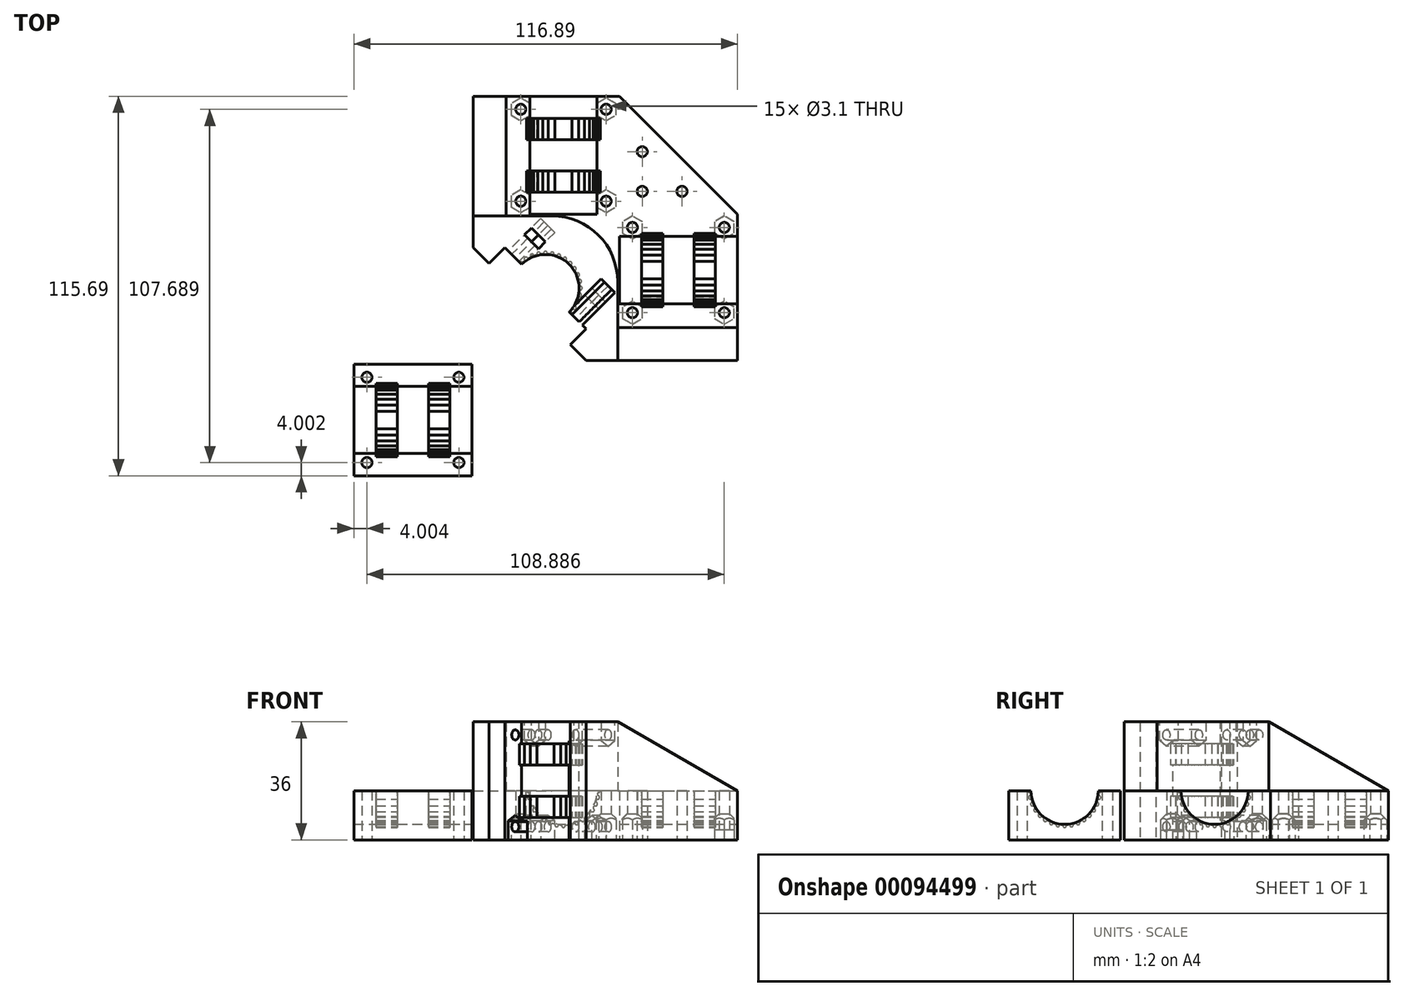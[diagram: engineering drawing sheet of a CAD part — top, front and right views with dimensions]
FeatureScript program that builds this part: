
annotation { "Feature Type Name" : "Feature", "Feature Type Description" : "" }
export const myFeature = defineFeature(function(context is Context, id is Id, definition is map)
    precondition{}
    {
        {
            var Q0;
            Q0=qCreatedBy(makeId("Top.planeOp"),FACE);
            var sketch = newSketch(context, id + "F0", { "sketchPlane" : qUnion([Q0])});
            skLineSegment(sketch, "E0.bottom", {"start": v(34, 0) * mm, "end": v(70, 0) * mm});
            skLineSegment(sketch, "E0.top", {"start": v(34, 34) * mm, "end": v(70, 34) * mm});
            skLineSegment(sketch, "E0.left", {"start": v(34, 0) * mm, "end": v(34, 34) * mm});
            skLineSegment(sketch, "E0.right", {"start": v(70, 0) * mm, "end": v(70, 34) * mm});
            skLineSegment(sketch, "E1", {"start": v(52, 34) * mm, "end": v(52, 0) * mm, "construction": true});
            skLineSegment(sketch, "E2", {"start": v(34, 17) * mm, "end": v(70, 17) * mm, "construction": true});
            skLineSegment(sketch, "E3", {"start": v(34, 34) * mm, "end": v(34, 70) * mm});
            skLineSegment(sketch, "E4", {"start": v(34, 70) * mm, "end": v(0, 70) * mm});
            skLineSegment(sketch, "E5", {"start": v(0, 70) * mm, "end": v(0, 34) * mm});
            skLineSegment(sketch, "E6", {"start": v(0, 34) * mm, "end": v(34, 34) * mm});
            skLineSegment(sketch, "E7", {"start": v(17, 70) * mm, "end": v(17, 34) * mm, "construction": true});
            skLineSegment(sketch, "E8", {"start": v(0, 52) * mm, "end": v(34, 52) * mm, "construction": true});
            skCircle(sketch, "E9", {"center": v(66, 30) * mm, "radius": 1.55 * mm});
            skPoint(sketch, "E10", {"position": v(60, 17) * mm});
            skCircle(sketch, "E11.MirrorC", {"center": v(38, 30) * mm, "radius": 1.55 * mm});
            skPoint(sketch, "E12.MirrorP", {"position": v(44, 17) * mm});
            skCircle(sketch, "E13.MirrorC", {"center": v(38, 4) * mm, "radius": 1.55 * mm});
            skCircle(sketch, "E14.MirrorC", {"center": v(66, 4) * mm, "radius": 1.55 * mm});
            skCircle(sketch, "E15", {"center": v(30, 66) * mm, "radius": 1.55 * mm});
            skPoint(sketch, "E16", {"position": v(17, 60) * mm});
            skCircle(sketch, "E17.MirrorC", {"center": v(4, 66) * mm, "radius": 1.55 * mm});
            skCircle(sketch, "E18.MirrorC", {"center": v(30, 38) * mm, "radius": 1.55 * mm});
            skPoint(sketch, "E19.MirrorP", {"position": v(17, 44) * mm});
            skCircle(sketch, "E20.MirrorC", {"center": v(4, 38) * mm, "radius": 1.55 * mm});
            skLineSegment(sketch, "E21", {"start": v(34, 70) * mm, "end": v(70, 34) * mm});
            skLineSegment(sketch, "E22", {"start": v(0, 70) * mm, "end": v(-0.5, 70) * mm});
            skLineSegment(sketch, "E23", {"start": v(-0.5, 70) * mm, "end": v(-0.5, 34) * mm});
            skLineSegment(sketch, "E24", {"start": v(33.5, -0.5) * mm, "end": v(70, -0.5) * mm});
            skLineSegment(sketch, "E25", {"start": v(70, -0.5) * mm, "end": v(70, 0) * mm});
            skLineSegment(sketch, "E26", {"start": v(-0.5, 34) * mm, "end": v(-0.5, 33.5) * mm});
            skLineSegment(sketch, "E27", {"start": v(-0.5, 33.5) * mm, "end": v(33.5, 33.5) * mm});
            skLineSegment(sketch, "E28", {"start": v(33.5, 33.5) * mm, "end": v(33.5, -0.5) * mm});
            skLineSegment(sketch, "E29", {"start": v(-0.5, 33.5) * mm, "end": v(33.5, -0.5) * mm});
            skLineSegment(sketch, "E30.0", {"start": v(41, 41) * mm, "end": v(41, 53.1) * mm, "construction": true});
            skLineSegment(sketch, "E30.1", {"start": v(41, 41) * mm, "end": v(53.1, 41) * mm, "construction": true});
            skLineSegment(sketch, "E30.2", {"start": v(41, 53.1) * mm, "end": v(53.1, 41) * mm, "construction": true});
            skLineSegment(sketch, "E31", {"start": v(70, -0.5) * mm, "end": v(70, -10.5) * mm});
            skLineSegment(sketch, "E32", {"start": v(70, -10.5) * mm, "end": v(33.5, -10.5) * mm});
            skLineSegment(sketch, "E33", {"start": v(33.5, -10.5) * mm, "end": v(-10.5, 33.5) * mm});
            skLineSegment(sketch, "E34", {"start": v(-10.5, 33.5) * mm, "end": v(-10.5, 70) * mm});
            skLineSegment(sketch, "E35", {"start": v(-10.5, 70) * mm, "end": v(-0.5, 70) * mm});
            skLineSegment(sketch, "E36", {"start": v(34, 34) * mm, "end": v(0, 0) * mm, "construction": true});
            skPoint(sketch, "E37", {"position": v(-0.87, 23.87) * mm});
            skPoint(sketch, "E38.MirrorP", {"position": v(23.87, -0.87) * mm});
            skLineSegment(sketch, "E39", {"start": v(33.5, -10.5) * mm, "end": v(23.87, -10.5) * mm});
            skLineSegment(sketch, "E40", {"start": v(23.87, -10.5) * mm, "end": v(23.87, -0.87) * mm});
            skLineSegment(sketch, "E41", {"start": v(-10.5, 33.5) * mm, "end": v(-10.5, 23.87) * mm});
            skLineSegment(sketch, "E42", {"start": v(-10.5, 23.87) * mm, "end": v(-0.87, 23.87) * mm});
            skLineSegment(sketch, "E43", {"start": v(23.87, -10.5) * mm, "end": v(19.06, -5.69) * mm});
            skLineSegment(sketch, "E44", {"start": v(19.06, -5.69) * mm, "end": v(23.87, -0.87) * mm});
            skLineSegment(sketch, "E45", {"start": v(-10.5, 23.87) * mm, "end": v(-5.69, 19.06) * mm});
            skLineSegment(sketch, "E46", {"start": v(-5.69, 19.06) * mm, "end": v(-0.87, 23.87) * mm});
            skCircle(sketch, "E47", {"center": v(41, 41) * mm, "radius": 1.55 * mm});
            skCircle(sketch, "E48", {"center": v(53.1, 41) * mm, "radius": 1.55 * mm});
            skCircle(sketch, "E49", {"center": v(41, 53.1) * mm, "radius": 1.55 * mm});
            skSolve(sketch);
        }
        {
            var Q0;
            Q0=makeQuery(id+"F0.imprint","IMPRINT",FACE,{"disambiguationData":[TD([[makeQuery(id+"F0.imprint","IMPRINT",EDGE,{"derivedFrom":sQuery(id+"F0.wireOp",EDGE,"E3")}),1.0]])]});
            var Q1;
            Q1=makeQuery(id+"F0.imprint","IMPRINT",FACE,{"disambiguationData":[TD([[makeQuery(id+"F0.imprint","IMPRINT",EDGE,{"derivedFrom":sQuery(id+"F0.wireOp",EDGE,"E0.bottom")}),1.0]])]});
            var Q2;
            Q2=makeQuery(id+"F0.imprint","IMPRINT",FACE,{"disambiguationData":[TD([[makeQuery(id+"F0.imprint","IMPRINT",EDGE,{"derivedFrom":sQuery(id+"F0.wireOp",EDGE,"E0.top")}),1.0]])]});
            var Q3;
            Q3=makeQuery(id+"F0.imprint","IMPRINT",FACE,{"disambiguationData":[TD([[makeQuery(id+"F0.imprint","IMPRINT",EDGE,{"derivedFrom":sQuery(id+"F0.wireOp",EDGE,"E0.bottom")}),-1.0]])]});
            extrude(context, id + "F1", {"entities" : qUnion([Q0, Q1, Q2, Q3]), "depth" : 15 * mm});
        }
        {
            var Q0;
            Q0=makeQuery(id+"F0.imprint","IMPRINT",FACE,{"disambiguationData":[TD([[makeQuery(id+"F0.imprint","IMPRINT",EDGE,{"derivedFrom":sQuery(id+"F0.wireOp",EDGE,"E27")}),-1.0]])]});
            var Q1;
            Q1=makeQuery(id+"F0.imprint","IMPRINT",FACE,{"disambiguationData":[TD([[makeQuery(id+"F0.imprint","IMPRINT",EDGE,{"derivedFrom":sQuery(id+"F0.wireOp",EDGE,"E23")}),-1.0]])]});
            var Q2;
            {var subQ0=sQuery(id+"F0.wireOp",EDGE,"E41");Q2=makeQuery(id+"F0.imprint","IMPRINT",FACE,{"disambiguationData":[TD([[makeQuery(id+"F0.imprint","IMPRINT",EDGE,{"derivedFrom":subQ0}),1.0]])]});}
            var Q3;
            {var subQ0=sQuery(id+"F0.wireOp",EDGE,"E39");Q3=makeQuery(id+"F0.imprint","IMPRINT",FACE,{"disambiguationData":[TD([[makeQuery(id+"F0.imprint","IMPRINT",EDGE,{"derivedFrom":subQ0}),-1.0]])]});}
            var Q4;
            Q4=makeQuery(id+"F0.imprint","IMPRINT",FACE,{"disambiguationData":[TD([[makeQuery(id+"F0.imprint","IMPRINT",EDGE,{"derivedFrom":sQuery(id+"F0.wireOp",EDGE,"E40")}),1.0]])]});
            var Q5;
            Q5=makeQuery(id+"F0.imprint","IMPRINT",FACE,{"disambiguationData":[TD([[makeQuery(id+"F0.imprint","IMPRINT",EDGE,{"derivedFrom":sQuery(id+"F0.wireOp",EDGE,"E42")}),-1.0]])]});
            extrude(context, id + "F2", {"entities" : qUnion([Q0, Q1, Q2, Q3, Q4, Q5]), "operationType" : NewBodyOperationType.ADD, "depth" : 36 * mm});
        }
        {
            var Q0;
            Q0=makeQuery(id+"F1.opExtrude","SWEPT_FACE",FACE,{"disambiguationData":[OSD([sQuery(id+"F0.wireOp",EDGE,"E0.right"),sQuery(id+"F0.wireOp",EDGE,"E25")])]});
            var sketch = newSketch(context, id + "F3", { "sketchPlane" : qUnion([Q0])});
            skLineSegment(sketch, "E50.0", {"start": v(5.55, 15) * mm, "end": v(2.45, 15) * mm});
            skLineSegment(sketch, "E51.0", {"start": v(28.45, 15) * mm, "end": v(31.55, 15) * mm});
            skLineSegment(sketch, "E52", {"start": v(5.55, 15) * mm, "end": v(28.45, 15) * mm});
            skPoint(sketch, "E53", {"position": v(17, 15) * mm});
            skArc(sketch, "E54", {"start": v(6.75, 15) * mm, "mid": v(17, 4.75) * mm, "end": v(27.25, 15) * mm});
            skSolve(sketch);
        }
        {
            var Q0;
            Q0 = qSketchRegion(id + "F3", true);
            var Q1;
            Q1=makeQuery(id+"F2.opExtrude","SWEPT_FACE",FACE,{"disambiguationData":[OSD([sQuery(id+"F0.wireOp",EDGE,"E28")])]});
            extrude(context, id + "F4", {"entities" : qUnion([Q0]), "operationType" : NewBodyOperationType.REMOVE, "oppositeDirection" : true, "endBoundEntityFace" : qUnion([Q1]), "depth" : 36 * mm});
        }
        {
            var Q0;
            Q0=makeQuery(id+"F1.opExtrude","SWEPT_FACE",FACE,{"disambiguationData":[OSD([sQuery(id+"F0.wireOp",EDGE,"E4"),sQuery(id+"F0.wireOp",EDGE,"E22")])]});
            var sketch = newSketch(context, id + "F5", { "sketchPlane" : qUnion([Q0])});
            skLineSegment(sketch, "E55", {"start": v(-28.45, 15) * mm, "end": v(-5.55, 15) * mm});
            skPoint(sketch, "E56.0.start.orphan", {"position": v(-31.55, 15) * mm});
            skPoint(sketch, "E57.0.start.orphan", {"position": v(-2.45, 15) * mm});
            skPoint(sketch, "E58", {"position": v(-17, 15) * mm});
            skArc(sketch, "E59", {"start": v(-27.25, 15) * mm, "mid": v(-17, 4.75) * mm, "end": v(-6.75, 15) * mm});
            skSolve(sketch);
        }
        {
            var Q0;
            Q0 = qSketchRegion(id + "F5", true);
            var Q1;
            Q1=makeQuery(id+"F2.opExtrude","SWEPT_FACE",FACE,{"disambiguationData":[OSD([sQuery(id+"F0.wireOp",EDGE,"E27")])]});
            extrude(context, id + "F6", {"entities" : qUnion([Q0]), "operationType" : NewBodyOperationType.REMOVE, "oppositeDirection" : true, "endBoundEntityFace" : qUnion([Q1]), "depth" : 36 * mm});
        }
        {
            var Q0;
            Q0=makeQuery(id+"F2.opExtrude","CAP_FACE",FACE,{"disambiguationData":[OSD([sQuery(id+"F0.wireOp",EDGE,"E23"),sQuery(id+"F0.wireOp",EDGE,"E24"),sQuery(id+"F0.wireOp",EDGE,"E26"),sQuery(id+"F0.wireOp",EDGE,"E27"),sQuery(id+"F0.wireOp",EDGE,"E28"),sQuery(id+"F0.wireOp",EDGE,"E31"),sQuery(id+"F0.wireOp",EDGE,"E32"),sQuery(id+"F0.wireOp",EDGE,"E33"),sQuery(id+"F0.wireOp",EDGE,"E34"),sQuery(id+"F0.wireOp",EDGE,"E35")])],"isStart":false});
            var sketch = newSketch(context, id + "F7", { "sketchPlane" : qUnion([Q0])});
            skLineSegment(sketch, "E60.0", {"start": v(-0.87, 23.87) * mm, "end": v(23.87, -0.87) * mm});
            skArc(sketch, "E61", {"start": v(18.75, 4.25) * mm, "mid": v(18.75, 18.75) * mm, "end": v(4.25, 18.75) * mm});
            skSolve(sketch);
        }
        {
            var Q0;
            Q0 = qSketchRegion(id + "F7", true);
            var Q1;
            Q1=makeQuery(id+"F2.opExtrude","CAP_FACE",FACE,{"disambiguationData":[OSD([sQuery(id+"F0.wireOp",EDGE,"E27"),sQuery(id+"F0.wireOp",EDGE,"E28"),sQuery(id+"F0.wireOp",EDGE,"E29")])],"isStart":true});
            extrude(context, id + "F8", {"entities" : qUnion([Q0]), "operationType" : NewBodyOperationType.REMOVE, "endBound" : BoundingType.UP_TO_SURFACE, "oppositeDirection" : true, "endBoundEntityFace" : qUnion([Q1]), "depth" : 25 * mm});
        }
        {
            var Q0;
            {var subQ0=sQuery(id+"F0.wireOp",EDGE,"E44");var subQ8=sQuery(id+"F0.wireOp",EDGE,"E33");Q0=makeQuery(id+"F8.boolean.opBoolean","SPLIT",FACE,{"disambiguationData":[TD([makeQuery(id+"F2.opExtrude","SWEPT_FACE",FACE,{"disambiguationData":[OSD([subQ0])]})])],"derivedFrom":makeQuery(id+"F2.opExtrude","SWEPT_FACE",FACE,{"disambiguationData":[OSD([subQ8])]})});}
            cPlane(context, id + "F9", {"entities" : qUnion([Q0]), "cplaneType" : CPlaneType.OFFSET, "offset" : 7 * mm, "oppositeDirection" : true, "width" : 150 * mm, "height" : 150 * mm});
        }
        {
            var Q0;
            Q0=qCreatedBy(id+"F9.planeOp",FACE);
            var sketch = newSketch(context, id + "F10", { "sketchPlane" : qUnion([Q0])});
            skPoint(sketch, "E62.0", {"position": v(-24.04, 36) * mm});
            skPoint(sketch, "E63.0", {"position": v(24.04, 36) * mm});
            skPoint(sketch, "E64.0", {"position": v(24.04, 0) * mm});
            skPoint(sketch, "E65.0", {"position": v(-24.04, 0) * mm});
            skLineSegment(sketch, "E66", {"start": v(-24.04, 0) * mm, "end": v(-24.04, 36) * mm, "construction": true});
            skLineSegment(sketch, "E67", {"start": v(-24.04, 36) * mm, "end": v(24.04, 36) * mm, "construction": true});
            skLineSegment(sketch, "E68", {"start": v(24.04, 36) * mm, "end": v(24.04, 0) * mm, "construction": true});
            skLineSegment(sketch, "E69", {"start": v(24.04, 0) * mm, "end": v(-24.04, 0) * mm, "construction": true});
            skLineSegment(sketch, "E70", {"start": v(0, 0) * mm, "end": v(0, 36) * mm, "construction": true});
            skLineSegment(sketch, "E71", {"start": v(-24.04, 18) * mm, "end": v(24.04, 18) * mm, "construction": true});
            skCircle(sketch, "E72", {"center": v(-13, 32) * mm, "radius": 1.55 * mm});
            skCircle(sketch, "E73.cCircle", {"center": v(-13, 32) * mm, "radius": 3 * mm, "construction": true});
            skLineSegment(sketch, "E73.0", {"start": v(-10, 33.73) * mm, "end": v(-10, 30.27) * mm});
            skLineSegment(sketch, "E73.1", {"start": v(-10, 30.27) * mm, "end": v(-13, 28.54) * mm});
            skLineSegment(sketch, "E73.2", {"start": v(-13, 28.54) * mm, "end": v(-16, 30.27) * mm});
            skLineSegment(sketch, "E73.3", {"start": v(-16, 30.27) * mm, "end": v(-16, 33.73) * mm});
            skLineSegment(sketch, "E73.4", {"start": v(-16, 33.73) * mm, "end": v(-13, 35.46) * mm, "construction": true});
            skLineSegment(sketch, "E73.5", {"start": v(-13, 35.46) * mm, "end": v(-10, 33.73) * mm, "construction": true});
            skPoint(sketch, "E73.0.midPoint", {"position": v(-10, 32) * mm});
            skLineSegment(sketch, "E74", {"start": v(-16, 33.73) * mm, "end": v(-16, 36) * mm});
            skLineSegment(sketch, "E75", {"start": v(-16, 36) * mm, "end": v(-10, 36) * mm});
            skLineSegment(sketch, "E76", {"start": v(-10, 36) * mm, "end": v(-10, 33.73) * mm});
            skCircle(sketch, "E77.MirrorC", {"center": v(-13, 4) * mm, "radius": 1.55 * mm});
            skLineSegment(sketch, "E78.MirrorCS", {"start": v(-16, 2.27) * mm, "end": v(-16, 0) * mm});
            skLineSegment(sketch, "E79.MirrorCS", {"start": v(-16, 5.73) * mm, "end": v(-16, 2.27) * mm});
            skLineSegment(sketch, "E80.MirrorCS", {"start": v(-13, 7.46) * mm, "end": v(-16, 5.73) * mm});
            skLineSegment(sketch, "E81.MirrorCS", {"start": v(-10, 5.73) * mm, "end": v(-13, 7.46) * mm});
            skLineSegment(sketch, "E82.MirrorCS", {"start": v(-10, 2.27) * mm, "end": v(-10, 5.73) * mm});
            skLineSegment(sketch, "E83.MirrorCS", {"start": v(-10, 0) * mm, "end": v(-10, 2.27) * mm});
            skLineSegment(sketch, "E84.MirrorCS", {"start": v(10, 36) * mm, "end": v(10, 33.73) * mm});
            skLineSegment(sketch, "E85.MirrorCS", {"start": v(10, 33.73) * mm, "end": v(10, 30.27) * mm});
            skLineSegment(sketch, "E86.MirrorCS", {"start": v(10, 30.27) * mm, "end": v(13, 28.54) * mm});
            skLineSegment(sketch, "E87.MirrorCS", {"start": v(13, 28.54) * mm, "end": v(16, 30.27) * mm});
            skLineSegment(sketch, "E88.MirrorCS", {"start": v(16, 30.27) * mm, "end": v(16, 33.73) * mm});
            skLineSegment(sketch, "E89.MirrorCS", {"start": v(16, 33.73) * mm, "end": v(16, 36) * mm});
            skCircle(sketch, "E90.MirrorC", {"center": v(13, 32) * mm, "radius": 1.55 * mm});
            skLineSegment(sketch, "E91.MirrorCS", {"start": v(16, 2.27) * mm, "end": v(16, 0) * mm});
            skLineSegment(sketch, "E92.MirrorCS", {"start": v(16, 5.73) * mm, "end": v(16, 2.27) * mm});
            skLineSegment(sketch, "E93.MirrorCS", {"start": v(13, 7.46) * mm, "end": v(16, 5.73) * mm});
            skLineSegment(sketch, "E94.MirrorCS", {"start": v(10, 5.73) * mm, "end": v(13, 7.46) * mm});
            skLineSegment(sketch, "E95.MirrorCS", {"start": v(10, 2.27) * mm, "end": v(10, 5.73) * mm});
            skLineSegment(sketch, "E96.MirrorCS", {"start": v(10, 0) * mm, "end": v(10, 2.27) * mm});
            skCircle(sketch, "E97.MirrorC", {"center": v(13, 4) * mm, "radius": 1.55 * mm});
            skLineSegment(sketch, "E98", {"start": v(-16, 0) * mm, "end": v(-10, 0) * mm});
            skLineSegment(sketch, "E99", {"start": v(10, 0) * mm, "end": v(16, 0) * mm});
            skLineSegment(sketch, "E100", {"start": v(16, 36) * mm, "end": v(10, 36) * mm});
            skLineSegment(sketch, "E101", {"start": v(-13, 32) * mm, "end": v(-13, 36) * mm, "construction": true});
            skLineSegment(sketch, "E102.0", {"start": v(-10.25, 0) * mm, "end": v(-10.25, 36) * mm, "construction": true});
            skLineSegment(sketch, "E103.0", {"start": v(10.25, 0) * mm, "end": v(10.25, 36) * mm, "construction": true});
            skPoint(sketch, "E104", {"position": v(0, 18) * mm});
            skPoint(sketch, "E105", {"position": v(0, 26) * mm});
            skPoint(sketch, "E106.MirrorP", {"position": v(0, 10) * mm});
            skSolve(sketch);
        }
        {
            var Q0;
            Q0=makeQuery(id+"F10.imprint","IMPRINT",FACE,{"disambiguationData":[TD([[makeQuery(id+"F10.imprint","IMPRINT",EDGE,{"derivedFrom":sQuery(id+"F10.wireOp",EDGE,"E72")}),1.0]])]});
            var Q1;
            Q1=makeQuery(id+"F10.imprint","IMPRINT",FACE,{"disambiguationData":[TD([[makeQuery(id+"F10.imprint","IMPRINT",EDGE,{"derivedFrom":sQuery(id+"F10.wireOp",EDGE,"E77.MirrorC")}),-1.0]])]});
            var Q2;
            Q2=makeQuery(id+"F10.imprint","IMPRINT",FACE,{"disambiguationData":[TD([[makeQuery(id+"F10.imprint","IMPRINT",EDGE,{"derivedFrom":sQuery(id+"F10.wireOp",EDGE,"E97.MirrorC")}),1.0]])]});
            var Q3;
            Q3=makeQuery(id+"F10.imprint","IMPRINT",FACE,{"disambiguationData":[TD([[makeQuery(id+"F10.imprint","IMPRINT",EDGE,{"derivedFrom":sQuery(id+"F10.wireOp",EDGE,"E90.MirrorC")}),-1.0]])]});
            extrude(context, id + "F11", {"entities" : qUnion([Q0, Q1, Q2, Q3]), "operationType" : NewBodyOperationType.REMOVE, "oppositeDirection" : true, "depth" : 7 * mm, "hasSecondDirection" : true, "secondDirectionOppositeDirection" : false, "secondDirectionDepth" : 25 * mm});
        }
        {
            var Q0;
            Q0=makeQuery(id+"F10.imprint","IMPRINT",FACE,{"disambiguationData":[TD([[makeQuery(id+"F10.imprint","IMPRINT",EDGE,{"derivedFrom":sQuery(id+"F10.wireOp",EDGE,"E72")}),-1.0]])]});
            var Q1;
            Q1=makeQuery(id+"F10.imprint","IMPRINT",FACE,{"disambiguationData":[TD([[makeQuery(id+"F10.imprint","IMPRINT",EDGE,{"derivedFrom":sQuery(id+"F10.wireOp",EDGE,"E77.MirrorC")}),1.0]])]});
            var Q2;
            Q2=makeQuery(id+"F10.imprint","IMPRINT",FACE,{"disambiguationData":[TD([[makeQuery(id+"F10.imprint","IMPRINT",EDGE,{"derivedFrom":sQuery(id+"F10.wireOp",EDGE,"E91.MirrorCS")}),-1.0]])]});
            var Q3;
            Q3=makeQuery(id+"F10.imprint","IMPRINT",FACE,{"disambiguationData":[TD([[makeQuery(id+"F10.imprint","IMPRINT",EDGE,{"derivedFrom":sQuery(id+"F10.wireOp",EDGE,"E84.MirrorCS")}),1.0]])]});
            extrude(context, id + "F12", {"entities" : qUnion([Q0, Q1, Q2, Q3]), "operationType" : NewBodyOperationType.REMOVE, "oppositeDirection" : true, "depth" : 3 * mm});
        }
        {
            var Q0;
            Q0=makeQuery(id+"F2.opExtrude","SWEPT_FACE",FACE,{"disambiguationData":[OSD([sQuery(id+"F0.wireOp",EDGE,"E24")])]});
            var sketch = newSketch(context, id + "F13", { "sketchPlane" : qUnion([Q0])});
            skLineSegment(sketch, "E107", {"start": v(-33.5, 36) * mm, "end": v(-70, 15) * mm});
            skLineSegment(sketch, "E108.0", {"start": v(-33.5, 36) * mm, "end": v(-70, 36) * mm});
            skLineSegment(sketch, "E109.0", {"start": v(-70, 36) * mm, "end": v(-70, 15) * mm});
            skSolve(sketch);
        }
        {
            var Q0;
            Q0 = qSketchRegion(id + "F13", true);
            var Q1;
            Q1=makeQuery(id+"F2.opExtrude","SWEPT_FACE",FACE,{"disambiguationData":[OSD([sQuery(id+"F0.wireOp",EDGE,"E32"),sQuery(id+"F0.wireOp",EDGE,"E39")])]});
            extrude(context, id + "F14", {"entities" : qUnion([Q0]), "operationType" : NewBodyOperationType.REMOVE, "endBound" : BoundingType.UP_TO_SURFACE, "oppositeDirection" : true, "endBoundEntityFace" : qUnion([Q1]), "depth" : 25 * mm});
        }
        {
            var Q0;
            Q0=makeQuery(id+"F2.opExtrude","SWEPT_FACE",FACE,{"disambiguationData":[OSD([sQuery(id+"F0.wireOp",EDGE,"E23"),sQuery(id+"F0.wireOp",EDGE,"E26")])]});
            var sketch = newSketch(context, id + "F15", { "sketchPlane" : qUnion([Q0])});
            skLineSegment(sketch, "E110.0", {"start": v(70, 36) * mm, "end": v(33.5, 36) * mm});
            skLineSegment(sketch, "E111.0", {"start": v(70, 36) * mm, "end": v(70, 15) * mm});
            skLineSegment(sketch, "E112", {"start": v(33.5, 36) * mm, "end": v(70, 15) * mm});
            skSolve(sketch);
        }
        {
            var Q0;
            Q0 = qSketchRegion(id + "F15", true);
            var Q1;
            Q1=makeQuery(id+"F2.opExtrude","SWEPT_FACE",FACE,{"disambiguationData":[OSD([sQuery(id+"F0.wireOp",EDGE,"E34"),sQuery(id+"F0.wireOp",EDGE,"E41")])]});
            extrude(context, id + "F16", {"entities" : qUnion([Q0]), "operationType" : NewBodyOperationType.REMOVE, "endBound" : BoundingType.UP_TO_SURFACE, "oppositeDirection" : true, "endBoundEntityFace" : qUnion([Q1]), "depth" : 25 * mm});
        }
        {
            var Q0;
            Q0=makeQuery(id+"F2.opExtrude","SWEPT_EDGE",EDGE,{"disambiguationData":[OSD([sQuery(id+"F0.wireOp",EDGE,"E27"),sQuery(id+"F0.wireOp",EDGE,"E28")])]});
            fillet(context, id + "F17", {"entities" : qUnion([Q0]), "radius" : 20 * mm, "tangentPropagation" : true, "allowEdgeOverflow" : false});
        }
        {
            var Q0;
            {var subQ0=sQuery(id+"F0.wireOp",EDGE,"E28");var subQ1=sQuery(id+"F0.wireOp",EDGE,"E27");var subQ2=sQuery(id+"F0.wireOp",EDGE,"E26");var subQ3=sQuery(id+"F0.wireOp",EDGE,"E24");var subQ4=sQuery(id+"F0.wireOp",EDGE,"E23");Q0=makeQuery(id+"F2.boolean.opBoolean","MERGE",FACE,{"derivedFrom":[makeQuery(id+"F1.opExtrude","CAP_FACE",FACE,{"disambiguationData":[OSD([sQuery(id+"F0.wireOp",EDGE,"E0.right"),sQuery(id+"F0.wireOp",EDGE,"E4"),sQuery(id+"F0.wireOp",EDGE,"E9"),sQuery(id+"F0.wireOp",EDGE,"E11.MirrorC"),sQuery(id+"F0.wireOp",EDGE,"E13.MirrorC"),sQuery(id+"F0.wireOp",EDGE,"E14.MirrorC"),sQuery(id+"F0.wireOp",EDGE,"E15"),sQuery(id+"F0.wireOp",EDGE,"E17.MirrorC"),sQuery(id+"F0.wireOp",EDGE,"E18.MirrorC"),sQuery(id+"F0.wireOp",EDGE,"E20.MirrorC"),sQuery(id+"F0.wireOp",EDGE,"E21"),sQuery(id+"F0.wireOp",EDGE,"E22"),subQ4,subQ3,sQuery(id+"F0.wireOp",EDGE,"E25"),subQ2,subQ1,subQ0,sQuery(id+"F0.wireOp",EDGE,"E30.0"),sQuery(id+"F0.wireOp",EDGE,"E30.1"),sQuery(id+"F0.wireOp",EDGE,"E30.2")])],"isStart":true}),makeQuery(id+"F2.opExtrude","CAP_FACE",FACE,{"disambiguationData":[OSD([subQ4,subQ3,subQ2,subQ1,subQ0,sQuery(id+"F0.wireOp",EDGE,"E31"),sQuery(id+"F0.wireOp",EDGE,"E32"),sQuery(id+"F0.wireOp",EDGE,"E33"),sQuery(id+"F0.wireOp",EDGE,"E34"),sQuery(id+"F0.wireOp",EDGE,"E35"),sQuery(id+"F0.wireOp",EDGE,"E39"),sQuery(id+"F0.wireOp",EDGE,"E41"),sQuery(id+"F0.wireOp",EDGE,"E43"),sQuery(id+"F0.wireOp",EDGE,"E44"),sQuery(id+"F0.wireOp",EDGE,"E45"),sQuery(id+"F0.wireOp",EDGE,"E46")])],"isStart":true})]});}
            var sketch = newSketch(context, id + "F18", { "sketchPlane" : qUnion([Q0])});
            skCircle(sketch, "E113.0", {"center": v(66, -4) * mm, "radius": 1.55 * mm});
            skCircle(sketch, "E114.0", {"center": v(66, -30) * mm, "radius": 1.55 * mm, "construction": true});
            skCircle(sketch, "E115.0", {"center": v(38, -4) * mm, "radius": 1.55 * mm, "construction": true});
            skCircle(sketch, "E116.0", {"center": v(38, -30) * mm, "radius": 1.55 * mm, "construction": true});
            skCircle(sketch, "E117.0", {"center": v(30, -38) * mm, "radius": 1.55 * mm, "construction": true});
            skCircle(sketch, "E118.0", {"center": v(30, -66) * mm, "radius": 1.55 * mm, "construction": true});
            skCircle(sketch, "E119.0", {"center": v(4, -66) * mm, "radius": 1.55 * mm, "construction": true});
            skCircle(sketch, "E120.0", {"center": v(4, -38) * mm, "radius": 1.55 * mm, "construction": true});
            skCircle(sketch, "E121.cCircle", {"center": v(66, -4) * mm, "radius": 3 * mm, "construction": true});
            skLineSegment(sketch, "E121.0", {"start": v(66, -7.46) * mm, "end": v(63, -5.73) * mm});
            skLineSegment(sketch, "E121.1", {"start": v(63, -5.73) * mm, "end": v(63, -2.27) * mm});
            skLineSegment(sketch, "E121.2", {"start": v(63, -2.27) * mm, "end": v(66, -0.54) * mm});
            skLineSegment(sketch, "E121.3", {"start": v(66, -0.54) * mm, "end": v(69, -2.27) * mm});
            skLineSegment(sketch, "E121.4", {"start": v(69, -2.27) * mm, "end": v(69, -5.73) * mm});
            skLineSegment(sketch, "E121.5", {"start": v(69, -5.73) * mm, "end": v(66, -7.46) * mm});
            skPoint(sketch, "E121.0.midPoint", {"position": v(64.5, -6.6) * mm});
            skCircle(sketch, "E122.cCircle", {"center": v(66, -30) * mm, "radius": 3 * mm, "construction": true});
            skLineSegment(sketch, "E122.0", {"start": v(63, -31.73) * mm, "end": v(63, -28.27) * mm});
            skLineSegment(sketch, "E122.1", {"start": v(63, -28.27) * mm, "end": v(66, -26.54) * mm});
            skLineSegment(sketch, "E122.2", {"start": v(66, -26.54) * mm, "end": v(69, -28.27) * mm});
            skLineSegment(sketch, "E122.3", {"start": v(69, -28.27) * mm, "end": v(69, -31.73) * mm});
            skLineSegment(sketch, "E122.4", {"start": v(69, -31.73) * mm, "end": v(66, -33.46) * mm});
            skLineSegment(sketch, "E122.5", {"start": v(66, -33.46) * mm, "end": v(63, -31.73) * mm});
            skPoint(sketch, "E122.0.midPoint", {"position": v(63, -30) * mm});
            skCircle(sketch, "E123.cCircle", {"center": v(38, -4) * mm, "radius": 3 * mm, "construction": true});
            skLineSegment(sketch, "E123.0", {"start": v(35, -5.73) * mm, "end": v(35, -2.27) * mm});
            skLineSegment(sketch, "E123.1", {"start": v(35, -2.27) * mm, "end": v(38, -0.54) * mm});
            skLineSegment(sketch, "E123.2", {"start": v(38, -0.54) * mm, "end": v(41, -2.27) * mm});
            skLineSegment(sketch, "E123.3", {"start": v(41, -2.27) * mm, "end": v(41, -5.73) * mm});
            skLineSegment(sketch, "E123.4", {"start": v(41, -5.73) * mm, "end": v(38, -7.46) * mm});
            skLineSegment(sketch, "E123.5", {"start": v(38, -7.46) * mm, "end": v(35, -5.73) * mm});
            skPoint(sketch, "E123.0.midPoint", {"position": v(35, -4) * mm});
            skCircle(sketch, "E124.cCircle", {"center": v(38, -30) * mm, "radius": 3 * mm, "construction": true});
            skLineSegment(sketch, "E124.0", {"start": v(35, -31.73) * mm, "end": v(35, -28.27) * mm});
            skLineSegment(sketch, "E124.1", {"start": v(35, -28.27) * mm, "end": v(38, -26.54) * mm});
            skLineSegment(sketch, "E124.2", {"start": v(38, -26.54) * mm, "end": v(41, -28.27) * mm});
            skLineSegment(sketch, "E124.3", {"start": v(41, -28.27) * mm, "end": v(41, -31.73) * mm});
            skLineSegment(sketch, "E124.4", {"start": v(41, -31.73) * mm, "end": v(38, -33.46) * mm});
            skLineSegment(sketch, "E124.5", {"start": v(38, -33.46) * mm, "end": v(35, -31.73) * mm});
            skPoint(sketch, "E124.0.midPoint", {"position": v(35, -30) * mm});
            skCircle(sketch, "E125.cCircle", {"center": v(30, -38) * mm, "radius": 3 * mm, "construction": true});
            skLineSegment(sketch, "E125.0", {"start": v(27, -39.73) * mm, "end": v(27, -36.27) * mm});
            skLineSegment(sketch, "E125.1", {"start": v(27, -36.27) * mm, "end": v(30, -34.54) * mm});
            skLineSegment(sketch, "E125.2", {"start": v(30, -34.54) * mm, "end": v(33, -36.27) * mm});
            skLineSegment(sketch, "E125.3", {"start": v(33, -36.27) * mm, "end": v(33, -39.73) * mm});
            skLineSegment(sketch, "E125.4", {"start": v(33, -39.73) * mm, "end": v(30, -41.46) * mm});
            skLineSegment(sketch, "E125.5", {"start": v(30, -41.46) * mm, "end": v(27, -39.73) * mm});
            skPoint(sketch, "E125.0.midPoint", {"position": v(27, -38) * mm});
            skCircle(sketch, "E126.cCircle", {"center": v(4, -38) * mm, "radius": 3 * mm, "construction": true});
            skLineSegment(sketch, "E126.0", {"start": v(1, -39.73) * mm, "end": v(1, -36.27) * mm});
            skLineSegment(sketch, "E126.1", {"start": v(1, -36.27) * mm, "end": v(4, -34.54) * mm});
            skLineSegment(sketch, "E126.2", {"start": v(4, -34.54) * mm, "end": v(7, -36.27) * mm});
            skLineSegment(sketch, "E126.3", {"start": v(7, -36.27) * mm, "end": v(7, -39.73) * mm});
            skLineSegment(sketch, "E126.4", {"start": v(7, -39.73) * mm, "end": v(4, -41.46) * mm});
            skLineSegment(sketch, "E126.5", {"start": v(4, -41.46) * mm, "end": v(1, -39.73) * mm});
            skPoint(sketch, "E126.0.midPoint", {"position": v(1, -38) * mm});
            skCircle(sketch, "E127.cCircle", {"center": v(4, -66) * mm, "radius": 3 * mm, "construction": true});
            skLineSegment(sketch, "E127.0", {"start": v(1, -67.73) * mm, "end": v(1, -64.27) * mm});
            skLineSegment(sketch, "E127.1", {"start": v(1, -64.27) * mm, "end": v(4, -62.54) * mm});
            skLineSegment(sketch, "E127.2", {"start": v(4, -62.54) * mm, "end": v(7, -64.27) * mm});
            skLineSegment(sketch, "E127.3", {"start": v(7, -64.27) * mm, "end": v(7, -67.73) * mm});
            skLineSegment(sketch, "E127.4", {"start": v(7, -67.73) * mm, "end": v(4, -69.46) * mm});
            skLineSegment(sketch, "E127.5", {"start": v(4, -69.46) * mm, "end": v(1, -67.73) * mm});
            skPoint(sketch, "E127.0.midPoint", {"position": v(1, -66) * mm});
            skCircle(sketch, "E128.cCircle", {"center": v(30, -66) * mm, "radius": 3 * mm, "construction": true});
            skLineSegment(sketch, "E128.0", {"start": v(27, -67.73) * mm, "end": v(27, -64.27) * mm});
            skLineSegment(sketch, "E128.1", {"start": v(27, -64.27) * mm, "end": v(30, -62.54) * mm});
            skLineSegment(sketch, "E128.2", {"start": v(30, -62.54) * mm, "end": v(33, -64.27) * mm});
            skLineSegment(sketch, "E128.3", {"start": v(33, -64.27) * mm, "end": v(33, -67.73) * mm});
            skLineSegment(sketch, "E128.4", {"start": v(33, -67.73) * mm, "end": v(30, -69.46) * mm});
            skLineSegment(sketch, "E128.5", {"start": v(30, -69.46) * mm, "end": v(27, -67.73) * mm});
            skPoint(sketch, "E128.0.midPoint", {"position": v(27, -66) * mm});
            skSolve(sketch);
        }
        {
            var Q0;
            Q0 = qSketchRegion(id + "F18", true);
            extrude(context, id + "F19", {"entities" : qUnion([Q0]), "operationType" : NewBodyOperationType.REMOVE, "oppositeDirection" : true, "depth" : 3 * mm});
        }
        {
            var Q0;
            Q0=makeQuery(id+"F19.boolean.opBoolean","COPY",EDGE,{"derivedFrom":makeQuery(id+"F19.opExtrude","CAP_EDGE",EDGE,{"disambiguationData":[OSD([sQuery(id+"F18.wireOp",EDGE,"E113.0")])],"isStart":false})});
            var Q1;
            Q1=makeQuery(id+"F19.boolean.opBoolean","INTERSECT",EDGE,{"derivedFrom":[makeQuery(id+"F1.opExtrude","SWEPT_FACE",FACE,{"disambiguationData":[OSD([sQuery(id+"F0.wireOp",EDGE,"E9")])]}),makeQuery(id+"F19.opExtrude","CAP_FACE",FACE,{"disambiguationData":[OSD([sQuery(id+"F18.wireOp",EDGE,"E122.0"),sQuery(id+"F18.wireOp",EDGE,"E122.1"),sQuery(id+"F18.wireOp",EDGE,"E122.2"),sQuery(id+"F18.wireOp",EDGE,"E122.3"),sQuery(id+"F18.wireOp",EDGE,"E122.4"),sQuery(id+"F18.wireOp",EDGE,"E122.5")])],"isStart":false})]});
            var Q2;
            Q2=makeQuery(id+"F19.boolean.opBoolean","INTERSECT",EDGE,{"derivedFrom":[makeQuery(id+"F1.opExtrude","SWEPT_FACE",FACE,{"disambiguationData":[OSD([sQuery(id+"F0.wireOp",EDGE,"E13.MirrorC")])]}),makeQuery(id+"F19.opExtrude","CAP_FACE",FACE,{"disambiguationData":[OSD([sQuery(id+"F18.wireOp",EDGE,"E123.0"),sQuery(id+"F18.wireOp",EDGE,"E123.1"),sQuery(id+"F18.wireOp",EDGE,"E123.2"),sQuery(id+"F18.wireOp",EDGE,"E123.3"),sQuery(id+"F18.wireOp",EDGE,"E123.4"),sQuery(id+"F18.wireOp",EDGE,"E123.5")])],"isStart":false})]});
            var Q3;
            Q3=makeQuery(id+"F19.boolean.opBoolean","INTERSECT",EDGE,{"derivedFrom":[makeQuery(id+"F1.opExtrude","SWEPT_FACE",FACE,{"disambiguationData":[OSD([sQuery(id+"F0.wireOp",EDGE,"E11.MirrorC")])]}),makeQuery(id+"F19.opExtrude","CAP_FACE",FACE,{"disambiguationData":[OSD([sQuery(id+"F18.wireOp",EDGE,"E124.0"),sQuery(id+"F18.wireOp",EDGE,"E124.1"),sQuery(id+"F18.wireOp",EDGE,"E124.2"),sQuery(id+"F18.wireOp",EDGE,"E124.3"),sQuery(id+"F18.wireOp",EDGE,"E124.4"),sQuery(id+"F18.wireOp",EDGE,"E124.5")])],"isStart":false})]});
            var Q4;
            Q4=makeQuery(id+"F19.boolean.opBoolean","INTERSECT",EDGE,{"derivedFrom":[makeQuery(id+"F1.opExtrude","SWEPT_FACE",FACE,{"disambiguationData":[OSD([sQuery(id+"F0.wireOp",EDGE,"E18.MirrorC")])]}),makeQuery(id+"F19.opExtrude","CAP_FACE",FACE,{"disambiguationData":[OSD([sQuery(id+"F18.wireOp",EDGE,"E125.0"),sQuery(id+"F18.wireOp",EDGE,"E125.1"),sQuery(id+"F18.wireOp",EDGE,"E125.2"),sQuery(id+"F18.wireOp",EDGE,"E125.3"),sQuery(id+"F18.wireOp",EDGE,"E125.4"),sQuery(id+"F18.wireOp",EDGE,"E125.5")])],"isStart":false})]});
            var Q5;
            Q5=makeQuery(id+"F19.boolean.opBoolean","INTERSECT",EDGE,{"derivedFrom":[makeQuery(id+"F1.opExtrude","SWEPT_FACE",FACE,{"disambiguationData":[OSD([sQuery(id+"F0.wireOp",EDGE,"E15")])]}),makeQuery(id+"F19.opExtrude","CAP_FACE",FACE,{"disambiguationData":[OSD([sQuery(id+"F18.wireOp",EDGE,"E128.0"),sQuery(id+"F18.wireOp",EDGE,"E128.1"),sQuery(id+"F18.wireOp",EDGE,"E128.2"),sQuery(id+"F18.wireOp",EDGE,"E128.3"),sQuery(id+"F18.wireOp",EDGE,"E128.4"),sQuery(id+"F18.wireOp",EDGE,"E128.5")])],"isStart":false})]});
            var Q6;
            Q6=makeQuery(id+"F19.boolean.opBoolean","INTERSECT",EDGE,{"derivedFrom":[makeQuery(id+"F1.opExtrude","SWEPT_FACE",FACE,{"disambiguationData":[OSD([sQuery(id+"F0.wireOp",EDGE,"E17.MirrorC")])]}),makeQuery(id+"F19.opExtrude","CAP_FACE",FACE,{"disambiguationData":[OSD([sQuery(id+"F18.wireOp",EDGE,"E127.0"),sQuery(id+"F18.wireOp",EDGE,"E127.1"),sQuery(id+"F18.wireOp",EDGE,"E127.2"),sQuery(id+"F18.wireOp",EDGE,"E127.3"),sQuery(id+"F18.wireOp",EDGE,"E127.4"),sQuery(id+"F18.wireOp",EDGE,"E127.5")])],"isStart":false})]});
            var Q7;
            Q7=makeQuery(id+"F19.boolean.opBoolean","INTERSECT",EDGE,{"derivedFrom":[makeQuery(id+"F1.opExtrude","SWEPT_FACE",FACE,{"disambiguationData":[OSD([sQuery(id+"F0.wireOp",EDGE,"E20.MirrorC")])]}),makeQuery(id+"F19.opExtrude","CAP_FACE",FACE,{"disambiguationData":[OSD([sQuery(id+"F18.wireOp",EDGE,"E126.0"),sQuery(id+"F18.wireOp",EDGE,"E126.1"),sQuery(id+"F18.wireOp",EDGE,"E126.2"),sQuery(id+"F18.wireOp",EDGE,"E126.3"),sQuery(id+"F18.wireOp",EDGE,"E126.4"),sQuery(id+"F18.wireOp",EDGE,"E126.5")])],"isStart":false})]});
            chamfer(context, id + "F20", {"entities" : qUnion([Q0, Q1, Q2, Q3, Q4, Q5, Q6, Q7]), "width" : 5 * mm, "tangentPropagation" : true});
        }
        {
            var Q0;
            Q0=qCreatedBy(makeId("Right.planeOp"),FACE);
            var Q1;
            Q1=sQuery(id+"F0.wireOp",VERTEX,"E10");
            cPlane(context, id + "F21", {"entities" : qUnion([Q0, Q1]), "cplaneType" : CPlaneType.PLANE_POINT, "offset" : 150 * mm, "width" : 150 * mm, "height" : 150 * mm});
        }
        {
            var Q0;
            Q0=qCreatedBy(id+"F21.planeOp",FACE);
            var sketch = newSketch(context, id + "F22", { "sketchPlane" : qUnion([Q0])});
            skLineSegment(sketch, "E129", {"start": v(17, 12.16) * mm, "end": v(17, 9.53) * mm, "construction": true});
            skArc(sketch, "E130", {"start": v(17, 26.2) * mm, "mid": v(17.3, 26.12) * mm, "end": v(17.5, 25.9) * mm});
            skArc(sketch, "E131", {"start": v(17.5, 25.9) * mm, "mid": v(17.56, 25.74) * mm, "end": v(17.6, 25.58) * mm});
            skArc(sketch, "E132", {"start": v(17.6, 25.58) * mm, "mid": v(17.64, 25.5) * mm, "end": v(17.73, 25.45) * mm});
            skPoint(sketch, "E133", {"position": v(17, 24.82) * mm});
            skPoint(sketch, "E134", {"position": v(17, 25.45) * mm});
            skPoint(sketch, "E135", {"position": v(17, 25.2) * mm});
            skArc(sketch, "E136", {"start": v(17, 25.2) * mm, "mid": v(17.5, 25.19) * mm, "end": v(18, 25.15) * mm, "construction": true});
            skLineSegment(sketch, "E137", {"start": v(17.96, 24.78) * mm, "end": v(18.03, 25.43) * mm});
            skArc(sketch, "E138", {"start": v(17.73, 25.45) * mm, "mid": v(17.88, 25.44) * mm, "end": v(18.03, 25.43) * mm});
            skArc(sketch, "E139", {"start": v(17, 24.82) * mm, "mid": v(17.48, 24.81) * mm, "end": v(17.96, 24.78) * mm});
            skArc(sketch, "E140.MirrorCS", {"start": v(17, 26.2) * mm, "mid": v(16.7, 26.12) * mm, "end": v(16.5, 25.9) * mm});
            skArc(sketch, "E141.MirrorCS", {"start": v(16.5, 25.9) * mm, "mid": v(16.44, 25.74) * mm, "end": v(16.4, 25.58) * mm});
            skArc(sketch, "E142.MirrorCS", {"start": v(16.4, 25.58) * mm, "mid": v(16.36, 25.5) * mm, "end": v(16.27, 25.45) * mm});
            skArc(sketch, "E143.MirrorCS", {"start": v(16.27, 25.45) * mm, "mid": v(16.12, 25.44) * mm, "end": v(15.97, 25.43) * mm});
            skLineSegment(sketch, "E144.MirrorCS", {"start": v(16.04, 24.78) * mm, "end": v(15.97, 25.43) * mm});
            skArc(sketch, "E145.MirrorCS", {"start": v(17, 24.82) * mm, "mid": v(16.52, 24.81) * mm, "end": v(16.04, 24.78) * mm});
            skArc(sketch, "E146.1.0", {"start": v(14.39, 25.59) * mm, "mid": v(14.36, 25.43) * mm, "end": v(14.36, 25.27) * mm});
            skArc(sketch, "E146.1.1", {"start": v(14.81, 25.99) * mm, "mid": v(14.54, 25.85) * mm, "end": v(14.39, 25.59) * mm});
            skArc(sketch, "E146.1.2", {"start": v(15.08, 24.64) * mm, "mid": v(15.56, 24.72) * mm, "end": v(16.04, 24.78) * mm});
            skPoint(sketch, "E146.1.3", {"position": v(14.96, 25.25) * mm});
            skArc(sketch, "E146.1.4", {"start": v(15.36, 25.78) * mm, "mid": v(15.45, 25.64) * mm, "end": v(15.52, 25.5) * mm});
            skLineSegment(sketch, "E146.1.5", {"start": v(14.15, 24.4) * mm, "end": v(13.96, 25.03) * mm});
            skArc(sketch, "E146.1.6", {"start": v(15.68, 25.4) * mm, "mid": v(15.82, 25.41) * mm, "end": v(15.97, 25.43) * mm});
            skArc(sketch, "E146.1.8", {"start": v(14.81, 25.99) * mm, "mid": v(15.12, 25.96) * mm, "end": v(15.36, 25.78) * mm});
            skPoint(sketch, "E146.1.9", {"position": v(15.08, 24.64) * mm});
            skArc(sketch, "E146.1.10", {"start": v(15.01, 25) * mm, "mid": v(15.5, 25.09) * mm, "end": v(16, 25.15) * mm, "construction": true});
            skArc(sketch, "E146.1.11", {"start": v(15.08, 24.64) * mm, "mid": v(14.61, 24.53) * mm, "end": v(14.15, 24.4) * mm});
            skPoint(sketch, "E146.1.12", {"position": v(15.01, 25) * mm});
            skArc(sketch, "E146.1.13", {"start": v(14.24, 25.11) * mm, "mid": v(14.1, 25.07) * mm, "end": v(13.96, 25.03) * mm});
            skArc(sketch, "E146.1.14", {"start": v(15.52, 25.5) * mm, "mid": v(15.58, 25.42) * mm, "end": v(15.68, 25.4) * mm});
            skArc(sketch, "E146.1.15", {"start": v(14.36, 25.27) * mm, "mid": v(14.33, 25.17) * mm, "end": v(14.24, 25.11) * mm});
            skArc(sketch, "E146.2.0", {"start": v(12.37, 24.87) * mm, "mid": v(12.37, 24.71) * mm, "end": v(12.4, 24.55) * mm});
            skArc(sketch, "E146.2.1", {"start": v(12.71, 25.35) * mm, "mid": v(12.47, 25.16) * mm, "end": v(12.37, 24.87) * mm});
            skArc(sketch, "E146.2.2", {"start": v(13.24, 24.08) * mm, "mid": v(13.7, 24.25) * mm, "end": v(14.15, 24.4) * mm});
            skPoint(sketch, "E146.2.3", {"position": v(13, 24.66) * mm});
            skArc(sketch, "E146.2.4", {"start": v(13.3, 25.25) * mm, "mid": v(13.4, 25.14) * mm, "end": v(13.5, 25) * mm});
            skLineSegment(sketch, "E146.2.5", {"start": v(12.37, 23.66) * mm, "end": v(12.06, 24.24) * mm});
            skArc(sketch, "E146.2.6", {"start": v(13.67, 24.94) * mm, "mid": v(13.82, 24.98) * mm, "end": v(13.96, 25.03) * mm});
            skLineSegment(sketch, "E146.2.7", {"start": v(14.15, 24.4) * mm, "end": v(13.96, 25.03) * mm});
            skArc(sketch, "E146.2.8", {"start": v(12.71, 25.35) * mm, "mid": v(13.02, 25.39) * mm, "end": v(13.3, 25.25) * mm});
            skPoint(sketch, "E146.2.9", {"position": v(13.24, 24.08) * mm});
            skArc(sketch, "E146.2.10", {"start": v(13.1, 24.42) * mm, "mid": v(13.56, 24.6) * mm, "end": v(14.04, 24.76) * mm, "construction": true});
            skArc(sketch, "E146.2.11", {"start": v(13.24, 24.08) * mm, "mid": v(12.8, 23.88) * mm, "end": v(12.37, 23.66) * mm});
            skPoint(sketch, "E146.2.12", {"position": v(13.1, 24.42) * mm});
            skArc(sketch, "E146.2.13", {"start": v(12.33, 24.38) * mm, "mid": v(12.2, 24.31) * mm, "end": v(12.06, 24.24) * mm});
            skArc(sketch, "E146.2.14", {"start": v(13.5, 25) * mm, "mid": v(13.57, 24.94) * mm, "end": v(13.67, 24.94) * mm});
            skArc(sketch, "E146.2.15", {"start": v(12.4, 24.55) * mm, "mid": v(12.4, 24.45) * mm, "end": v(12.33, 24.38) * mm});
            skArc(sketch, "E146.3.0", {"start": v(10.53, 23.78) * mm, "mid": v(10.57, 23.62) * mm, "end": v(10.63, 23.47) * mm});
            skArc(sketch, "E146.3.1", {"start": v(10.78, 24.32) * mm, "mid": v(10.58, 24.08) * mm, "end": v(10.53, 23.78) * mm});
            skArc(sketch, "E146.3.2", {"start": v(11.54, 23.17) * mm, "mid": v(11.95, 23.43) * mm, "end": v(12.37, 23.66) * mm});
            skPoint(sketch, "E146.3.3", {"position": v(11.2, 23.7) * mm});
            skArc(sketch, "E146.3.4", {"start": v(11.36, 24.33) * mm, "mid": v(11.5, 24.24) * mm, "end": v(11.61, 24.13) * mm});
            skLineSegment(sketch, "E146.3.5", {"start": v(10.77, 22.6) * mm, "end": v(10.35, 23.1) * mm});
            skArc(sketch, "E146.3.6", {"start": v(11.8, 24.1) * mm, "mid": v(11.93, 24.17) * mm, "end": v(12.06, 24.24) * mm});
            skLineSegment(sketch, "E146.3.7", {"start": v(12.37, 23.66) * mm, "end": v(12.06, 24.24) * mm});
            skArc(sketch, "E146.3.8", {"start": v(10.78, 24.32) * mm, "mid": v(11.07, 24.4) * mm, "end": v(11.36, 24.33) * mm});
            skPoint(sketch, "E146.3.9", {"position": v(11.54, 23.17) * mm});
            skArc(sketch, "E146.3.10", {"start": v(11.33, 23.48) * mm, "mid": v(11.76, 23.75) * mm, "end": v(12.2, 24) * mm, "construction": true});
            skArc(sketch, "E146.3.11", {"start": v(11.54, 23.17) * mm, "mid": v(11.15, 22.9) * mm, "end": v(10.77, 22.6) * mm});
            skPoint(sketch, "E146.3.12", {"position": v(11.33, 23.48) * mm});
            skArc(sketch, "E146.3.13", {"start": v(10.59, 23.29) * mm, "mid": v(10.47, 23.2) * mm, "end": v(10.35, 23.1) * mm});
            skArc(sketch, "E146.3.14", {"start": v(11.61, 24.13) * mm, "mid": v(11.7, 24.08) * mm, "end": v(11.8, 24.1) * mm});
            skArc(sketch, "E146.3.15", {"start": v(10.63, 23.47) * mm, "mid": v(10.64, 23.37) * mm, "end": v(10.59, 23.29) * mm});
            skArc(sketch, "E146.4.0", {"start": v(8.95, 22.35) * mm, "mid": v(9, 22.2) * mm, "end": v(9.1, 22.07) * mm});
            skArc(sketch, "E146.4.1", {"start": v(9.08, 22.92) * mm, "mid": v(8.93, 22.65) * mm, "end": v(8.95, 22.35) * mm});
            skArc(sketch, "E146.4.2", {"start": v(10.05, 21.95) * mm, "mid": v(10.4, 22.28) * mm, "end": v(10.77, 22.6) * mm});
            skPoint(sketch, "E146.4.3", {"position": v(9.6, 22.4) * mm});
            skArc(sketch, "E146.4.4", {"start": v(9.65, 23.05) * mm, "mid": v(9.8, 23) * mm, "end": v(9.93, 22.9) * mm});
            skLineSegment(sketch, "E146.4.5", {"start": v(9.4, 21.23) * mm, "end": v(8.9, 21.65) * mm});
            skArc(sketch, "E146.4.6", {"start": v(10.12, 22.9) * mm, "mid": v(10.24, 23) * mm, "end": v(10.35, 23.1) * mm});
            skLineSegment(sketch, "E146.4.7", {"start": v(10.77, 22.6) * mm, "end": v(10.35, 23.1) * mm});
            skArc(sketch, "E146.4.8", {"start": v(9.08, 22.92) * mm, "mid": v(9.35, 23.07) * mm, "end": v(9.65, 23.05) * mm});
            skPoint(sketch, "E146.4.9", {"position": v(10.05, 21.95) * mm});
            skArc(sketch, "E146.4.10", {"start": v(9.79, 22.21) * mm, "mid": v(10.15, 22.56) * mm, "end": v(10.53, 22.88) * mm, "construction": true});
            skArc(sketch, "E146.4.11", {"start": v(10.05, 21.95) * mm, "mid": v(9.72, 21.6) * mm, "end": v(9.4, 21.23) * mm});
            skPoint(sketch, "E146.4.12", {"position": v(9.79, 22.21) * mm});
            skArc(sketch, "E146.4.13", {"start": v(9.1, 21.88) * mm, "mid": v(9, 21.76) * mm, "end": v(8.9, 21.65) * mm});
            skArc(sketch, "E146.4.14", {"start": v(9.93, 22.9) * mm, "mid": v(10.03, 22.87) * mm, "end": v(10.12, 22.9) * mm});
            skArc(sketch, "E146.4.15", {"start": v(9.1, 22.07) * mm, "mid": v(9.13, 21.97) * mm, "end": v(9.1, 21.88) * mm});
            skArc(sketch, "E146.5.0", {"start": v(7.67, 20.64) * mm, "mid": v(7.76, 20.5) * mm, "end": v(7.87, 20.39) * mm});
            skArc(sketch, "E146.5.1", {"start": v(7.68, 21.22) * mm, "mid": v(7.6, 20.93) * mm, "end": v(7.67, 20.64) * mm});
            skArc(sketch, "E146.5.2", {"start": v(8.83, 20.46) * mm, "mid": v(9.1, 20.85) * mm, "end": v(9.4, 21.23) * mm});
            skPoint(sketch, "E146.5.3", {"position": v(8.3, 20.8) * mm});
            skArc(sketch, "E146.5.4", {"start": v(8.22, 21.47) * mm, "mid": v(8.38, 21.43) * mm, "end": v(8.53, 21.37) * mm});
            skLineSegment(sketch, "E146.5.5", {"start": v(8.34, 19.63) * mm, "end": v(7.76, 19.94) * mm});
            skArc(sketch, "E146.5.6", {"start": v(8.71, 21.41) * mm, "mid": v(8.8, 21.53) * mm, "end": v(8.9, 21.65) * mm});
            skLineSegment(sketch, "E146.5.7", {"start": v(9.4, 21.23) * mm, "end": v(8.9, 21.65) * mm});
            skArc(sketch, "E146.5.8", {"start": v(7.68, 21.22) * mm, "mid": v(7.92, 21.42) * mm, "end": v(8.22, 21.47) * mm});
            skPoint(sketch, "E146.5.9", {"position": v(8.83, 20.46) * mm});
            skArc(sketch, "E146.5.10", {"start": v(8.52, 20.67) * mm, "mid": v(8.8, 21.08) * mm, "end": v(9.12, 21.47) * mm, "construction": true});
            skArc(sketch, "E146.5.11", {"start": v(8.83, 20.46) * mm, "mid": v(8.57, 20.05) * mm, "end": v(8.34, 19.63) * mm});
            skPoint(sketch, "E146.5.12", {"position": v(8.52, 20.67) * mm});
            skArc(sketch, "E146.5.13", {"start": v(7.9, 20.2) * mm, "mid": v(7.83, 20.07) * mm, "end": v(7.76, 19.94) * mm});
            skArc(sketch, "E146.5.14", {"start": v(8.53, 21.37) * mm, "mid": v(8.63, 21.36) * mm, "end": v(8.71, 21.41) * mm});
            skArc(sketch, "E146.5.15", {"start": v(7.87, 20.39) * mm, "mid": v(7.92, 20.3) * mm, "end": v(7.9, 20.2) * mm});
            skArc(sketch, "E146.6.0", {"start": v(6.75, 18.7) * mm, "mid": v(6.86, 18.6) * mm, "end": v(7, 18.5) * mm});
            skArc(sketch, "E146.6.1", {"start": v(6.65, 19.29) * mm, "mid": v(6.61, 18.98) * mm, "end": v(6.75, 18.7) * mm});
            skArc(sketch, "E146.6.2", {"start": v(7.92, 18.76) * mm, "mid": v(8.12, 19.2) * mm, "end": v(8.34, 19.63) * mm});
            skPoint(sketch, "E146.6.3", {"position": v(7.34, 19) * mm});
            skArc(sketch, "E146.6.4", {"start": v(7.13, 19.63) * mm, "mid": v(7.29, 19.63) * mm, "end": v(7.45, 19.6) * mm});
            skLineSegment(sketch, "E146.6.5", {"start": v(7.6, 17.85) * mm, "end": v(6.97, 18.04) * mm});
            skArc(sketch, "E146.6.6", {"start": v(7.62, 19.67) * mm, "mid": v(7.69, 19.8) * mm, "end": v(7.76, 19.94) * mm});
            skLineSegment(sketch, "E146.6.7", {"start": v(8.34, 19.63) * mm, "end": v(7.76, 19.94) * mm});
            skArc(sketch, "E146.6.8", {"start": v(6.65, 19.29) * mm, "mid": v(6.84, 19.53) * mm, "end": v(7.13, 19.63) * mm});
            skPoint(sketch, "E146.6.9", {"position": v(7.92, 18.76) * mm});
            skArc(sketch, "E146.6.10", {"start": v(7.58, 18.9) * mm, "mid": v(7.78, 19.36) * mm, "end": v(8, 19.8) * mm, "construction": true});
            skArc(sketch, "E146.6.11", {"start": v(7.92, 18.76) * mm, "mid": v(7.75, 18.3) * mm, "end": v(7.6, 17.85) * mm});
            skPoint(sketch, "E146.6.12", {"position": v(7.58, 18.9) * mm});
            skArc(sketch, "E146.6.13", {"start": v(7.06, 18.33) * mm, "mid": v(7.02, 18.18) * mm, "end": v(6.97, 18.04) * mm});
            skArc(sketch, "E146.6.14", {"start": v(7.45, 19.6) * mm, "mid": v(7.55, 19.6) * mm, "end": v(7.62, 19.67) * mm});
            skArc(sketch, "E146.6.15", {"start": v(7, 18.5) * mm, "mid": v(7.06, 18.43) * mm, "end": v(7.06, 18.33) * mm});
            skArc(sketch, "E146.7.0", {"start": v(6.22, 16.64) * mm, "mid": v(6.36, 16.55) * mm, "end": v(6.5, 16.48) * mm});
            skArc(sketch, "E146.7.1", {"start": v(6.01, 17.19) * mm, "mid": v(6.04, 16.88) * mm, "end": v(6.22, 16.64) * mm});
            skArc(sketch, "E146.7.2", {"start": v(7.36, 16.92) * mm, "mid": v(7.47, 17.39) * mm, "end": v(7.6, 17.85) * mm});
            skPoint(sketch, "E146.7.3", {"position": v(6.75, 17.04) * mm});
            skArc(sketch, "E146.7.4", {"start": v(6.41, 17.61) * mm, "mid": v(6.57, 17.64) * mm, "end": v(6.73, 17.64) * mm});
            skLineSegment(sketch, "E146.7.5", {"start": v(7.22, 15.96) * mm, "end": v(6.57, 16.03) * mm});
            skArc(sketch, "E146.7.6", {"start": v(6.89, 17.76) * mm, "mid": v(6.93, 17.9) * mm, "end": v(6.97, 18.04) * mm});
            skLineSegment(sketch, "E146.7.7", {"start": v(7.6, 17.85) * mm, "end": v(6.97, 18.04) * mm});
            skArc(sketch, "E146.7.8", {"start": v(6.01, 17.19) * mm, "mid": v(6.15, 17.46) * mm, "end": v(6.41, 17.61) * mm});
            skPoint(sketch, "E146.7.9", {"position": v(7.36, 16.92) * mm});
            skArc(sketch, "E146.7.10", {"start": v(7, 16.99) * mm, "mid": v(7.1, 17.48) * mm, "end": v(7.24, 17.96) * mm, "construction": true});
            skArc(sketch, "E146.7.11", {"start": v(7.36, 16.92) * mm, "mid": v(7.28, 16.44) * mm, "end": v(7.22, 15.96) * mm});
            skPoint(sketch, "E146.7.12", {"position": v(7, 16.99) * mm});
            skArc(sketch, "E146.7.13", {"start": v(6.6, 16.32) * mm, "mid": v(6.59, 16.18) * mm, "end": v(6.57, 16.03) * mm});
            skArc(sketch, "E146.7.14", {"start": v(6.73, 17.64) * mm, "mid": v(6.83, 17.67) * mm, "end": v(6.89, 17.76) * mm});
            skArc(sketch, "E146.7.15", {"start": v(6.5, 16.48) * mm, "mid": v(6.58, 16.42) * mm, "end": v(6.6, 16.32) * mm});
            skArc(sketch, "E146.8.0", {"start": v(6.1, 14.5) * mm, "mid": v(6.26, 14.44) * mm, "end": v(6.42, 14.4) * mm});
            skArc(sketch, "E146.8.1", {"start": v(5.8, 15) * mm, "mid": v(5.88, 14.7) * mm, "end": v(6.1, 14.5) * mm});
            skArc(sketch, "E146.8.2", {"start": v(7.18, 15) * mm, "mid": v(7.19, 15.48) * mm, "end": v(7.22, 15.96) * mm});
            skPoint(sketch, "E146.8.3", {"position": v(6.55, 15) * mm});
            skArc(sketch, "E146.8.4", {"start": v(6.1, 15.5) * mm, "mid": v(6.26, 15.56) * mm, "end": v(6.42, 15.6) * mm});
            skLineSegment(sketch, "E146.8.5", {"start": v(7.22, 14.04) * mm, "end": v(6.57, 13.97) * mm});
            skArc(sketch, "E146.8.6", {"start": v(6.55, 15.73) * mm, "mid": v(6.56, 15.88) * mm, "end": v(6.57, 16.03) * mm});
            skLineSegment(sketch, "E146.8.7", {"start": v(7.22, 15.96) * mm, "end": v(6.57, 16.03) * mm});
            skArc(sketch, "E146.8.8", {"start": v(5.8, 15) * mm, "mid": v(5.88, 15.3) * mm, "end": v(6.1, 15.5) * mm});
            skPoint(sketch, "E146.8.9", {"position": v(7.18, 15) * mm});
            skArc(sketch, "E146.8.10", {"start": v(6.8, 15) * mm, "mid": v(6.81, 15.5) * mm, "end": v(6.85, 16) * mm, "construction": true});
            skArc(sketch, "E146.8.11", {"start": v(7.18, 15) * mm, "mid": v(7.19, 14.52) * mm, "end": v(7.22, 14.04) * mm});
            skPoint(sketch, "E146.8.12", {"position": v(6.8, 15) * mm});
            skArc(sketch, "E146.8.13", {"start": v(6.55, 14.27) * mm, "mid": v(6.56, 14.12) * mm, "end": v(6.57, 13.97) * mm});
            skArc(sketch, "E146.8.14", {"start": v(6.42, 15.6) * mm, "mid": v(6.5, 15.64) * mm, "end": v(6.55, 15.73) * mm});
            skArc(sketch, "E146.8.15", {"start": v(6.42, 14.4) * mm, "mid": v(6.5, 14.36) * mm, "end": v(6.55, 14.27) * mm});
            skArc(sketch, "E146.9.0", {"start": v(6.41, 12.39) * mm, "mid": v(6.57, 12.36) * mm, "end": v(6.73, 12.36) * mm});
            skArc(sketch, "E146.9.1", {"start": v(6.01, 12.81) * mm, "mid": v(6.15, 12.54) * mm, "end": v(6.41, 12.39) * mm});
            skArc(sketch, "E146.9.2", {"start": v(7.36, 13.08) * mm, "mid": v(7.28, 13.56) * mm, "end": v(7.22, 14.04) * mm});
            skPoint(sketch, "E146.9.3", {"position": v(6.75, 12.96) * mm});
            skArc(sketch, "E146.9.4", {"start": v(6.22, 13.36) * mm, "mid": v(6.36, 13.45) * mm, "end": v(6.5, 13.52) * mm});
            skLineSegment(sketch, "E146.9.5", {"start": v(7.6, 12.15) * mm, "end": v(6.97, 11.96) * mm});
            skArc(sketch, "E146.9.6", {"start": v(6.6, 13.68) * mm, "mid": v(6.59, 13.82) * mm, "end": v(6.57, 13.97) * mm});
            skLineSegment(sketch, "E146.9.7", {"start": v(7.22, 14.04) * mm, "end": v(6.57, 13.97) * mm});
            skArc(sketch, "E146.9.8", {"start": v(6.01, 12.81) * mm, "mid": v(6.04, 13.12) * mm, "end": v(6.22, 13.36) * mm});
            skPoint(sketch, "E146.9.9", {"position": v(7.36, 13.08) * mm});
            skArc(sketch, "E146.9.10", {"start": v(7, 13.01) * mm, "mid": v(6.91, 13.5) * mm, "end": v(6.85, 14) * mm, "construction": true});
            skArc(sketch, "E146.9.11", {"start": v(7.36, 13.08) * mm, "mid": v(7.47, 12.61) * mm, "end": v(7.6, 12.15) * mm});
            skPoint(sketch, "E146.9.12", {"position": v(7, 13.01) * mm});
            skArc(sketch, "E146.9.13", {"start": v(6.89, 12.24) * mm, "mid": v(6.93, 12.1) * mm, "end": v(6.97, 11.96) * mm});
            skArc(sketch, "E146.9.14", {"start": v(6.5, 13.52) * mm, "mid": v(6.58, 13.58) * mm, "end": v(6.6, 13.68) * mm});
            skArc(sketch, "E146.9.15", {"start": v(6.73, 12.36) * mm, "mid": v(6.83, 12.33) * mm, "end": v(6.89, 12.24) * mm});
            skArc(sketch, "E146.10.0", {"start": v(7.13, 10.37) * mm, "mid": v(7.29, 10.37) * mm, "end": v(7.45, 10.4) * mm});
            skArc(sketch, "E146.10.1", {"start": v(6.65, 10.71) * mm, "mid": v(6.84, 10.47) * mm, "end": v(7.13, 10.37) * mm});
            skArc(sketch, "E146.10.2", {"start": v(7.92, 11.24) * mm, "mid": v(7.75, 11.7) * mm, "end": v(7.6, 12.15) * mm});
            skPoint(sketch, "E146.10.3", {"position": v(7.34, 11) * mm});
            skArc(sketch, "E146.10.4", {"start": v(6.75, 11.3) * mm, "mid": v(6.86, 11.4) * mm, "end": v(7, 11.5) * mm});
            skLineSegment(sketch, "E146.10.5", {"start": v(8.34, 10.37) * mm, "end": v(7.76, 10.06) * mm});
            skArc(sketch, "E146.10.6", {"start": v(7.06, 11.67) * mm, "mid": v(7.02, 11.82) * mm, "end": v(6.97, 11.96) * mm});
            skLineSegment(sketch, "E146.10.7", {"start": v(7.6, 12.15) * mm, "end": v(6.97, 11.96) * mm});
            skArc(sketch, "E146.10.8", {"start": v(6.65, 10.71) * mm, "mid": v(6.61, 11.02) * mm, "end": v(6.75, 11.3) * mm});
            skPoint(sketch, "E146.10.9", {"position": v(7.92, 11.24) * mm});
            skArc(sketch, "E146.10.10", {"start": v(7.58, 11.1) * mm, "mid": v(7.4, 11.56) * mm, "end": v(7.24, 12.04) * mm, "construction": true});
            skArc(sketch, "E146.10.11", {"start": v(7.92, 11.24) * mm, "mid": v(8.12, 10.8) * mm, "end": v(8.34, 10.37) * mm});
            skPoint(sketch, "E146.10.12", {"position": v(7.58, 11.1) * mm});
            skArc(sketch, "E146.10.13", {"start": v(7.62, 10.33) * mm, "mid": v(7.69, 10.2) * mm, "end": v(7.76, 10.06) * mm});
            skArc(sketch, "E146.10.14", {"start": v(7, 11.5) * mm, "mid": v(7.06, 11.57) * mm, "end": v(7.06, 11.67) * mm});
            skArc(sketch, "E146.10.15", {"start": v(7.45, 10.4) * mm, "mid": v(7.55, 10.4) * mm, "end": v(7.62, 10.33) * mm});
            skArc(sketch, "E146.11.0", {"start": v(8.22, 8.53) * mm, "mid": v(8.38, 8.57) * mm, "end": v(8.53, 8.63) * mm});
            skArc(sketch, "E146.11.1", {"start": v(7.68, 8.78) * mm, "mid": v(7.92, 8.58) * mm, "end": v(8.22, 8.53) * mm});
            skArc(sketch, "E146.11.2", {"start": v(8.83, 9.54) * mm, "mid": v(8.57, 9.95) * mm, "end": v(8.34, 10.37) * mm});
            skPoint(sketch, "E146.11.3", {"position": v(8.3, 9.2) * mm});
            skArc(sketch, "E146.11.4", {"start": v(7.67, 9.36) * mm, "mid": v(7.76, 9.5) * mm, "end": v(7.87, 9.61) * mm});
            skLineSegment(sketch, "E146.11.5", {"start": v(9.4, 8.77) * mm, "end": v(8.9, 8.35) * mm});
            skArc(sketch, "E146.11.6", {"start": v(7.9, 9.8) * mm, "mid": v(7.83, 9.93) * mm, "end": v(7.76, 10.06) * mm});
            skLineSegment(sketch, "E146.11.7", {"start": v(8.34, 10.37) * mm, "end": v(7.76, 10.06) * mm});
            skArc(sketch, "E146.11.8", {"start": v(7.68, 8.78) * mm, "mid": v(7.6, 9.07) * mm, "end": v(7.67, 9.36) * mm});
            skPoint(sketch, "E146.11.9", {"position": v(8.83, 9.54) * mm});
            skArc(sketch, "E146.11.10", {"start": v(8.52, 9.33) * mm, "mid": v(8.25, 9.76) * mm, "end": v(8, 10.2) * mm, "construction": true});
            skArc(sketch, "E146.11.11", {"start": v(8.83, 9.54) * mm, "mid": v(9.1, 9.15) * mm, "end": v(9.4, 8.77) * mm});
            skPoint(sketch, "E146.11.12", {"position": v(8.52, 9.33) * mm});
            skArc(sketch, "E146.11.13", {"start": v(8.71, 8.59) * mm, "mid": v(8.8, 8.47) * mm, "end": v(8.9, 8.35) * mm});
            skArc(sketch, "E146.11.14", {"start": v(7.87, 9.61) * mm, "mid": v(7.92, 9.7) * mm, "end": v(7.9, 9.8) * mm});
            skArc(sketch, "E146.11.15", {"start": v(8.53, 8.63) * mm, "mid": v(8.63, 8.64) * mm, "end": v(8.71, 8.59) * mm});
            skArc(sketch, "E146.12.0", {"start": v(9.65, 6.95) * mm, "mid": v(9.8, 7) * mm, "end": v(9.93, 7.1) * mm});
            skArc(sketch, "E146.12.1", {"start": v(9.08, 7.08) * mm, "mid": v(9.35, 6.93) * mm, "end": v(9.65, 6.95) * mm});
            skArc(sketch, "E146.12.2", {"start": v(10.05, 8.05) * mm, "mid": v(9.72, 8.4) * mm, "end": v(9.4, 8.77) * mm});
            skPoint(sketch, "E146.12.3", {"position": v(9.6, 7.6) * mm});
            skArc(sketch, "E146.12.4", {"start": v(8.95, 7.65) * mm, "mid": v(9, 7.8) * mm, "end": v(9.1, 7.93) * mm});
            skLineSegment(sketch, "E146.12.5", {"start": v(10.77, 7.4) * mm, "end": v(10.35, 6.9) * mm});
            skArc(sketch, "E146.12.6", {"start": v(9.1, 8.12) * mm, "mid": v(9, 8.24) * mm, "end": v(8.9, 8.35) * mm});
            skLineSegment(sketch, "E146.12.7", {"start": v(9.4, 8.77) * mm, "end": v(8.9, 8.35) * mm});
            skArc(sketch, "E146.12.8", {"start": v(9.08, 7.08) * mm, "mid": v(8.93, 7.35) * mm, "end": v(8.95, 7.65) * mm});
            skPoint(sketch, "E146.12.9", {"position": v(10.05, 8.05) * mm});
            skArc(sketch, "E146.12.10", {"start": v(9.79, 7.79) * mm, "mid": v(9.44, 8.15) * mm, "end": v(9.12, 8.53) * mm, "construction": true});
            skArc(sketch, "E146.12.11", {"start": v(10.05, 8.05) * mm, "mid": v(10.4, 7.72) * mm, "end": v(10.77, 7.4) * mm});
            skPoint(sketch, "E146.12.12", {"position": v(9.79, 7.79) * mm});
            skArc(sketch, "E146.12.13", {"start": v(10.12, 7.1) * mm, "mid": v(10.24, 7) * mm, "end": v(10.35, 6.9) * mm});
            skArc(sketch, "E146.12.14", {"start": v(9.1, 7.93) * mm, "mid": v(9.13, 8.03) * mm, "end": v(9.1, 8.12) * mm});
            skArc(sketch, "E146.12.15", {"start": v(9.93, 7.1) * mm, "mid": v(10.03, 7.13) * mm, "end": v(10.12, 7.1) * mm});
            skArc(sketch, "E146.13.0", {"start": v(11.36, 5.67) * mm, "mid": v(11.5, 5.76) * mm, "end": v(11.61, 5.87) * mm});
            skArc(sketch, "E146.13.1", {"start": v(10.78, 5.68) * mm, "mid": v(11.07, 5.6) * mm, "end": v(11.36, 5.67) * mm});
            skArc(sketch, "E146.13.2", {"start": v(11.54, 6.83) * mm, "mid": v(11.15, 7.1) * mm, "end": v(10.77, 7.4) * mm});
            skPoint(sketch, "E146.13.3", {"position": v(11.2, 6.3) * mm});
            skArc(sketch, "E146.13.4", {"start": v(10.53, 6.22) * mm, "mid": v(10.57, 6.38) * mm, "end": v(10.63, 6.53) * mm});
            skLineSegment(sketch, "E146.13.5", {"start": v(12.37, 6.34) * mm, "end": v(12.06, 5.76) * mm});
            skArc(sketch, "E146.13.6", {"start": v(10.59, 6.71) * mm, "mid": v(10.47, 6.8) * mm, "end": v(10.35, 6.9) * mm});
            skLineSegment(sketch, "E146.13.7", {"start": v(10.77, 7.4) * mm, "end": v(10.35, 6.9) * mm});
            skArc(sketch, "E146.13.8", {"start": v(10.78, 5.68) * mm, "mid": v(10.58, 5.92) * mm, "end": v(10.53, 6.22) * mm});
            skPoint(sketch, "E146.13.9", {"position": v(11.54, 6.83) * mm});
            skArc(sketch, "E146.13.10", {"start": v(11.33, 6.52) * mm, "mid": v(10.92, 6.8) * mm, "end": v(10.53, 7.12) * mm, "construction": true});
            skArc(sketch, "E146.13.11", {"start": v(11.54, 6.83) * mm, "mid": v(11.95, 6.57) * mm, "end": v(12.37, 6.34) * mm});
            skPoint(sketch, "E146.13.12", {"position": v(11.33, 6.52) * mm});
            skArc(sketch, "E146.13.13", {"start": v(11.8, 5.9) * mm, "mid": v(11.93, 5.83) * mm, "end": v(12.06, 5.76) * mm});
            skArc(sketch, "E146.13.14", {"start": v(10.63, 6.53) * mm, "mid": v(10.64, 6.63) * mm, "end": v(10.59, 6.71) * mm});
            skArc(sketch, "E146.13.15", {"start": v(11.61, 5.87) * mm, "mid": v(11.7, 5.92) * mm, "end": v(11.8, 5.9) * mm});
            skArc(sketch, "E146.14.0", {"start": v(13.3, 4.75) * mm, "mid": v(13.4, 4.86) * mm, "end": v(13.5, 5) * mm});
            skArc(sketch, "E146.14.1", {"start": v(12.71, 4.65) * mm, "mid": v(13.02, 4.61) * mm, "end": v(13.3, 4.75) * mm});
            skArc(sketch, "E146.14.2", {"start": v(13.24, 5.92) * mm, "mid": v(12.8, 6.12) * mm, "end": v(12.37, 6.34) * mm});
            skPoint(sketch, "E146.14.3", {"position": v(13, 5.34) * mm});
            skArc(sketch, "E146.14.4", {"start": v(12.37, 5.13) * mm, "mid": v(12.37, 5.29) * mm, "end": v(12.4, 5.45) * mm});
            skLineSegment(sketch, "E146.14.5", {"start": v(14.15, 5.6) * mm, "end": v(13.96, 4.97) * mm});
            skArc(sketch, "E146.14.6", {"start": v(12.33, 5.62) * mm, "mid": v(12.2, 5.69) * mm, "end": v(12.06, 5.76) * mm});
            skLineSegment(sketch, "E146.14.7", {"start": v(12.37, 6.34) * mm, "end": v(12.06, 5.76) * mm});
            skArc(sketch, "E146.14.8", {"start": v(12.71, 4.65) * mm, "mid": v(12.47, 4.84) * mm, "end": v(12.37, 5.13) * mm});
            skPoint(sketch, "E146.14.9", {"position": v(13.24, 5.92) * mm});
            skArc(sketch, "E146.14.10", {"start": v(13.1, 5.58) * mm, "mid": v(12.64, 5.78) * mm, "end": v(12.2, 6) * mm, "construction": true});
            skArc(sketch, "E146.14.11", {"start": v(13.24, 5.92) * mm, "mid": v(13.7, 5.75) * mm, "end": v(14.15, 5.6) * mm});
            skPoint(sketch, "E146.14.12", {"position": v(13.1, 5.58) * mm});
            skArc(sketch, "E146.14.13", {"start": v(13.67, 5.06) * mm, "mid": v(13.82, 5.02) * mm, "end": v(13.96, 4.97) * mm});
            skArc(sketch, "E146.14.14", {"start": v(12.4, 5.45) * mm, "mid": v(12.4, 5.55) * mm, "end": v(12.33, 5.62) * mm});
            skArc(sketch, "E146.14.15", {"start": v(13.5, 5) * mm, "mid": v(13.57, 5.06) * mm, "end": v(13.67, 5.06) * mm});
            skArc(sketch, "E146.15.0", {"start": v(15.36, 4.22) * mm, "mid": v(15.45, 4.36) * mm, "end": v(15.52, 4.5) * mm});
            skArc(sketch, "E146.15.1", {"start": v(14.81, 4.01) * mm, "mid": v(15.12, 4.04) * mm, "end": v(15.36, 4.22) * mm});
            skArc(sketch, "E146.15.2", {"start": v(15.08, 5.36) * mm, "mid": v(14.61, 5.47) * mm, "end": v(14.15, 5.6) * mm});
            skPoint(sketch, "E146.15.3", {"position": v(14.96, 4.75) * mm});
            skArc(sketch, "E146.15.4", {"start": v(14.39, 4.41) * mm, "mid": v(14.36, 4.57) * mm, "end": v(14.36, 4.73) * mm});
            skLineSegment(sketch, "E146.15.5", {"start": v(16.04, 5.22) * mm, "end": v(15.97, 4.57) * mm});
            skArc(sketch, "E146.15.6", {"start": v(14.24, 4.89) * mm, "mid": v(14.1, 4.93) * mm, "end": v(13.96, 4.97) * mm});
            skLineSegment(sketch, "E146.15.7", {"start": v(14.15, 5.6) * mm, "end": v(13.96, 4.97) * mm});
            skArc(sketch, "E146.15.8", {"start": v(14.81, 4.01) * mm, "mid": v(14.54, 4.15) * mm, "end": v(14.39, 4.41) * mm});
            skPoint(sketch, "E146.15.9", {"position": v(15.08, 5.36) * mm});
            skArc(sketch, "E146.15.10", {"start": v(15.01, 5) * mm, "mid": v(14.52, 5.1) * mm, "end": v(14.04, 5.24) * mm, "construction": true});
            skArc(sketch, "E146.15.11", {"start": v(15.08, 5.36) * mm, "mid": v(15.56, 5.28) * mm, "end": v(16.04, 5.22) * mm});
            skPoint(sketch, "E146.15.12", {"position": v(15.01, 5) * mm});
            skArc(sketch, "E146.15.13", {"start": v(15.68, 4.6) * mm, "mid": v(15.82, 4.59) * mm, "end": v(15.97, 4.57) * mm});
            skArc(sketch, "E146.15.14", {"start": v(14.36, 4.73) * mm, "mid": v(14.33, 4.83) * mm, "end": v(14.24, 4.89) * mm});
            skArc(sketch, "E146.15.15", {"start": v(15.52, 4.5) * mm, "mid": v(15.58, 4.58) * mm, "end": v(15.68, 4.6) * mm});
            skArc(sketch, "E146.16.0", {"start": v(17.5, 4.1) * mm, "mid": v(17.56, 4.26) * mm, "end": v(17.6, 4.42) * mm});
            skArc(sketch, "E146.16.1", {"start": v(17, 3.8) * mm, "mid": v(17.3, 3.88) * mm, "end": v(17.5, 4.1) * mm});
            skArc(sketch, "E146.16.2", {"start": v(17, 5.18) * mm, "mid": v(16.52, 5.19) * mm, "end": v(16.04, 5.22) * mm});
            skPoint(sketch, "E146.16.3", {"position": v(17, 4.55) * mm});
            skArc(sketch, "E146.16.4", {"start": v(16.5, 4.1) * mm, "mid": v(16.44, 4.26) * mm, "end": v(16.4, 4.42) * mm});
            skLineSegment(sketch, "E146.16.5", {"start": v(17.96, 5.22) * mm, "end": v(18.03, 4.57) * mm});
            skArc(sketch, "E146.16.6", {"start": v(16.27, 4.55) * mm, "mid": v(16.12, 4.56) * mm, "end": v(15.97, 4.57) * mm});
            skLineSegment(sketch, "E146.16.7", {"start": v(16.04, 5.22) * mm, "end": v(15.97, 4.57) * mm});
            skArc(sketch, "E146.16.8", {"start": v(17, 3.8) * mm, "mid": v(16.7, 3.88) * mm, "end": v(16.5, 4.1) * mm});
            skPoint(sketch, "E146.16.9", {"position": v(17, 5.18) * mm});
            skArc(sketch, "E146.16.10", {"start": v(17, 4.8) * mm, "mid": v(16.5, 4.81) * mm, "end": v(16, 4.85) * mm, "construction": true});
            skArc(sketch, "E146.16.11", {"start": v(17, 5.18) * mm, "mid": v(17.48, 5.19) * mm, "end": v(17.96, 5.22) * mm});
            skPoint(sketch, "E146.16.12", {"position": v(17, 4.8) * mm});
            skArc(sketch, "E146.16.13", {"start": v(17.73, 4.55) * mm, "mid": v(17.88, 4.56) * mm, "end": v(18.03, 4.57) * mm});
            skArc(sketch, "E146.16.14", {"start": v(16.4, 4.42) * mm, "mid": v(16.36, 4.5) * mm, "end": v(16.27, 4.55) * mm});
            skArc(sketch, "E146.16.15", {"start": v(17.6, 4.42) * mm, "mid": v(17.64, 4.5) * mm, "end": v(17.73, 4.55) * mm});
            skArc(sketch, "E146.17.0", {"start": v(19.61, 4.41) * mm, "mid": v(19.64, 4.57) * mm, "end": v(19.64, 4.73) * mm});
            skArc(sketch, "E146.17.1", {"start": v(19.19, 4.01) * mm, "mid": v(19.46, 4.15) * mm, "end": v(19.61, 4.41) * mm});
            skArc(sketch, "E146.17.2", {"start": v(18.92, 5.36) * mm, "mid": v(18.44, 5.28) * mm, "end": v(17.96, 5.22) * mm});
            skPoint(sketch, "E146.17.3", {"position": v(19.04, 4.75) * mm});
            skArc(sketch, "E146.17.4", {"start": v(18.64, 4.22) * mm, "mid": v(18.55, 4.36) * mm, "end": v(18.48, 4.5) * mm});
            skLineSegment(sketch, "E146.17.5", {"start": v(19.85, 5.6) * mm, "end": v(20.04, 4.97) * mm});
            skArc(sketch, "E146.17.6", {"start": v(18.32, 4.6) * mm, "mid": v(18.18, 4.59) * mm, "end": v(18.03, 4.57) * mm});
            skLineSegment(sketch, "E146.17.7", {"start": v(17.96, 5.22) * mm, "end": v(18.03, 4.57) * mm});
            skArc(sketch, "E146.17.8", {"start": v(19.19, 4.01) * mm, "mid": v(18.88, 4.04) * mm, "end": v(18.64, 4.22) * mm});
            skPoint(sketch, "E146.17.9", {"position": v(18.92, 5.36) * mm});
            skArc(sketch, "E146.17.10", {"start": v(18.99, 5) * mm, "mid": v(18.5, 4.91) * mm, "end": v(18, 4.85) * mm, "construction": true});
            skArc(sketch, "E146.17.11", {"start": v(18.92, 5.36) * mm, "mid": v(19.39, 5.47) * mm, "end": v(19.85, 5.6) * mm});
            skPoint(sketch, "E146.17.12", {"position": v(18.99, 5) * mm});
            skArc(sketch, "E146.17.13", {"start": v(19.76, 4.89) * mm, "mid": v(19.9, 4.93) * mm, "end": v(20.04, 4.97) * mm});
            skArc(sketch, "E146.17.14", {"start": v(18.48, 4.5) * mm, "mid": v(18.42, 4.58) * mm, "end": v(18.32, 4.6) * mm});
            skArc(sketch, "E146.17.15", {"start": v(19.64, 4.73) * mm, "mid": v(19.67, 4.83) * mm, "end": v(19.76, 4.89) * mm});
            skArc(sketch, "E146.18.0", {"start": v(21.63, 5.13) * mm, "mid": v(21.63, 5.29) * mm, "end": v(21.6, 5.45) * mm});
            skArc(sketch, "E146.18.1", {"start": v(21.29, 4.65) * mm, "mid": v(21.53, 4.84) * mm, "end": v(21.63, 5.13) * mm});
            skArc(sketch, "E146.18.2", {"start": v(20.76, 5.92) * mm, "mid": v(20.3, 5.75) * mm, "end": v(19.85, 5.6) * mm});
            skPoint(sketch, "E146.18.3", {"position": v(21, 5.34) * mm});
            skArc(sketch, "E146.18.4", {"start": v(20.7, 4.75) * mm, "mid": v(20.6, 4.86) * mm, "end": v(20.5, 5) * mm});
            skLineSegment(sketch, "E146.18.5", {"start": v(21.63, 6.34) * mm, "end": v(21.94, 5.76) * mm});
            skArc(sketch, "E146.18.6", {"start": v(20.33, 5.06) * mm, "mid": v(20.18, 5.02) * mm, "end": v(20.04, 4.97) * mm});
            skLineSegment(sketch, "E146.18.7", {"start": v(19.85, 5.6) * mm, "end": v(20.04, 4.97) * mm});
            skArc(sketch, "E146.18.8", {"start": v(21.29, 4.65) * mm, "mid": v(20.98, 4.61) * mm, "end": v(20.7, 4.75) * mm});
            skPoint(sketch, "E146.18.9", {"position": v(20.76, 5.92) * mm});
            skArc(sketch, "E146.18.10", {"start": v(20.9, 5.58) * mm, "mid": v(20.44, 5.4) * mm, "end": v(19.96, 5.24) * mm, "construction": true});
            skArc(sketch, "E146.18.11", {"start": v(20.76, 5.92) * mm, "mid": v(21.2, 6.12) * mm, "end": v(21.63, 6.34) * mm});
            skPoint(sketch, "E146.18.12", {"position": v(20.9, 5.58) * mm});
            skArc(sketch, "E146.18.13", {"start": v(21.67, 5.62) * mm, "mid": v(21.8, 5.69) * mm, "end": v(21.94, 5.76) * mm});
            skArc(sketch, "E146.18.14", {"start": v(20.5, 5) * mm, "mid": v(20.43, 5.06) * mm, "end": v(20.33, 5.06) * mm});
            skArc(sketch, "E146.18.15", {"start": v(21.6, 5.45) * mm, "mid": v(21.6, 5.55) * mm, "end": v(21.67, 5.62) * mm});
            skArc(sketch, "E146.19.0", {"start": v(23.47, 6.22) * mm, "mid": v(23.43, 6.38) * mm, "end": v(23.37, 6.53) * mm});
            skArc(sketch, "E146.19.1", {"start": v(23.22, 5.68) * mm, "mid": v(23.42, 5.92) * mm, "end": v(23.47, 6.22) * mm});
            skArc(sketch, "E146.19.2", {"start": v(22.46, 6.83) * mm, "mid": v(22.05, 6.57) * mm, "end": v(21.63, 6.34) * mm});
            skPoint(sketch, "E146.19.3", {"position": v(22.8, 6.3) * mm});
            skArc(sketch, "E146.19.4", {"start": v(22.64, 5.67) * mm, "mid": v(22.5, 5.76) * mm, "end": v(22.39, 5.87) * mm});
            skLineSegment(sketch, "E146.19.5", {"start": v(23.23, 7.4) * mm, "end": v(23.65, 6.9) * mm});
            skArc(sketch, "E146.19.6", {"start": v(22.2, 5.9) * mm, "mid": v(22.07, 5.83) * mm, "end": v(21.94, 5.76) * mm});
            skLineSegment(sketch, "E146.19.7", {"start": v(21.63, 6.34) * mm, "end": v(21.94, 5.76) * mm});
            skArc(sketch, "E146.19.8", {"start": v(23.22, 5.68) * mm, "mid": v(22.93, 5.6) * mm, "end": v(22.64, 5.67) * mm});
            skPoint(sketch, "E146.19.9", {"position": v(22.46, 6.83) * mm});
            skArc(sketch, "E146.19.10", {"start": v(22.67, 6.52) * mm, "mid": v(22.24, 6.25) * mm, "end": v(21.8, 6) * mm, "construction": true});
            skArc(sketch, "E146.19.11", {"start": v(22.46, 6.83) * mm, "mid": v(22.85, 7.1) * mm, "end": v(23.23, 7.4) * mm});
            skPoint(sketch, "E146.19.12", {"position": v(22.67, 6.52) * mm});
            skArc(sketch, "E146.19.13", {"start": v(23.41, 6.71) * mm, "mid": v(23.53, 6.8) * mm, "end": v(23.65, 6.9) * mm});
            skArc(sketch, "E146.19.14", {"start": v(22.39, 5.87) * mm, "mid": v(22.3, 5.92) * mm, "end": v(22.2, 5.9) * mm});
            skArc(sketch, "E146.19.15", {"start": v(23.37, 6.53) * mm, "mid": v(23.36, 6.63) * mm, "end": v(23.41, 6.71) * mm});
            skArc(sketch, "E146.20.0", {"start": v(25.05, 7.65) * mm, "mid": v(25, 7.8) * mm, "end": v(24.9, 7.93) * mm});
            skArc(sketch, "E146.20.1", {"start": v(24.92, 7.08) * mm, "mid": v(25.07, 7.35) * mm, "end": v(25.05, 7.65) * mm});
            skArc(sketch, "E146.20.2", {"start": v(23.95, 8.05) * mm, "mid": v(23.6, 7.72) * mm, "end": v(23.23, 7.4) * mm});
            skPoint(sketch, "E146.20.3", {"position": v(24.4, 7.6) * mm});
            skArc(sketch, "E146.20.4", {"start": v(24.35, 6.95) * mm, "mid": v(24.2, 7) * mm, "end": v(24.07, 7.1) * mm});
            skLineSegment(sketch, "E146.20.5", {"start": v(24.6, 8.77) * mm, "end": v(25.1, 8.35) * mm});
            skArc(sketch, "E146.20.6", {"start": v(23.88, 7.1) * mm, "mid": v(23.76, 7) * mm, "end": v(23.65, 6.9) * mm});
            skLineSegment(sketch, "E146.20.7", {"start": v(23.23, 7.4) * mm, "end": v(23.65, 6.9) * mm});
            skArc(sketch, "E146.20.8", {"start": v(24.92, 7.08) * mm, "mid": v(24.65, 6.93) * mm, "end": v(24.35, 6.95) * mm});
            skPoint(sketch, "E146.20.9", {"position": v(23.95, 8.05) * mm});
            skArc(sketch, "E146.20.10", {"start": v(24.21, 7.79) * mm, "mid": v(23.85, 7.44) * mm, "end": v(23.47, 7.12) * mm, "construction": true});
            skArc(sketch, "E146.20.11", {"start": v(23.95, 8.05) * mm, "mid": v(24.28, 8.4) * mm, "end": v(24.6, 8.77) * mm});
            skPoint(sketch, "E146.20.12", {"position": v(24.21, 7.79) * mm});
            skArc(sketch, "E146.20.13", {"start": v(24.9, 8.12) * mm, "mid": v(25, 8.24) * mm, "end": v(25.1, 8.35) * mm});
            skArc(sketch, "E146.20.14", {"start": v(24.07, 7.1) * mm, "mid": v(23.97, 7.13) * mm, "end": v(23.88, 7.1) * mm});
            skArc(sketch, "E146.20.15", {"start": v(24.9, 7.93) * mm, "mid": v(24.87, 8.03) * mm, "end": v(24.9, 8.12) * mm});
            skArc(sketch, "E146.21.0", {"start": v(26.33, 9.36) * mm, "mid": v(26.24, 9.5) * mm, "end": v(26.13, 9.61) * mm});
            skArc(sketch, "E146.21.1", {"start": v(26.32, 8.78) * mm, "mid": v(26.4, 9.07) * mm, "end": v(26.33, 9.36) * mm});
            skArc(sketch, "E146.21.2", {"start": v(25.17, 9.54) * mm, "mid": v(24.9, 9.15) * mm, "end": v(24.6, 8.77) * mm});
            skPoint(sketch, "E146.21.3", {"position": v(25.7, 9.2) * mm});
            skArc(sketch, "E146.21.4", {"start": v(25.78, 8.53) * mm, "mid": v(25.62, 8.57) * mm, "end": v(25.47, 8.63) * mm});
            skLineSegment(sketch, "E146.21.5", {"start": v(25.66, 10.37) * mm, "end": v(26.24, 10.06) * mm});
            skArc(sketch, "E146.21.6", {"start": v(25.29, 8.59) * mm, "mid": v(25.2, 8.47) * mm, "end": v(25.1, 8.35) * mm});
            skLineSegment(sketch, "E146.21.7", {"start": v(24.6, 8.77) * mm, "end": v(25.1, 8.35) * mm});
            skArc(sketch, "E146.21.8", {"start": v(26.32, 8.78) * mm, "mid": v(26.08, 8.58) * mm, "end": v(25.78, 8.53) * mm});
            skPoint(sketch, "E146.21.9", {"position": v(25.17, 9.54) * mm});
            skArc(sketch, "E146.21.10", {"start": v(25.48, 9.33) * mm, "mid": v(25.2, 8.92) * mm, "end": v(24.88, 8.53) * mm, "construction": true});
            skArc(sketch, "E146.21.11", {"start": v(25.17, 9.54) * mm, "mid": v(25.43, 9.95) * mm, "end": v(25.66, 10.37) * mm});
            skPoint(sketch, "E146.21.12", {"position": v(25.48, 9.33) * mm});
            skArc(sketch, "E146.21.13", {"start": v(26.1, 9.8) * mm, "mid": v(26.17, 9.93) * mm, "end": v(26.24, 10.06) * mm});
            skArc(sketch, "E146.21.14", {"start": v(25.47, 8.63) * mm, "mid": v(25.37, 8.64) * mm, "end": v(25.29, 8.59) * mm});
            skArc(sketch, "E146.21.15", {"start": v(26.13, 9.61) * mm, "mid": v(26.08, 9.7) * mm, "end": v(26.1, 9.8) * mm});
            skArc(sketch, "E146.22.0", {"start": v(27.25, 11.3) * mm, "mid": v(27.14, 11.4) * mm, "end": v(27, 11.5) * mm});
            skArc(sketch, "E146.22.1", {"start": v(27.35, 10.71) * mm, "mid": v(27.39, 11.02) * mm, "end": v(27.25, 11.3) * mm});
            skArc(sketch, "E146.22.2", {"start": v(26.08, 11.24) * mm, "mid": v(25.88, 10.8) * mm, "end": v(25.66, 10.37) * mm});
            skPoint(sketch, "E146.22.3", {"position": v(26.66, 11) * mm});
            skArc(sketch, "E146.22.4", {"start": v(26.87, 10.37) * mm, "mid": v(26.71, 10.37) * mm, "end": v(26.55, 10.4) * mm});
            skLineSegment(sketch, "E146.22.5", {"start": v(26.4, 12.15) * mm, "end": v(27.03, 11.96) * mm});
            skArc(sketch, "E146.22.6", {"start": v(26.38, 10.33) * mm, "mid": v(26.31, 10.2) * mm, "end": v(26.24, 10.06) * mm});
            skLineSegment(sketch, "E146.22.7", {"start": v(25.66, 10.37) * mm, "end": v(26.24, 10.06) * mm});
            skArc(sketch, "E146.22.8", {"start": v(27.35, 10.71) * mm, "mid": v(27.16, 10.47) * mm, "end": v(26.87, 10.37) * mm});
            skPoint(sketch, "E146.22.9", {"position": v(26.08, 11.24) * mm});
            skArc(sketch, "E146.22.10", {"start": v(26.42, 11.1) * mm, "mid": v(26.22, 10.64) * mm, "end": v(26, 10.2) * mm, "construction": true});
            skArc(sketch, "E146.22.11", {"start": v(26.08, 11.24) * mm, "mid": v(26.25, 11.7) * mm, "end": v(26.4, 12.15) * mm});
            skPoint(sketch, "E146.22.12", {"position": v(26.42, 11.1) * mm});
            skArc(sketch, "E146.22.13", {"start": v(26.94, 11.67) * mm, "mid": v(26.98, 11.82) * mm, "end": v(27.03, 11.96) * mm});
            skArc(sketch, "E146.22.14", {"start": v(26.55, 10.4) * mm, "mid": v(26.45, 10.4) * mm, "end": v(26.38, 10.33) * mm});
            skArc(sketch, "E146.22.15", {"start": v(27, 11.5) * mm, "mid": v(26.94, 11.57) * mm, "end": v(26.94, 11.67) * mm});
            skArc(sketch, "E146.23.0", {"start": v(27.78, 13.36) * mm, "mid": v(27.64, 13.45) * mm, "end": v(27.5, 13.52) * mm});
            skArc(sketch, "E146.23.1", {"start": v(27.99, 12.81) * mm, "mid": v(27.96, 13.12) * mm, "end": v(27.78, 13.36) * mm});
            skArc(sketch, "E146.23.2", {"start": v(26.64, 13.08) * mm, "mid": v(26.53, 12.61) * mm, "end": v(26.4, 12.15) * mm});
            skPoint(sketch, "E146.23.3", {"position": v(27.25, 12.96) * mm});
            skArc(sketch, "E146.23.4", {"start": v(27.59, 12.39) * mm, "mid": v(27.43, 12.36) * mm, "end": v(27.27, 12.36) * mm});
            skLineSegment(sketch, "E146.23.5", {"start": v(26.78, 14.04) * mm, "end": v(27.43, 13.97) * mm});
            skArc(sketch, "E146.23.6", {"start": v(27.11, 12.24) * mm, "mid": v(27.07, 12.1) * mm, "end": v(27.03, 11.96) * mm});
            skLineSegment(sketch, "E146.23.7", {"start": v(26.4, 12.15) * mm, "end": v(27.03, 11.96) * mm});
            skArc(sketch, "E146.23.8", {"start": v(27.99, 12.81) * mm, "mid": v(27.85, 12.54) * mm, "end": v(27.59, 12.39) * mm});
            skPoint(sketch, "E146.23.9", {"position": v(26.64, 13.08) * mm});
            skArc(sketch, "E146.23.10", {"start": v(27, 13.01) * mm, "mid": v(26.9, 12.52) * mm, "end": v(26.76, 12.04) * mm, "construction": true});
            skArc(sketch, "E146.23.11", {"start": v(26.64, 13.08) * mm, "mid": v(26.72, 13.56) * mm, "end": v(26.78, 14.04) * mm});
            skPoint(sketch, "E146.23.12", {"position": v(27, 13.01) * mm});
            skArc(sketch, "E146.23.13", {"start": v(27.4, 13.68) * mm, "mid": v(27.41, 13.82) * mm, "end": v(27.43, 13.97) * mm});
            skArc(sketch, "E146.23.14", {"start": v(27.27, 12.36) * mm, "mid": v(27.17, 12.33) * mm, "end": v(27.11, 12.24) * mm});
            skArc(sketch, "E146.23.15", {"start": v(27.5, 13.52) * mm, "mid": v(27.42, 13.58) * mm, "end": v(27.4, 13.68) * mm});
            skArc(sketch, "E146.24.0", {"start": v(27.9, 15.5) * mm, "mid": v(27.74, 15.56) * mm, "end": v(27.58, 15.6) * mm});
            skArc(sketch, "E146.24.1", {"start": v(28.2, 15) * mm, "mid": v(28.12, 15.3) * mm, "end": v(27.9, 15.5) * mm});
            skArc(sketch, "E146.24.2", {"start": v(26.82, 15) * mm, "mid": v(26.81, 14.52) * mm, "end": v(26.78, 14.04) * mm});
            skPoint(sketch, "E146.24.3", {"position": v(27.45, 15) * mm});
            skArc(sketch, "E146.24.4", {"start": v(27.9, 14.5) * mm, "mid": v(27.74, 14.44) * mm, "end": v(27.58, 14.4) * mm});
            skLineSegment(sketch, "E146.24.5", {"start": v(26.78, 15.96) * mm, "end": v(27.43, 16.03) * mm});
            skArc(sketch, "E146.24.6", {"start": v(27.45, 14.27) * mm, "mid": v(27.44, 14.12) * mm, "end": v(27.43, 13.97) * mm});
            skLineSegment(sketch, "E146.24.7", {"start": v(26.78, 14.04) * mm, "end": v(27.43, 13.97) * mm});
            skArc(sketch, "E146.24.8", {"start": v(28.2, 15) * mm, "mid": v(28.12, 14.7) * mm, "end": v(27.9, 14.5) * mm});
            skPoint(sketch, "E146.24.9", {"position": v(26.82, 15) * mm});
            skArc(sketch, "E146.24.10", {"start": v(27.2, 15) * mm, "mid": v(27.19, 14.5) * mm, "end": v(27.15, 14) * mm, "construction": true});
            skArc(sketch, "E146.24.11", {"start": v(26.82, 15) * mm, "mid": v(26.81, 15.48) * mm, "end": v(26.78, 15.96) * mm});
            skPoint(sketch, "E146.24.12", {"position": v(27.2, 15) * mm});
            skArc(sketch, "E146.24.13", {"start": v(27.45, 15.73) * mm, "mid": v(27.44, 15.88) * mm, "end": v(27.43, 16.03) * mm});
            skArc(sketch, "E146.24.14", {"start": v(27.58, 14.4) * mm, "mid": v(27.5, 14.36) * mm, "end": v(27.45, 14.27) * mm});
            skArc(sketch, "E146.24.15", {"start": v(27.58, 15.6) * mm, "mid": v(27.5, 15.64) * mm, "end": v(27.45, 15.73) * mm});
            skArc(sketch, "E146.25.0", {"start": v(27.59, 17.61) * mm, "mid": v(27.43, 17.64) * mm, "end": v(27.27, 17.64) * mm});
            skArc(sketch, "E146.25.1", {"start": v(27.99, 17.19) * mm, "mid": v(27.85, 17.46) * mm, "end": v(27.59, 17.61) * mm});
            skArc(sketch, "E146.25.2", {"start": v(26.64, 16.92) * mm, "mid": v(26.72, 16.44) * mm, "end": v(26.78, 15.96) * mm});
            skPoint(sketch, "E146.25.3", {"position": v(27.25, 17.04) * mm});
            skArc(sketch, "E146.25.4", {"start": v(27.78, 16.64) * mm, "mid": v(27.64, 16.55) * mm, "end": v(27.5, 16.48) * mm});
            skLineSegment(sketch, "E146.25.5", {"start": v(26.4, 17.85) * mm, "end": v(27.03, 18.04) * mm});
            skArc(sketch, "E146.25.6", {"start": v(27.4, 16.32) * mm, "mid": v(27.41, 16.18) * mm, "end": v(27.43, 16.03) * mm});
            skLineSegment(sketch, "E146.25.7", {"start": v(26.78, 15.96) * mm, "end": v(27.43, 16.03) * mm});
            skArc(sketch, "E146.25.8", {"start": v(27.99, 17.19) * mm, "mid": v(27.96, 16.88) * mm, "end": v(27.78, 16.64) * mm});
            skPoint(sketch, "E146.25.9", {"position": v(26.64, 16.92) * mm});
            skArc(sketch, "E146.25.10", {"start": v(27, 16.99) * mm, "mid": v(27.09, 16.5) * mm, "end": v(27.15, 16) * mm, "construction": true});
            skArc(sketch, "E146.25.11", {"start": v(26.64, 16.92) * mm, "mid": v(26.53, 17.39) * mm, "end": v(26.4, 17.85) * mm});
            skPoint(sketch, "E146.25.12", {"position": v(27, 16.99) * mm});
            skArc(sketch, "E146.25.13", {"start": v(27.11, 17.76) * mm, "mid": v(27.07, 17.9) * mm, "end": v(27.03, 18.04) * mm});
            skArc(sketch, "E146.25.14", {"start": v(27.5, 16.48) * mm, "mid": v(27.42, 16.42) * mm, "end": v(27.4, 16.32) * mm});
            skArc(sketch, "E146.25.15", {"start": v(27.27, 17.64) * mm, "mid": v(27.17, 17.67) * mm, "end": v(27.11, 17.76) * mm});
            skArc(sketch, "E146.26.0", {"start": v(26.87, 19.63) * mm, "mid": v(26.71, 19.63) * mm, "end": v(26.55, 19.6) * mm});
            skArc(sketch, "E146.26.1", {"start": v(27.35, 19.29) * mm, "mid": v(27.16, 19.53) * mm, "end": v(26.87, 19.63) * mm});
            skArc(sketch, "E146.26.2", {"start": v(26.08, 18.76) * mm, "mid": v(26.25, 18.3) * mm, "end": v(26.4, 17.85) * mm});
            skPoint(sketch, "E146.26.3", {"position": v(26.66, 19) * mm});
            skArc(sketch, "E146.26.4", {"start": v(27.25, 18.7) * mm, "mid": v(27.14, 18.6) * mm, "end": v(27, 18.5) * mm});
            skLineSegment(sketch, "E146.26.5", {"start": v(25.66, 19.63) * mm, "end": v(26.24, 19.94) * mm});
            skArc(sketch, "E146.26.6", {"start": v(26.94, 18.33) * mm, "mid": v(26.98, 18.18) * mm, "end": v(27.03, 18.04) * mm});
            skLineSegment(sketch, "E146.26.7", {"start": v(26.4, 17.85) * mm, "end": v(27.03, 18.04) * mm});
            skArc(sketch, "E146.26.8", {"start": v(27.35, 19.29) * mm, "mid": v(27.39, 18.98) * mm, "end": v(27.25, 18.7) * mm});
            skPoint(sketch, "E146.26.9", {"position": v(26.08, 18.76) * mm});
            skArc(sketch, "E146.26.10", {"start": v(26.42, 18.9) * mm, "mid": v(26.6, 18.44) * mm, "end": v(26.76, 17.96) * mm, "construction": true});
            skArc(sketch, "E146.26.11", {"start": v(26.08, 18.76) * mm, "mid": v(25.88, 19.2) * mm, "end": v(25.66, 19.63) * mm});
            skPoint(sketch, "E146.26.12", {"position": v(26.42, 18.9) * mm});
            skArc(sketch, "E146.26.13", {"start": v(26.38, 19.67) * mm, "mid": v(26.31, 19.8) * mm, "end": v(26.24, 19.94) * mm});
            skArc(sketch, "E146.26.14", {"start": v(27, 18.5) * mm, "mid": v(26.94, 18.43) * mm, "end": v(26.94, 18.33) * mm});
            skArc(sketch, "E146.26.15", {"start": v(26.55, 19.6) * mm, "mid": v(26.45, 19.6) * mm, "end": v(26.38, 19.67) * mm});
            skArc(sketch, "E146.27.0", {"start": v(25.78, 21.47) * mm, "mid": v(25.62, 21.43) * mm, "end": v(25.47, 21.37) * mm});
            skArc(sketch, "E146.27.1", {"start": v(26.32, 21.22) * mm, "mid": v(26.08, 21.42) * mm, "end": v(25.78, 21.47) * mm});
            skArc(sketch, "E146.27.2", {"start": v(25.17, 20.46) * mm, "mid": v(25.43, 20.05) * mm, "end": v(25.66, 19.63) * mm});
            skPoint(sketch, "E146.27.3", {"position": v(25.7, 20.8) * mm});
            skArc(sketch, "E146.27.4", {"start": v(26.33, 20.64) * mm, "mid": v(26.24, 20.5) * mm, "end": v(26.13, 20.39) * mm});
            skLineSegment(sketch, "E146.27.5", {"start": v(24.6, 21.23) * mm, "end": v(25.1, 21.65) * mm});
            skArc(sketch, "E146.27.6", {"start": v(26.1, 20.2) * mm, "mid": v(26.17, 20.07) * mm, "end": v(26.24, 19.94) * mm});
            skLineSegment(sketch, "E146.27.7", {"start": v(25.66, 19.63) * mm, "end": v(26.24, 19.94) * mm});
            skArc(sketch, "E146.27.8", {"start": v(26.32, 21.22) * mm, "mid": v(26.4, 20.93) * mm, "end": v(26.33, 20.64) * mm});
            skPoint(sketch, "E146.27.9", {"position": v(25.17, 20.46) * mm});
            skArc(sketch, "E146.27.10", {"start": v(25.48, 20.67) * mm, "mid": v(25.75, 20.24) * mm, "end": v(26, 19.8) * mm, "construction": true});
            skArc(sketch, "E146.27.11", {"start": v(25.17, 20.46) * mm, "mid": v(24.9, 20.85) * mm, "end": v(24.6, 21.23) * mm});
            skPoint(sketch, "E146.27.12", {"position": v(25.48, 20.67) * mm});
            skArc(sketch, "E146.27.13", {"start": v(25.29, 21.41) * mm, "mid": v(25.2, 21.53) * mm, "end": v(25.1, 21.65) * mm});
            skArc(sketch, "E146.27.14", {"start": v(26.13, 20.39) * mm, "mid": v(26.08, 20.3) * mm, "end": v(26.1, 20.2) * mm});
            skArc(sketch, "E146.27.15", {"start": v(25.47, 21.37) * mm, "mid": v(25.37, 21.36) * mm, "end": v(25.29, 21.41) * mm});
            skArc(sketch, "E146.28.0", {"start": v(24.35, 23.05) * mm, "mid": v(24.2, 23) * mm, "end": v(24.07, 22.9) * mm});
            skArc(sketch, "E146.28.1", {"start": v(24.92, 22.92) * mm, "mid": v(24.65, 23.07) * mm, "end": v(24.35, 23.05) * mm});
            skArc(sketch, "E146.28.2", {"start": v(23.95, 21.95) * mm, "mid": v(24.28, 21.6) * mm, "end": v(24.6, 21.23) * mm});
            skPoint(sketch, "E146.28.3", {"position": v(24.4, 22.4) * mm});
            skArc(sketch, "E146.28.4", {"start": v(25.05, 22.35) * mm, "mid": v(25, 22.2) * mm, "end": v(24.9, 22.07) * mm});
            skLineSegment(sketch, "E146.28.5", {"start": v(23.23, 22.6) * mm, "end": v(23.65, 23.1) * mm});
            skArc(sketch, "E146.28.6", {"start": v(24.9, 21.88) * mm, "mid": v(25, 21.76) * mm, "end": v(25.1, 21.65) * mm});
            skLineSegment(sketch, "E146.28.7", {"start": v(24.6, 21.23) * mm, "end": v(25.1, 21.65) * mm});
            skArc(sketch, "E146.28.8", {"start": v(24.92, 22.92) * mm, "mid": v(25.07, 22.65) * mm, "end": v(25.05, 22.35) * mm});
            skPoint(sketch, "E146.28.9", {"position": v(23.95, 21.95) * mm});
            skArc(sketch, "E146.28.10", {"start": v(24.21, 22.21) * mm, "mid": v(24.56, 21.85) * mm, "end": v(24.88, 21.47) * mm, "construction": true});
            skArc(sketch, "E146.28.11", {"start": v(23.95, 21.95) * mm, "mid": v(23.6, 22.28) * mm, "end": v(23.23, 22.6) * mm});
            skPoint(sketch, "E146.28.12", {"position": v(24.21, 22.21) * mm});
            skArc(sketch, "E146.28.13", {"start": v(23.88, 22.9) * mm, "mid": v(23.76, 23) * mm, "end": v(23.65, 23.1) * mm});
            skArc(sketch, "E146.28.14", {"start": v(24.9, 22.07) * mm, "mid": v(24.87, 21.97) * mm, "end": v(24.9, 21.88) * mm});
            skArc(sketch, "E146.28.15", {"start": v(24.07, 22.9) * mm, "mid": v(23.97, 22.87) * mm, "end": v(23.88, 22.9) * mm});
            skArc(sketch, "E146.29.0", {"start": v(22.64, 24.33) * mm, "mid": v(22.5, 24.24) * mm, "end": v(22.39, 24.13) * mm});
            skArc(sketch, "E146.29.1", {"start": v(23.22, 24.32) * mm, "mid": v(22.93, 24.4) * mm, "end": v(22.64, 24.33) * mm});
            skArc(sketch, "E146.29.2", {"start": v(22.46, 23.17) * mm, "mid": v(22.85, 22.9) * mm, "end": v(23.23, 22.6) * mm});
            skPoint(sketch, "E146.29.3", {"position": v(22.8, 23.7) * mm});
            skArc(sketch, "E146.29.4", {"start": v(23.47, 23.78) * mm, "mid": v(23.43, 23.62) * mm, "end": v(23.37, 23.47) * mm});
            skLineSegment(sketch, "E146.29.5", {"start": v(21.63, 23.66) * mm, "end": v(21.94, 24.24) * mm});
            skArc(sketch, "E146.29.6", {"start": v(23.41, 23.29) * mm, "mid": v(23.53, 23.2) * mm, "end": v(23.65, 23.1) * mm});
            skLineSegment(sketch, "E146.29.7", {"start": v(23.23, 22.6) * mm, "end": v(23.65, 23.1) * mm});
            skArc(sketch, "E146.29.8", {"start": v(23.22, 24.32) * mm, "mid": v(23.42, 24.08) * mm, "end": v(23.47, 23.78) * mm});
            skPoint(sketch, "E146.29.9", {"position": v(22.46, 23.17) * mm});
            skArc(sketch, "E146.29.10", {"start": v(22.67, 23.48) * mm, "mid": v(23.08, 23.2) * mm, "end": v(23.47, 22.88) * mm, "construction": true});
            skArc(sketch, "E146.29.11", {"start": v(22.46, 23.17) * mm, "mid": v(22.05, 23.43) * mm, "end": v(21.63, 23.66) * mm});
            skPoint(sketch, "E146.29.12", {"position": v(22.67, 23.48) * mm});
            skArc(sketch, "E146.29.13", {"start": v(22.2, 24.1) * mm, "mid": v(22.07, 24.17) * mm, "end": v(21.94, 24.24) * mm});
            skArc(sketch, "E146.29.14", {"start": v(23.37, 23.47) * mm, "mid": v(23.36, 23.37) * mm, "end": v(23.41, 23.29) * mm});
            skArc(sketch, "E146.29.15", {"start": v(22.39, 24.13) * mm, "mid": v(22.3, 24.08) * mm, "end": v(22.2, 24.1) * mm});
            skArc(sketch, "E146.30.0", {"start": v(20.7, 25.25) * mm, "mid": v(20.6, 25.14) * mm, "end": v(20.5, 25) * mm});
            skArc(sketch, "E146.30.1", {"start": v(21.29, 25.35) * mm, "mid": v(20.98, 25.39) * mm, "end": v(20.7, 25.25) * mm});
            skArc(sketch, "E146.30.2", {"start": v(20.76, 24.08) * mm, "mid": v(21.2, 23.88) * mm, "end": v(21.63, 23.66) * mm});
            skPoint(sketch, "E146.30.3", {"position": v(21, 24.66) * mm});
            skArc(sketch, "E146.30.4", {"start": v(21.63, 24.87) * mm, "mid": v(21.63, 24.71) * mm, "end": v(21.6, 24.55) * mm});
            skLineSegment(sketch, "E146.30.5", {"start": v(19.85, 24.4) * mm, "end": v(20.04, 25.03) * mm});
            skArc(sketch, "E146.30.6", {"start": v(21.67, 24.38) * mm, "mid": v(21.8, 24.31) * mm, "end": v(21.94, 24.24) * mm});
            skLineSegment(sketch, "E146.30.7", {"start": v(21.63, 23.66) * mm, "end": v(21.94, 24.24) * mm});
            skArc(sketch, "E146.30.8", {"start": v(21.29, 25.35) * mm, "mid": v(21.53, 25.16) * mm, "end": v(21.63, 24.87) * mm});
            skPoint(sketch, "E146.30.9", {"position": v(20.76, 24.08) * mm});
            skArc(sketch, "E146.30.10", {"start": v(20.9, 24.42) * mm, "mid": v(21.36, 24.22) * mm, "end": v(21.8, 24) * mm, "construction": true});
            skArc(sketch, "E146.30.11", {"start": v(20.76, 24.08) * mm, "mid": v(20.3, 24.25) * mm, "end": v(19.85, 24.4) * mm});
            skPoint(sketch, "E146.30.12", {"position": v(20.9, 24.42) * mm});
            skArc(sketch, "E146.30.13", {"start": v(20.33, 24.94) * mm, "mid": v(20.18, 24.98) * mm, "end": v(20.04, 25.03) * mm});
            skArc(sketch, "E146.30.14", {"start": v(21.6, 24.55) * mm, "mid": v(21.6, 24.45) * mm, "end": v(21.67, 24.38) * mm});
            skArc(sketch, "E146.30.15", {"start": v(20.5, 25) * mm, "mid": v(20.43, 24.94) * mm, "end": v(20.33, 24.94) * mm});
            skArc(sketch, "E146.31.0", {"start": v(18.64, 25.78) * mm, "mid": v(18.55, 25.64) * mm, "end": v(18.48, 25.5) * mm});
            skArc(sketch, "E146.31.1", {"start": v(19.19, 25.99) * mm, "mid": v(18.88, 25.96) * mm, "end": v(18.64, 25.78) * mm});
            skArc(sketch, "E146.31.2", {"start": v(18.92, 24.64) * mm, "mid": v(19.39, 24.53) * mm, "end": v(19.85, 24.4) * mm});
            skPoint(sketch, "E146.31.3", {"position": v(19.04, 25.25) * mm});
            skArc(sketch, "E146.31.4", {"start": v(19.61, 25.59) * mm, "mid": v(19.64, 25.43) * mm, "end": v(19.64, 25.27) * mm});
            skArc(sketch, "E146.31.6", {"start": v(19.76, 25.11) * mm, "mid": v(19.9, 25.07) * mm, "end": v(20.04, 25.03) * mm});
            skLineSegment(sketch, "E146.31.7", {"start": v(19.85, 24.4) * mm, "end": v(20.04, 25.03) * mm});
            skArc(sketch, "E146.31.8", {"start": v(19.19, 25.99) * mm, "mid": v(19.46, 25.85) * mm, "end": v(19.61, 25.59) * mm});
            skPoint(sketch, "E146.31.9", {"position": v(18.92, 24.64) * mm});
            skArc(sketch, "E146.31.10", {"start": v(18.99, 25) * mm, "mid": v(19.48, 24.9) * mm, "end": v(19.96, 24.76) * mm, "construction": true});
            skArc(sketch, "E146.31.11", {"start": v(18.92, 24.64) * mm, "mid": v(18.44, 24.72) * mm, "end": v(17.96, 24.78) * mm});
            skPoint(sketch, "E146.31.12", {"position": v(18.99, 25) * mm});
            skArc(sketch, "E146.31.13", {"start": v(18.32, 25.4) * mm, "mid": v(18.18, 25.41) * mm, "end": v(18.03, 25.43) * mm});
            skArc(sketch, "E146.31.14", {"start": v(19.64, 25.27) * mm, "mid": v(19.67, 25.17) * mm, "end": v(19.76, 25.11) * mm});
            skArc(sketch, "E146.31.15", {"start": v(18.48, 25.5) * mm, "mid": v(18.42, 25.42) * mm, "end": v(18.32, 25.4) * mm});
            skLineSegment(sketch, "E147.0", {"start": v(6.75, 15) * mm, "end": v(27.25, 15) * mm, "construction": true});
            skSolve(sketch);
        }
        {
            var Q0;
            Q0 = qSketchRegion(id + "F22", true);
            extrude(context, id + "F23", {"entities" : qUnion([Q0]), "operationType" : NewBodyOperationType.REMOVE, "endBound" : BoundingType.SYMMETRIC, "oppositeDirection" : true, "depth" : 6.5 * mm});
        }
        {
            var Q0;
            Q0=makeQuery(id+"F2.boolean.opBoolean","MERGE",FACE,{"derivedFrom":[makeQuery(id+"F1.opExtrude","SWEPT_FACE",FACE,{"disambiguationData":[OSD([sQuery(id+"F0.wireOp",EDGE,"E0.right"),sQuery(id+"F0.wireOp",EDGE,"E25")])]}),makeQuery(id+"F2.opExtrude","SWEPT_FACE",FACE,{"disambiguationData":[OSD([sQuery(id+"F0.wireOp",EDGE,"E31")])]})]});
            var Q1;
            Q1=sQuery(id+"F0.wireOp",VERTEX,"E12.MirrorP");
            cPlane(context, id + "F24", {"entities" : qUnion([Q0, Q1]), "cplaneType" : CPlaneType.PLANE_POINT, "offset" : 150 * mm, "width" : 150 * mm, "height" : 150 * mm});
        }
        {
            var Q0;
            Q0=qCreatedBy(id+"F24.planeOp",FACE);
            var sketch = newSketch(context, id + "F25", { "sketchPlane" : qUnion([Q0])});
            skLineSegment(sketch, "E148", {"start": v(17, 12.16) * mm, "end": v(17, 9.53) * mm, "construction": true});
            skArc(sketch, "E149", {"start": v(17, 26.2) * mm, "mid": v(17.3, 26.12) * mm, "end": v(17.5, 25.9) * mm});
            skArc(sketch, "E150", {"start": v(17.5, 25.9) * mm, "mid": v(17.56, 25.74) * mm, "end": v(17.6, 25.58) * mm});
            skArc(sketch, "E151", {"start": v(17.6, 25.58) * mm, "mid": v(17.64, 25.5) * mm, "end": v(17.73, 25.45) * mm});
            skPoint(sketch, "E152", {"position": v(17, 24.82) * mm});
            skPoint(sketch, "E153", {"position": v(17, 25.45) * mm});
            skPoint(sketch, "E154", {"position": v(17, 25.2) * mm});
            skArc(sketch, "E155", {"start": v(17, 25.2) * mm, "mid": v(17.5, 25.19) * mm, "end": v(18, 25.15) * mm, "construction": true});
            skLineSegment(sketch, "E156", {"start": v(17.96, 24.78) * mm, "end": v(18.03, 25.43) * mm});
            skArc(sketch, "E157", {"start": v(17.73, 25.45) * mm, "mid": v(17.88, 25.44) * mm, "end": v(18.03, 25.43) * mm});
            skArc(sketch, "E158", {"start": v(17, 24.82) * mm, "mid": v(17.48, 24.81) * mm, "end": v(17.96, 24.78) * mm});
            skArc(sketch, "E159.MirrorCS", {"start": v(17, 26.2) * mm, "mid": v(16.7, 26.12) * mm, "end": v(16.5, 25.9) * mm});
            skArc(sketch, "E160.MirrorCS", {"start": v(16.5, 25.9) * mm, "mid": v(16.44, 25.74) * mm, "end": v(16.4, 25.58) * mm});
            skArc(sketch, "E161.MirrorCS", {"start": v(16.4, 25.58) * mm, "mid": v(16.36, 25.5) * mm, "end": v(16.27, 25.45) * mm});
            skArc(sketch, "E162.MirrorCS", {"start": v(16.27, 25.45) * mm, "mid": v(16.12, 25.44) * mm, "end": v(15.97, 25.43) * mm});
            skLineSegment(sketch, "E163.MirrorCS", {"start": v(16.04, 24.78) * mm, "end": v(15.97, 25.43) * mm});
            skArc(sketch, "E164.MirrorCS", {"start": v(17, 24.82) * mm, "mid": v(16.52, 24.81) * mm, "end": v(16.04, 24.78) * mm});
            skArc(sketch, "E165.1.0", {"start": v(14.39, 25.59) * mm, "mid": v(14.36, 25.43) * mm, "end": v(14.36, 25.27) * mm});
            skArc(sketch, "E165.1.1", {"start": v(14.81, 25.99) * mm, "mid": v(14.54, 25.85) * mm, "end": v(14.39, 25.59) * mm});
            skArc(sketch, "E165.1.2", {"start": v(15.08, 24.64) * mm, "mid": v(15.56, 24.72) * mm, "end": v(16.04, 24.78) * mm});
            skPoint(sketch, "E165.1.3", {"position": v(14.96, 25.25) * mm});
            skArc(sketch, "E165.1.4", {"start": v(15.36, 25.78) * mm, "mid": v(15.45, 25.64) * mm, "end": v(15.52, 25.5) * mm});
            skLineSegment(sketch, "E165.1.5", {"start": v(14.15, 24.4) * mm, "end": v(13.96, 25.03) * mm});
            skArc(sketch, "E165.1.6", {"start": v(15.68, 25.4) * mm, "mid": v(15.82, 25.41) * mm, "end": v(15.97, 25.43) * mm});
            skArc(sketch, "E165.1.8", {"start": v(14.81, 25.99) * mm, "mid": v(15.12, 25.96) * mm, "end": v(15.36, 25.78) * mm});
            skPoint(sketch, "E165.1.9", {"position": v(15.08, 24.64) * mm});
            skArc(sketch, "E165.1.10", {"start": v(15.01, 25) * mm, "mid": v(15.5, 25.09) * mm, "end": v(16, 25.15) * mm, "construction": true});
            skArc(sketch, "E165.1.11", {"start": v(15.08, 24.64) * mm, "mid": v(14.61, 24.53) * mm, "end": v(14.15, 24.4) * mm});
            skPoint(sketch, "E165.1.12", {"position": v(15.01, 25) * mm});
            skArc(sketch, "E165.1.13", {"start": v(14.24, 25.11) * mm, "mid": v(14.1, 25.07) * mm, "end": v(13.96, 25.03) * mm});
            skArc(sketch, "E165.1.14", {"start": v(15.52, 25.5) * mm, "mid": v(15.58, 25.42) * mm, "end": v(15.68, 25.4) * mm});
            skArc(sketch, "E165.1.15", {"start": v(14.36, 25.27) * mm, "mid": v(14.33, 25.17) * mm, "end": v(14.24, 25.11) * mm});
            skArc(sketch, "E165.2.0", {"start": v(12.37, 24.87) * mm, "mid": v(12.37, 24.71) * mm, "end": v(12.4, 24.55) * mm});
            skArc(sketch, "E165.2.1", {"start": v(12.71, 25.35) * mm, "mid": v(12.47, 25.16) * mm, "end": v(12.37, 24.87) * mm});
            skArc(sketch, "E165.2.2", {"start": v(13.24, 24.08) * mm, "mid": v(13.7, 24.25) * mm, "end": v(14.15, 24.4) * mm});
            skPoint(sketch, "E165.2.3", {"position": v(13, 24.66) * mm});
            skArc(sketch, "E165.2.4", {"start": v(13.3, 25.25) * mm, "mid": v(13.4, 25.14) * mm, "end": v(13.5, 25) * mm});
            skLineSegment(sketch, "E165.2.5", {"start": v(12.37, 23.66) * mm, "end": v(12.06, 24.24) * mm});
            skArc(sketch, "E165.2.6", {"start": v(13.67, 24.94) * mm, "mid": v(13.82, 24.98) * mm, "end": v(13.96, 25.03) * mm});
            skLineSegment(sketch, "E165.2.7", {"start": v(14.15, 24.4) * mm, "end": v(13.96, 25.03) * mm});
            skArc(sketch, "E165.2.8", {"start": v(12.71, 25.35) * mm, "mid": v(13.02, 25.39) * mm, "end": v(13.3, 25.25) * mm});
            skPoint(sketch, "E165.2.9", {"position": v(13.24, 24.08) * mm});
            skArc(sketch, "E165.2.10", {"start": v(13.1, 24.42) * mm, "mid": v(13.56, 24.6) * mm, "end": v(14.04, 24.76) * mm, "construction": true});
            skArc(sketch, "E165.2.11", {"start": v(13.24, 24.08) * mm, "mid": v(12.8, 23.88) * mm, "end": v(12.37, 23.66) * mm});
            skPoint(sketch, "E165.2.12", {"position": v(13.1, 24.42) * mm});
            skArc(sketch, "E165.2.13", {"start": v(12.33, 24.38) * mm, "mid": v(12.2, 24.31) * mm, "end": v(12.06, 24.24) * mm});
            skArc(sketch, "E165.2.14", {"start": v(13.5, 25) * mm, "mid": v(13.57, 24.94) * mm, "end": v(13.67, 24.94) * mm});
            skArc(sketch, "E165.2.15", {"start": v(12.4, 24.55) * mm, "mid": v(12.4, 24.45) * mm, "end": v(12.33, 24.38) * mm});
            skArc(sketch, "E165.3.0", {"start": v(10.53, 23.78) * mm, "mid": v(10.57, 23.62) * mm, "end": v(10.63, 23.47) * mm});
            skArc(sketch, "E165.3.1", {"start": v(10.78, 24.32) * mm, "mid": v(10.58, 24.08) * mm, "end": v(10.53, 23.78) * mm});
            skArc(sketch, "E165.3.2", {"start": v(11.54, 23.17) * mm, "mid": v(11.95, 23.43) * mm, "end": v(12.37, 23.66) * mm});
            skPoint(sketch, "E165.3.3", {"position": v(11.2, 23.7) * mm});
            skArc(sketch, "E165.3.4", {"start": v(11.36, 24.33) * mm, "mid": v(11.5, 24.24) * mm, "end": v(11.61, 24.13) * mm});
            skLineSegment(sketch, "E165.3.5", {"start": v(10.77, 22.6) * mm, "end": v(10.35, 23.1) * mm});
            skArc(sketch, "E165.3.6", {"start": v(11.8, 24.1) * mm, "mid": v(11.93, 24.17) * mm, "end": v(12.06, 24.24) * mm});
            skLineSegment(sketch, "E165.3.7", {"start": v(12.37, 23.66) * mm, "end": v(12.06, 24.24) * mm});
            skArc(sketch, "E165.3.8", {"start": v(10.78, 24.32) * mm, "mid": v(11.07, 24.4) * mm, "end": v(11.36, 24.33) * mm});
            skPoint(sketch, "E165.3.9", {"position": v(11.54, 23.17) * mm});
            skArc(sketch, "E165.3.10", {"start": v(11.33, 23.48) * mm, "mid": v(11.76, 23.75) * mm, "end": v(12.2, 24) * mm, "construction": true});
            skArc(sketch, "E165.3.11", {"start": v(11.54, 23.17) * mm, "mid": v(11.15, 22.9) * mm, "end": v(10.77, 22.6) * mm});
            skPoint(sketch, "E165.3.12", {"position": v(11.33, 23.48) * mm});
            skArc(sketch, "E165.3.13", {"start": v(10.59, 23.29) * mm, "mid": v(10.47, 23.2) * mm, "end": v(10.35, 23.1) * mm});
            skArc(sketch, "E165.3.14", {"start": v(11.61, 24.13) * mm, "mid": v(11.7, 24.08) * mm, "end": v(11.8, 24.1) * mm});
            skArc(sketch, "E165.3.15", {"start": v(10.63, 23.47) * mm, "mid": v(10.64, 23.37) * mm, "end": v(10.59, 23.29) * mm});
            skArc(sketch, "E165.4.0", {"start": v(8.95, 22.35) * mm, "mid": v(9, 22.2) * mm, "end": v(9.1, 22.07) * mm});
            skArc(sketch, "E165.4.1", {"start": v(9.08, 22.92) * mm, "mid": v(8.93, 22.65) * mm, "end": v(8.95, 22.35) * mm});
            skArc(sketch, "E165.4.2", {"start": v(10.05, 21.95) * mm, "mid": v(10.4, 22.28) * mm, "end": v(10.77, 22.6) * mm});
            skPoint(sketch, "E165.4.3", {"position": v(9.6, 22.4) * mm});
            skArc(sketch, "E165.4.4", {"start": v(9.65, 23.05) * mm, "mid": v(9.8, 23) * mm, "end": v(9.93, 22.9) * mm});
            skLineSegment(sketch, "E165.4.5", {"start": v(9.4, 21.23) * mm, "end": v(8.9, 21.65) * mm});
            skArc(sketch, "E165.4.6", {"start": v(10.12, 22.9) * mm, "mid": v(10.24, 23) * mm, "end": v(10.35, 23.1) * mm});
            skLineSegment(sketch, "E165.4.7", {"start": v(10.77, 22.6) * mm, "end": v(10.35, 23.1) * mm});
            skArc(sketch, "E165.4.8", {"start": v(9.08, 22.92) * mm, "mid": v(9.35, 23.07) * mm, "end": v(9.65, 23.05) * mm});
            skPoint(sketch, "E165.4.9", {"position": v(10.05, 21.95) * mm});
            skArc(sketch, "E165.4.10", {"start": v(9.79, 22.21) * mm, "mid": v(10.15, 22.56) * mm, "end": v(10.53, 22.88) * mm, "construction": true});
            skArc(sketch, "E165.4.11", {"start": v(10.05, 21.95) * mm, "mid": v(9.72, 21.6) * mm, "end": v(9.4, 21.23) * mm});
            skPoint(sketch, "E165.4.12", {"position": v(9.79, 22.21) * mm});
            skArc(sketch, "E165.4.13", {"start": v(9.1, 21.88) * mm, "mid": v(9, 21.76) * mm, "end": v(8.9, 21.65) * mm});
            skArc(sketch, "E165.4.14", {"start": v(9.93, 22.9) * mm, "mid": v(10.03, 22.87) * mm, "end": v(10.12, 22.9) * mm});
            skArc(sketch, "E165.4.15", {"start": v(9.1, 22.07) * mm, "mid": v(9.13, 21.97) * mm, "end": v(9.1, 21.88) * mm});
            skArc(sketch, "E165.5.0", {"start": v(7.67, 20.64) * mm, "mid": v(7.76, 20.5) * mm, "end": v(7.87, 20.39) * mm});
            skArc(sketch, "E165.5.1", {"start": v(7.68, 21.22) * mm, "mid": v(7.6, 20.93) * mm, "end": v(7.67, 20.64) * mm});
            skArc(sketch, "E165.5.2", {"start": v(8.83, 20.46) * mm, "mid": v(9.1, 20.85) * mm, "end": v(9.4, 21.23) * mm});
            skPoint(sketch, "E165.5.3", {"position": v(8.3, 20.8) * mm});
            skArc(sketch, "E165.5.4", {"start": v(8.22, 21.47) * mm, "mid": v(8.38, 21.43) * mm, "end": v(8.53, 21.37) * mm});
            skLineSegment(sketch, "E165.5.5", {"start": v(8.34, 19.63) * mm, "end": v(7.76, 19.94) * mm});
            skArc(sketch, "E165.5.6", {"start": v(8.71, 21.41) * mm, "mid": v(8.8, 21.53) * mm, "end": v(8.9, 21.65) * mm});
            skLineSegment(sketch, "E165.5.7", {"start": v(9.4, 21.23) * mm, "end": v(8.9, 21.65) * mm});
            skArc(sketch, "E165.5.8", {"start": v(7.68, 21.22) * mm, "mid": v(7.92, 21.42) * mm, "end": v(8.22, 21.47) * mm});
            skPoint(sketch, "E165.5.9", {"position": v(8.83, 20.46) * mm});
            skArc(sketch, "E165.5.10", {"start": v(8.52, 20.67) * mm, "mid": v(8.8, 21.08) * mm, "end": v(9.12, 21.47) * mm, "construction": true});
            skArc(sketch, "E165.5.11", {"start": v(8.83, 20.46) * mm, "mid": v(8.57, 20.05) * mm, "end": v(8.34, 19.63) * mm});
            skPoint(sketch, "E165.5.12", {"position": v(8.52, 20.67) * mm});
            skArc(sketch, "E165.5.13", {"start": v(7.9, 20.2) * mm, "mid": v(7.83, 20.07) * mm, "end": v(7.76, 19.94) * mm});
            skArc(sketch, "E165.5.14", {"start": v(8.53, 21.37) * mm, "mid": v(8.63, 21.36) * mm, "end": v(8.71, 21.41) * mm});
            skArc(sketch, "E165.5.15", {"start": v(7.87, 20.39) * mm, "mid": v(7.92, 20.3) * mm, "end": v(7.9, 20.2) * mm});
            skArc(sketch, "E165.6.0", {"start": v(6.75, 18.7) * mm, "mid": v(6.86, 18.6) * mm, "end": v(7, 18.5) * mm});
            skArc(sketch, "E165.6.1", {"start": v(6.65, 19.29) * mm, "mid": v(6.61, 18.98) * mm, "end": v(6.75, 18.7) * mm});
            skArc(sketch, "E165.6.2", {"start": v(7.92, 18.76) * mm, "mid": v(8.12, 19.2) * mm, "end": v(8.34, 19.63) * mm});
            skPoint(sketch, "E165.6.3", {"position": v(7.34, 19) * mm});
            skArc(sketch, "E165.6.4", {"start": v(7.13, 19.63) * mm, "mid": v(7.29, 19.63) * mm, "end": v(7.45, 19.6) * mm});
            skLineSegment(sketch, "E165.6.5", {"start": v(7.6, 17.85) * mm, "end": v(6.97, 18.04) * mm});
            skArc(sketch, "E165.6.6", {"start": v(7.62, 19.67) * mm, "mid": v(7.69, 19.8) * mm, "end": v(7.76, 19.94) * mm});
            skLineSegment(sketch, "E165.6.7", {"start": v(8.34, 19.63) * mm, "end": v(7.76, 19.94) * mm});
            skArc(sketch, "E165.6.8", {"start": v(6.65, 19.29) * mm, "mid": v(6.84, 19.53) * mm, "end": v(7.13, 19.63) * mm});
            skPoint(sketch, "E165.6.9", {"position": v(7.92, 18.76) * mm});
            skArc(sketch, "E165.6.10", {"start": v(7.58, 18.9) * mm, "mid": v(7.78, 19.36) * mm, "end": v(8, 19.8) * mm, "construction": true});
            skArc(sketch, "E165.6.11", {"start": v(7.92, 18.76) * mm, "mid": v(7.75, 18.3) * mm, "end": v(7.6, 17.85) * mm});
            skPoint(sketch, "E165.6.12", {"position": v(7.58, 18.9) * mm});
            skArc(sketch, "E165.6.13", {"start": v(7.06, 18.33) * mm, "mid": v(7.02, 18.18) * mm, "end": v(6.97, 18.04) * mm});
            skArc(sketch, "E165.6.14", {"start": v(7.45, 19.6) * mm, "mid": v(7.55, 19.6) * mm, "end": v(7.62, 19.67) * mm});
            skArc(sketch, "E165.6.15", {"start": v(7, 18.5) * mm, "mid": v(7.06, 18.43) * mm, "end": v(7.06, 18.33) * mm});
            skArc(sketch, "E165.7.0", {"start": v(6.22, 16.64) * mm, "mid": v(6.36, 16.55) * mm, "end": v(6.5, 16.48) * mm});
            skArc(sketch, "E165.7.1", {"start": v(6.01, 17.19) * mm, "mid": v(6.04, 16.88) * mm, "end": v(6.22, 16.64) * mm});
            skArc(sketch, "E165.7.2", {"start": v(7.36, 16.92) * mm, "mid": v(7.47, 17.39) * mm, "end": v(7.6, 17.85) * mm});
            skPoint(sketch, "E165.7.3", {"position": v(6.75, 17.04) * mm});
            skArc(sketch, "E165.7.4", {"start": v(6.41, 17.61) * mm, "mid": v(6.57, 17.64) * mm, "end": v(6.73, 17.64) * mm});
            skLineSegment(sketch, "E165.7.5", {"start": v(7.22, 15.96) * mm, "end": v(6.57, 16.03) * mm});
            skArc(sketch, "E165.7.6", {"start": v(6.89, 17.76) * mm, "mid": v(6.93, 17.9) * mm, "end": v(6.97, 18.04) * mm});
            skLineSegment(sketch, "E165.7.7", {"start": v(7.6, 17.85) * mm, "end": v(6.97, 18.04) * mm});
            skArc(sketch, "E165.7.8", {"start": v(6.01, 17.19) * mm, "mid": v(6.15, 17.46) * mm, "end": v(6.41, 17.61) * mm});
            skPoint(sketch, "E165.7.9", {"position": v(7.36, 16.92) * mm});
            skArc(sketch, "E165.7.10", {"start": v(7, 16.99) * mm, "mid": v(7.1, 17.48) * mm, "end": v(7.24, 17.96) * mm, "construction": true});
            skArc(sketch, "E165.7.11", {"start": v(7.36, 16.92) * mm, "mid": v(7.28, 16.44) * mm, "end": v(7.22, 15.96) * mm});
            skPoint(sketch, "E165.7.12", {"position": v(7, 16.99) * mm});
            skArc(sketch, "E165.7.13", {"start": v(6.6, 16.32) * mm, "mid": v(6.59, 16.18) * mm, "end": v(6.57, 16.03) * mm});
            skArc(sketch, "E165.7.14", {"start": v(6.73, 17.64) * mm, "mid": v(6.83, 17.67) * mm, "end": v(6.89, 17.76) * mm});
            skArc(sketch, "E165.7.15", {"start": v(6.5, 16.48) * mm, "mid": v(6.58, 16.42) * mm, "end": v(6.6, 16.32) * mm});
            skArc(sketch, "E165.8.0", {"start": v(6.1, 14.5) * mm, "mid": v(6.26, 14.44) * mm, "end": v(6.42, 14.4) * mm});
            skArc(sketch, "E165.8.1", {"start": v(5.8, 15) * mm, "mid": v(5.88, 14.7) * mm, "end": v(6.1, 14.5) * mm});
            skArc(sketch, "E165.8.2", {"start": v(7.18, 15) * mm, "mid": v(7.19, 15.48) * mm, "end": v(7.22, 15.96) * mm});
            skPoint(sketch, "E165.8.3", {"position": v(6.55, 15) * mm});
            skArc(sketch, "E165.8.4", {"start": v(6.1, 15.5) * mm, "mid": v(6.26, 15.56) * mm, "end": v(6.42, 15.6) * mm});
            skLineSegment(sketch, "E165.8.5", {"start": v(7.22, 14.04) * mm, "end": v(6.57, 13.97) * mm});
            skArc(sketch, "E165.8.6", {"start": v(6.55, 15.73) * mm, "mid": v(6.56, 15.88) * mm, "end": v(6.57, 16.03) * mm});
            skLineSegment(sketch, "E165.8.7", {"start": v(7.22, 15.96) * mm, "end": v(6.57, 16.03) * mm});
            skArc(sketch, "E165.8.8", {"start": v(5.8, 15) * mm, "mid": v(5.88, 15.3) * mm, "end": v(6.1, 15.5) * mm});
            skPoint(sketch, "E165.8.9", {"position": v(7.18, 15) * mm});
            skArc(sketch, "E165.8.10", {"start": v(6.8, 15) * mm, "mid": v(6.81, 15.5) * mm, "end": v(6.85, 16) * mm, "construction": true});
            skArc(sketch, "E165.8.11", {"start": v(7.18, 15) * mm, "mid": v(7.19, 14.52) * mm, "end": v(7.22, 14.04) * mm});
            skPoint(sketch, "E165.8.12", {"position": v(6.8, 15) * mm});
            skArc(sketch, "E165.8.13", {"start": v(6.55, 14.27) * mm, "mid": v(6.56, 14.12) * mm, "end": v(6.57, 13.97) * mm});
            skArc(sketch, "E165.8.14", {"start": v(6.42, 15.6) * mm, "mid": v(6.5, 15.64) * mm, "end": v(6.55, 15.73) * mm});
            skArc(sketch, "E165.8.15", {"start": v(6.42, 14.4) * mm, "mid": v(6.5, 14.36) * mm, "end": v(6.55, 14.27) * mm});
            skArc(sketch, "E165.9.0", {"start": v(6.41, 12.39) * mm, "mid": v(6.57, 12.36) * mm, "end": v(6.73, 12.36) * mm});
            skArc(sketch, "E165.9.1", {"start": v(6.01, 12.81) * mm, "mid": v(6.15, 12.54) * mm, "end": v(6.41, 12.39) * mm});
            skArc(sketch, "E165.9.2", {"start": v(7.36, 13.08) * mm, "mid": v(7.28, 13.56) * mm, "end": v(7.22, 14.04) * mm});
            skPoint(sketch, "E165.9.3", {"position": v(6.75, 12.96) * mm});
            skArc(sketch, "E165.9.4", {"start": v(6.22, 13.36) * mm, "mid": v(6.36, 13.45) * mm, "end": v(6.5, 13.52) * mm});
            skLineSegment(sketch, "E165.9.5", {"start": v(7.6, 12.15) * mm, "end": v(6.97, 11.96) * mm});
            skArc(sketch, "E165.9.6", {"start": v(6.6, 13.68) * mm, "mid": v(6.59, 13.82) * mm, "end": v(6.57, 13.97) * mm});
            skLineSegment(sketch, "E165.9.7", {"start": v(7.22, 14.04) * mm, "end": v(6.57, 13.97) * mm});
            skArc(sketch, "E165.9.8", {"start": v(6.01, 12.81) * mm, "mid": v(6.04, 13.12) * mm, "end": v(6.22, 13.36) * mm});
            skPoint(sketch, "E165.9.9", {"position": v(7.36, 13.08) * mm});
            skArc(sketch, "E165.9.10", {"start": v(7, 13.01) * mm, "mid": v(6.91, 13.5) * mm, "end": v(6.85, 14) * mm, "construction": true});
            skArc(sketch, "E165.9.11", {"start": v(7.36, 13.08) * mm, "mid": v(7.47, 12.61) * mm, "end": v(7.6, 12.15) * mm});
            skPoint(sketch, "E165.9.12", {"position": v(7, 13.01) * mm});
            skArc(sketch, "E165.9.13", {"start": v(6.89, 12.24) * mm, "mid": v(6.93, 12.1) * mm, "end": v(6.97, 11.96) * mm});
            skArc(sketch, "E165.9.14", {"start": v(6.5, 13.52) * mm, "mid": v(6.58, 13.58) * mm, "end": v(6.6, 13.68) * mm});
            skArc(sketch, "E165.9.15", {"start": v(6.73, 12.36) * mm, "mid": v(6.83, 12.33) * mm, "end": v(6.89, 12.24) * mm});
            skArc(sketch, "E165.10.0", {"start": v(7.13, 10.37) * mm, "mid": v(7.29, 10.37) * mm, "end": v(7.45, 10.4) * mm});
            skArc(sketch, "E165.10.1", {"start": v(6.65, 10.71) * mm, "mid": v(6.84, 10.47) * mm, "end": v(7.13, 10.37) * mm});
            skArc(sketch, "E165.10.2", {"start": v(7.92, 11.24) * mm, "mid": v(7.75, 11.7) * mm, "end": v(7.6, 12.15) * mm});
            skPoint(sketch, "E165.10.3", {"position": v(7.34, 11) * mm});
            skArc(sketch, "E165.10.4", {"start": v(6.75, 11.3) * mm, "mid": v(6.86, 11.4) * mm, "end": v(7, 11.5) * mm});
            skLineSegment(sketch, "E165.10.5", {"start": v(8.34, 10.37) * mm, "end": v(7.76, 10.06) * mm});
            skArc(sketch, "E165.10.6", {"start": v(7.06, 11.67) * mm, "mid": v(7.02, 11.82) * mm, "end": v(6.97, 11.96) * mm});
            skLineSegment(sketch, "E165.10.7", {"start": v(7.6, 12.15) * mm, "end": v(6.97, 11.96) * mm});
            skArc(sketch, "E165.10.8", {"start": v(6.65, 10.71) * mm, "mid": v(6.61, 11.02) * mm, "end": v(6.75, 11.3) * mm});
            skPoint(sketch, "E165.10.9", {"position": v(7.92, 11.24) * mm});
            skArc(sketch, "E165.10.10", {"start": v(7.58, 11.1) * mm, "mid": v(7.4, 11.56) * mm, "end": v(7.24, 12.04) * mm, "construction": true});
            skArc(sketch, "E165.10.11", {"start": v(7.92, 11.24) * mm, "mid": v(8.12, 10.8) * mm, "end": v(8.34, 10.37) * mm});
            skPoint(sketch, "E165.10.12", {"position": v(7.58, 11.1) * mm});
            skArc(sketch, "E165.10.13", {"start": v(7.62, 10.33) * mm, "mid": v(7.69, 10.2) * mm, "end": v(7.76, 10.06) * mm});
            skArc(sketch, "E165.10.14", {"start": v(7, 11.5) * mm, "mid": v(7.06, 11.57) * mm, "end": v(7.06, 11.67) * mm});
            skArc(sketch, "E165.10.15", {"start": v(7.45, 10.4) * mm, "mid": v(7.55, 10.4) * mm, "end": v(7.62, 10.33) * mm});
            skArc(sketch, "E165.11.0", {"start": v(8.22, 8.53) * mm, "mid": v(8.38, 8.57) * mm, "end": v(8.53, 8.63) * mm});
            skArc(sketch, "E165.11.1", {"start": v(7.68, 8.78) * mm, "mid": v(7.92, 8.58) * mm, "end": v(8.22, 8.53) * mm});
            skArc(sketch, "E165.11.2", {"start": v(8.83, 9.54) * mm, "mid": v(8.57, 9.95) * mm, "end": v(8.34, 10.37) * mm});
            skPoint(sketch, "E165.11.3", {"position": v(8.3, 9.2) * mm});
            skArc(sketch, "E165.11.4", {"start": v(7.67, 9.36) * mm, "mid": v(7.76, 9.5) * mm, "end": v(7.87, 9.61) * mm});
            skLineSegment(sketch, "E165.11.5", {"start": v(9.4, 8.77) * mm, "end": v(8.9, 8.35) * mm});
            skArc(sketch, "E165.11.6", {"start": v(7.9, 9.8) * mm, "mid": v(7.83, 9.93) * mm, "end": v(7.76, 10.06) * mm});
            skLineSegment(sketch, "E165.11.7", {"start": v(8.34, 10.37) * mm, "end": v(7.76, 10.06) * mm});
            skArc(sketch, "E165.11.8", {"start": v(7.68, 8.78) * mm, "mid": v(7.6, 9.07) * mm, "end": v(7.67, 9.36) * mm});
            skPoint(sketch, "E165.11.9", {"position": v(8.83, 9.54) * mm});
            skArc(sketch, "E165.11.10", {"start": v(8.52, 9.33) * mm, "mid": v(8.25, 9.76) * mm, "end": v(8, 10.2) * mm, "construction": true});
            skArc(sketch, "E165.11.11", {"start": v(8.83, 9.54) * mm, "mid": v(9.1, 9.15) * mm, "end": v(9.4, 8.77) * mm});
            skPoint(sketch, "E165.11.12", {"position": v(8.52, 9.33) * mm});
            skArc(sketch, "E165.11.13", {"start": v(8.71, 8.59) * mm, "mid": v(8.8, 8.47) * mm, "end": v(8.9, 8.35) * mm});
            skArc(sketch, "E165.11.14", {"start": v(7.87, 9.61) * mm, "mid": v(7.92, 9.7) * mm, "end": v(7.9, 9.8) * mm});
            skArc(sketch, "E165.11.15", {"start": v(8.53, 8.63) * mm, "mid": v(8.63, 8.64) * mm, "end": v(8.71, 8.59) * mm});
            skArc(sketch, "E165.12.0", {"start": v(9.65, 6.95) * mm, "mid": v(9.8, 7) * mm, "end": v(9.93, 7.1) * mm});
            skArc(sketch, "E165.12.1", {"start": v(9.08, 7.08) * mm, "mid": v(9.35, 6.93) * mm, "end": v(9.65, 6.95) * mm});
            skArc(sketch, "E165.12.2", {"start": v(10.05, 8.05) * mm, "mid": v(9.72, 8.4) * mm, "end": v(9.4, 8.77) * mm});
            skPoint(sketch, "E165.12.3", {"position": v(9.6, 7.6) * mm});
            skArc(sketch, "E165.12.4", {"start": v(8.95, 7.65) * mm, "mid": v(9, 7.8) * mm, "end": v(9.1, 7.93) * mm});
            skLineSegment(sketch, "E165.12.5", {"start": v(10.77, 7.4) * mm, "end": v(10.35, 6.9) * mm});
            skArc(sketch, "E165.12.6", {"start": v(9.1, 8.12) * mm, "mid": v(9, 8.24) * mm, "end": v(8.9, 8.35) * mm});
            skLineSegment(sketch, "E165.12.7", {"start": v(9.4, 8.77) * mm, "end": v(8.9, 8.35) * mm});
            skArc(sketch, "E165.12.8", {"start": v(9.08, 7.08) * mm, "mid": v(8.93, 7.35) * mm, "end": v(8.95, 7.65) * mm});
            skPoint(sketch, "E165.12.9", {"position": v(10.05, 8.05) * mm});
            skArc(sketch, "E165.12.10", {"start": v(9.79, 7.79) * mm, "mid": v(9.44, 8.15) * mm, "end": v(9.12, 8.53) * mm, "construction": true});
            skArc(sketch, "E165.12.11", {"start": v(10.05, 8.05) * mm, "mid": v(10.4, 7.72) * mm, "end": v(10.77, 7.4) * mm});
            skPoint(sketch, "E165.12.12", {"position": v(9.79, 7.79) * mm});
            skArc(sketch, "E165.12.13", {"start": v(10.12, 7.1) * mm, "mid": v(10.24, 7) * mm, "end": v(10.35, 6.9) * mm});
            skArc(sketch, "E165.12.14", {"start": v(9.1, 7.93) * mm, "mid": v(9.13, 8.03) * mm, "end": v(9.1, 8.12) * mm});
            skArc(sketch, "E165.12.15", {"start": v(9.93, 7.1) * mm, "mid": v(10.03, 7.13) * mm, "end": v(10.12, 7.1) * mm});
            skArc(sketch, "E165.13.0", {"start": v(11.36, 5.67) * mm, "mid": v(11.5, 5.76) * mm, "end": v(11.61, 5.87) * mm});
            skArc(sketch, "E165.13.1", {"start": v(10.78, 5.68) * mm, "mid": v(11.07, 5.6) * mm, "end": v(11.36, 5.67) * mm});
            skArc(sketch, "E165.13.2", {"start": v(11.54, 6.83) * mm, "mid": v(11.15, 7.1) * mm, "end": v(10.77, 7.4) * mm});
            skPoint(sketch, "E165.13.3", {"position": v(11.2, 6.3) * mm});
            skArc(sketch, "E165.13.4", {"start": v(10.53, 6.22) * mm, "mid": v(10.57, 6.38) * mm, "end": v(10.63, 6.53) * mm});
            skLineSegment(sketch, "E165.13.5", {"start": v(12.37, 6.34) * mm, "end": v(12.06, 5.76) * mm});
            skArc(sketch, "E165.13.6", {"start": v(10.59, 6.71) * mm, "mid": v(10.47, 6.8) * mm, "end": v(10.35, 6.9) * mm});
            skLineSegment(sketch, "E165.13.7", {"start": v(10.77, 7.4) * mm, "end": v(10.35, 6.9) * mm});
            skArc(sketch, "E165.13.8", {"start": v(10.78, 5.68) * mm, "mid": v(10.58, 5.92) * mm, "end": v(10.53, 6.22) * mm});
            skPoint(sketch, "E165.13.9", {"position": v(11.54, 6.83) * mm});
            skArc(sketch, "E165.13.10", {"start": v(11.33, 6.52) * mm, "mid": v(10.92, 6.8) * mm, "end": v(10.53, 7.12) * mm, "construction": true});
            skArc(sketch, "E165.13.11", {"start": v(11.54, 6.83) * mm, "mid": v(11.95, 6.57) * mm, "end": v(12.37, 6.34) * mm});
            skPoint(sketch, "E165.13.12", {"position": v(11.33, 6.52) * mm});
            skArc(sketch, "E165.13.13", {"start": v(11.8, 5.9) * mm, "mid": v(11.93, 5.83) * mm, "end": v(12.06, 5.76) * mm});
            skArc(sketch, "E165.13.14", {"start": v(10.63, 6.53) * mm, "mid": v(10.64, 6.63) * mm, "end": v(10.59, 6.71) * mm});
            skArc(sketch, "E165.13.15", {"start": v(11.61, 5.87) * mm, "mid": v(11.7, 5.92) * mm, "end": v(11.8, 5.9) * mm});
            skArc(sketch, "E165.14.0", {"start": v(13.3, 4.75) * mm, "mid": v(13.4, 4.86) * mm, "end": v(13.5, 5) * mm});
            skArc(sketch, "E165.14.1", {"start": v(12.71, 4.65) * mm, "mid": v(13.02, 4.61) * mm, "end": v(13.3, 4.75) * mm});
            skArc(sketch, "E165.14.2", {"start": v(13.24, 5.92) * mm, "mid": v(12.8, 6.12) * mm, "end": v(12.37, 6.34) * mm});
            skPoint(sketch, "E165.14.3", {"position": v(13, 5.34) * mm});
            skArc(sketch, "E165.14.4", {"start": v(12.37, 5.13) * mm, "mid": v(12.37, 5.29) * mm, "end": v(12.4, 5.45) * mm});
            skLineSegment(sketch, "E165.14.5", {"start": v(14.15, 5.6) * mm, "end": v(13.96, 4.97) * mm});
            skArc(sketch, "E165.14.6", {"start": v(12.33, 5.62) * mm, "mid": v(12.2, 5.69) * mm, "end": v(12.06, 5.76) * mm});
            skLineSegment(sketch, "E165.14.7", {"start": v(12.37, 6.34) * mm, "end": v(12.06, 5.76) * mm});
            skArc(sketch, "E165.14.8", {"start": v(12.71, 4.65) * mm, "mid": v(12.47, 4.84) * mm, "end": v(12.37, 5.13) * mm});
            skPoint(sketch, "E165.14.9", {"position": v(13.24, 5.92) * mm});
            skArc(sketch, "E165.14.10", {"start": v(13.1, 5.58) * mm, "mid": v(12.64, 5.78) * mm, "end": v(12.2, 6) * mm, "construction": true});
            skArc(sketch, "E165.14.11", {"start": v(13.24, 5.92) * mm, "mid": v(13.7, 5.75) * mm, "end": v(14.15, 5.6) * mm});
            skPoint(sketch, "E165.14.12", {"position": v(13.1, 5.58) * mm});
            skArc(sketch, "E165.14.13", {"start": v(13.67, 5.06) * mm, "mid": v(13.82, 5.02) * mm, "end": v(13.96, 4.97) * mm});
            skArc(sketch, "E165.14.14", {"start": v(12.4, 5.45) * mm, "mid": v(12.4, 5.55) * mm, "end": v(12.33, 5.62) * mm});
            skArc(sketch, "E165.14.15", {"start": v(13.5, 5) * mm, "mid": v(13.57, 5.06) * mm, "end": v(13.67, 5.06) * mm});
            skArc(sketch, "E165.15.0", {"start": v(15.36, 4.22) * mm, "mid": v(15.45, 4.36) * mm, "end": v(15.52, 4.5) * mm});
            skArc(sketch, "E165.15.1", {"start": v(14.81, 4.01) * mm, "mid": v(15.12, 4.04) * mm, "end": v(15.36, 4.22) * mm});
            skArc(sketch, "E165.15.2", {"start": v(15.08, 5.36) * mm, "mid": v(14.61, 5.47) * mm, "end": v(14.15, 5.6) * mm});
            skPoint(sketch, "E165.15.3", {"position": v(14.96, 4.75) * mm});
            skArc(sketch, "E165.15.4", {"start": v(14.39, 4.41) * mm, "mid": v(14.36, 4.57) * mm, "end": v(14.36, 4.73) * mm});
            skLineSegment(sketch, "E165.15.5", {"start": v(16.04, 5.22) * mm, "end": v(15.97, 4.57) * mm});
            skArc(sketch, "E165.15.6", {"start": v(14.24, 4.89) * mm, "mid": v(14.1, 4.93) * mm, "end": v(13.96, 4.97) * mm});
            skLineSegment(sketch, "E165.15.7", {"start": v(14.15, 5.6) * mm, "end": v(13.96, 4.97) * mm});
            skArc(sketch, "E165.15.8", {"start": v(14.81, 4.01) * mm, "mid": v(14.54, 4.15) * mm, "end": v(14.39, 4.41) * mm});
            skPoint(sketch, "E165.15.9", {"position": v(15.08, 5.36) * mm});
            skArc(sketch, "E165.15.10", {"start": v(15.01, 5) * mm, "mid": v(14.52, 5.1) * mm, "end": v(14.04, 5.24) * mm, "construction": true});
            skArc(sketch, "E165.15.11", {"start": v(15.08, 5.36) * mm, "mid": v(15.56, 5.28) * mm, "end": v(16.04, 5.22) * mm});
            skPoint(sketch, "E165.15.12", {"position": v(15.01, 5) * mm});
            skArc(sketch, "E165.15.13", {"start": v(15.68, 4.6) * mm, "mid": v(15.82, 4.59) * mm, "end": v(15.97, 4.57) * mm});
            skArc(sketch, "E165.15.14", {"start": v(14.36, 4.73) * mm, "mid": v(14.33, 4.83) * mm, "end": v(14.24, 4.89) * mm});
            skArc(sketch, "E165.15.15", {"start": v(15.52, 4.5) * mm, "mid": v(15.58, 4.58) * mm, "end": v(15.68, 4.6) * mm});
            skArc(sketch, "E165.16.0", {"start": v(17.5, 4.1) * mm, "mid": v(17.56, 4.26) * mm, "end": v(17.6, 4.42) * mm});
            skArc(sketch, "E165.16.1", {"start": v(17, 3.8) * mm, "mid": v(17.3, 3.88) * mm, "end": v(17.5, 4.1) * mm});
            skArc(sketch, "E165.16.2", {"start": v(17, 5.18) * mm, "mid": v(16.52, 5.19) * mm, "end": v(16.04, 5.22) * mm});
            skPoint(sketch, "E165.16.3", {"position": v(17, 4.55) * mm});
            skArc(sketch, "E165.16.4", {"start": v(16.5, 4.1) * mm, "mid": v(16.44, 4.26) * mm, "end": v(16.4, 4.42) * mm});
            skLineSegment(sketch, "E165.16.5", {"start": v(17.96, 5.22) * mm, "end": v(18.03, 4.57) * mm});
            skArc(sketch, "E165.16.6", {"start": v(16.27, 4.55) * mm, "mid": v(16.12, 4.56) * mm, "end": v(15.97, 4.57) * mm});
            skLineSegment(sketch, "E165.16.7", {"start": v(16.04, 5.22) * mm, "end": v(15.97, 4.57) * mm});
            skArc(sketch, "E165.16.8", {"start": v(17, 3.8) * mm, "mid": v(16.7, 3.88) * mm, "end": v(16.5, 4.1) * mm});
            skPoint(sketch, "E165.16.9", {"position": v(17, 5.18) * mm});
            skArc(sketch, "E165.16.10", {"start": v(17, 4.8) * mm, "mid": v(16.5, 4.81) * mm, "end": v(16, 4.85) * mm, "construction": true});
            skArc(sketch, "E165.16.11", {"start": v(17, 5.18) * mm, "mid": v(17.48, 5.19) * mm, "end": v(17.96, 5.22) * mm});
            skPoint(sketch, "E165.16.12", {"position": v(17, 4.8) * mm});
            skArc(sketch, "E165.16.13", {"start": v(17.73, 4.55) * mm, "mid": v(17.88, 4.56) * mm, "end": v(18.03, 4.57) * mm});
            skArc(sketch, "E165.16.14", {"start": v(16.4, 4.42) * mm, "mid": v(16.36, 4.5) * mm, "end": v(16.27, 4.55) * mm});
            skArc(sketch, "E165.16.15", {"start": v(17.6, 4.42) * mm, "mid": v(17.64, 4.5) * mm, "end": v(17.73, 4.55) * mm});
            skArc(sketch, "E165.17.0", {"start": v(19.61, 4.41) * mm, "mid": v(19.64, 4.57) * mm, "end": v(19.64, 4.73) * mm});
            skArc(sketch, "E165.17.1", {"start": v(19.19, 4.01) * mm, "mid": v(19.46, 4.15) * mm, "end": v(19.61, 4.41) * mm});
            skArc(sketch, "E165.17.2", {"start": v(18.92, 5.36) * mm, "mid": v(18.44, 5.28) * mm, "end": v(17.96, 5.22) * mm});
            skPoint(sketch, "E165.17.3", {"position": v(19.04, 4.75) * mm});
            skArc(sketch, "E165.17.4", {"start": v(18.64, 4.22) * mm, "mid": v(18.55, 4.36) * mm, "end": v(18.48, 4.5) * mm});
            skLineSegment(sketch, "E165.17.5", {"start": v(19.85, 5.6) * mm, "end": v(20.04, 4.97) * mm});
            skArc(sketch, "E165.17.6", {"start": v(18.32, 4.6) * mm, "mid": v(18.18, 4.59) * mm, "end": v(18.03, 4.57) * mm});
            skLineSegment(sketch, "E165.17.7", {"start": v(17.96, 5.22) * mm, "end": v(18.03, 4.57) * mm});
            skArc(sketch, "E165.17.8", {"start": v(19.19, 4.01) * mm, "mid": v(18.88, 4.04) * mm, "end": v(18.64, 4.22) * mm});
            skPoint(sketch, "E165.17.9", {"position": v(18.92, 5.36) * mm});
            skArc(sketch, "E165.17.10", {"start": v(18.99, 5) * mm, "mid": v(18.5, 4.91) * mm, "end": v(18, 4.85) * mm, "construction": true});
            skArc(sketch, "E165.17.11", {"start": v(18.92, 5.36) * mm, "mid": v(19.39, 5.47) * mm, "end": v(19.85, 5.6) * mm});
            skPoint(sketch, "E165.17.12", {"position": v(18.99, 5) * mm});
            skArc(sketch, "E165.17.13", {"start": v(19.76, 4.89) * mm, "mid": v(19.9, 4.93) * mm, "end": v(20.04, 4.97) * mm});
            skArc(sketch, "E165.17.14", {"start": v(18.48, 4.5) * mm, "mid": v(18.42, 4.58) * mm, "end": v(18.32, 4.6) * mm});
            skArc(sketch, "E165.17.15", {"start": v(19.64, 4.73) * mm, "mid": v(19.67, 4.83) * mm, "end": v(19.76, 4.89) * mm});
            skArc(sketch, "E165.18.0", {"start": v(21.63, 5.13) * mm, "mid": v(21.63, 5.29) * mm, "end": v(21.6, 5.45) * mm});
            skArc(sketch, "E165.18.1", {"start": v(21.29, 4.65) * mm, "mid": v(21.53, 4.84) * mm, "end": v(21.63, 5.13) * mm});
            skArc(sketch, "E165.18.2", {"start": v(20.76, 5.92) * mm, "mid": v(20.3, 5.75) * mm, "end": v(19.85, 5.6) * mm});
            skPoint(sketch, "E165.18.3", {"position": v(21, 5.34) * mm});
            skArc(sketch, "E165.18.4", {"start": v(20.7, 4.75) * mm, "mid": v(20.6, 4.86) * mm, "end": v(20.5, 5) * mm});
            skLineSegment(sketch, "E165.18.5", {"start": v(21.63, 6.34) * mm, "end": v(21.94, 5.76) * mm});
            skArc(sketch, "E165.18.6", {"start": v(20.33, 5.06) * mm, "mid": v(20.18, 5.02) * mm, "end": v(20.04, 4.97) * mm});
            skLineSegment(sketch, "E165.18.7", {"start": v(19.85, 5.6) * mm, "end": v(20.04, 4.97) * mm});
            skArc(sketch, "E165.18.8", {"start": v(21.29, 4.65) * mm, "mid": v(20.98, 4.61) * mm, "end": v(20.7, 4.75) * mm});
            skPoint(sketch, "E165.18.9", {"position": v(20.76, 5.92) * mm});
            skArc(sketch, "E165.18.10", {"start": v(20.9, 5.58) * mm, "mid": v(20.44, 5.4) * mm, "end": v(19.96, 5.24) * mm, "construction": true});
            skArc(sketch, "E165.18.11", {"start": v(20.76, 5.92) * mm, "mid": v(21.2, 6.12) * mm, "end": v(21.63, 6.34) * mm});
            skPoint(sketch, "E165.18.12", {"position": v(20.9, 5.58) * mm});
            skArc(sketch, "E165.18.13", {"start": v(21.67, 5.62) * mm, "mid": v(21.8, 5.69) * mm, "end": v(21.94, 5.76) * mm});
            skArc(sketch, "E165.18.14", {"start": v(20.5, 5) * mm, "mid": v(20.43, 5.06) * mm, "end": v(20.33, 5.06) * mm});
            skArc(sketch, "E165.18.15", {"start": v(21.6, 5.45) * mm, "mid": v(21.6, 5.55) * mm, "end": v(21.67, 5.62) * mm});
            skArc(sketch, "E165.19.0", {"start": v(23.47, 6.22) * mm, "mid": v(23.43, 6.38) * mm, "end": v(23.37, 6.53) * mm});
            skArc(sketch, "E165.19.1", {"start": v(23.22, 5.68) * mm, "mid": v(23.42, 5.92) * mm, "end": v(23.47, 6.22) * mm});
            skArc(sketch, "E165.19.2", {"start": v(22.46, 6.83) * mm, "mid": v(22.05, 6.57) * mm, "end": v(21.63, 6.34) * mm});
            skPoint(sketch, "E165.19.3", {"position": v(22.8, 6.3) * mm});
            skArc(sketch, "E165.19.4", {"start": v(22.64, 5.67) * mm, "mid": v(22.5, 5.76) * mm, "end": v(22.39, 5.87) * mm});
            skLineSegment(sketch, "E165.19.5", {"start": v(23.23, 7.4) * mm, "end": v(23.65, 6.9) * mm});
            skArc(sketch, "E165.19.6", {"start": v(22.2, 5.9) * mm, "mid": v(22.07, 5.83) * mm, "end": v(21.94, 5.76) * mm});
            skLineSegment(sketch, "E165.19.7", {"start": v(21.63, 6.34) * mm, "end": v(21.94, 5.76) * mm});
            skArc(sketch, "E165.19.8", {"start": v(23.22, 5.68) * mm, "mid": v(22.93, 5.6) * mm, "end": v(22.64, 5.67) * mm});
            skPoint(sketch, "E165.19.9", {"position": v(22.46, 6.83) * mm});
            skArc(sketch, "E165.19.10", {"start": v(22.67, 6.52) * mm, "mid": v(22.24, 6.25) * mm, "end": v(21.8, 6) * mm, "construction": true});
            skArc(sketch, "E165.19.11", {"start": v(22.46, 6.83) * mm, "mid": v(22.85, 7.1) * mm, "end": v(23.23, 7.4) * mm});
            skPoint(sketch, "E165.19.12", {"position": v(22.67, 6.52) * mm});
            skArc(sketch, "E165.19.13", {"start": v(23.41, 6.71) * mm, "mid": v(23.53, 6.8) * mm, "end": v(23.65, 6.9) * mm});
            skArc(sketch, "E165.19.14", {"start": v(22.39, 5.87) * mm, "mid": v(22.3, 5.92) * mm, "end": v(22.2, 5.9) * mm});
            skArc(sketch, "E165.19.15", {"start": v(23.37, 6.53) * mm, "mid": v(23.36, 6.63) * mm, "end": v(23.41, 6.71) * mm});
            skArc(sketch, "E165.20.0", {"start": v(25.05, 7.65) * mm, "mid": v(25, 7.8) * mm, "end": v(24.9, 7.93) * mm});
            skArc(sketch, "E165.20.1", {"start": v(24.92, 7.08) * mm, "mid": v(25.07, 7.35) * mm, "end": v(25.05, 7.65) * mm});
            skArc(sketch, "E165.20.2", {"start": v(23.95, 8.05) * mm, "mid": v(23.6, 7.72) * mm, "end": v(23.23, 7.4) * mm});
            skPoint(sketch, "E165.20.3", {"position": v(24.4, 7.6) * mm});
            skArc(sketch, "E165.20.4", {"start": v(24.35, 6.95) * mm, "mid": v(24.2, 7) * mm, "end": v(24.07, 7.1) * mm});
            skLineSegment(sketch, "E165.20.5", {"start": v(24.6, 8.77) * mm, "end": v(25.1, 8.35) * mm});
            skArc(sketch, "E165.20.6", {"start": v(23.88, 7.1) * mm, "mid": v(23.76, 7) * mm, "end": v(23.65, 6.9) * mm});
            skLineSegment(sketch, "E165.20.7", {"start": v(23.23, 7.4) * mm, "end": v(23.65, 6.9) * mm});
            skArc(sketch, "E165.20.8", {"start": v(24.92, 7.08) * mm, "mid": v(24.65, 6.93) * mm, "end": v(24.35, 6.95) * mm});
            skPoint(sketch, "E165.20.9", {"position": v(23.95, 8.05) * mm});
            skArc(sketch, "E165.20.10", {"start": v(24.21, 7.79) * mm, "mid": v(23.85, 7.44) * mm, "end": v(23.47, 7.12) * mm, "construction": true});
            skArc(sketch, "E165.20.11", {"start": v(23.95, 8.05) * mm, "mid": v(24.28, 8.4) * mm, "end": v(24.6, 8.77) * mm});
            skPoint(sketch, "E165.20.12", {"position": v(24.21, 7.79) * mm});
            skArc(sketch, "E165.20.13", {"start": v(24.9, 8.12) * mm, "mid": v(25, 8.24) * mm, "end": v(25.1, 8.35) * mm});
            skArc(sketch, "E165.20.14", {"start": v(24.07, 7.1) * mm, "mid": v(23.97, 7.13) * mm, "end": v(23.88, 7.1) * mm});
            skArc(sketch, "E165.20.15", {"start": v(24.9, 7.93) * mm, "mid": v(24.87, 8.03) * mm, "end": v(24.9, 8.12) * mm});
            skArc(sketch, "E165.21.0", {"start": v(26.33, 9.36) * mm, "mid": v(26.24, 9.5) * mm, "end": v(26.13, 9.61) * mm});
            skArc(sketch, "E165.21.1", {"start": v(26.32, 8.78) * mm, "mid": v(26.4, 9.07) * mm, "end": v(26.33, 9.36) * mm});
            skArc(sketch, "E165.21.2", {"start": v(25.17, 9.54) * mm, "mid": v(24.9, 9.15) * mm, "end": v(24.6, 8.77) * mm});
            skPoint(sketch, "E165.21.3", {"position": v(25.7, 9.2) * mm});
            skArc(sketch, "E165.21.4", {"start": v(25.78, 8.53) * mm, "mid": v(25.62, 8.57) * mm, "end": v(25.47, 8.63) * mm});
            skLineSegment(sketch, "E165.21.5", {"start": v(25.66, 10.37) * mm, "end": v(26.24, 10.06) * mm});
            skArc(sketch, "E165.21.6", {"start": v(25.29, 8.59) * mm, "mid": v(25.2, 8.47) * mm, "end": v(25.1, 8.35) * mm});
            skLineSegment(sketch, "E165.21.7", {"start": v(24.6, 8.77) * mm, "end": v(25.1, 8.35) * mm});
            skArc(sketch, "E165.21.8", {"start": v(26.32, 8.78) * mm, "mid": v(26.08, 8.58) * mm, "end": v(25.78, 8.53) * mm});
            skPoint(sketch, "E165.21.9", {"position": v(25.17, 9.54) * mm});
            skArc(sketch, "E165.21.10", {"start": v(25.48, 9.33) * mm, "mid": v(25.2, 8.92) * mm, "end": v(24.88, 8.53) * mm, "construction": true});
            skArc(sketch, "E165.21.11", {"start": v(25.17, 9.54) * mm, "mid": v(25.43, 9.95) * mm, "end": v(25.66, 10.37) * mm});
            skPoint(sketch, "E165.21.12", {"position": v(25.48, 9.33) * mm});
            skArc(sketch, "E165.21.13", {"start": v(26.1, 9.8) * mm, "mid": v(26.17, 9.93) * mm, "end": v(26.24, 10.06) * mm});
            skArc(sketch, "E165.21.14", {"start": v(25.47, 8.63) * mm, "mid": v(25.37, 8.64) * mm, "end": v(25.29, 8.59) * mm});
            skArc(sketch, "E165.21.15", {"start": v(26.13, 9.61) * mm, "mid": v(26.08, 9.7) * mm, "end": v(26.1, 9.8) * mm});
            skArc(sketch, "E165.22.0", {"start": v(27.25, 11.3) * mm, "mid": v(27.14, 11.4) * mm, "end": v(27, 11.5) * mm});
            skArc(sketch, "E165.22.1", {"start": v(27.35, 10.71) * mm, "mid": v(27.39, 11.02) * mm, "end": v(27.25, 11.3) * mm});
            skArc(sketch, "E165.22.2", {"start": v(26.08, 11.24) * mm, "mid": v(25.88, 10.8) * mm, "end": v(25.66, 10.37) * mm});
            skPoint(sketch, "E165.22.3", {"position": v(26.66, 11) * mm});
            skArc(sketch, "E165.22.4", {"start": v(26.87, 10.37) * mm, "mid": v(26.71, 10.37) * mm, "end": v(26.55, 10.4) * mm});
            skLineSegment(sketch, "E165.22.5", {"start": v(26.4, 12.15) * mm, "end": v(27.03, 11.96) * mm});
            skArc(sketch, "E165.22.6", {"start": v(26.38, 10.33) * mm, "mid": v(26.31, 10.2) * mm, "end": v(26.24, 10.06) * mm});
            skLineSegment(sketch, "E165.22.7", {"start": v(25.66, 10.37) * mm, "end": v(26.24, 10.06) * mm});
            skArc(sketch, "E165.22.8", {"start": v(27.35, 10.71) * mm, "mid": v(27.16, 10.47) * mm, "end": v(26.87, 10.37) * mm});
            skPoint(sketch, "E165.22.9", {"position": v(26.08, 11.24) * mm});
            skArc(sketch, "E165.22.10", {"start": v(26.42, 11.1) * mm, "mid": v(26.22, 10.64) * mm, "end": v(26, 10.2) * mm, "construction": true});
            skArc(sketch, "E165.22.11", {"start": v(26.08, 11.24) * mm, "mid": v(26.25, 11.7) * mm, "end": v(26.4, 12.15) * mm});
            skPoint(sketch, "E165.22.12", {"position": v(26.42, 11.1) * mm});
            skArc(sketch, "E165.22.13", {"start": v(26.94, 11.67) * mm, "mid": v(26.98, 11.82) * mm, "end": v(27.03, 11.96) * mm});
            skArc(sketch, "E165.22.14", {"start": v(26.55, 10.4) * mm, "mid": v(26.45, 10.4) * mm, "end": v(26.38, 10.33) * mm});
            skArc(sketch, "E165.22.15", {"start": v(27, 11.5) * mm, "mid": v(26.94, 11.57) * mm, "end": v(26.94, 11.67) * mm});
            skArc(sketch, "E165.23.0", {"start": v(27.78, 13.36) * mm, "mid": v(27.64, 13.45) * mm, "end": v(27.5, 13.52) * mm});
            skArc(sketch, "E165.23.1", {"start": v(27.99, 12.81) * mm, "mid": v(27.96, 13.12) * mm, "end": v(27.78, 13.36) * mm});
            skArc(sketch, "E165.23.2", {"start": v(26.64, 13.08) * mm, "mid": v(26.53, 12.61) * mm, "end": v(26.4, 12.15) * mm});
            skPoint(sketch, "E165.23.3", {"position": v(27.25, 12.96) * mm});
            skArc(sketch, "E165.23.4", {"start": v(27.59, 12.39) * mm, "mid": v(27.43, 12.36) * mm, "end": v(27.27, 12.36) * mm});
            skLineSegment(sketch, "E165.23.5", {"start": v(26.78, 14.04) * mm, "end": v(27.43, 13.97) * mm});
            skArc(sketch, "E165.23.6", {"start": v(27.11, 12.24) * mm, "mid": v(27.07, 12.1) * mm, "end": v(27.03, 11.96) * mm});
            skLineSegment(sketch, "E165.23.7", {"start": v(26.4, 12.15) * mm, "end": v(27.03, 11.96) * mm});
            skArc(sketch, "E165.23.8", {"start": v(27.99, 12.81) * mm, "mid": v(27.85, 12.54) * mm, "end": v(27.59, 12.39) * mm});
            skPoint(sketch, "E165.23.9", {"position": v(26.64, 13.08) * mm});
            skArc(sketch, "E165.23.10", {"start": v(27, 13.01) * mm, "mid": v(26.9, 12.52) * mm, "end": v(26.76, 12.04) * mm, "construction": true});
            skArc(sketch, "E165.23.11", {"start": v(26.64, 13.08) * mm, "mid": v(26.72, 13.56) * mm, "end": v(26.78, 14.04) * mm});
            skPoint(sketch, "E165.23.12", {"position": v(27, 13.01) * mm});
            skArc(sketch, "E165.23.13", {"start": v(27.4, 13.68) * mm, "mid": v(27.41, 13.82) * mm, "end": v(27.43, 13.97) * mm});
            skArc(sketch, "E165.23.14", {"start": v(27.27, 12.36) * mm, "mid": v(27.17, 12.33) * mm, "end": v(27.11, 12.24) * mm});
            skArc(sketch, "E165.23.15", {"start": v(27.5, 13.52) * mm, "mid": v(27.42, 13.58) * mm, "end": v(27.4, 13.68) * mm});
            skArc(sketch, "E165.24.0", {"start": v(27.9, 15.5) * mm, "mid": v(27.74, 15.56) * mm, "end": v(27.58, 15.6) * mm});
            skArc(sketch, "E165.24.1", {"start": v(28.2, 15) * mm, "mid": v(28.12, 15.3) * mm, "end": v(27.9, 15.5) * mm});
            skArc(sketch, "E165.24.2", {"start": v(26.82, 15) * mm, "mid": v(26.81, 14.52) * mm, "end": v(26.78, 14.04) * mm});
            skPoint(sketch, "E165.24.3", {"position": v(27.45, 15) * mm});
            skArc(sketch, "E165.24.4", {"start": v(27.9, 14.5) * mm, "mid": v(27.74, 14.44) * mm, "end": v(27.58, 14.4) * mm});
            skLineSegment(sketch, "E165.24.5", {"start": v(26.78, 15.96) * mm, "end": v(27.43, 16.03) * mm});
            skArc(sketch, "E165.24.6", {"start": v(27.45, 14.27) * mm, "mid": v(27.44, 14.12) * mm, "end": v(27.43, 13.97) * mm});
            skLineSegment(sketch, "E165.24.7", {"start": v(26.78, 14.04) * mm, "end": v(27.43, 13.97) * mm});
            skArc(sketch, "E165.24.8", {"start": v(28.2, 15) * mm, "mid": v(28.12, 14.7) * mm, "end": v(27.9, 14.5) * mm});
            skPoint(sketch, "E165.24.9", {"position": v(26.82, 15) * mm});
            skArc(sketch, "E165.24.10", {"start": v(27.2, 15) * mm, "mid": v(27.19, 14.5) * mm, "end": v(27.15, 14) * mm, "construction": true});
            skArc(sketch, "E165.24.11", {"start": v(26.82, 15) * mm, "mid": v(26.81, 15.48) * mm, "end": v(26.78, 15.96) * mm});
            skPoint(sketch, "E165.24.12", {"position": v(27.2, 15) * mm});
            skArc(sketch, "E165.24.13", {"start": v(27.45, 15.73) * mm, "mid": v(27.44, 15.88) * mm, "end": v(27.43, 16.03) * mm});
            skArc(sketch, "E165.24.14", {"start": v(27.58, 14.4) * mm, "mid": v(27.5, 14.36) * mm, "end": v(27.45, 14.27) * mm});
            skArc(sketch, "E165.24.15", {"start": v(27.58, 15.6) * mm, "mid": v(27.5, 15.64) * mm, "end": v(27.45, 15.73) * mm});
            skArc(sketch, "E165.25.0", {"start": v(27.59, 17.61) * mm, "mid": v(27.43, 17.64) * mm, "end": v(27.27, 17.64) * mm});
            skArc(sketch, "E165.25.1", {"start": v(27.99, 17.19) * mm, "mid": v(27.85, 17.46) * mm, "end": v(27.59, 17.61) * mm});
            skArc(sketch, "E165.25.2", {"start": v(26.64, 16.92) * mm, "mid": v(26.72, 16.44) * mm, "end": v(26.78, 15.96) * mm});
            skPoint(sketch, "E165.25.3", {"position": v(27.25, 17.04) * mm});
            skArc(sketch, "E165.25.4", {"start": v(27.78, 16.64) * mm, "mid": v(27.64, 16.55) * mm, "end": v(27.5, 16.48) * mm});
            skLineSegment(sketch, "E165.25.5", {"start": v(26.4, 17.85) * mm, "end": v(27.03, 18.04) * mm});
            skArc(sketch, "E165.25.6", {"start": v(27.4, 16.32) * mm, "mid": v(27.41, 16.18) * mm, "end": v(27.43, 16.03) * mm});
            skLineSegment(sketch, "E165.25.7", {"start": v(26.78, 15.96) * mm, "end": v(27.43, 16.03) * mm});
            skArc(sketch, "E165.25.8", {"start": v(27.99, 17.19) * mm, "mid": v(27.96, 16.88) * mm, "end": v(27.78, 16.64) * mm});
            skPoint(sketch, "E165.25.9", {"position": v(26.64, 16.92) * mm});
            skArc(sketch, "E165.25.10", {"start": v(27, 16.99) * mm, "mid": v(27.09, 16.5) * mm, "end": v(27.15, 16) * mm, "construction": true});
            skArc(sketch, "E165.25.11", {"start": v(26.64, 16.92) * mm, "mid": v(26.53, 17.39) * mm, "end": v(26.4, 17.85) * mm});
            skPoint(sketch, "E165.25.12", {"position": v(27, 16.99) * mm});
            skArc(sketch, "E165.25.13", {"start": v(27.11, 17.76) * mm, "mid": v(27.07, 17.9) * mm, "end": v(27.03, 18.04) * mm});
            skArc(sketch, "E165.25.14", {"start": v(27.5, 16.48) * mm, "mid": v(27.42, 16.42) * mm, "end": v(27.4, 16.32) * mm});
            skArc(sketch, "E165.25.15", {"start": v(27.27, 17.64) * mm, "mid": v(27.17, 17.67) * mm, "end": v(27.11, 17.76) * mm});
            skArc(sketch, "E165.26.0", {"start": v(26.87, 19.63) * mm, "mid": v(26.71, 19.63) * mm, "end": v(26.55, 19.6) * mm});
            skArc(sketch, "E165.26.1", {"start": v(27.35, 19.29) * mm, "mid": v(27.16, 19.53) * mm, "end": v(26.87, 19.63) * mm});
            skArc(sketch, "E165.26.2", {"start": v(26.08, 18.76) * mm, "mid": v(26.25, 18.3) * mm, "end": v(26.4, 17.85) * mm});
            skPoint(sketch, "E165.26.3", {"position": v(26.66, 19) * mm});
            skArc(sketch, "E165.26.4", {"start": v(27.25, 18.7) * mm, "mid": v(27.14, 18.6) * mm, "end": v(27, 18.5) * mm});
            skLineSegment(sketch, "E165.26.5", {"start": v(25.66, 19.63) * mm, "end": v(26.24, 19.94) * mm});
            skArc(sketch, "E165.26.6", {"start": v(26.94, 18.33) * mm, "mid": v(26.98, 18.18) * mm, "end": v(27.03, 18.04) * mm});
            skLineSegment(sketch, "E165.26.7", {"start": v(26.4, 17.85) * mm, "end": v(27.03, 18.04) * mm});
            skArc(sketch, "E165.26.8", {"start": v(27.35, 19.29) * mm, "mid": v(27.39, 18.98) * mm, "end": v(27.25, 18.7) * mm});
            skPoint(sketch, "E165.26.9", {"position": v(26.08, 18.76) * mm});
            skArc(sketch, "E165.26.10", {"start": v(26.42, 18.9) * mm, "mid": v(26.6, 18.44) * mm, "end": v(26.76, 17.96) * mm, "construction": true});
            skArc(sketch, "E165.26.11", {"start": v(26.08, 18.76) * mm, "mid": v(25.88, 19.2) * mm, "end": v(25.66, 19.63) * mm});
            skPoint(sketch, "E165.26.12", {"position": v(26.42, 18.9) * mm});
            skArc(sketch, "E165.26.13", {"start": v(26.38, 19.67) * mm, "mid": v(26.31, 19.8) * mm, "end": v(26.24, 19.94) * mm});
            skArc(sketch, "E165.26.14", {"start": v(27, 18.5) * mm, "mid": v(26.94, 18.43) * mm, "end": v(26.94, 18.33) * mm});
            skArc(sketch, "E165.26.15", {"start": v(26.55, 19.6) * mm, "mid": v(26.45, 19.6) * mm, "end": v(26.38, 19.67) * mm});
            skArc(sketch, "E165.27.0", {"start": v(25.78, 21.47) * mm, "mid": v(25.62, 21.43) * mm, "end": v(25.47, 21.37) * mm});
            skArc(sketch, "E165.27.1", {"start": v(26.32, 21.22) * mm, "mid": v(26.08, 21.42) * mm, "end": v(25.78, 21.47) * mm});
            skArc(sketch, "E165.27.2", {"start": v(25.17, 20.46) * mm, "mid": v(25.43, 20.05) * mm, "end": v(25.66, 19.63) * mm});
            skPoint(sketch, "E165.27.3", {"position": v(25.7, 20.8) * mm});
            skArc(sketch, "E165.27.4", {"start": v(26.33, 20.64) * mm, "mid": v(26.24, 20.5) * mm, "end": v(26.13, 20.39) * mm});
            skLineSegment(sketch, "E165.27.5", {"start": v(24.6, 21.23) * mm, "end": v(25.1, 21.65) * mm});
            skArc(sketch, "E165.27.6", {"start": v(26.1, 20.2) * mm, "mid": v(26.17, 20.07) * mm, "end": v(26.24, 19.94) * mm});
            skLineSegment(sketch, "E165.27.7", {"start": v(25.66, 19.63) * mm, "end": v(26.24, 19.94) * mm});
            skArc(sketch, "E165.27.8", {"start": v(26.32, 21.22) * mm, "mid": v(26.4, 20.93) * mm, "end": v(26.33, 20.64) * mm});
            skPoint(sketch, "E165.27.9", {"position": v(25.17, 20.46) * mm});
            skArc(sketch, "E165.27.10", {"start": v(25.48, 20.67) * mm, "mid": v(25.75, 20.24) * mm, "end": v(26, 19.8) * mm, "construction": true});
            skArc(sketch, "E165.27.11", {"start": v(25.17, 20.46) * mm, "mid": v(24.9, 20.85) * mm, "end": v(24.6, 21.23) * mm});
            skPoint(sketch, "E165.27.12", {"position": v(25.48, 20.67) * mm});
            skArc(sketch, "E165.27.13", {"start": v(25.29, 21.41) * mm, "mid": v(25.2, 21.53) * mm, "end": v(25.1, 21.65) * mm});
            skArc(sketch, "E165.27.14", {"start": v(26.13, 20.39) * mm, "mid": v(26.08, 20.3) * mm, "end": v(26.1, 20.2) * mm});
            skArc(sketch, "E165.27.15", {"start": v(25.47, 21.37) * mm, "mid": v(25.37, 21.36) * mm, "end": v(25.29, 21.41) * mm});
            skArc(sketch, "E165.28.0", {"start": v(24.35, 23.05) * mm, "mid": v(24.2, 23) * mm, "end": v(24.07, 22.9) * mm});
            skArc(sketch, "E165.28.1", {"start": v(24.92, 22.92) * mm, "mid": v(24.65, 23.07) * mm, "end": v(24.35, 23.05) * mm});
            skArc(sketch, "E165.28.2", {"start": v(23.95, 21.95) * mm, "mid": v(24.28, 21.6) * mm, "end": v(24.6, 21.23) * mm});
            skPoint(sketch, "E165.28.3", {"position": v(24.4, 22.4) * mm});
            skArc(sketch, "E165.28.4", {"start": v(25.05, 22.35) * mm, "mid": v(25, 22.2) * mm, "end": v(24.9, 22.07) * mm});
            skLineSegment(sketch, "E165.28.5", {"start": v(23.23, 22.6) * mm, "end": v(23.65, 23.1) * mm});
            skArc(sketch, "E165.28.6", {"start": v(24.9, 21.88) * mm, "mid": v(25, 21.76) * mm, "end": v(25.1, 21.65) * mm});
            skLineSegment(sketch, "E165.28.7", {"start": v(24.6, 21.23) * mm, "end": v(25.1, 21.65) * mm});
            skArc(sketch, "E165.28.8", {"start": v(24.92, 22.92) * mm, "mid": v(25.07, 22.65) * mm, "end": v(25.05, 22.35) * mm});
            skPoint(sketch, "E165.28.9", {"position": v(23.95, 21.95) * mm});
            skArc(sketch, "E165.28.10", {"start": v(24.21, 22.21) * mm, "mid": v(24.56, 21.85) * mm, "end": v(24.88, 21.47) * mm, "construction": true});
            skArc(sketch, "E165.28.11", {"start": v(23.95, 21.95) * mm, "mid": v(23.6, 22.28) * mm, "end": v(23.23, 22.6) * mm});
            skPoint(sketch, "E165.28.12", {"position": v(24.21, 22.21) * mm});
            skArc(sketch, "E165.28.13", {"start": v(23.88, 22.9) * mm, "mid": v(23.76, 23) * mm, "end": v(23.65, 23.1) * mm});
            skArc(sketch, "E165.28.14", {"start": v(24.9, 22.07) * mm, "mid": v(24.87, 21.97) * mm, "end": v(24.9, 21.88) * mm});
            skArc(sketch, "E165.28.15", {"start": v(24.07, 22.9) * mm, "mid": v(23.97, 22.87) * mm, "end": v(23.88, 22.9) * mm});
            skArc(sketch, "E165.29.0", {"start": v(22.64, 24.33) * mm, "mid": v(22.5, 24.24) * mm, "end": v(22.39, 24.13) * mm});
            skArc(sketch, "E165.29.1", {"start": v(23.22, 24.32) * mm, "mid": v(22.93, 24.4) * mm, "end": v(22.64, 24.33) * mm});
            skArc(sketch, "E165.29.2", {"start": v(22.46, 23.17) * mm, "mid": v(22.85, 22.9) * mm, "end": v(23.23, 22.6) * mm});
            skPoint(sketch, "E165.29.3", {"position": v(22.8, 23.7) * mm});
            skArc(sketch, "E165.29.4", {"start": v(23.47, 23.78) * mm, "mid": v(23.43, 23.62) * mm, "end": v(23.37, 23.47) * mm});
            skLineSegment(sketch, "E165.29.5", {"start": v(21.63, 23.66) * mm, "end": v(21.94, 24.24) * mm});
            skArc(sketch, "E165.29.6", {"start": v(23.41, 23.29) * mm, "mid": v(23.53, 23.2) * mm, "end": v(23.65, 23.1) * mm});
            skLineSegment(sketch, "E165.29.7", {"start": v(23.23, 22.6) * mm, "end": v(23.65, 23.1) * mm});
            skArc(sketch, "E165.29.8", {"start": v(23.22, 24.32) * mm, "mid": v(23.42, 24.08) * mm, "end": v(23.47, 23.78) * mm});
            skPoint(sketch, "E165.29.9", {"position": v(22.46, 23.17) * mm});
            skArc(sketch, "E165.29.10", {"start": v(22.67, 23.48) * mm, "mid": v(23.08, 23.2) * mm, "end": v(23.47, 22.88) * mm, "construction": true});
            skArc(sketch, "E165.29.11", {"start": v(22.46, 23.17) * mm, "mid": v(22.05, 23.43) * mm, "end": v(21.63, 23.66) * mm});
            skPoint(sketch, "E165.29.12", {"position": v(22.67, 23.48) * mm});
            skArc(sketch, "E165.29.13", {"start": v(22.2, 24.1) * mm, "mid": v(22.07, 24.17) * mm, "end": v(21.94, 24.24) * mm});
            skArc(sketch, "E165.29.14", {"start": v(23.37, 23.47) * mm, "mid": v(23.36, 23.37) * mm, "end": v(23.41, 23.29) * mm});
            skArc(sketch, "E165.29.15", {"start": v(22.39, 24.13) * mm, "mid": v(22.3, 24.08) * mm, "end": v(22.2, 24.1) * mm});
            skArc(sketch, "E165.30.0", {"start": v(20.7, 25.25) * mm, "mid": v(20.6, 25.14) * mm, "end": v(20.5, 25) * mm});
            skArc(sketch, "E165.30.1", {"start": v(21.29, 25.35) * mm, "mid": v(20.98, 25.39) * mm, "end": v(20.7, 25.25) * mm});
            skArc(sketch, "E165.30.2", {"start": v(20.76, 24.08) * mm, "mid": v(21.2, 23.88) * mm, "end": v(21.63, 23.66) * mm});
            skPoint(sketch, "E165.30.3", {"position": v(21, 24.66) * mm});
            skArc(sketch, "E165.30.4", {"start": v(21.63, 24.87) * mm, "mid": v(21.63, 24.71) * mm, "end": v(21.6, 24.55) * mm});
            skLineSegment(sketch, "E165.30.5", {"start": v(19.85, 24.4) * mm, "end": v(20.04, 25.03) * mm});
            skArc(sketch, "E165.30.6", {"start": v(21.67, 24.38) * mm, "mid": v(21.8, 24.31) * mm, "end": v(21.94, 24.24) * mm});
            skLineSegment(sketch, "E165.30.7", {"start": v(21.63, 23.66) * mm, "end": v(21.94, 24.24) * mm});
            skArc(sketch, "E165.30.8", {"start": v(21.29, 25.35) * mm, "mid": v(21.53, 25.16) * mm, "end": v(21.63, 24.87) * mm});
            skPoint(sketch, "E165.30.9", {"position": v(20.76, 24.08) * mm});
            skArc(sketch, "E165.30.10", {"start": v(20.9, 24.42) * mm, "mid": v(21.36, 24.22) * mm, "end": v(21.8, 24) * mm, "construction": true});
            skArc(sketch, "E165.30.11", {"start": v(20.76, 24.08) * mm, "mid": v(20.3, 24.25) * mm, "end": v(19.85, 24.4) * mm});
            skPoint(sketch, "E165.30.12", {"position": v(20.9, 24.42) * mm});
            skArc(sketch, "E165.30.13", {"start": v(20.33, 24.94) * mm, "mid": v(20.18, 24.98) * mm, "end": v(20.04, 25.03) * mm});
            skArc(sketch, "E165.30.14", {"start": v(21.6, 24.55) * mm, "mid": v(21.6, 24.45) * mm, "end": v(21.67, 24.38) * mm});
            skArc(sketch, "E165.30.15", {"start": v(20.5, 25) * mm, "mid": v(20.43, 24.94) * mm, "end": v(20.33, 24.94) * mm});
            skArc(sketch, "E165.31.0", {"start": v(18.64, 25.78) * mm, "mid": v(18.55, 25.64) * mm, "end": v(18.48, 25.5) * mm});
            skArc(sketch, "E165.31.1", {"start": v(19.19, 25.99) * mm, "mid": v(18.88, 25.96) * mm, "end": v(18.64, 25.78) * mm});
            skArc(sketch, "E165.31.2", {"start": v(18.92, 24.64) * mm, "mid": v(19.39, 24.53) * mm, "end": v(19.85, 24.4) * mm});
            skPoint(sketch, "E165.31.3", {"position": v(19.04, 25.25) * mm});
            skArc(sketch, "E165.31.4", {"start": v(19.61, 25.59) * mm, "mid": v(19.64, 25.43) * mm, "end": v(19.64, 25.27) * mm});
            skArc(sketch, "E165.31.6", {"start": v(19.76, 25.11) * mm, "mid": v(19.9, 25.07) * mm, "end": v(20.04, 25.03) * mm});
            skLineSegment(sketch, "E165.31.7", {"start": v(19.85, 24.4) * mm, "end": v(20.04, 25.03) * mm});
            skArc(sketch, "E165.31.8", {"start": v(19.19, 25.99) * mm, "mid": v(19.46, 25.85) * mm, "end": v(19.61, 25.59) * mm});
            skPoint(sketch, "E165.31.9", {"position": v(18.92, 24.64) * mm});
            skArc(sketch, "E165.31.10", {"start": v(18.99, 25) * mm, "mid": v(19.48, 24.9) * mm, "end": v(19.96, 24.76) * mm, "construction": true});
            skArc(sketch, "E165.31.11", {"start": v(18.92, 24.64) * mm, "mid": v(18.44, 24.72) * mm, "end": v(17.96, 24.78) * mm});
            skPoint(sketch, "E165.31.12", {"position": v(18.99, 25) * mm});
            skArc(sketch, "E165.31.13", {"start": v(18.32, 25.4) * mm, "mid": v(18.18, 25.41) * mm, "end": v(18.03, 25.43) * mm});
            skArc(sketch, "E165.31.14", {"start": v(19.64, 25.27) * mm, "mid": v(19.67, 25.17) * mm, "end": v(19.76, 25.11) * mm});
            skArc(sketch, "E165.31.15", {"start": v(18.48, 25.5) * mm, "mid": v(18.42, 25.42) * mm, "end": v(18.32, 25.4) * mm});
            skLineSegment(sketch, "E166.0", {"start": v(6.75, 15) * mm, "end": v(27.25, 15) * mm, "construction": true});
            skSolve(sketch);
        }
        {
            var Q0;
            Q0 = qSketchRegion(id + "F25", true);
            extrude(context, id + "F26", {"entities" : qUnion([Q0]), "operationType" : NewBodyOperationType.REMOVE, "endBound" : BoundingType.SYMMETRIC, "oppositeDirection" : true, "depth" : 6.5 * mm});
        }
        {
            var Q0;
            Q0=makeQuery(id+"F2.boolean.opBoolean","MERGE",FACE,{"derivedFrom":[makeQuery(id+"F1.opExtrude","SWEPT_FACE",FACE,{"disambiguationData":[OSD([sQuery(id+"F0.wireOp",EDGE,"E4"),sQuery(id+"F0.wireOp",EDGE,"E22")])]}),makeQuery(id+"F2.opExtrude","SWEPT_FACE",FACE,{"disambiguationData":[OSD([sQuery(id+"F0.wireOp",EDGE,"E35")])]})]});
            var Q1;
            Q1=sQuery(id+"F0.wireOp",VERTEX,"E16");
            cPlane(context, id + "F27", {"entities" : qUnion([Q0, Q1]), "cplaneType" : CPlaneType.PLANE_POINT, "offset" : 150 * mm, "width" : 150 * mm, "height" : 150 * mm});
        }
        {
            var Q0;
            Q0=qCreatedBy(id+"F27.planeOp",FACE);
            var sketch = newSketch(context, id + "F28", { "sketchPlane" : qUnion([Q0])});
            skLineSegment(sketch, "E167", {"start": v(-17, 12.16) * mm, "end": v(-17, 9.53) * mm, "construction": true});
            skArc(sketch, "E168", {"start": v(-17, 26.2) * mm, "mid": v(-16.7, 26.12) * mm, "end": v(-16.5, 25.9) * mm});
            skArc(sketch, "E169", {"start": v(-16.5, 25.9) * mm, "mid": v(-16.44, 25.74) * mm, "end": v(-16.4, 25.58) * mm});
            skArc(sketch, "E170", {"start": v(-16.4, 25.58) * mm, "mid": v(-16.36, 25.5) * mm, "end": v(-16.27, 25.45) * mm});
            skPoint(sketch, "E171", {"position": v(-17, 24.82) * mm});
            skPoint(sketch, "E172", {"position": v(-17, 25.45) * mm});
            skPoint(sketch, "E173", {"position": v(-17, 25.2) * mm});
            skArc(sketch, "E174", {"start": v(-17, 25.2) * mm, "mid": v(-16.5, 25.19) * mm, "end": v(-16, 25.15) * mm, "construction": true});
            skLineSegment(sketch, "E175", {"start": v(-16.04, 24.78) * mm, "end": v(-15.97, 25.43) * mm});
            skArc(sketch, "E176", {"start": v(-16.27, 25.45) * mm, "mid": v(-16.12, 25.44) * mm, "end": v(-15.97, 25.43) * mm});
            skArc(sketch, "E177", {"start": v(-17, 24.82) * mm, "mid": v(-16.52, 24.81) * mm, "end": v(-16.04, 24.78) * mm});
            skArc(sketch, "E178.MirrorCS", {"start": v(-17, 26.2) * mm, "mid": v(-17.3, 26.12) * mm, "end": v(-17.5, 25.9) * mm});
            skArc(sketch, "E179.MirrorCS", {"start": v(-17.5, 25.9) * mm, "mid": v(-17.56, 25.74) * mm, "end": v(-17.6, 25.58) * mm});
            skArc(sketch, "E180.MirrorCS", {"start": v(-17.6, 25.58) * mm, "mid": v(-17.64, 25.5) * mm, "end": v(-17.73, 25.45) * mm});
            skArc(sketch, "E181.MirrorCS", {"start": v(-17.73, 25.45) * mm, "mid": v(-17.88, 25.44) * mm, "end": v(-18.03, 25.43) * mm});
            skLineSegment(sketch, "E182.MirrorCS", {"start": v(-17.96, 24.78) * mm, "end": v(-18.03, 25.43) * mm});
            skArc(sketch, "E183.MirrorCS", {"start": v(-17, 24.82) * mm, "mid": v(-17.48, 24.81) * mm, "end": v(-17.96, 24.78) * mm});
            skArc(sketch, "E184.1.0", {"start": v(-19.61, 25.59) * mm, "mid": v(-19.64, 25.43) * mm, "end": v(-19.64, 25.27) * mm});
            skArc(sketch, "E184.1.1", {"start": v(-19.19, 25.99) * mm, "mid": v(-19.46, 25.85) * mm, "end": v(-19.61, 25.59) * mm});
            skArc(sketch, "E184.1.2", {"start": v(-18.92, 24.64) * mm, "mid": v(-18.44, 24.72) * mm, "end": v(-17.96, 24.78) * mm});
            skPoint(sketch, "E184.1.3", {"position": v(-19.04, 25.25) * mm});
            skArc(sketch, "E184.1.4", {"start": v(-18.64, 25.78) * mm, "mid": v(-18.55, 25.64) * mm, "end": v(-18.48, 25.5) * mm});
            skLineSegment(sketch, "E184.1.5", {"start": v(-19.85, 24.4) * mm, "end": v(-20.04, 25.03) * mm});
            skArc(sketch, "E184.1.6", {"start": v(-18.32, 25.4) * mm, "mid": v(-18.18, 25.41) * mm, "end": v(-18.03, 25.43) * mm});
            skArc(sketch, "E184.1.8", {"start": v(-19.19, 25.99) * mm, "mid": v(-18.88, 25.96) * mm, "end": v(-18.64, 25.78) * mm});
            skPoint(sketch, "E184.1.9", {"position": v(-18.92, 24.64) * mm});
            skArc(sketch, "E184.1.10", {"start": v(-18.99, 25) * mm, "mid": v(-18.5, 25.09) * mm, "end": v(-18, 25.15) * mm, "construction": true});
            skArc(sketch, "E184.1.11", {"start": v(-18.92, 24.64) * mm, "mid": v(-19.39, 24.53) * mm, "end": v(-19.85, 24.4) * mm});
            skPoint(sketch, "E184.1.12", {"position": v(-18.99, 25) * mm});
            skArc(sketch, "E184.1.13", {"start": v(-19.76, 25.11) * mm, "mid": v(-19.9, 25.07) * mm, "end": v(-20.04, 25.03) * mm});
            skArc(sketch, "E184.1.14", {"start": v(-18.48, 25.5) * mm, "mid": v(-18.42, 25.42) * mm, "end": v(-18.32, 25.4) * mm});
            skArc(sketch, "E184.1.15", {"start": v(-19.64, 25.27) * mm, "mid": v(-19.67, 25.17) * mm, "end": v(-19.76, 25.11) * mm});
            skArc(sketch, "E184.2.0", {"start": v(-21.63, 24.87) * mm, "mid": v(-21.63, 24.71) * mm, "end": v(-21.6, 24.55) * mm});
            skArc(sketch, "E184.2.1", {"start": v(-21.29, 25.35) * mm, "mid": v(-21.53, 25.16) * mm, "end": v(-21.63, 24.87) * mm});
            skArc(sketch, "E184.2.2", {"start": v(-20.76, 24.08) * mm, "mid": v(-20.3, 24.25) * mm, "end": v(-19.85, 24.4) * mm});
            skPoint(sketch, "E184.2.3", {"position": v(-21, 24.66) * mm});
            skArc(sketch, "E184.2.4", {"start": v(-20.7, 25.25) * mm, "mid": v(-20.6, 25.14) * mm, "end": v(-20.5, 25) * mm});
            skLineSegment(sketch, "E184.2.5", {"start": v(-21.63, 23.66) * mm, "end": v(-21.94, 24.24) * mm});
            skArc(sketch, "E184.2.6", {"start": v(-20.33, 24.94) * mm, "mid": v(-20.18, 24.98) * mm, "end": v(-20.04, 25.03) * mm});
            skLineSegment(sketch, "E184.2.7", {"start": v(-19.85, 24.4) * mm, "end": v(-20.04, 25.03) * mm});
            skArc(sketch, "E184.2.8", {"start": v(-21.29, 25.35) * mm, "mid": v(-20.98, 25.39) * mm, "end": v(-20.7, 25.25) * mm});
            skPoint(sketch, "E184.2.9", {"position": v(-20.76, 24.08) * mm});
            skArc(sketch, "E184.2.10", {"start": v(-20.9, 24.42) * mm, "mid": v(-20.44, 24.6) * mm, "end": v(-19.96, 24.76) * mm, "construction": true});
            skArc(sketch, "E184.2.11", {"start": v(-20.76, 24.08) * mm, "mid": v(-21.2, 23.88) * mm, "end": v(-21.63, 23.66) * mm});
            skPoint(sketch, "E184.2.12", {"position": v(-20.9, 24.42) * mm});
            skArc(sketch, "E184.2.13", {"start": v(-21.67, 24.38) * mm, "mid": v(-21.8, 24.31) * mm, "end": v(-21.94, 24.24) * mm});
            skArc(sketch, "E184.2.14", {"start": v(-20.5, 25) * mm, "mid": v(-20.43, 24.94) * mm, "end": v(-20.33, 24.94) * mm});
            skArc(sketch, "E184.2.15", {"start": v(-21.6, 24.55) * mm, "mid": v(-21.6, 24.45) * mm, "end": v(-21.67, 24.38) * mm});
            skArc(sketch, "E184.3.0", {"start": v(-23.47, 23.78) * mm, "mid": v(-23.43, 23.62) * mm, "end": v(-23.37, 23.47) * mm});
            skArc(sketch, "E184.3.1", {"start": v(-23.22, 24.32) * mm, "mid": v(-23.42, 24.08) * mm, "end": v(-23.47, 23.78) * mm});
            skArc(sketch, "E184.3.2", {"start": v(-22.46, 23.17) * mm, "mid": v(-22.05, 23.43) * mm, "end": v(-21.63, 23.66) * mm});
            skPoint(sketch, "E184.3.3", {"position": v(-22.8, 23.7) * mm});
            skArc(sketch, "E184.3.4", {"start": v(-22.64, 24.33) * mm, "mid": v(-22.5, 24.24) * mm, "end": v(-22.39, 24.13) * mm});
            skLineSegment(sketch, "E184.3.5", {"start": v(-23.23, 22.6) * mm, "end": v(-23.65, 23.1) * mm});
            skArc(sketch, "E184.3.6", {"start": v(-22.2, 24.1) * mm, "mid": v(-22.07, 24.17) * mm, "end": v(-21.94, 24.24) * mm});
            skLineSegment(sketch, "E184.3.7", {"start": v(-21.63, 23.66) * mm, "end": v(-21.94, 24.24) * mm});
            skArc(sketch, "E184.3.8", {"start": v(-23.22, 24.32) * mm, "mid": v(-22.93, 24.4) * mm, "end": v(-22.64, 24.33) * mm});
            skPoint(sketch, "E184.3.9", {"position": v(-22.46, 23.17) * mm});
            skArc(sketch, "E184.3.10", {"start": v(-22.67, 23.48) * mm, "mid": v(-22.24, 23.75) * mm, "end": v(-21.8, 24) * mm, "construction": true});
            skArc(sketch, "E184.3.11", {"start": v(-22.46, 23.17) * mm, "mid": v(-22.85, 22.9) * mm, "end": v(-23.23, 22.6) * mm});
            skPoint(sketch, "E184.3.12", {"position": v(-22.67, 23.48) * mm});
            skArc(sketch, "E184.3.13", {"start": v(-23.41, 23.29) * mm, "mid": v(-23.53, 23.2) * mm, "end": v(-23.65, 23.1) * mm});
            skArc(sketch, "E184.3.14", {"start": v(-22.39, 24.13) * mm, "mid": v(-22.3, 24.08) * mm, "end": v(-22.2, 24.1) * mm});
            skArc(sketch, "E184.3.15", {"start": v(-23.37, 23.47) * mm, "mid": v(-23.36, 23.37) * mm, "end": v(-23.41, 23.29) * mm});
            skArc(sketch, "E184.4.0", {"start": v(-25.05, 22.35) * mm, "mid": v(-25, 22.2) * mm, "end": v(-24.9, 22.07) * mm});
            skArc(sketch, "E184.4.1", {"start": v(-24.92, 22.92) * mm, "mid": v(-25.07, 22.65) * mm, "end": v(-25.05, 22.35) * mm});
            skArc(sketch, "E184.4.2", {"start": v(-23.95, 21.95) * mm, "mid": v(-23.6, 22.28) * mm, "end": v(-23.23, 22.6) * mm});
            skPoint(sketch, "E184.4.3", {"position": v(-24.4, 22.4) * mm});
            skArc(sketch, "E184.4.4", {"start": v(-24.35, 23.05) * mm, "mid": v(-24.2, 23) * mm, "end": v(-24.07, 22.9) * mm});
            skLineSegment(sketch, "E184.4.5", {"start": v(-24.6, 21.23) * mm, "end": v(-25.1, 21.65) * mm});
            skArc(sketch, "E184.4.6", {"start": v(-23.88, 22.9) * mm, "mid": v(-23.76, 23) * mm, "end": v(-23.65, 23.1) * mm});
            skLineSegment(sketch, "E184.4.7", {"start": v(-23.23, 22.6) * mm, "end": v(-23.65, 23.1) * mm});
            skArc(sketch, "E184.4.8", {"start": v(-24.92, 22.92) * mm, "mid": v(-24.65, 23.07) * mm, "end": v(-24.35, 23.05) * mm});
            skPoint(sketch, "E184.4.9", {"position": v(-23.95, 21.95) * mm});
            skArc(sketch, "E184.4.10", {"start": v(-24.21, 22.21) * mm, "mid": v(-23.85, 22.56) * mm, "end": v(-23.47, 22.88) * mm, "construction": true});
            skArc(sketch, "E184.4.11", {"start": v(-23.95, 21.95) * mm, "mid": v(-24.28, 21.6) * mm, "end": v(-24.6, 21.23) * mm});
            skPoint(sketch, "E184.4.12", {"position": v(-24.21, 22.21) * mm});
            skArc(sketch, "E184.4.13", {"start": v(-24.9, 21.88) * mm, "mid": v(-25, 21.76) * mm, "end": v(-25.1, 21.65) * mm});
            skArc(sketch, "E184.4.14", {"start": v(-24.07, 22.9) * mm, "mid": v(-23.97, 22.87) * mm, "end": v(-23.88, 22.9) * mm});
            skArc(sketch, "E184.4.15", {"start": v(-24.9, 22.07) * mm, "mid": v(-24.87, 21.97) * mm, "end": v(-24.9, 21.88) * mm});
            skArc(sketch, "E184.5.0", {"start": v(-26.33, 20.64) * mm, "mid": v(-26.24, 20.5) * mm, "end": v(-26.13, 20.39) * mm});
            skArc(sketch, "E184.5.1", {"start": v(-26.32, 21.22) * mm, "mid": v(-26.4, 20.93) * mm, "end": v(-26.33, 20.64) * mm});
            skArc(sketch, "E184.5.2", {"start": v(-25.17, 20.46) * mm, "mid": v(-24.9, 20.85) * mm, "end": v(-24.6, 21.23) * mm});
            skPoint(sketch, "E184.5.3", {"position": v(-25.7, 20.8) * mm});
            skArc(sketch, "E184.5.4", {"start": v(-25.78, 21.47) * mm, "mid": v(-25.62, 21.43) * mm, "end": v(-25.47, 21.37) * mm});
            skLineSegment(sketch, "E184.5.5", {"start": v(-25.66, 19.63) * mm, "end": v(-26.24, 19.94) * mm});
            skArc(sketch, "E184.5.6", {"start": v(-25.29, 21.41) * mm, "mid": v(-25.2, 21.53) * mm, "end": v(-25.1, 21.65) * mm});
            skLineSegment(sketch, "E184.5.7", {"start": v(-24.6, 21.23) * mm, "end": v(-25.1, 21.65) * mm});
            skArc(sketch, "E184.5.8", {"start": v(-26.32, 21.22) * mm, "mid": v(-26.08, 21.42) * mm, "end": v(-25.78, 21.47) * mm});
            skPoint(sketch, "E184.5.9", {"position": v(-25.17, 20.46) * mm});
            skArc(sketch, "E184.5.10", {"start": v(-25.48, 20.67) * mm, "mid": v(-25.2, 21.08) * mm, "end": v(-24.88, 21.47) * mm, "construction": true});
            skArc(sketch, "E184.5.11", {"start": v(-25.17, 20.46) * mm, "mid": v(-25.43, 20.05) * mm, "end": v(-25.66, 19.63) * mm});
            skPoint(sketch, "E184.5.12", {"position": v(-25.48, 20.67) * mm});
            skArc(sketch, "E184.5.13", {"start": v(-26.1, 20.2) * mm, "mid": v(-26.17, 20.07) * mm, "end": v(-26.24, 19.94) * mm});
            skArc(sketch, "E184.5.14", {"start": v(-25.47, 21.37) * mm, "mid": v(-25.37, 21.36) * mm, "end": v(-25.29, 21.41) * mm});
            skArc(sketch, "E184.5.15", {"start": v(-26.13, 20.39) * mm, "mid": v(-26.08, 20.3) * mm, "end": v(-26.1, 20.2) * mm});
            skArc(sketch, "E184.6.0", {"start": v(-27.25, 18.7) * mm, "mid": v(-27.14, 18.6) * mm, "end": v(-27, 18.5) * mm});
            skArc(sketch, "E184.6.1", {"start": v(-27.35, 19.29) * mm, "mid": v(-27.39, 18.98) * mm, "end": v(-27.25, 18.7) * mm});
            skArc(sketch, "E184.6.2", {"start": v(-26.08, 18.76) * mm, "mid": v(-25.88, 19.2) * mm, "end": v(-25.66, 19.63) * mm});
            skPoint(sketch, "E184.6.3", {"position": v(-26.66, 19) * mm});
            skArc(sketch, "E184.6.4", {"start": v(-26.87, 19.63) * mm, "mid": v(-26.71, 19.63) * mm, "end": v(-26.55, 19.6) * mm});
            skLineSegment(sketch, "E184.6.5", {"start": v(-26.4, 17.85) * mm, "end": v(-27.03, 18.04) * mm});
            skArc(sketch, "E184.6.6", {"start": v(-26.38, 19.67) * mm, "mid": v(-26.31, 19.8) * mm, "end": v(-26.24, 19.94) * mm});
            skLineSegment(sketch, "E184.6.7", {"start": v(-25.66, 19.63) * mm, "end": v(-26.24, 19.94) * mm});
            skArc(sketch, "E184.6.8", {"start": v(-27.35, 19.29) * mm, "mid": v(-27.16, 19.53) * mm, "end": v(-26.87, 19.63) * mm});
            skPoint(sketch, "E184.6.9", {"position": v(-26.08, 18.76) * mm});
            skArc(sketch, "E184.6.10", {"start": v(-26.42, 18.9) * mm, "mid": v(-26.22, 19.36) * mm, "end": v(-26, 19.8) * mm, "construction": true});
            skArc(sketch, "E184.6.11", {"start": v(-26.08, 18.76) * mm, "mid": v(-26.25, 18.3) * mm, "end": v(-26.4, 17.85) * mm});
            skPoint(sketch, "E184.6.12", {"position": v(-26.42, 18.9) * mm});
            skArc(sketch, "E184.6.13", {"start": v(-26.94, 18.33) * mm, "mid": v(-26.98, 18.18) * mm, "end": v(-27.03, 18.04) * mm});
            skArc(sketch, "E184.6.14", {"start": v(-26.55, 19.6) * mm, "mid": v(-26.45, 19.6) * mm, "end": v(-26.38, 19.67) * mm});
            skArc(sketch, "E184.6.15", {"start": v(-27, 18.5) * mm, "mid": v(-26.94, 18.43) * mm, "end": v(-26.94, 18.33) * mm});
            skArc(sketch, "E184.7.0", {"start": v(-27.78, 16.64) * mm, "mid": v(-27.64, 16.55) * mm, "end": v(-27.5, 16.48) * mm});
            skArc(sketch, "E184.7.1", {"start": v(-27.99, 17.19) * mm, "mid": v(-27.96, 16.88) * mm, "end": v(-27.78, 16.64) * mm});
            skArc(sketch, "E184.7.2", {"start": v(-26.64, 16.92) * mm, "mid": v(-26.53, 17.39) * mm, "end": v(-26.4, 17.85) * mm});
            skPoint(sketch, "E184.7.3", {"position": v(-27.25, 17.04) * mm});
            skArc(sketch, "E184.7.4", {"start": v(-27.59, 17.61) * mm, "mid": v(-27.43, 17.64) * mm, "end": v(-27.27, 17.64) * mm});
            skLineSegment(sketch, "E184.7.5", {"start": v(-26.78, 15.96) * mm, "end": v(-27.43, 16.03) * mm});
            skArc(sketch, "E184.7.6", {"start": v(-27.11, 17.76) * mm, "mid": v(-27.07, 17.9) * mm, "end": v(-27.03, 18.04) * mm});
            skLineSegment(sketch, "E184.7.7", {"start": v(-26.4, 17.85) * mm, "end": v(-27.03, 18.04) * mm});
            skArc(sketch, "E184.7.8", {"start": v(-27.99, 17.19) * mm, "mid": v(-27.85, 17.46) * mm, "end": v(-27.59, 17.61) * mm});
            skPoint(sketch, "E184.7.9", {"position": v(-26.64, 16.92) * mm});
            skArc(sketch, "E184.7.10", {"start": v(-27, 16.99) * mm, "mid": v(-26.9, 17.48) * mm, "end": v(-26.76, 17.96) * mm, "construction": true});
            skArc(sketch, "E184.7.11", {"start": v(-26.64, 16.92) * mm, "mid": v(-26.72, 16.44) * mm, "end": v(-26.78, 15.96) * mm});
            skPoint(sketch, "E184.7.12", {"position": v(-27, 16.99) * mm});
            skArc(sketch, "E184.7.13", {"start": v(-27.4, 16.32) * mm, "mid": v(-27.41, 16.18) * mm, "end": v(-27.43, 16.03) * mm});
            skArc(sketch, "E184.7.14", {"start": v(-27.27, 17.64) * mm, "mid": v(-27.17, 17.67) * mm, "end": v(-27.11, 17.76) * mm});
            skArc(sketch, "E184.7.15", {"start": v(-27.5, 16.48) * mm, "mid": v(-27.42, 16.42) * mm, "end": v(-27.4, 16.32) * mm});
            skArc(sketch, "E184.8.0", {"start": v(-27.9, 14.5) * mm, "mid": v(-27.74, 14.44) * mm, "end": v(-27.58, 14.4) * mm});
            skArc(sketch, "E184.8.1", {"start": v(-28.2, 15) * mm, "mid": v(-28.12, 14.7) * mm, "end": v(-27.9, 14.5) * mm});
            skArc(sketch, "E184.8.2", {"start": v(-26.82, 15) * mm, "mid": v(-26.81, 15.48) * mm, "end": v(-26.78, 15.96) * mm});
            skPoint(sketch, "E184.8.3", {"position": v(-27.45, 15) * mm});
            skArc(sketch, "E184.8.4", {"start": v(-27.9, 15.5) * mm, "mid": v(-27.74, 15.56) * mm, "end": v(-27.58, 15.6) * mm});
            skLineSegment(sketch, "E184.8.5", {"start": v(-26.78, 14.04) * mm, "end": v(-27.43, 13.97) * mm});
            skArc(sketch, "E184.8.6", {"start": v(-27.45, 15.73) * mm, "mid": v(-27.44, 15.88) * mm, "end": v(-27.43, 16.03) * mm});
            skLineSegment(sketch, "E184.8.7", {"start": v(-26.78, 15.96) * mm, "end": v(-27.43, 16.03) * mm});
            skArc(sketch, "E184.8.8", {"start": v(-28.2, 15) * mm, "mid": v(-28.12, 15.3) * mm, "end": v(-27.9, 15.5) * mm});
            skPoint(sketch, "E184.8.9", {"position": v(-26.82, 15) * mm});
            skArc(sketch, "E184.8.10", {"start": v(-27.2, 15) * mm, "mid": v(-27.19, 15.5) * mm, "end": v(-27.15, 16) * mm, "construction": true});
            skArc(sketch, "E184.8.11", {"start": v(-26.82, 15) * mm, "mid": v(-26.81, 14.52) * mm, "end": v(-26.78, 14.04) * mm});
            skPoint(sketch, "E184.8.12", {"position": v(-27.2, 15) * mm});
            skArc(sketch, "E184.8.13", {"start": v(-27.45, 14.27) * mm, "mid": v(-27.44, 14.12) * mm, "end": v(-27.43, 13.97) * mm});
            skArc(sketch, "E184.8.14", {"start": v(-27.58, 15.6) * mm, "mid": v(-27.5, 15.64) * mm, "end": v(-27.45, 15.73) * mm});
            skArc(sketch, "E184.8.15", {"start": v(-27.58, 14.4) * mm, "mid": v(-27.5, 14.36) * mm, "end": v(-27.45, 14.27) * mm});
            skArc(sketch, "E184.9.0", {"start": v(-27.59, 12.39) * mm, "mid": v(-27.43, 12.36) * mm, "end": v(-27.27, 12.36) * mm});
            skArc(sketch, "E184.9.1", {"start": v(-27.99, 12.81) * mm, "mid": v(-27.85, 12.54) * mm, "end": v(-27.59, 12.39) * mm});
            skArc(sketch, "E184.9.2", {"start": v(-26.64, 13.08) * mm, "mid": v(-26.72, 13.56) * mm, "end": v(-26.78, 14.04) * mm});
            skPoint(sketch, "E184.9.3", {"position": v(-27.25, 12.96) * mm});
            skArc(sketch, "E184.9.4", {"start": v(-27.78, 13.36) * mm, "mid": v(-27.64, 13.45) * mm, "end": v(-27.5, 13.52) * mm});
            skLineSegment(sketch, "E184.9.5", {"start": v(-26.4, 12.15) * mm, "end": v(-27.03, 11.96) * mm});
            skArc(sketch, "E184.9.6", {"start": v(-27.4, 13.68) * mm, "mid": v(-27.41, 13.82) * mm, "end": v(-27.43, 13.97) * mm});
            skLineSegment(sketch, "E184.9.7", {"start": v(-26.78, 14.04) * mm, "end": v(-27.43, 13.97) * mm});
            skArc(sketch, "E184.9.8", {"start": v(-27.99, 12.81) * mm, "mid": v(-27.96, 13.12) * mm, "end": v(-27.78, 13.36) * mm});
            skPoint(sketch, "E184.9.9", {"position": v(-26.64, 13.08) * mm});
            skArc(sketch, "E184.9.10", {"start": v(-27, 13.01) * mm, "mid": v(-27.09, 13.5) * mm, "end": v(-27.15, 14) * mm, "construction": true});
            skArc(sketch, "E184.9.11", {"start": v(-26.64, 13.08) * mm, "mid": v(-26.53, 12.61) * mm, "end": v(-26.4, 12.15) * mm});
            skPoint(sketch, "E184.9.12", {"position": v(-27, 13.01) * mm});
            skArc(sketch, "E184.9.13", {"start": v(-27.11, 12.24) * mm, "mid": v(-27.07, 12.1) * mm, "end": v(-27.03, 11.96) * mm});
            skArc(sketch, "E184.9.14", {"start": v(-27.5, 13.52) * mm, "mid": v(-27.42, 13.58) * mm, "end": v(-27.4, 13.68) * mm});
            skArc(sketch, "E184.9.15", {"start": v(-27.27, 12.36) * mm, "mid": v(-27.17, 12.33) * mm, "end": v(-27.11, 12.24) * mm});
            skArc(sketch, "E184.10.0", {"start": v(-26.87, 10.37) * mm, "mid": v(-26.71, 10.37) * mm, "end": v(-26.55, 10.4) * mm});
            skArc(sketch, "E184.10.1", {"start": v(-27.35, 10.71) * mm, "mid": v(-27.16, 10.47) * mm, "end": v(-26.87, 10.37) * mm});
            skArc(sketch, "E184.10.2", {"start": v(-26.08, 11.24) * mm, "mid": v(-26.25, 11.7) * mm, "end": v(-26.4, 12.15) * mm});
            skPoint(sketch, "E184.10.3", {"position": v(-26.66, 11) * mm});
            skArc(sketch, "E184.10.4", {"start": v(-27.25, 11.3) * mm, "mid": v(-27.14, 11.4) * mm, "end": v(-27, 11.5) * mm});
            skLineSegment(sketch, "E184.10.5", {"start": v(-25.66, 10.37) * mm, "end": v(-26.24, 10.06) * mm});
            skArc(sketch, "E184.10.6", {"start": v(-26.94, 11.67) * mm, "mid": v(-26.98, 11.82) * mm, "end": v(-27.03, 11.96) * mm});
            skLineSegment(sketch, "E184.10.7", {"start": v(-26.4, 12.15) * mm, "end": v(-27.03, 11.96) * mm});
            skArc(sketch, "E184.10.8", {"start": v(-27.35, 10.71) * mm, "mid": v(-27.39, 11.02) * mm, "end": v(-27.25, 11.3) * mm});
            skPoint(sketch, "E184.10.9", {"position": v(-26.08, 11.24) * mm});
            skArc(sketch, "E184.10.10", {"start": v(-26.42, 11.1) * mm, "mid": v(-26.6, 11.56) * mm, "end": v(-26.76, 12.04) * mm, "construction": true});
            skArc(sketch, "E184.10.11", {"start": v(-26.08, 11.24) * mm, "mid": v(-25.88, 10.8) * mm, "end": v(-25.66, 10.37) * mm});
            skPoint(sketch, "E184.10.12", {"position": v(-26.42, 11.1) * mm});
            skArc(sketch, "E184.10.13", {"start": v(-26.38, 10.33) * mm, "mid": v(-26.31, 10.2) * mm, "end": v(-26.24, 10.06) * mm});
            skArc(sketch, "E184.10.14", {"start": v(-27, 11.5) * mm, "mid": v(-26.94, 11.57) * mm, "end": v(-26.94, 11.67) * mm});
            skArc(sketch, "E184.10.15", {"start": v(-26.55, 10.4) * mm, "mid": v(-26.45, 10.4) * mm, "end": v(-26.38, 10.33) * mm});
            skArc(sketch, "E184.11.0", {"start": v(-25.78, 8.53) * mm, "mid": v(-25.62, 8.57) * mm, "end": v(-25.47, 8.63) * mm});
            skArc(sketch, "E184.11.1", {"start": v(-26.32, 8.78) * mm, "mid": v(-26.08, 8.58) * mm, "end": v(-25.78, 8.53) * mm});
            skArc(sketch, "E184.11.2", {"start": v(-25.17, 9.54) * mm, "mid": v(-25.43, 9.95) * mm, "end": v(-25.66, 10.37) * mm});
            skPoint(sketch, "E184.11.3", {"position": v(-25.7, 9.2) * mm});
            skArc(sketch, "E184.11.4", {"start": v(-26.33, 9.36) * mm, "mid": v(-26.24, 9.5) * mm, "end": v(-26.13, 9.61) * mm});
            skLineSegment(sketch, "E184.11.5", {"start": v(-24.6, 8.77) * mm, "end": v(-25.1, 8.35) * mm});
            skArc(sketch, "E184.11.6", {"start": v(-26.1, 9.8) * mm, "mid": v(-26.17, 9.93) * mm, "end": v(-26.24, 10.06) * mm});
            skLineSegment(sketch, "E184.11.7", {"start": v(-25.66, 10.37) * mm, "end": v(-26.24, 10.06) * mm});
            skArc(sketch, "E184.11.8", {"start": v(-26.32, 8.78) * mm, "mid": v(-26.4, 9.07) * mm, "end": v(-26.33, 9.36) * mm});
            skPoint(sketch, "E184.11.9", {"position": v(-25.17, 9.54) * mm});
            skArc(sketch, "E184.11.10", {"start": v(-25.48, 9.33) * mm, "mid": v(-25.75, 9.76) * mm, "end": v(-26, 10.2) * mm, "construction": true});
            skArc(sketch, "E184.11.11", {"start": v(-25.17, 9.54) * mm, "mid": v(-24.9, 9.15) * mm, "end": v(-24.6, 8.77) * mm});
            skPoint(sketch, "E184.11.12", {"position": v(-25.48, 9.33) * mm});
            skArc(sketch, "E184.11.13", {"start": v(-25.29, 8.59) * mm, "mid": v(-25.2, 8.47) * mm, "end": v(-25.1, 8.35) * mm});
            skArc(sketch, "E184.11.14", {"start": v(-26.13, 9.61) * mm, "mid": v(-26.08, 9.7) * mm, "end": v(-26.1, 9.8) * mm});
            skArc(sketch, "E184.11.15", {"start": v(-25.47, 8.63) * mm, "mid": v(-25.37, 8.64) * mm, "end": v(-25.29, 8.59) * mm});
            skArc(sketch, "E184.12.0", {"start": v(-24.35, 6.95) * mm, "mid": v(-24.2, 7) * mm, "end": v(-24.07, 7.1) * mm});
            skArc(sketch, "E184.12.1", {"start": v(-24.92, 7.08) * mm, "mid": v(-24.65, 6.93) * mm, "end": v(-24.35, 6.95) * mm});
            skArc(sketch, "E184.12.2", {"start": v(-23.95, 8.05) * mm, "mid": v(-24.28, 8.4) * mm, "end": v(-24.6, 8.77) * mm});
            skPoint(sketch, "E184.12.3", {"position": v(-24.4, 7.6) * mm});
            skArc(sketch, "E184.12.4", {"start": v(-25.05, 7.65) * mm, "mid": v(-25, 7.8) * mm, "end": v(-24.9, 7.93) * mm});
            skLineSegment(sketch, "E184.12.5", {"start": v(-23.23, 7.4) * mm, "end": v(-23.65, 6.9) * mm});
            skArc(sketch, "E184.12.6", {"start": v(-24.9, 8.12) * mm, "mid": v(-25, 8.24) * mm, "end": v(-25.1, 8.35) * mm});
            skLineSegment(sketch, "E184.12.7", {"start": v(-24.6, 8.77) * mm, "end": v(-25.1, 8.35) * mm});
            skArc(sketch, "E184.12.8", {"start": v(-24.92, 7.08) * mm, "mid": v(-25.07, 7.35) * mm, "end": v(-25.05, 7.65) * mm});
            skPoint(sketch, "E184.12.9", {"position": v(-23.95, 8.05) * mm});
            skArc(sketch, "E184.12.10", {"start": v(-24.21, 7.79) * mm, "mid": v(-24.56, 8.15) * mm, "end": v(-24.88, 8.53) * mm, "construction": true});
            skArc(sketch, "E184.12.11", {"start": v(-23.95, 8.05) * mm, "mid": v(-23.6, 7.72) * mm, "end": v(-23.23, 7.4) * mm});
            skPoint(sketch, "E184.12.12", {"position": v(-24.21, 7.79) * mm});
            skArc(sketch, "E184.12.13", {"start": v(-23.88, 7.1) * mm, "mid": v(-23.76, 7) * mm, "end": v(-23.65, 6.9) * mm});
            skArc(sketch, "E184.12.14", {"start": v(-24.9, 7.93) * mm, "mid": v(-24.87, 8.03) * mm, "end": v(-24.9, 8.12) * mm});
            skArc(sketch, "E184.12.15", {"start": v(-24.07, 7.1) * mm, "mid": v(-23.97, 7.13) * mm, "end": v(-23.88, 7.1) * mm});
            skArc(sketch, "E184.13.0", {"start": v(-22.64, 5.67) * mm, "mid": v(-22.5, 5.76) * mm, "end": v(-22.39, 5.87) * mm});
            skArc(sketch, "E184.13.1", {"start": v(-23.22, 5.68) * mm, "mid": v(-22.93, 5.6) * mm, "end": v(-22.64, 5.67) * mm});
            skArc(sketch, "E184.13.2", {"start": v(-22.46, 6.83) * mm, "mid": v(-22.85, 7.1) * mm, "end": v(-23.23, 7.4) * mm});
            skPoint(sketch, "E184.13.3", {"position": v(-22.8, 6.3) * mm});
            skArc(sketch, "E184.13.4", {"start": v(-23.47, 6.22) * mm, "mid": v(-23.43, 6.38) * mm, "end": v(-23.37, 6.53) * mm});
            skLineSegment(sketch, "E184.13.5", {"start": v(-21.63, 6.34) * mm, "end": v(-21.94, 5.76) * mm});
            skArc(sketch, "E184.13.6", {"start": v(-23.41, 6.71) * mm, "mid": v(-23.53, 6.8) * mm, "end": v(-23.65, 6.9) * mm});
            skLineSegment(sketch, "E184.13.7", {"start": v(-23.23, 7.4) * mm, "end": v(-23.65, 6.9) * mm});
            skArc(sketch, "E184.13.8", {"start": v(-23.22, 5.68) * mm, "mid": v(-23.42, 5.92) * mm, "end": v(-23.47, 6.22) * mm});
            skPoint(sketch, "E184.13.9", {"position": v(-22.46, 6.83) * mm});
            skArc(sketch, "E184.13.10", {"start": v(-22.67, 6.52) * mm, "mid": v(-23.08, 6.8) * mm, "end": v(-23.47, 7.12) * mm, "construction": true});
            skArc(sketch, "E184.13.11", {"start": v(-22.46, 6.83) * mm, "mid": v(-22.05, 6.57) * mm, "end": v(-21.63, 6.34) * mm});
            skPoint(sketch, "E184.13.12", {"position": v(-22.67, 6.52) * mm});
            skArc(sketch, "E184.13.13", {"start": v(-22.2, 5.9) * mm, "mid": v(-22.07, 5.83) * mm, "end": v(-21.94, 5.76) * mm});
            skArc(sketch, "E184.13.14", {"start": v(-23.37, 6.53) * mm, "mid": v(-23.36, 6.63) * mm, "end": v(-23.41, 6.71) * mm});
            skArc(sketch, "E184.13.15", {"start": v(-22.39, 5.87) * mm, "mid": v(-22.3, 5.92) * mm, "end": v(-22.2, 5.9) * mm});
            skArc(sketch, "E184.14.0", {"start": v(-20.7, 4.75) * mm, "mid": v(-20.6, 4.86) * mm, "end": v(-20.5, 5) * mm});
            skArc(sketch, "E184.14.1", {"start": v(-21.29, 4.65) * mm, "mid": v(-20.98, 4.61) * mm, "end": v(-20.7, 4.75) * mm});
            skArc(sketch, "E184.14.2", {"start": v(-20.76, 5.92) * mm, "mid": v(-21.2, 6.12) * mm, "end": v(-21.63, 6.34) * mm});
            skPoint(sketch, "E184.14.3", {"position": v(-21, 5.34) * mm});
            skArc(sketch, "E184.14.4", {"start": v(-21.63, 5.13) * mm, "mid": v(-21.63, 5.29) * mm, "end": v(-21.6, 5.45) * mm});
            skLineSegment(sketch, "E184.14.5", {"start": v(-19.85, 5.6) * mm, "end": v(-20.04, 4.97) * mm});
            skArc(sketch, "E184.14.6", {"start": v(-21.67, 5.62) * mm, "mid": v(-21.8, 5.69) * mm, "end": v(-21.94, 5.76) * mm});
            skLineSegment(sketch, "E184.14.7", {"start": v(-21.63, 6.34) * mm, "end": v(-21.94, 5.76) * mm});
            skArc(sketch, "E184.14.8", {"start": v(-21.29, 4.65) * mm, "mid": v(-21.53, 4.84) * mm, "end": v(-21.63, 5.13) * mm});
            skPoint(sketch, "E184.14.9", {"position": v(-20.76, 5.92) * mm});
            skArc(sketch, "E184.14.10", {"start": v(-20.9, 5.58) * mm, "mid": v(-21.36, 5.78) * mm, "end": v(-21.8, 6) * mm, "construction": true});
            skArc(sketch, "E184.14.11", {"start": v(-20.76, 5.92) * mm, "mid": v(-20.3, 5.75) * mm, "end": v(-19.85, 5.6) * mm});
            skPoint(sketch, "E184.14.12", {"position": v(-20.9, 5.58) * mm});
            skArc(sketch, "E184.14.13", {"start": v(-20.33, 5.06) * mm, "mid": v(-20.18, 5.02) * mm, "end": v(-20.04, 4.97) * mm});
            skArc(sketch, "E184.14.14", {"start": v(-21.6, 5.45) * mm, "mid": v(-21.6, 5.55) * mm, "end": v(-21.67, 5.62) * mm});
            skArc(sketch, "E184.14.15", {"start": v(-20.5, 5) * mm, "mid": v(-20.43, 5.06) * mm, "end": v(-20.33, 5.06) * mm});
            skArc(sketch, "E184.15.0", {"start": v(-18.64, 4.22) * mm, "mid": v(-18.55, 4.36) * mm, "end": v(-18.48, 4.5) * mm});
            skArc(sketch, "E184.15.1", {"start": v(-19.19, 4.01) * mm, "mid": v(-18.88, 4.04) * mm, "end": v(-18.64, 4.22) * mm});
            skArc(sketch, "E184.15.2", {"start": v(-18.92, 5.36) * mm, "mid": v(-19.39, 5.47) * mm, "end": v(-19.85, 5.6) * mm});
            skPoint(sketch, "E184.15.3", {"position": v(-19.04, 4.75) * mm});
            skArc(sketch, "E184.15.4", {"start": v(-19.61, 4.41) * mm, "mid": v(-19.64, 4.57) * mm, "end": v(-19.64, 4.73) * mm});
            skLineSegment(sketch, "E184.15.5", {"start": v(-17.96, 5.22) * mm, "end": v(-18.03, 4.57) * mm});
            skArc(sketch, "E184.15.6", {"start": v(-19.76, 4.89) * mm, "mid": v(-19.9, 4.93) * mm, "end": v(-20.04, 4.97) * mm});
            skLineSegment(sketch, "E184.15.7", {"start": v(-19.85, 5.6) * mm, "end": v(-20.04, 4.97) * mm});
            skArc(sketch, "E184.15.8", {"start": v(-19.19, 4.01) * mm, "mid": v(-19.46, 4.15) * mm, "end": v(-19.61, 4.41) * mm});
            skPoint(sketch, "E184.15.9", {"position": v(-18.92, 5.36) * mm});
            skArc(sketch, "E184.15.10", {"start": v(-18.99, 5) * mm, "mid": v(-19.48, 5.1) * mm, "end": v(-19.96, 5.24) * mm, "construction": true});
            skArc(sketch, "E184.15.11", {"start": v(-18.92, 5.36) * mm, "mid": v(-18.44, 5.28) * mm, "end": v(-17.96, 5.22) * mm});
            skPoint(sketch, "E184.15.12", {"position": v(-18.99, 5) * mm});
            skArc(sketch, "E184.15.13", {"start": v(-18.32, 4.6) * mm, "mid": v(-18.18, 4.59) * mm, "end": v(-18.03, 4.57) * mm});
            skArc(sketch, "E184.15.14", {"start": v(-19.64, 4.73) * mm, "mid": v(-19.67, 4.83) * mm, "end": v(-19.76, 4.89) * mm});
            skArc(sketch, "E184.15.15", {"start": v(-18.48, 4.5) * mm, "mid": v(-18.42, 4.58) * mm, "end": v(-18.32, 4.6) * mm});
            skArc(sketch, "E184.16.0", {"start": v(-16.5, 4.1) * mm, "mid": v(-16.44, 4.26) * mm, "end": v(-16.4, 4.42) * mm});
            skArc(sketch, "E184.16.1", {"start": v(-17, 3.8) * mm, "mid": v(-16.7, 3.88) * mm, "end": v(-16.5, 4.1) * mm});
            skArc(sketch, "E184.16.2", {"start": v(-17, 5.18) * mm, "mid": v(-17.48, 5.19) * mm, "end": v(-17.96, 5.22) * mm});
            skPoint(sketch, "E184.16.3", {"position": v(-17, 4.55) * mm});
            skArc(sketch, "E184.16.4", {"start": v(-17.5, 4.1) * mm, "mid": v(-17.56, 4.26) * mm, "end": v(-17.6, 4.42) * mm});
            skLineSegment(sketch, "E184.16.5", {"start": v(-16.04, 5.22) * mm, "end": v(-15.97, 4.57) * mm});
            skArc(sketch, "E184.16.6", {"start": v(-17.73, 4.55) * mm, "mid": v(-17.88, 4.56) * mm, "end": v(-18.03, 4.57) * mm});
            skLineSegment(sketch, "E184.16.7", {"start": v(-17.96, 5.22) * mm, "end": v(-18.03, 4.57) * mm});
            skArc(sketch, "E184.16.8", {"start": v(-17, 3.8) * mm, "mid": v(-17.3, 3.88) * mm, "end": v(-17.5, 4.1) * mm});
            skPoint(sketch, "E184.16.9", {"position": v(-17, 5.18) * mm});
            skArc(sketch, "E184.16.10", {"start": v(-17, 4.8) * mm, "mid": v(-17.5, 4.81) * mm, "end": v(-18, 4.85) * mm, "construction": true});
            skArc(sketch, "E184.16.11", {"start": v(-17, 5.18) * mm, "mid": v(-16.52, 5.19) * mm, "end": v(-16.04, 5.22) * mm});
            skPoint(sketch, "E184.16.12", {"position": v(-17, 4.8) * mm});
            skArc(sketch, "E184.16.13", {"start": v(-16.27, 4.55) * mm, "mid": v(-16.12, 4.56) * mm, "end": v(-15.97, 4.57) * mm});
            skArc(sketch, "E184.16.14", {"start": v(-17.6, 4.42) * mm, "mid": v(-17.64, 4.5) * mm, "end": v(-17.73, 4.55) * mm});
            skArc(sketch, "E184.16.15", {"start": v(-16.4, 4.42) * mm, "mid": v(-16.36, 4.5) * mm, "end": v(-16.27, 4.55) * mm});
            skArc(sketch, "E184.17.0", {"start": v(-14.39, 4.41) * mm, "mid": v(-14.36, 4.57) * mm, "end": v(-14.36, 4.73) * mm});
            skArc(sketch, "E184.17.1", {"start": v(-14.81, 4.01) * mm, "mid": v(-14.54, 4.15) * mm, "end": v(-14.39, 4.41) * mm});
            skArc(sketch, "E184.17.2", {"start": v(-15.08, 5.36) * mm, "mid": v(-15.56, 5.28) * mm, "end": v(-16.04, 5.22) * mm});
            skPoint(sketch, "E184.17.3", {"position": v(-14.96, 4.75) * mm});
            skArc(sketch, "E184.17.4", {"start": v(-15.36, 4.22) * mm, "mid": v(-15.45, 4.36) * mm, "end": v(-15.52, 4.5) * mm});
            skLineSegment(sketch, "E184.17.5", {"start": v(-14.15, 5.6) * mm, "end": v(-13.96, 4.97) * mm});
            skArc(sketch, "E184.17.6", {"start": v(-15.68, 4.6) * mm, "mid": v(-15.82, 4.59) * mm, "end": v(-15.97, 4.57) * mm});
            skLineSegment(sketch, "E184.17.7", {"start": v(-16.04, 5.22) * mm, "end": v(-15.97, 4.57) * mm});
            skArc(sketch, "E184.17.8", {"start": v(-14.81, 4.01) * mm, "mid": v(-15.12, 4.04) * mm, "end": v(-15.36, 4.22) * mm});
            skPoint(sketch, "E184.17.9", {"position": v(-15.08, 5.36) * mm});
            skArc(sketch, "E184.17.10", {"start": v(-15.01, 5) * mm, "mid": v(-15.5, 4.91) * mm, "end": v(-16, 4.85) * mm, "construction": true});
            skArc(sketch, "E184.17.11", {"start": v(-15.08, 5.36) * mm, "mid": v(-14.61, 5.47) * mm, "end": v(-14.15, 5.6) * mm});
            skPoint(sketch, "E184.17.12", {"position": v(-15.01, 5) * mm});
            skArc(sketch, "E184.17.13", {"start": v(-14.24, 4.89) * mm, "mid": v(-14.1, 4.93) * mm, "end": v(-13.96, 4.97) * mm});
            skArc(sketch, "E184.17.14", {"start": v(-15.52, 4.5) * mm, "mid": v(-15.58, 4.58) * mm, "end": v(-15.68, 4.6) * mm});
            skArc(sketch, "E184.17.15", {"start": v(-14.36, 4.73) * mm, "mid": v(-14.33, 4.83) * mm, "end": v(-14.24, 4.89) * mm});
            skArc(sketch, "E184.18.0", {"start": v(-12.37, 5.13) * mm, "mid": v(-12.37, 5.29) * mm, "end": v(-12.4, 5.45) * mm});
            skArc(sketch, "E184.18.1", {"start": v(-12.71, 4.65) * mm, "mid": v(-12.47, 4.84) * mm, "end": v(-12.37, 5.13) * mm});
            skArc(sketch, "E184.18.2", {"start": v(-13.24, 5.92) * mm, "mid": v(-13.7, 5.75) * mm, "end": v(-14.15, 5.6) * mm});
            skPoint(sketch, "E184.18.3", {"position": v(-13, 5.34) * mm});
            skArc(sketch, "E184.18.4", {"start": v(-13.3, 4.75) * mm, "mid": v(-13.4, 4.86) * mm, "end": v(-13.5, 5) * mm});
            skLineSegment(sketch, "E184.18.5", {"start": v(-12.37, 6.34) * mm, "end": v(-12.06, 5.76) * mm});
            skArc(sketch, "E184.18.6", {"start": v(-13.67, 5.06) * mm, "mid": v(-13.82, 5.02) * mm, "end": v(-13.96, 4.97) * mm});
            skLineSegment(sketch, "E184.18.7", {"start": v(-14.15, 5.6) * mm, "end": v(-13.96, 4.97) * mm});
            skArc(sketch, "E184.18.8", {"start": v(-12.71, 4.65) * mm, "mid": v(-13.02, 4.61) * mm, "end": v(-13.3, 4.75) * mm});
            skPoint(sketch, "E184.18.9", {"position": v(-13.24, 5.92) * mm});
            skArc(sketch, "E184.18.10", {"start": v(-13.1, 5.58) * mm, "mid": v(-13.56, 5.4) * mm, "end": v(-14.04, 5.24) * mm, "construction": true});
            skArc(sketch, "E184.18.11", {"start": v(-13.24, 5.92) * mm, "mid": v(-12.8, 6.12) * mm, "end": v(-12.37, 6.34) * mm});
            skPoint(sketch, "E184.18.12", {"position": v(-13.1, 5.58) * mm});
            skArc(sketch, "E184.18.13", {"start": v(-12.33, 5.62) * mm, "mid": v(-12.2, 5.69) * mm, "end": v(-12.06, 5.76) * mm});
            skArc(sketch, "E184.18.14", {"start": v(-13.5, 5) * mm, "mid": v(-13.57, 5.06) * mm, "end": v(-13.67, 5.06) * mm});
            skArc(sketch, "E184.18.15", {"start": v(-12.4, 5.45) * mm, "mid": v(-12.4, 5.55) * mm, "end": v(-12.33, 5.62) * mm});
            skArc(sketch, "E184.19.0", {"start": v(-10.53, 6.22) * mm, "mid": v(-10.57, 6.38) * mm, "end": v(-10.63, 6.53) * mm});
            skArc(sketch, "E184.19.1", {"start": v(-10.78, 5.68) * mm, "mid": v(-10.58, 5.92) * mm, "end": v(-10.53, 6.22) * mm});
            skArc(sketch, "E184.19.2", {"start": v(-11.54, 6.83) * mm, "mid": v(-11.95, 6.57) * mm, "end": v(-12.37, 6.34) * mm});
            skPoint(sketch, "E184.19.3", {"position": v(-11.2, 6.3) * mm});
            skArc(sketch, "E184.19.4", {"start": v(-11.36, 5.67) * mm, "mid": v(-11.5, 5.76) * mm, "end": v(-11.61, 5.87) * mm});
            skLineSegment(sketch, "E184.19.5", {"start": v(-10.77, 7.4) * mm, "end": v(-10.35, 6.9) * mm});
            skArc(sketch, "E184.19.6", {"start": v(-11.8, 5.9) * mm, "mid": v(-11.93, 5.83) * mm, "end": v(-12.06, 5.76) * mm});
            skLineSegment(sketch, "E184.19.7", {"start": v(-12.37, 6.34) * mm, "end": v(-12.06, 5.76) * mm});
            skArc(sketch, "E184.19.8", {"start": v(-10.78, 5.68) * mm, "mid": v(-11.07, 5.6) * mm, "end": v(-11.36, 5.67) * mm});
            skPoint(sketch, "E184.19.9", {"position": v(-11.54, 6.83) * mm});
            skArc(sketch, "E184.19.10", {"start": v(-11.33, 6.52) * mm, "mid": v(-11.76, 6.25) * mm, "end": v(-12.2, 6) * mm, "construction": true});
            skArc(sketch, "E184.19.11", {"start": v(-11.54, 6.83) * mm, "mid": v(-11.15, 7.1) * mm, "end": v(-10.77, 7.4) * mm});
            skPoint(sketch, "E184.19.12", {"position": v(-11.33, 6.52) * mm});
            skArc(sketch, "E184.19.13", {"start": v(-10.59, 6.71) * mm, "mid": v(-10.47, 6.8) * mm, "end": v(-10.35, 6.9) * mm});
            skArc(sketch, "E184.19.14", {"start": v(-11.61, 5.87) * mm, "mid": v(-11.7, 5.92) * mm, "end": v(-11.8, 5.9) * mm});
            skArc(sketch, "E184.19.15", {"start": v(-10.63, 6.53) * mm, "mid": v(-10.64, 6.63) * mm, "end": v(-10.59, 6.71) * mm});
            skArc(sketch, "E184.20.0", {"start": v(-8.95, 7.65) * mm, "mid": v(-9, 7.8) * mm, "end": v(-9.1, 7.93) * mm});
            skArc(sketch, "E184.20.1", {"start": v(-9.08, 7.08) * mm, "mid": v(-8.93, 7.35) * mm, "end": v(-8.95, 7.65) * mm});
            skArc(sketch, "E184.20.2", {"start": v(-10.05, 8.05) * mm, "mid": v(-10.4, 7.72) * mm, "end": v(-10.77, 7.4) * mm});
            skPoint(sketch, "E184.20.3", {"position": v(-9.6, 7.6) * mm});
            skArc(sketch, "E184.20.4", {"start": v(-9.65, 6.95) * mm, "mid": v(-9.8, 7) * mm, "end": v(-9.93, 7.1) * mm});
            skLineSegment(sketch, "E184.20.5", {"start": v(-9.4, 8.77) * mm, "end": v(-8.9, 8.35) * mm});
            skArc(sketch, "E184.20.6", {"start": v(-10.12, 7.1) * mm, "mid": v(-10.24, 7) * mm, "end": v(-10.35, 6.9) * mm});
            skLineSegment(sketch, "E184.20.7", {"start": v(-10.77, 7.4) * mm, "end": v(-10.35, 6.9) * mm});
            skArc(sketch, "E184.20.8", {"start": v(-9.08, 7.08) * mm, "mid": v(-9.35, 6.93) * mm, "end": v(-9.65, 6.95) * mm});
            skPoint(sketch, "E184.20.9", {"position": v(-10.05, 8.05) * mm});
            skArc(sketch, "E184.20.10", {"start": v(-9.79, 7.79) * mm, "mid": v(-10.15, 7.44) * mm, "end": v(-10.53, 7.12) * mm, "construction": true});
            skArc(sketch, "E184.20.11", {"start": v(-10.05, 8.05) * mm, "mid": v(-9.72, 8.4) * mm, "end": v(-9.4, 8.77) * mm});
            skPoint(sketch, "E184.20.12", {"position": v(-9.79, 7.79) * mm});
            skArc(sketch, "E184.20.13", {"start": v(-9.1, 8.12) * mm, "mid": v(-9, 8.24) * mm, "end": v(-8.9, 8.35) * mm});
            skArc(sketch, "E184.20.14", {"start": v(-9.93, 7.1) * mm, "mid": v(-10.03, 7.13) * mm, "end": v(-10.12, 7.1) * mm});
            skArc(sketch, "E184.20.15", {"start": v(-9.1, 7.93) * mm, "mid": v(-9.13, 8.03) * mm, "end": v(-9.1, 8.12) * mm});
            skArc(sketch, "E184.21.0", {"start": v(-7.67, 9.36) * mm, "mid": v(-7.76, 9.5) * mm, "end": v(-7.87, 9.61) * mm});
            skArc(sketch, "E184.21.1", {"start": v(-7.68, 8.78) * mm, "mid": v(-7.6, 9.07) * mm, "end": v(-7.67, 9.36) * mm});
            skArc(sketch, "E184.21.2", {"start": v(-8.83, 9.54) * mm, "mid": v(-9.1, 9.15) * mm, "end": v(-9.4, 8.77) * mm});
            skPoint(sketch, "E184.21.3", {"position": v(-8.3, 9.2) * mm});
            skArc(sketch, "E184.21.4", {"start": v(-8.22, 8.53) * mm, "mid": v(-8.38, 8.57) * mm, "end": v(-8.53, 8.63) * mm});
            skLineSegment(sketch, "E184.21.5", {"start": v(-8.34, 10.37) * mm, "end": v(-7.76, 10.06) * mm});
            skArc(sketch, "E184.21.6", {"start": v(-8.71, 8.59) * mm, "mid": v(-8.8, 8.47) * mm, "end": v(-8.9, 8.35) * mm});
            skLineSegment(sketch, "E184.21.7", {"start": v(-9.4, 8.77) * mm, "end": v(-8.9, 8.35) * mm});
            skArc(sketch, "E184.21.8", {"start": v(-7.68, 8.78) * mm, "mid": v(-7.92, 8.58) * mm, "end": v(-8.22, 8.53) * mm});
            skPoint(sketch, "E184.21.9", {"position": v(-8.83, 9.54) * mm});
            skArc(sketch, "E184.21.10", {"start": v(-8.52, 9.33) * mm, "mid": v(-8.8, 8.92) * mm, "end": v(-9.12, 8.53) * mm, "construction": true});
            skArc(sketch, "E184.21.11", {"start": v(-8.83, 9.54) * mm, "mid": v(-8.57, 9.95) * mm, "end": v(-8.34, 10.37) * mm});
            skPoint(sketch, "E184.21.12", {"position": v(-8.52, 9.33) * mm});
            skArc(sketch, "E184.21.13", {"start": v(-7.9, 9.8) * mm, "mid": v(-7.83, 9.93) * mm, "end": v(-7.76, 10.06) * mm});
            skArc(sketch, "E184.21.14", {"start": v(-8.53, 8.63) * mm, "mid": v(-8.63, 8.64) * mm, "end": v(-8.71, 8.59) * mm});
            skArc(sketch, "E184.21.15", {"start": v(-7.87, 9.61) * mm, "mid": v(-7.92, 9.7) * mm, "end": v(-7.9, 9.8) * mm});
            skArc(sketch, "E184.22.0", {"start": v(-6.75, 11.3) * mm, "mid": v(-6.86, 11.4) * mm, "end": v(-7, 11.5) * mm});
            skArc(sketch, "E184.22.1", {"start": v(-6.65, 10.71) * mm, "mid": v(-6.61, 11.02) * mm, "end": v(-6.75, 11.3) * mm});
            skArc(sketch, "E184.22.2", {"start": v(-7.92, 11.24) * mm, "mid": v(-8.12, 10.8) * mm, "end": v(-8.34, 10.37) * mm});
            skPoint(sketch, "E184.22.3", {"position": v(-7.34, 11) * mm});
            skArc(sketch, "E184.22.4", {"start": v(-7.13, 10.37) * mm, "mid": v(-7.29, 10.37) * mm, "end": v(-7.45, 10.4) * mm});
            skLineSegment(sketch, "E184.22.5", {"start": v(-7.6, 12.15) * mm, "end": v(-6.97, 11.96) * mm});
            skArc(sketch, "E184.22.6", {"start": v(-7.62, 10.33) * mm, "mid": v(-7.69, 10.2) * mm, "end": v(-7.76, 10.06) * mm});
            skLineSegment(sketch, "E184.22.7", {"start": v(-8.34, 10.37) * mm, "end": v(-7.76, 10.06) * mm});
            skArc(sketch, "E184.22.8", {"start": v(-6.65, 10.71) * mm, "mid": v(-6.84, 10.47) * mm, "end": v(-7.13, 10.37) * mm});
            skPoint(sketch, "E184.22.9", {"position": v(-7.92, 11.24) * mm});
            skArc(sketch, "E184.22.10", {"start": v(-7.58, 11.1) * mm, "mid": v(-7.78, 10.64) * mm, "end": v(-8, 10.2) * mm, "construction": true});
            skArc(sketch, "E184.22.11", {"start": v(-7.92, 11.24) * mm, "mid": v(-7.75, 11.7) * mm, "end": v(-7.6, 12.15) * mm});
            skPoint(sketch, "E184.22.12", {"position": v(-7.58, 11.1) * mm});
            skArc(sketch, "E184.22.13", {"start": v(-7.06, 11.67) * mm, "mid": v(-7.02, 11.82) * mm, "end": v(-6.97, 11.96) * mm});
            skArc(sketch, "E184.22.14", {"start": v(-7.45, 10.4) * mm, "mid": v(-7.55, 10.4) * mm, "end": v(-7.62, 10.33) * mm});
            skArc(sketch, "E184.22.15", {"start": v(-7, 11.5) * mm, "mid": v(-7.06, 11.57) * mm, "end": v(-7.06, 11.67) * mm});
            skArc(sketch, "E184.23.0", {"start": v(-6.22, 13.36) * mm, "mid": v(-6.36, 13.45) * mm, "end": v(-6.5, 13.52) * mm});
            skArc(sketch, "E184.23.1", {"start": v(-6.01, 12.81) * mm, "mid": v(-6.04, 13.12) * mm, "end": v(-6.22, 13.36) * mm});
            skArc(sketch, "E184.23.2", {"start": v(-7.36, 13.08) * mm, "mid": v(-7.47, 12.61) * mm, "end": v(-7.6, 12.15) * mm});
            skPoint(sketch, "E184.23.3", {"position": v(-6.75, 12.96) * mm});
            skArc(sketch, "E184.23.4", {"start": v(-6.41, 12.39) * mm, "mid": v(-6.57, 12.36) * mm, "end": v(-6.73, 12.36) * mm});
            skLineSegment(sketch, "E184.23.5", {"start": v(-7.22, 14.04) * mm, "end": v(-6.57, 13.97) * mm});
            skArc(sketch, "E184.23.6", {"start": v(-6.89, 12.24) * mm, "mid": v(-6.93, 12.1) * mm, "end": v(-6.97, 11.96) * mm});
            skLineSegment(sketch, "E184.23.7", {"start": v(-7.6, 12.15) * mm, "end": v(-6.97, 11.96) * mm});
            skArc(sketch, "E184.23.8", {"start": v(-6.01, 12.81) * mm, "mid": v(-6.15, 12.54) * mm, "end": v(-6.41, 12.39) * mm});
            skPoint(sketch, "E184.23.9", {"position": v(-7.36, 13.08) * mm});
            skArc(sketch, "E184.23.10", {"start": v(-7, 13.01) * mm, "mid": v(-7.1, 12.52) * mm, "end": v(-7.24, 12.04) * mm, "construction": true});
            skArc(sketch, "E184.23.11", {"start": v(-7.36, 13.08) * mm, "mid": v(-7.28, 13.56) * mm, "end": v(-7.22, 14.04) * mm});
            skPoint(sketch, "E184.23.12", {"position": v(-7, 13.01) * mm});
            skArc(sketch, "E184.23.13", {"start": v(-6.6, 13.68) * mm, "mid": v(-6.59, 13.82) * mm, "end": v(-6.57, 13.97) * mm});
            skArc(sketch, "E184.23.14", {"start": v(-6.73, 12.36) * mm, "mid": v(-6.83, 12.33) * mm, "end": v(-6.89, 12.24) * mm});
            skArc(sketch, "E184.23.15", {"start": v(-6.5, 13.52) * mm, "mid": v(-6.58, 13.58) * mm, "end": v(-6.6, 13.68) * mm});
            skArc(sketch, "E184.24.0", {"start": v(-6.1, 15.5) * mm, "mid": v(-6.26, 15.56) * mm, "end": v(-6.42, 15.6) * mm});
            skArc(sketch, "E184.24.1", {"start": v(-5.8, 15) * mm, "mid": v(-5.88, 15.3) * mm, "end": v(-6.1, 15.5) * mm});
            skArc(sketch, "E184.24.2", {"start": v(-7.18, 15) * mm, "mid": v(-7.19, 14.52) * mm, "end": v(-7.22, 14.04) * mm});
            skPoint(sketch, "E184.24.3", {"position": v(-6.55, 15) * mm});
            skArc(sketch, "E184.24.4", {"start": v(-6.1, 14.5) * mm, "mid": v(-6.26, 14.44) * mm, "end": v(-6.42, 14.4) * mm});
            skLineSegment(sketch, "E184.24.5", {"start": v(-7.22, 15.96) * mm, "end": v(-6.57, 16.03) * mm});
            skArc(sketch, "E184.24.6", {"start": v(-6.55, 14.27) * mm, "mid": v(-6.56, 14.12) * mm, "end": v(-6.57, 13.97) * mm});
            skLineSegment(sketch, "E184.24.7", {"start": v(-7.22, 14.04) * mm, "end": v(-6.57, 13.97) * mm});
            skArc(sketch, "E184.24.8", {"start": v(-5.8, 15) * mm, "mid": v(-5.88, 14.7) * mm, "end": v(-6.1, 14.5) * mm});
            skPoint(sketch, "E184.24.9", {"position": v(-7.18, 15) * mm});
            skArc(sketch, "E184.24.10", {"start": v(-6.8, 15) * mm, "mid": v(-6.81, 14.5) * mm, "end": v(-6.85, 14) * mm, "construction": true});
            skArc(sketch, "E184.24.11", {"start": v(-7.18, 15) * mm, "mid": v(-7.19, 15.48) * mm, "end": v(-7.22, 15.96) * mm});
            skPoint(sketch, "E184.24.12", {"position": v(-6.8, 15) * mm});
            skArc(sketch, "E184.24.13", {"start": v(-6.55, 15.73) * mm, "mid": v(-6.56, 15.88) * mm, "end": v(-6.57, 16.03) * mm});
            skArc(sketch, "E184.24.14", {"start": v(-6.42, 14.4) * mm, "mid": v(-6.5, 14.36) * mm, "end": v(-6.55, 14.27) * mm});
            skArc(sketch, "E184.24.15", {"start": v(-6.42, 15.6) * mm, "mid": v(-6.5, 15.64) * mm, "end": v(-6.55, 15.73) * mm});
            skArc(sketch, "E184.25.0", {"start": v(-6.41, 17.61) * mm, "mid": v(-6.57, 17.64) * mm, "end": v(-6.73, 17.64) * mm});
            skArc(sketch, "E184.25.1", {"start": v(-6.01, 17.19) * mm, "mid": v(-6.15, 17.46) * mm, "end": v(-6.41, 17.61) * mm});
            skArc(sketch, "E184.25.2", {"start": v(-7.36, 16.92) * mm, "mid": v(-7.28, 16.44) * mm, "end": v(-7.22, 15.96) * mm});
            skPoint(sketch, "E184.25.3", {"position": v(-6.75, 17.04) * mm});
            skArc(sketch, "E184.25.4", {"start": v(-6.22, 16.64) * mm, "mid": v(-6.36, 16.55) * mm, "end": v(-6.5, 16.48) * mm});
            skLineSegment(sketch, "E184.25.5", {"start": v(-7.6, 17.85) * mm, "end": v(-6.97, 18.04) * mm});
            skArc(sketch, "E184.25.6", {"start": v(-6.6, 16.32) * mm, "mid": v(-6.59, 16.18) * mm, "end": v(-6.57, 16.03) * mm});
            skLineSegment(sketch, "E184.25.7", {"start": v(-7.22, 15.96) * mm, "end": v(-6.57, 16.03) * mm});
            skArc(sketch, "E184.25.8", {"start": v(-6.01, 17.19) * mm, "mid": v(-6.04, 16.88) * mm, "end": v(-6.22, 16.64) * mm});
            skPoint(sketch, "E184.25.9", {"position": v(-7.36, 16.92) * mm});
            skArc(sketch, "E184.25.10", {"start": v(-7, 16.99) * mm, "mid": v(-6.91, 16.5) * mm, "end": v(-6.85, 16) * mm, "construction": true});
            skArc(sketch, "E184.25.11", {"start": v(-7.36, 16.92) * mm, "mid": v(-7.47, 17.39) * mm, "end": v(-7.6, 17.85) * mm});
            skPoint(sketch, "E184.25.12", {"position": v(-7, 16.99) * mm});
            skArc(sketch, "E184.25.13", {"start": v(-6.89, 17.76) * mm, "mid": v(-6.93, 17.9) * mm, "end": v(-6.97, 18.04) * mm});
            skArc(sketch, "E184.25.14", {"start": v(-6.5, 16.48) * mm, "mid": v(-6.58, 16.42) * mm, "end": v(-6.6, 16.32) * mm});
            skArc(sketch, "E184.25.15", {"start": v(-6.73, 17.64) * mm, "mid": v(-6.83, 17.67) * mm, "end": v(-6.89, 17.76) * mm});
            skArc(sketch, "E184.26.0", {"start": v(-7.13, 19.63) * mm, "mid": v(-7.29, 19.63) * mm, "end": v(-7.45, 19.6) * mm});
            skArc(sketch, "E184.26.1", {"start": v(-6.65, 19.29) * mm, "mid": v(-6.84, 19.53) * mm, "end": v(-7.13, 19.63) * mm});
            skArc(sketch, "E184.26.2", {"start": v(-7.92, 18.76) * mm, "mid": v(-7.75, 18.3) * mm, "end": v(-7.6, 17.85) * mm});
            skPoint(sketch, "E184.26.3", {"position": v(-7.34, 19) * mm});
            skArc(sketch, "E184.26.4", {"start": v(-6.75, 18.7) * mm, "mid": v(-6.86, 18.6) * mm, "end": v(-7, 18.5) * mm});
            skLineSegment(sketch, "E184.26.5", {"start": v(-8.34, 19.63) * mm, "end": v(-7.76, 19.94) * mm});
            skArc(sketch, "E184.26.6", {"start": v(-7.06, 18.33) * mm, "mid": v(-7.02, 18.18) * mm, "end": v(-6.97, 18.04) * mm});
            skLineSegment(sketch, "E184.26.7", {"start": v(-7.6, 17.85) * mm, "end": v(-6.97, 18.04) * mm});
            skArc(sketch, "E184.26.8", {"start": v(-6.65, 19.29) * mm, "mid": v(-6.61, 18.98) * mm, "end": v(-6.75, 18.7) * mm});
            skPoint(sketch, "E184.26.9", {"position": v(-7.92, 18.76) * mm});
            skArc(sketch, "E184.26.10", {"start": v(-7.58, 18.9) * mm, "mid": v(-7.4, 18.44) * mm, "end": v(-7.24, 17.96) * mm, "construction": true});
            skArc(sketch, "E184.26.11", {"start": v(-7.92, 18.76) * mm, "mid": v(-8.12, 19.2) * mm, "end": v(-8.34, 19.63) * mm});
            skPoint(sketch, "E184.26.12", {"position": v(-7.58, 18.9) * mm});
            skArc(sketch, "E184.26.13", {"start": v(-7.62, 19.67) * mm, "mid": v(-7.69, 19.8) * mm, "end": v(-7.76, 19.94) * mm});
            skArc(sketch, "E184.26.14", {"start": v(-7, 18.5) * mm, "mid": v(-7.06, 18.43) * mm, "end": v(-7.06, 18.33) * mm});
            skArc(sketch, "E184.26.15", {"start": v(-7.45, 19.6) * mm, "mid": v(-7.55, 19.6) * mm, "end": v(-7.62, 19.67) * mm});
            skArc(sketch, "E184.27.0", {"start": v(-8.22, 21.47) * mm, "mid": v(-8.38, 21.43) * mm, "end": v(-8.53, 21.37) * mm});
            skArc(sketch, "E184.27.1", {"start": v(-7.68, 21.22) * mm, "mid": v(-7.92, 21.42) * mm, "end": v(-8.22, 21.47) * mm});
            skArc(sketch, "E184.27.2", {"start": v(-8.83, 20.46) * mm, "mid": v(-8.57, 20.05) * mm, "end": v(-8.34, 19.63) * mm});
            skPoint(sketch, "E184.27.3", {"position": v(-8.3, 20.8) * mm});
            skArc(sketch, "E184.27.4", {"start": v(-7.67, 20.64) * mm, "mid": v(-7.76, 20.5) * mm, "end": v(-7.87, 20.39) * mm});
            skLineSegment(sketch, "E184.27.5", {"start": v(-9.4, 21.23) * mm, "end": v(-8.9, 21.65) * mm});
            skArc(sketch, "E184.27.6", {"start": v(-7.9, 20.2) * mm, "mid": v(-7.83, 20.07) * mm, "end": v(-7.76, 19.94) * mm});
            skLineSegment(sketch, "E184.27.7", {"start": v(-8.34, 19.63) * mm, "end": v(-7.76, 19.94) * mm});
            skArc(sketch, "E184.27.8", {"start": v(-7.68, 21.22) * mm, "mid": v(-7.6, 20.93) * mm, "end": v(-7.67, 20.64) * mm});
            skPoint(sketch, "E184.27.9", {"position": v(-8.83, 20.46) * mm});
            skArc(sketch, "E184.27.10", {"start": v(-8.52, 20.67) * mm, "mid": v(-8.25, 20.24) * mm, "end": v(-8, 19.8) * mm, "construction": true});
            skArc(sketch, "E184.27.11", {"start": v(-8.83, 20.46) * mm, "mid": v(-9.1, 20.85) * mm, "end": v(-9.4, 21.23) * mm});
            skPoint(sketch, "E184.27.12", {"position": v(-8.52, 20.67) * mm});
            skArc(sketch, "E184.27.13", {"start": v(-8.71, 21.41) * mm, "mid": v(-8.8, 21.53) * mm, "end": v(-8.9, 21.65) * mm});
            skArc(sketch, "E184.27.14", {"start": v(-7.87, 20.39) * mm, "mid": v(-7.92, 20.3) * mm, "end": v(-7.9, 20.2) * mm});
            skArc(sketch, "E184.27.15", {"start": v(-8.53, 21.37) * mm, "mid": v(-8.63, 21.36) * mm, "end": v(-8.71, 21.41) * mm});
            skArc(sketch, "E184.28.0", {"start": v(-9.65, 23.05) * mm, "mid": v(-9.8, 23) * mm, "end": v(-9.93, 22.9) * mm});
            skArc(sketch, "E184.28.1", {"start": v(-9.08, 22.92) * mm, "mid": v(-9.35, 23.07) * mm, "end": v(-9.65, 23.05) * mm});
            skArc(sketch, "E184.28.2", {"start": v(-10.05, 21.95) * mm, "mid": v(-9.72, 21.6) * mm, "end": v(-9.4, 21.23) * mm});
            skPoint(sketch, "E184.28.3", {"position": v(-9.6, 22.4) * mm});
            skArc(sketch, "E184.28.4", {"start": v(-8.95, 22.35) * mm, "mid": v(-9, 22.2) * mm, "end": v(-9.1, 22.07) * mm});
            skLineSegment(sketch, "E184.28.5", {"start": v(-10.77, 22.6) * mm, "end": v(-10.35, 23.1) * mm});
            skArc(sketch, "E184.28.6", {"start": v(-9.1, 21.88) * mm, "mid": v(-9, 21.76) * mm, "end": v(-8.9, 21.65) * mm});
            skLineSegment(sketch, "E184.28.7", {"start": v(-9.4, 21.23) * mm, "end": v(-8.9, 21.65) * mm});
            skArc(sketch, "E184.28.8", {"start": v(-9.08, 22.92) * mm, "mid": v(-8.93, 22.65) * mm, "end": v(-8.95, 22.35) * mm});
            skPoint(sketch, "E184.28.9", {"position": v(-10.05, 21.95) * mm});
            skArc(sketch, "E184.28.10", {"start": v(-9.79, 22.21) * mm, "mid": v(-9.44, 21.85) * mm, "end": v(-9.12, 21.47) * mm, "construction": true});
            skArc(sketch, "E184.28.11", {"start": v(-10.05, 21.95) * mm, "mid": v(-10.4, 22.28) * mm, "end": v(-10.77, 22.6) * mm});
            skPoint(sketch, "E184.28.12", {"position": v(-9.79, 22.21) * mm});
            skArc(sketch, "E184.28.13", {"start": v(-10.12, 22.9) * mm, "mid": v(-10.24, 23) * mm, "end": v(-10.35, 23.1) * mm});
            skArc(sketch, "E184.28.14", {"start": v(-9.1, 22.07) * mm, "mid": v(-9.13, 21.97) * mm, "end": v(-9.1, 21.88) * mm});
            skArc(sketch, "E184.28.15", {"start": v(-9.93, 22.9) * mm, "mid": v(-10.03, 22.87) * mm, "end": v(-10.12, 22.9) * mm});
            skArc(sketch, "E184.29.0", {"start": v(-11.36, 24.33) * mm, "mid": v(-11.5, 24.24) * mm, "end": v(-11.61, 24.13) * mm});
            skArc(sketch, "E184.29.1", {"start": v(-10.78, 24.32) * mm, "mid": v(-11.07, 24.4) * mm, "end": v(-11.36, 24.33) * mm});
            skArc(sketch, "E184.29.2", {"start": v(-11.54, 23.17) * mm, "mid": v(-11.15, 22.9) * mm, "end": v(-10.77, 22.6) * mm});
            skPoint(sketch, "E184.29.3", {"position": v(-11.2, 23.7) * mm});
            skArc(sketch, "E184.29.4", {"start": v(-10.53, 23.78) * mm, "mid": v(-10.57, 23.62) * mm, "end": v(-10.63, 23.47) * mm});
            skLineSegment(sketch, "E184.29.5", {"start": v(-12.37, 23.66) * mm, "end": v(-12.06, 24.24) * mm});
            skArc(sketch, "E184.29.6", {"start": v(-10.59, 23.29) * mm, "mid": v(-10.47, 23.2) * mm, "end": v(-10.35, 23.1) * mm});
            skLineSegment(sketch, "E184.29.7", {"start": v(-10.77, 22.6) * mm, "end": v(-10.35, 23.1) * mm});
            skArc(sketch, "E184.29.8", {"start": v(-10.78, 24.32) * mm, "mid": v(-10.58, 24.08) * mm, "end": v(-10.53, 23.78) * mm});
            skPoint(sketch, "E184.29.9", {"position": v(-11.54, 23.17) * mm});
            skArc(sketch, "E184.29.10", {"start": v(-11.33, 23.48) * mm, "mid": v(-10.92, 23.2) * mm, "end": v(-10.53, 22.88) * mm, "construction": true});
            skArc(sketch, "E184.29.11", {"start": v(-11.54, 23.17) * mm, "mid": v(-11.95, 23.43) * mm, "end": v(-12.37, 23.66) * mm});
            skPoint(sketch, "E184.29.12", {"position": v(-11.33, 23.48) * mm});
            skArc(sketch, "E184.29.13", {"start": v(-11.8, 24.1) * mm, "mid": v(-11.93, 24.17) * mm, "end": v(-12.06, 24.24) * mm});
            skArc(sketch, "E184.29.14", {"start": v(-10.63, 23.47) * mm, "mid": v(-10.64, 23.37) * mm, "end": v(-10.59, 23.29) * mm});
            skArc(sketch, "E184.29.15", {"start": v(-11.61, 24.13) * mm, "mid": v(-11.7, 24.08) * mm, "end": v(-11.8, 24.1) * mm});
            skArc(sketch, "E184.30.0", {"start": v(-13.3, 25.25) * mm, "mid": v(-13.4, 25.14) * mm, "end": v(-13.5, 25) * mm});
            skArc(sketch, "E184.30.1", {"start": v(-12.71, 25.35) * mm, "mid": v(-13.02, 25.39) * mm, "end": v(-13.3, 25.25) * mm});
            skArc(sketch, "E184.30.2", {"start": v(-13.24, 24.08) * mm, "mid": v(-12.8, 23.88) * mm, "end": v(-12.37, 23.66) * mm});
            skPoint(sketch, "E184.30.3", {"position": v(-13, 24.66) * mm});
            skArc(sketch, "E184.30.4", {"start": v(-12.37, 24.87) * mm, "mid": v(-12.37, 24.71) * mm, "end": v(-12.4, 24.55) * mm});
            skLineSegment(sketch, "E184.30.5", {"start": v(-14.15, 24.4) * mm, "end": v(-13.96, 25.03) * mm});
            skArc(sketch, "E184.30.6", {"start": v(-12.33, 24.38) * mm, "mid": v(-12.2, 24.31) * mm, "end": v(-12.06, 24.24) * mm});
            skLineSegment(sketch, "E184.30.7", {"start": v(-12.37, 23.66) * mm, "end": v(-12.06, 24.24) * mm});
            skArc(sketch, "E184.30.8", {"start": v(-12.71, 25.35) * mm, "mid": v(-12.47, 25.16) * mm, "end": v(-12.37, 24.87) * mm});
            skPoint(sketch, "E184.30.9", {"position": v(-13.24, 24.08) * mm});
            skArc(sketch, "E184.30.10", {"start": v(-13.1, 24.42) * mm, "mid": v(-12.64, 24.22) * mm, "end": v(-12.2, 24) * mm, "construction": true});
            skArc(sketch, "E184.30.11", {"start": v(-13.24, 24.08) * mm, "mid": v(-13.7, 24.25) * mm, "end": v(-14.15, 24.4) * mm});
            skPoint(sketch, "E184.30.12", {"position": v(-13.1, 24.42) * mm});
            skArc(sketch, "E184.30.13", {"start": v(-13.67, 24.94) * mm, "mid": v(-13.82, 24.98) * mm, "end": v(-13.96, 25.03) * mm});
            skArc(sketch, "E184.30.14", {"start": v(-12.4, 24.55) * mm, "mid": v(-12.4, 24.45) * mm, "end": v(-12.33, 24.38) * mm});
            skArc(sketch, "E184.30.15", {"start": v(-13.5, 25) * mm, "mid": v(-13.57, 24.94) * mm, "end": v(-13.67, 24.94) * mm});
            skArc(sketch, "E184.31.0", {"start": v(-15.36, 25.78) * mm, "mid": v(-15.45, 25.64) * mm, "end": v(-15.52, 25.5) * mm});
            skArc(sketch, "E184.31.1", {"start": v(-14.81, 25.99) * mm, "mid": v(-15.12, 25.96) * mm, "end": v(-15.36, 25.78) * mm});
            skArc(sketch, "E184.31.2", {"start": v(-15.08, 24.64) * mm, "mid": v(-14.61, 24.53) * mm, "end": v(-14.15, 24.4) * mm});
            skPoint(sketch, "E184.31.3", {"position": v(-14.96, 25.25) * mm});
            skArc(sketch, "E184.31.4", {"start": v(-14.39, 25.59) * mm, "mid": v(-14.36, 25.43) * mm, "end": v(-14.36, 25.27) * mm});
            skArc(sketch, "E184.31.6", {"start": v(-14.24, 25.11) * mm, "mid": v(-14.1, 25.07) * mm, "end": v(-13.96, 25.03) * mm});
            skLineSegment(sketch, "E184.31.7", {"start": v(-14.15, 24.4) * mm, "end": v(-13.96, 25.03) * mm});
            skArc(sketch, "E184.31.8", {"start": v(-14.81, 25.99) * mm, "mid": v(-14.54, 25.85) * mm, "end": v(-14.39, 25.59) * mm});
            skPoint(sketch, "E184.31.9", {"position": v(-15.08, 24.64) * mm});
            skArc(sketch, "E184.31.10", {"start": v(-15.01, 25) * mm, "mid": v(-14.52, 24.9) * mm, "end": v(-14.04, 24.76) * mm, "construction": true});
            skArc(sketch, "E184.31.11", {"start": v(-15.08, 24.64) * mm, "mid": v(-15.56, 24.72) * mm, "end": v(-16.04, 24.78) * mm});
            skPoint(sketch, "E184.31.12", {"position": v(-15.01, 25) * mm});
            skArc(sketch, "E184.31.13", {"start": v(-15.68, 25.4) * mm, "mid": v(-15.82, 25.41) * mm, "end": v(-15.97, 25.43) * mm});
            skArc(sketch, "E184.31.14", {"start": v(-14.36, 25.27) * mm, "mid": v(-14.33, 25.17) * mm, "end": v(-14.24, 25.11) * mm});
            skArc(sketch, "E184.31.15", {"start": v(-15.52, 25.5) * mm, "mid": v(-15.58, 25.42) * mm, "end": v(-15.68, 25.4) * mm});
            skLineSegment(sketch, "E185.0", {"start": v(-27.25, 15) * mm, "end": v(-6.75, 15) * mm});
            skSolve(sketch);
        }
        {
            var Q0;
            Q0 = qSketchRegion(id + "F28", true);
            extrude(context, id + "F29", {"entities" : qUnion([Q0]), "operationType" : NewBodyOperationType.REMOVE, "endBound" : BoundingType.SYMMETRIC, "oppositeDirection" : true, "depth" : 6.5 * mm});
        }
        {
            var Q0;
            Q0=makeQuery(id+"F2.boolean.opBoolean","MERGE",FACE,{"derivedFrom":[makeQuery(id+"F1.opExtrude","SWEPT_FACE",FACE,{"disambiguationData":[OSD([sQuery(id+"F0.wireOp",EDGE,"E4"),sQuery(id+"F0.wireOp",EDGE,"E22")])]}),makeQuery(id+"F2.opExtrude","SWEPT_FACE",FACE,{"disambiguationData":[OSD([sQuery(id+"F0.wireOp",EDGE,"E35")])]})]});
            var Q1;
            Q1=sQuery(id+"F0.wireOp",VERTEX,"E19.MirrorP");
            cPlane(context, id + "F30", {"entities" : qUnion([Q0, Q1]), "cplaneType" : CPlaneType.PLANE_POINT, "offset" : 150 * mm, "width" : 150 * mm, "height" : 150 * mm});
        }
        {
            var Q0;
            Q0=qCreatedBy(id+"F30.planeOp",FACE);
            var sketch = newSketch(context, id + "F31", { "sketchPlane" : qUnion([Q0])});
            skLineSegment(sketch, "E186", {"start": v(-17, 12.16) * mm, "end": v(-17, 9.53) * mm, "construction": true});
            skArc(sketch, "E187", {"start": v(-17, 26.2) * mm, "mid": v(-16.7, 26.12) * mm, "end": v(-16.5, 25.9) * mm});
            skArc(sketch, "E188", {"start": v(-16.5, 25.9) * mm, "mid": v(-16.44, 25.74) * mm, "end": v(-16.4, 25.58) * mm});
            skArc(sketch, "E189", {"start": v(-16.4, 25.58) * mm, "mid": v(-16.36, 25.5) * mm, "end": v(-16.27, 25.45) * mm});
            skPoint(sketch, "E190", {"position": v(-17, 24.82) * mm});
            skPoint(sketch, "E191", {"position": v(-17, 25.45) * mm});
            skPoint(sketch, "E192", {"position": v(-17, 25.2) * mm});
            skArc(sketch, "E193", {"start": v(-17, 25.2) * mm, "mid": v(-16.5, 25.19) * mm, "end": v(-16, 25.15) * mm, "construction": true});
            skLineSegment(sketch, "E194", {"start": v(-16.04, 24.78) * mm, "end": v(-15.97, 25.43) * mm});
            skArc(sketch, "E195", {"start": v(-16.27, 25.45) * mm, "mid": v(-16.12, 25.44) * mm, "end": v(-15.97, 25.43) * mm});
            skArc(sketch, "E196", {"start": v(-17, 24.82) * mm, "mid": v(-16.52, 24.81) * mm, "end": v(-16.04, 24.78) * mm});
            skArc(sketch, "E197.MirrorCS", {"start": v(-17, 26.2) * mm, "mid": v(-17.3, 26.12) * mm, "end": v(-17.5, 25.9) * mm});
            skArc(sketch, "E198.MirrorCS", {"start": v(-17.5, 25.9) * mm, "mid": v(-17.56, 25.74) * mm, "end": v(-17.6, 25.58) * mm});
            skArc(sketch, "E199.MirrorCS", {"start": v(-17.6, 25.58) * mm, "mid": v(-17.64, 25.5) * mm, "end": v(-17.73, 25.45) * mm});
            skArc(sketch, "E200.MirrorCS", {"start": v(-17.73, 25.45) * mm, "mid": v(-17.88, 25.44) * mm, "end": v(-18.03, 25.43) * mm});
            skLineSegment(sketch, "E201.MirrorCS", {"start": v(-17.96, 24.78) * mm, "end": v(-18.03, 25.43) * mm});
            skArc(sketch, "E202.MirrorCS", {"start": v(-17, 24.82) * mm, "mid": v(-17.48, 24.81) * mm, "end": v(-17.96, 24.78) * mm});
            skArc(sketch, "E203.1.0", {"start": v(-19.61, 25.59) * mm, "mid": v(-19.64, 25.43) * mm, "end": v(-19.64, 25.27) * mm});
            skArc(sketch, "E203.1.1", {"start": v(-19.19, 25.99) * mm, "mid": v(-19.46, 25.85) * mm, "end": v(-19.61, 25.59) * mm});
            skArc(sketch, "E203.1.2", {"start": v(-18.92, 24.64) * mm, "mid": v(-18.44, 24.72) * mm, "end": v(-17.96, 24.78) * mm});
            skPoint(sketch, "E203.1.3", {"position": v(-19.04, 25.25) * mm});
            skArc(sketch, "E203.1.4", {"start": v(-18.64, 25.78) * mm, "mid": v(-18.55, 25.64) * mm, "end": v(-18.48, 25.5) * mm});
            skLineSegment(sketch, "E203.1.5", {"start": v(-19.85, 24.4) * mm, "end": v(-20.04, 25.03) * mm});
            skArc(sketch, "E203.1.6", {"start": v(-18.32, 25.4) * mm, "mid": v(-18.18, 25.41) * mm, "end": v(-18.03, 25.43) * mm});
            skArc(sketch, "E203.1.8", {"start": v(-19.19, 25.99) * mm, "mid": v(-18.88, 25.96) * mm, "end": v(-18.64, 25.78) * mm});
            skPoint(sketch, "E203.1.9", {"position": v(-18.92, 24.64) * mm});
            skArc(sketch, "E203.1.10", {"start": v(-18.99, 25) * mm, "mid": v(-18.5, 25.09) * mm, "end": v(-18, 25.15) * mm, "construction": true});
            skArc(sketch, "E203.1.11", {"start": v(-18.92, 24.64) * mm, "mid": v(-19.39, 24.53) * mm, "end": v(-19.85, 24.4) * mm});
            skPoint(sketch, "E203.1.12", {"position": v(-18.99, 25) * mm});
            skArc(sketch, "E203.1.13", {"start": v(-19.76, 25.11) * mm, "mid": v(-19.9, 25.07) * mm, "end": v(-20.04, 25.03) * mm});
            skArc(sketch, "E203.1.14", {"start": v(-18.48, 25.5) * mm, "mid": v(-18.42, 25.42) * mm, "end": v(-18.32, 25.4) * mm});
            skArc(sketch, "E203.1.15", {"start": v(-19.64, 25.27) * mm, "mid": v(-19.67, 25.17) * mm, "end": v(-19.76, 25.11) * mm});
            skArc(sketch, "E203.2.0", {"start": v(-21.63, 24.87) * mm, "mid": v(-21.63, 24.71) * mm, "end": v(-21.6, 24.55) * mm});
            skArc(sketch, "E203.2.1", {"start": v(-21.29, 25.35) * mm, "mid": v(-21.53, 25.16) * mm, "end": v(-21.63, 24.87) * mm});
            skArc(sketch, "E203.2.2", {"start": v(-20.76, 24.08) * mm, "mid": v(-20.3, 24.25) * mm, "end": v(-19.85, 24.4) * mm});
            skPoint(sketch, "E203.2.3", {"position": v(-21, 24.66) * mm});
            skArc(sketch, "E203.2.4", {"start": v(-20.7, 25.25) * mm, "mid": v(-20.6, 25.14) * mm, "end": v(-20.5, 25) * mm});
            skLineSegment(sketch, "E203.2.5", {"start": v(-21.63, 23.66) * mm, "end": v(-21.94, 24.24) * mm});
            skArc(sketch, "E203.2.6", {"start": v(-20.33, 24.94) * mm, "mid": v(-20.18, 24.98) * mm, "end": v(-20.04, 25.03) * mm});
            skLineSegment(sketch, "E203.2.7", {"start": v(-19.85, 24.4) * mm, "end": v(-20.04, 25.03) * mm});
            skArc(sketch, "E203.2.8", {"start": v(-21.29, 25.35) * mm, "mid": v(-20.98, 25.39) * mm, "end": v(-20.7, 25.25) * mm});
            skPoint(sketch, "E203.2.9", {"position": v(-20.76, 24.08) * mm});
            skArc(sketch, "E203.2.10", {"start": v(-20.9, 24.42) * mm, "mid": v(-20.44, 24.6) * mm, "end": v(-19.96, 24.76) * mm, "construction": true});
            skArc(sketch, "E203.2.11", {"start": v(-20.76, 24.08) * mm, "mid": v(-21.2, 23.88) * mm, "end": v(-21.63, 23.66) * mm});
            skPoint(sketch, "E203.2.12", {"position": v(-20.9, 24.42) * mm});
            skArc(sketch, "E203.2.13", {"start": v(-21.67, 24.38) * mm, "mid": v(-21.8, 24.31) * mm, "end": v(-21.94, 24.24) * mm});
            skArc(sketch, "E203.2.14", {"start": v(-20.5, 25) * mm, "mid": v(-20.43, 24.94) * mm, "end": v(-20.33, 24.94) * mm});
            skArc(sketch, "E203.2.15", {"start": v(-21.6, 24.55) * mm, "mid": v(-21.6, 24.45) * mm, "end": v(-21.67, 24.38) * mm});
            skArc(sketch, "E203.3.0", {"start": v(-23.47, 23.78) * mm, "mid": v(-23.43, 23.62) * mm, "end": v(-23.37, 23.47) * mm});
            skArc(sketch, "E203.3.1", {"start": v(-23.22, 24.32) * mm, "mid": v(-23.42, 24.08) * mm, "end": v(-23.47, 23.78) * mm});
            skArc(sketch, "E203.3.2", {"start": v(-22.46, 23.17) * mm, "mid": v(-22.05, 23.43) * mm, "end": v(-21.63, 23.66) * mm});
            skPoint(sketch, "E203.3.3", {"position": v(-22.8, 23.7) * mm});
            skArc(sketch, "E203.3.4", {"start": v(-22.64, 24.33) * mm, "mid": v(-22.5, 24.24) * mm, "end": v(-22.39, 24.13) * mm});
            skLineSegment(sketch, "E203.3.5", {"start": v(-23.23, 22.6) * mm, "end": v(-23.65, 23.1) * mm});
            skArc(sketch, "E203.3.6", {"start": v(-22.2, 24.1) * mm, "mid": v(-22.07, 24.17) * mm, "end": v(-21.94, 24.24) * mm});
            skLineSegment(sketch, "E203.3.7", {"start": v(-21.63, 23.66) * mm, "end": v(-21.94, 24.24) * mm});
            skArc(sketch, "E203.3.8", {"start": v(-23.22, 24.32) * mm, "mid": v(-22.93, 24.4) * mm, "end": v(-22.64, 24.33) * mm});
            skPoint(sketch, "E203.3.9", {"position": v(-22.46, 23.17) * mm});
            skArc(sketch, "E203.3.10", {"start": v(-22.67, 23.48) * mm, "mid": v(-22.24, 23.75) * mm, "end": v(-21.8, 24) * mm, "construction": true});
            skArc(sketch, "E203.3.11", {"start": v(-22.46, 23.17) * mm, "mid": v(-22.85, 22.9) * mm, "end": v(-23.23, 22.6) * mm});
            skPoint(sketch, "E203.3.12", {"position": v(-22.67, 23.48) * mm});
            skArc(sketch, "E203.3.13", {"start": v(-23.41, 23.29) * mm, "mid": v(-23.53, 23.2) * mm, "end": v(-23.65, 23.1) * mm});
            skArc(sketch, "E203.3.14", {"start": v(-22.39, 24.13) * mm, "mid": v(-22.3, 24.08) * mm, "end": v(-22.2, 24.1) * mm});
            skArc(sketch, "E203.3.15", {"start": v(-23.37, 23.47) * mm, "mid": v(-23.36, 23.37) * mm, "end": v(-23.41, 23.29) * mm});
            skArc(sketch, "E203.4.0", {"start": v(-25.05, 22.35) * mm, "mid": v(-25, 22.2) * mm, "end": v(-24.9, 22.07) * mm});
            skArc(sketch, "E203.4.1", {"start": v(-24.92, 22.92) * mm, "mid": v(-25.07, 22.65) * mm, "end": v(-25.05, 22.35) * mm});
            skArc(sketch, "E203.4.2", {"start": v(-23.95, 21.95) * mm, "mid": v(-23.6, 22.28) * mm, "end": v(-23.23, 22.6) * mm});
            skPoint(sketch, "E203.4.3", {"position": v(-24.4, 22.4) * mm});
            skArc(sketch, "E203.4.4", {"start": v(-24.35, 23.05) * mm, "mid": v(-24.2, 23) * mm, "end": v(-24.07, 22.9) * mm});
            skLineSegment(sketch, "E203.4.5", {"start": v(-24.6, 21.23) * mm, "end": v(-25.1, 21.65) * mm});
            skArc(sketch, "E203.4.6", {"start": v(-23.88, 22.9) * mm, "mid": v(-23.76, 23) * mm, "end": v(-23.65, 23.1) * mm});
            skLineSegment(sketch, "E203.4.7", {"start": v(-23.23, 22.6) * mm, "end": v(-23.65, 23.1) * mm});
            skArc(sketch, "E203.4.8", {"start": v(-24.92, 22.92) * mm, "mid": v(-24.65, 23.07) * mm, "end": v(-24.35, 23.05) * mm});
            skPoint(sketch, "E203.4.9", {"position": v(-23.95, 21.95) * mm});
            skArc(sketch, "E203.4.10", {"start": v(-24.21, 22.21) * mm, "mid": v(-23.85, 22.56) * mm, "end": v(-23.47, 22.88) * mm, "construction": true});
            skArc(sketch, "E203.4.11", {"start": v(-23.95, 21.95) * mm, "mid": v(-24.28, 21.6) * mm, "end": v(-24.6, 21.23) * mm});
            skPoint(sketch, "E203.4.12", {"position": v(-24.21, 22.21) * mm});
            skArc(sketch, "E203.4.13", {"start": v(-24.9, 21.88) * mm, "mid": v(-25, 21.76) * mm, "end": v(-25.1, 21.65) * mm});
            skArc(sketch, "E203.4.14", {"start": v(-24.07, 22.9) * mm, "mid": v(-23.97, 22.87) * mm, "end": v(-23.88, 22.9) * mm});
            skArc(sketch, "E203.4.15", {"start": v(-24.9, 22.07) * mm, "mid": v(-24.87, 21.97) * mm, "end": v(-24.9, 21.88) * mm});
            skArc(sketch, "E203.5.0", {"start": v(-26.33, 20.64) * mm, "mid": v(-26.24, 20.5) * mm, "end": v(-26.13, 20.39) * mm});
            skArc(sketch, "E203.5.1", {"start": v(-26.32, 21.22) * mm, "mid": v(-26.4, 20.93) * mm, "end": v(-26.33, 20.64) * mm});
            skArc(sketch, "E203.5.2", {"start": v(-25.17, 20.46) * mm, "mid": v(-24.9, 20.85) * mm, "end": v(-24.6, 21.23) * mm});
            skPoint(sketch, "E203.5.3", {"position": v(-25.7, 20.8) * mm});
            skArc(sketch, "E203.5.4", {"start": v(-25.78, 21.47) * mm, "mid": v(-25.62, 21.43) * mm, "end": v(-25.47, 21.37) * mm});
            skLineSegment(sketch, "E203.5.5", {"start": v(-25.66, 19.63) * mm, "end": v(-26.24, 19.94) * mm});
            skArc(sketch, "E203.5.6", {"start": v(-25.29, 21.41) * mm, "mid": v(-25.2, 21.53) * mm, "end": v(-25.1, 21.65) * mm});
            skLineSegment(sketch, "E203.5.7", {"start": v(-24.6, 21.23) * mm, "end": v(-25.1, 21.65) * mm});
            skArc(sketch, "E203.5.8", {"start": v(-26.32, 21.22) * mm, "mid": v(-26.08, 21.42) * mm, "end": v(-25.78, 21.47) * mm});
            skPoint(sketch, "E203.5.9", {"position": v(-25.17, 20.46) * mm});
            skArc(sketch, "E203.5.10", {"start": v(-25.48, 20.67) * mm, "mid": v(-25.2, 21.08) * mm, "end": v(-24.88, 21.47) * mm, "construction": true});
            skArc(sketch, "E203.5.11", {"start": v(-25.17, 20.46) * mm, "mid": v(-25.43, 20.05) * mm, "end": v(-25.66, 19.63) * mm});
            skPoint(sketch, "E203.5.12", {"position": v(-25.48, 20.67) * mm});
            skArc(sketch, "E203.5.13", {"start": v(-26.1, 20.2) * mm, "mid": v(-26.17, 20.07) * mm, "end": v(-26.24, 19.94) * mm});
            skArc(sketch, "E203.5.14", {"start": v(-25.47, 21.37) * mm, "mid": v(-25.37, 21.36) * mm, "end": v(-25.29, 21.41) * mm});
            skArc(sketch, "E203.5.15", {"start": v(-26.13, 20.39) * mm, "mid": v(-26.08, 20.3) * mm, "end": v(-26.1, 20.2) * mm});
            skArc(sketch, "E203.6.0", {"start": v(-27.25, 18.7) * mm, "mid": v(-27.14, 18.6) * mm, "end": v(-27, 18.5) * mm});
            skArc(sketch, "E203.6.1", {"start": v(-27.35, 19.29) * mm, "mid": v(-27.39, 18.98) * mm, "end": v(-27.25, 18.7) * mm});
            skArc(sketch, "E203.6.2", {"start": v(-26.08, 18.76) * mm, "mid": v(-25.88, 19.2) * mm, "end": v(-25.66, 19.63) * mm});
            skPoint(sketch, "E203.6.3", {"position": v(-26.66, 19) * mm});
            skArc(sketch, "E203.6.4", {"start": v(-26.87, 19.63) * mm, "mid": v(-26.71, 19.63) * mm, "end": v(-26.55, 19.6) * mm});
            skLineSegment(sketch, "E203.6.5", {"start": v(-26.4, 17.85) * mm, "end": v(-27.03, 18.04) * mm});
            skArc(sketch, "E203.6.6", {"start": v(-26.38, 19.67) * mm, "mid": v(-26.31, 19.8) * mm, "end": v(-26.24, 19.94) * mm});
            skLineSegment(sketch, "E203.6.7", {"start": v(-25.66, 19.63) * mm, "end": v(-26.24, 19.94) * mm});
            skArc(sketch, "E203.6.8", {"start": v(-27.35, 19.29) * mm, "mid": v(-27.16, 19.53) * mm, "end": v(-26.87, 19.63) * mm});
            skPoint(sketch, "E203.6.9", {"position": v(-26.08, 18.76) * mm});
            skArc(sketch, "E203.6.10", {"start": v(-26.42, 18.9) * mm, "mid": v(-26.22, 19.36) * mm, "end": v(-26, 19.8) * mm, "construction": true});
            skArc(sketch, "E203.6.11", {"start": v(-26.08, 18.76) * mm, "mid": v(-26.25, 18.3) * mm, "end": v(-26.4, 17.85) * mm});
            skPoint(sketch, "E203.6.12", {"position": v(-26.42, 18.9) * mm});
            skArc(sketch, "E203.6.13", {"start": v(-26.94, 18.33) * mm, "mid": v(-26.98, 18.18) * mm, "end": v(-27.03, 18.04) * mm});
            skArc(sketch, "E203.6.14", {"start": v(-26.55, 19.6) * mm, "mid": v(-26.45, 19.6) * mm, "end": v(-26.38, 19.67) * mm});
            skArc(sketch, "E203.6.15", {"start": v(-27, 18.5) * mm, "mid": v(-26.94, 18.43) * mm, "end": v(-26.94, 18.33) * mm});
            skArc(sketch, "E203.7.0", {"start": v(-27.78, 16.64) * mm, "mid": v(-27.64, 16.55) * mm, "end": v(-27.5, 16.48) * mm});
            skArc(sketch, "E203.7.1", {"start": v(-27.99, 17.19) * mm, "mid": v(-27.96, 16.88) * mm, "end": v(-27.78, 16.64) * mm});
            skArc(sketch, "E203.7.2", {"start": v(-26.64, 16.92) * mm, "mid": v(-26.53, 17.39) * mm, "end": v(-26.4, 17.85) * mm});
            skPoint(sketch, "E203.7.3", {"position": v(-27.25, 17.04) * mm});
            skArc(sketch, "E203.7.4", {"start": v(-27.59, 17.61) * mm, "mid": v(-27.43, 17.64) * mm, "end": v(-27.27, 17.64) * mm});
            skLineSegment(sketch, "E203.7.5", {"start": v(-26.78, 15.96) * mm, "end": v(-27.43, 16.03) * mm});
            skArc(sketch, "E203.7.6", {"start": v(-27.11, 17.76) * mm, "mid": v(-27.07, 17.9) * mm, "end": v(-27.03, 18.04) * mm});
            skLineSegment(sketch, "E203.7.7", {"start": v(-26.4, 17.85) * mm, "end": v(-27.03, 18.04) * mm});
            skArc(sketch, "E203.7.8", {"start": v(-27.99, 17.19) * mm, "mid": v(-27.85, 17.46) * mm, "end": v(-27.59, 17.61) * mm});
            skPoint(sketch, "E203.7.9", {"position": v(-26.64, 16.92) * mm});
            skArc(sketch, "E203.7.10", {"start": v(-27, 16.99) * mm, "mid": v(-26.9, 17.48) * mm, "end": v(-26.76, 17.96) * mm, "construction": true});
            skArc(sketch, "E203.7.11", {"start": v(-26.64, 16.92) * mm, "mid": v(-26.72, 16.44) * mm, "end": v(-26.78, 15.96) * mm});
            skPoint(sketch, "E203.7.12", {"position": v(-27, 16.99) * mm});
            skArc(sketch, "E203.7.13", {"start": v(-27.4, 16.32) * mm, "mid": v(-27.41, 16.18) * mm, "end": v(-27.43, 16.03) * mm});
            skArc(sketch, "E203.7.14", {"start": v(-27.27, 17.64) * mm, "mid": v(-27.17, 17.67) * mm, "end": v(-27.11, 17.76) * mm});
            skArc(sketch, "E203.7.15", {"start": v(-27.5, 16.48) * mm, "mid": v(-27.42, 16.42) * mm, "end": v(-27.4, 16.32) * mm});
            skArc(sketch, "E203.8.0", {"start": v(-27.9, 14.5) * mm, "mid": v(-27.74, 14.44) * mm, "end": v(-27.58, 14.4) * mm});
            skArc(sketch, "E203.8.1", {"start": v(-28.2, 15) * mm, "mid": v(-28.12, 14.7) * mm, "end": v(-27.9, 14.5) * mm});
            skArc(sketch, "E203.8.2", {"start": v(-26.82, 15) * mm, "mid": v(-26.81, 15.48) * mm, "end": v(-26.78, 15.96) * mm});
            skPoint(sketch, "E203.8.3", {"position": v(-27.45, 15) * mm});
            skArc(sketch, "E203.8.4", {"start": v(-27.9, 15.5) * mm, "mid": v(-27.74, 15.56) * mm, "end": v(-27.58, 15.6) * mm});
            skLineSegment(sketch, "E203.8.5", {"start": v(-26.78, 14.04) * mm, "end": v(-27.43, 13.97) * mm});
            skArc(sketch, "E203.8.6", {"start": v(-27.45, 15.73) * mm, "mid": v(-27.44, 15.88) * mm, "end": v(-27.43, 16.03) * mm});
            skLineSegment(sketch, "E203.8.7", {"start": v(-26.78, 15.96) * mm, "end": v(-27.43, 16.03) * mm});
            skArc(sketch, "E203.8.8", {"start": v(-28.2, 15) * mm, "mid": v(-28.12, 15.3) * mm, "end": v(-27.9, 15.5) * mm});
            skPoint(sketch, "E203.8.9", {"position": v(-26.82, 15) * mm});
            skArc(sketch, "E203.8.10", {"start": v(-27.2, 15) * mm, "mid": v(-27.19, 15.5) * mm, "end": v(-27.15, 16) * mm, "construction": true});
            skArc(sketch, "E203.8.11", {"start": v(-26.82, 15) * mm, "mid": v(-26.81, 14.52) * mm, "end": v(-26.78, 14.04) * mm});
            skPoint(sketch, "E203.8.12", {"position": v(-27.2, 15) * mm});
            skArc(sketch, "E203.8.13", {"start": v(-27.45, 14.27) * mm, "mid": v(-27.44, 14.12) * mm, "end": v(-27.43, 13.97) * mm});
            skArc(sketch, "E203.8.14", {"start": v(-27.58, 15.6) * mm, "mid": v(-27.5, 15.64) * mm, "end": v(-27.45, 15.73) * mm});
            skArc(sketch, "E203.8.15", {"start": v(-27.58, 14.4) * mm, "mid": v(-27.5, 14.36) * mm, "end": v(-27.45, 14.27) * mm});
            skArc(sketch, "E203.9.0", {"start": v(-27.59, 12.39) * mm, "mid": v(-27.43, 12.36) * mm, "end": v(-27.27, 12.36) * mm});
            skArc(sketch, "E203.9.1", {"start": v(-27.99, 12.81) * mm, "mid": v(-27.85, 12.54) * mm, "end": v(-27.59, 12.39) * mm});
            skArc(sketch, "E203.9.2", {"start": v(-26.64, 13.08) * mm, "mid": v(-26.72, 13.56) * mm, "end": v(-26.78, 14.04) * mm});
            skPoint(sketch, "E203.9.3", {"position": v(-27.25, 12.96) * mm});
            skArc(sketch, "E203.9.4", {"start": v(-27.78, 13.36) * mm, "mid": v(-27.64, 13.45) * mm, "end": v(-27.5, 13.52) * mm});
            skLineSegment(sketch, "E203.9.5", {"start": v(-26.4, 12.15) * mm, "end": v(-27.03, 11.96) * mm});
            skArc(sketch, "E203.9.6", {"start": v(-27.4, 13.68) * mm, "mid": v(-27.41, 13.82) * mm, "end": v(-27.43, 13.97) * mm});
            skLineSegment(sketch, "E203.9.7", {"start": v(-26.78, 14.04) * mm, "end": v(-27.43, 13.97) * mm});
            skArc(sketch, "E203.9.8", {"start": v(-27.99, 12.81) * mm, "mid": v(-27.96, 13.12) * mm, "end": v(-27.78, 13.36) * mm});
            skPoint(sketch, "E203.9.9", {"position": v(-26.64, 13.08) * mm});
            skArc(sketch, "E203.9.10", {"start": v(-27, 13.01) * mm, "mid": v(-27.09, 13.5) * mm, "end": v(-27.15, 14) * mm, "construction": true});
            skArc(sketch, "E203.9.11", {"start": v(-26.64, 13.08) * mm, "mid": v(-26.53, 12.61) * mm, "end": v(-26.4, 12.15) * mm});
            skPoint(sketch, "E203.9.12", {"position": v(-27, 13.01) * mm});
            skArc(sketch, "E203.9.13", {"start": v(-27.11, 12.24) * mm, "mid": v(-27.07, 12.1) * mm, "end": v(-27.03, 11.96) * mm});
            skArc(sketch, "E203.9.14", {"start": v(-27.5, 13.52) * mm, "mid": v(-27.42, 13.58) * mm, "end": v(-27.4, 13.68) * mm});
            skArc(sketch, "E203.9.15", {"start": v(-27.27, 12.36) * mm, "mid": v(-27.17, 12.33) * mm, "end": v(-27.11, 12.24) * mm});
            skArc(sketch, "E203.10.0", {"start": v(-26.87, 10.37) * mm, "mid": v(-26.71, 10.37) * mm, "end": v(-26.55, 10.4) * mm});
            skArc(sketch, "E203.10.1", {"start": v(-27.35, 10.71) * mm, "mid": v(-27.16, 10.47) * mm, "end": v(-26.87, 10.37) * mm});
            skArc(sketch, "E203.10.2", {"start": v(-26.08, 11.24) * mm, "mid": v(-26.25, 11.7) * mm, "end": v(-26.4, 12.15) * mm});
            skPoint(sketch, "E203.10.3", {"position": v(-26.66, 11) * mm});
            skArc(sketch, "E203.10.4", {"start": v(-27.25, 11.3) * mm, "mid": v(-27.14, 11.4) * mm, "end": v(-27, 11.5) * mm});
            skLineSegment(sketch, "E203.10.5", {"start": v(-25.66, 10.37) * mm, "end": v(-26.24, 10.06) * mm});
            skArc(sketch, "E203.10.6", {"start": v(-26.94, 11.67) * mm, "mid": v(-26.98, 11.82) * mm, "end": v(-27.03, 11.96) * mm});
            skLineSegment(sketch, "E203.10.7", {"start": v(-26.4, 12.15) * mm, "end": v(-27.03, 11.96) * mm});
            skArc(sketch, "E203.10.8", {"start": v(-27.35, 10.71) * mm, "mid": v(-27.39, 11.02) * mm, "end": v(-27.25, 11.3) * mm});
            skPoint(sketch, "E203.10.9", {"position": v(-26.08, 11.24) * mm});
            skArc(sketch, "E203.10.10", {"start": v(-26.42, 11.1) * mm, "mid": v(-26.6, 11.56) * mm, "end": v(-26.76, 12.04) * mm, "construction": true});
            skArc(sketch, "E203.10.11", {"start": v(-26.08, 11.24) * mm, "mid": v(-25.88, 10.8) * mm, "end": v(-25.66, 10.37) * mm});
            skPoint(sketch, "E203.10.12", {"position": v(-26.42, 11.1) * mm});
            skArc(sketch, "E203.10.13", {"start": v(-26.38, 10.33) * mm, "mid": v(-26.31, 10.2) * mm, "end": v(-26.24, 10.06) * mm});
            skArc(sketch, "E203.10.14", {"start": v(-27, 11.5) * mm, "mid": v(-26.94, 11.57) * mm, "end": v(-26.94, 11.67) * mm});
            skArc(sketch, "E203.10.15", {"start": v(-26.55, 10.4) * mm, "mid": v(-26.45, 10.4) * mm, "end": v(-26.38, 10.33) * mm});
            skArc(sketch, "E203.11.0", {"start": v(-25.78, 8.53) * mm, "mid": v(-25.62, 8.57) * mm, "end": v(-25.47, 8.63) * mm});
            skArc(sketch, "E203.11.1", {"start": v(-26.32, 8.78) * mm, "mid": v(-26.08, 8.58) * mm, "end": v(-25.78, 8.53) * mm});
            skArc(sketch, "E203.11.2", {"start": v(-25.17, 9.54) * mm, "mid": v(-25.43, 9.95) * mm, "end": v(-25.66, 10.37) * mm});
            skPoint(sketch, "E203.11.3", {"position": v(-25.7, 9.2) * mm});
            skArc(sketch, "E203.11.4", {"start": v(-26.33, 9.36) * mm, "mid": v(-26.24, 9.5) * mm, "end": v(-26.13, 9.61) * mm});
            skLineSegment(sketch, "E203.11.5", {"start": v(-24.6, 8.77) * mm, "end": v(-25.1, 8.35) * mm});
            skArc(sketch, "E203.11.6", {"start": v(-26.1, 9.8) * mm, "mid": v(-26.17, 9.93) * mm, "end": v(-26.24, 10.06) * mm});
            skLineSegment(sketch, "E203.11.7", {"start": v(-25.66, 10.37) * mm, "end": v(-26.24, 10.06) * mm});
            skArc(sketch, "E203.11.8", {"start": v(-26.32, 8.78) * mm, "mid": v(-26.4, 9.07) * mm, "end": v(-26.33, 9.36) * mm});
            skPoint(sketch, "E203.11.9", {"position": v(-25.17, 9.54) * mm});
            skArc(sketch, "E203.11.10", {"start": v(-25.48, 9.33) * mm, "mid": v(-25.75, 9.76) * mm, "end": v(-26, 10.2) * mm, "construction": true});
            skArc(sketch, "E203.11.11", {"start": v(-25.17, 9.54) * mm, "mid": v(-24.9, 9.15) * mm, "end": v(-24.6, 8.77) * mm});
            skPoint(sketch, "E203.11.12", {"position": v(-25.48, 9.33) * mm});
            skArc(sketch, "E203.11.13", {"start": v(-25.29, 8.59) * mm, "mid": v(-25.2, 8.47) * mm, "end": v(-25.1, 8.35) * mm});
            skArc(sketch, "E203.11.14", {"start": v(-26.13, 9.61) * mm, "mid": v(-26.08, 9.7) * mm, "end": v(-26.1, 9.8) * mm});
            skArc(sketch, "E203.11.15", {"start": v(-25.47, 8.63) * mm, "mid": v(-25.37, 8.64) * mm, "end": v(-25.29, 8.59) * mm});
            skArc(sketch, "E203.12.0", {"start": v(-24.35, 6.95) * mm, "mid": v(-24.2, 7) * mm, "end": v(-24.07, 7.1) * mm});
            skArc(sketch, "E203.12.1", {"start": v(-24.92, 7.08) * mm, "mid": v(-24.65, 6.93) * mm, "end": v(-24.35, 6.95) * mm});
            skArc(sketch, "E203.12.2", {"start": v(-23.95, 8.05) * mm, "mid": v(-24.28, 8.4) * mm, "end": v(-24.6, 8.77) * mm});
            skPoint(sketch, "E203.12.3", {"position": v(-24.4, 7.6) * mm});
            skArc(sketch, "E203.12.4", {"start": v(-25.05, 7.65) * mm, "mid": v(-25, 7.8) * mm, "end": v(-24.9, 7.93) * mm});
            skLineSegment(sketch, "E203.12.5", {"start": v(-23.23, 7.4) * mm, "end": v(-23.65, 6.9) * mm});
            skArc(sketch, "E203.12.6", {"start": v(-24.9, 8.12) * mm, "mid": v(-25, 8.24) * mm, "end": v(-25.1, 8.35) * mm});
            skLineSegment(sketch, "E203.12.7", {"start": v(-24.6, 8.77) * mm, "end": v(-25.1, 8.35) * mm});
            skArc(sketch, "E203.12.8", {"start": v(-24.92, 7.08) * mm, "mid": v(-25.07, 7.35) * mm, "end": v(-25.05, 7.65) * mm});
            skPoint(sketch, "E203.12.9", {"position": v(-23.95, 8.05) * mm});
            skArc(sketch, "E203.12.10", {"start": v(-24.21, 7.79) * mm, "mid": v(-24.56, 8.15) * mm, "end": v(-24.88, 8.53) * mm, "construction": true});
            skArc(sketch, "E203.12.11", {"start": v(-23.95, 8.05) * mm, "mid": v(-23.6, 7.72) * mm, "end": v(-23.23, 7.4) * mm});
            skPoint(sketch, "E203.12.12", {"position": v(-24.21, 7.79) * mm});
            skArc(sketch, "E203.12.13", {"start": v(-23.88, 7.1) * mm, "mid": v(-23.76, 7) * mm, "end": v(-23.65, 6.9) * mm});
            skArc(sketch, "E203.12.14", {"start": v(-24.9, 7.93) * mm, "mid": v(-24.87, 8.03) * mm, "end": v(-24.9, 8.12) * mm});
            skArc(sketch, "E203.12.15", {"start": v(-24.07, 7.1) * mm, "mid": v(-23.97, 7.13) * mm, "end": v(-23.88, 7.1) * mm});
            skArc(sketch, "E203.13.0", {"start": v(-22.64, 5.67) * mm, "mid": v(-22.5, 5.76) * mm, "end": v(-22.39, 5.87) * mm});
            skArc(sketch, "E203.13.1", {"start": v(-23.22, 5.68) * mm, "mid": v(-22.93, 5.6) * mm, "end": v(-22.64, 5.67) * mm});
            skArc(sketch, "E203.13.2", {"start": v(-22.46, 6.83) * mm, "mid": v(-22.85, 7.1) * mm, "end": v(-23.23, 7.4) * mm});
            skPoint(sketch, "E203.13.3", {"position": v(-22.8, 6.3) * mm});
            skArc(sketch, "E203.13.4", {"start": v(-23.47, 6.22) * mm, "mid": v(-23.43, 6.38) * mm, "end": v(-23.37, 6.53) * mm});
            skLineSegment(sketch, "E203.13.5", {"start": v(-21.63, 6.34) * mm, "end": v(-21.94, 5.76) * mm});
            skArc(sketch, "E203.13.6", {"start": v(-23.41, 6.71) * mm, "mid": v(-23.53, 6.8) * mm, "end": v(-23.65, 6.9) * mm});
            skLineSegment(sketch, "E203.13.7", {"start": v(-23.23, 7.4) * mm, "end": v(-23.65, 6.9) * mm});
            skArc(sketch, "E203.13.8", {"start": v(-23.22, 5.68) * mm, "mid": v(-23.42, 5.92) * mm, "end": v(-23.47, 6.22) * mm});
            skPoint(sketch, "E203.13.9", {"position": v(-22.46, 6.83) * mm});
            skArc(sketch, "E203.13.10", {"start": v(-22.67, 6.52) * mm, "mid": v(-23.08, 6.8) * mm, "end": v(-23.47, 7.12) * mm, "construction": true});
            skArc(sketch, "E203.13.11", {"start": v(-22.46, 6.83) * mm, "mid": v(-22.05, 6.57) * mm, "end": v(-21.63, 6.34) * mm});
            skPoint(sketch, "E203.13.12", {"position": v(-22.67, 6.52) * mm});
            skArc(sketch, "E203.13.13", {"start": v(-22.2, 5.9) * mm, "mid": v(-22.07, 5.83) * mm, "end": v(-21.94, 5.76) * mm});
            skArc(sketch, "E203.13.14", {"start": v(-23.37, 6.53) * mm, "mid": v(-23.36, 6.63) * mm, "end": v(-23.41, 6.71) * mm});
            skArc(sketch, "E203.13.15", {"start": v(-22.39, 5.87) * mm, "mid": v(-22.3, 5.92) * mm, "end": v(-22.2, 5.9) * mm});
            skArc(sketch, "E203.14.0", {"start": v(-20.7, 4.75) * mm, "mid": v(-20.6, 4.86) * mm, "end": v(-20.5, 5) * mm});
            skArc(sketch, "E203.14.1", {"start": v(-21.29, 4.65) * mm, "mid": v(-20.98, 4.61) * mm, "end": v(-20.7, 4.75) * mm});
            skArc(sketch, "E203.14.2", {"start": v(-20.76, 5.92) * mm, "mid": v(-21.2, 6.12) * mm, "end": v(-21.63, 6.34) * mm});
            skPoint(sketch, "E203.14.3", {"position": v(-21, 5.34) * mm});
            skArc(sketch, "E203.14.4", {"start": v(-21.63, 5.13) * mm, "mid": v(-21.63, 5.29) * mm, "end": v(-21.6, 5.45) * mm});
            skLineSegment(sketch, "E203.14.5", {"start": v(-19.85, 5.6) * mm, "end": v(-20.04, 4.97) * mm});
            skArc(sketch, "E203.14.6", {"start": v(-21.67, 5.62) * mm, "mid": v(-21.8, 5.69) * mm, "end": v(-21.94, 5.76) * mm});
            skLineSegment(sketch, "E203.14.7", {"start": v(-21.63, 6.34) * mm, "end": v(-21.94, 5.76) * mm});
            skArc(sketch, "E203.14.8", {"start": v(-21.29, 4.65) * mm, "mid": v(-21.53, 4.84) * mm, "end": v(-21.63, 5.13) * mm});
            skPoint(sketch, "E203.14.9", {"position": v(-20.76, 5.92) * mm});
            skArc(sketch, "E203.14.10", {"start": v(-20.9, 5.58) * mm, "mid": v(-21.36, 5.78) * mm, "end": v(-21.8, 6) * mm, "construction": true});
            skArc(sketch, "E203.14.11", {"start": v(-20.76, 5.92) * mm, "mid": v(-20.3, 5.75) * mm, "end": v(-19.85, 5.6) * mm});
            skPoint(sketch, "E203.14.12", {"position": v(-20.9, 5.58) * mm});
            skArc(sketch, "E203.14.13", {"start": v(-20.33, 5.06) * mm, "mid": v(-20.18, 5.02) * mm, "end": v(-20.04, 4.97) * mm});
            skArc(sketch, "E203.14.14", {"start": v(-21.6, 5.45) * mm, "mid": v(-21.6, 5.55) * mm, "end": v(-21.67, 5.62) * mm});
            skArc(sketch, "E203.14.15", {"start": v(-20.5, 5) * mm, "mid": v(-20.43, 5.06) * mm, "end": v(-20.33, 5.06) * mm});
            skArc(sketch, "E203.15.0", {"start": v(-18.64, 4.22) * mm, "mid": v(-18.55, 4.36) * mm, "end": v(-18.48, 4.5) * mm});
            skArc(sketch, "E203.15.1", {"start": v(-19.19, 4.01) * mm, "mid": v(-18.88, 4.04) * mm, "end": v(-18.64, 4.22) * mm});
            skArc(sketch, "E203.15.2", {"start": v(-18.92, 5.36) * mm, "mid": v(-19.39, 5.47) * mm, "end": v(-19.85, 5.6) * mm});
            skPoint(sketch, "E203.15.3", {"position": v(-19.04, 4.75) * mm});
            skArc(sketch, "E203.15.4", {"start": v(-19.61, 4.41) * mm, "mid": v(-19.64, 4.57) * mm, "end": v(-19.64, 4.73) * mm});
            skLineSegment(sketch, "E203.15.5", {"start": v(-17.96, 5.22) * mm, "end": v(-18.03, 4.57) * mm});
            skArc(sketch, "E203.15.6", {"start": v(-19.76, 4.89) * mm, "mid": v(-19.9, 4.93) * mm, "end": v(-20.04, 4.97) * mm});
            skLineSegment(sketch, "E203.15.7", {"start": v(-19.85, 5.6) * mm, "end": v(-20.04, 4.97) * mm});
            skArc(sketch, "E203.15.8", {"start": v(-19.19, 4.01) * mm, "mid": v(-19.46, 4.15) * mm, "end": v(-19.61, 4.41) * mm});
            skPoint(sketch, "E203.15.9", {"position": v(-18.92, 5.36) * mm});
            skArc(sketch, "E203.15.10", {"start": v(-18.99, 5) * mm, "mid": v(-19.48, 5.1) * mm, "end": v(-19.96, 5.24) * mm, "construction": true});
            skArc(sketch, "E203.15.11", {"start": v(-18.92, 5.36) * mm, "mid": v(-18.44, 5.28) * mm, "end": v(-17.96, 5.22) * mm});
            skPoint(sketch, "E203.15.12", {"position": v(-18.99, 5) * mm});
            skArc(sketch, "E203.15.13", {"start": v(-18.32, 4.6) * mm, "mid": v(-18.18, 4.59) * mm, "end": v(-18.03, 4.57) * mm});
            skArc(sketch, "E203.15.14", {"start": v(-19.64, 4.73) * mm, "mid": v(-19.67, 4.83) * mm, "end": v(-19.76, 4.89) * mm});
            skArc(sketch, "E203.15.15", {"start": v(-18.48, 4.5) * mm, "mid": v(-18.42, 4.58) * mm, "end": v(-18.32, 4.6) * mm});
            skArc(sketch, "E203.16.0", {"start": v(-16.5, 4.1) * mm, "mid": v(-16.44, 4.26) * mm, "end": v(-16.4, 4.42) * mm});
            skArc(sketch, "E203.16.1", {"start": v(-17, 3.8) * mm, "mid": v(-16.7, 3.88) * mm, "end": v(-16.5, 4.1) * mm});
            skArc(sketch, "E203.16.2", {"start": v(-17, 5.18) * mm, "mid": v(-17.48, 5.19) * mm, "end": v(-17.96, 5.22) * mm});
            skPoint(sketch, "E203.16.3", {"position": v(-17, 4.55) * mm});
            skArc(sketch, "E203.16.4", {"start": v(-17.5, 4.1) * mm, "mid": v(-17.56, 4.26) * mm, "end": v(-17.6, 4.42) * mm});
            skLineSegment(sketch, "E203.16.5", {"start": v(-16.04, 5.22) * mm, "end": v(-15.97, 4.57) * mm});
            skArc(sketch, "E203.16.6", {"start": v(-17.73, 4.55) * mm, "mid": v(-17.88, 4.56) * mm, "end": v(-18.03, 4.57) * mm});
            skLineSegment(sketch, "E203.16.7", {"start": v(-17.96, 5.22) * mm, "end": v(-18.03, 4.57) * mm});
            skArc(sketch, "E203.16.8", {"start": v(-17, 3.8) * mm, "mid": v(-17.3, 3.88) * mm, "end": v(-17.5, 4.1) * mm});
            skPoint(sketch, "E203.16.9", {"position": v(-17, 5.18) * mm});
            skArc(sketch, "E203.16.10", {"start": v(-17, 4.8) * mm, "mid": v(-17.5, 4.81) * mm, "end": v(-18, 4.85) * mm, "construction": true});
            skArc(sketch, "E203.16.11", {"start": v(-17, 5.18) * mm, "mid": v(-16.52, 5.19) * mm, "end": v(-16.04, 5.22) * mm});
            skPoint(sketch, "E203.16.12", {"position": v(-17, 4.8) * mm});
            skArc(sketch, "E203.16.13", {"start": v(-16.27, 4.55) * mm, "mid": v(-16.12, 4.56) * mm, "end": v(-15.97, 4.57) * mm});
            skArc(sketch, "E203.16.14", {"start": v(-17.6, 4.42) * mm, "mid": v(-17.64, 4.5) * mm, "end": v(-17.73, 4.55) * mm});
            skArc(sketch, "E203.16.15", {"start": v(-16.4, 4.42) * mm, "mid": v(-16.36, 4.5) * mm, "end": v(-16.27, 4.55) * mm});
            skArc(sketch, "E203.17.0", {"start": v(-14.39, 4.41) * mm, "mid": v(-14.36, 4.57) * mm, "end": v(-14.36, 4.73) * mm});
            skArc(sketch, "E203.17.1", {"start": v(-14.81, 4.01) * mm, "mid": v(-14.54, 4.15) * mm, "end": v(-14.39, 4.41) * mm});
            skArc(sketch, "E203.17.2", {"start": v(-15.08, 5.36) * mm, "mid": v(-15.56, 5.28) * mm, "end": v(-16.04, 5.22) * mm});
            skPoint(sketch, "E203.17.3", {"position": v(-14.96, 4.75) * mm});
            skArc(sketch, "E203.17.4", {"start": v(-15.36, 4.22) * mm, "mid": v(-15.45, 4.36) * mm, "end": v(-15.52, 4.5) * mm});
            skLineSegment(sketch, "E203.17.5", {"start": v(-14.15, 5.6) * mm, "end": v(-13.96, 4.97) * mm});
            skArc(sketch, "E203.17.6", {"start": v(-15.68, 4.6) * mm, "mid": v(-15.82, 4.59) * mm, "end": v(-15.97, 4.57) * mm});
            skLineSegment(sketch, "E203.17.7", {"start": v(-16.04, 5.22) * mm, "end": v(-15.97, 4.57) * mm});
            skArc(sketch, "E203.17.8", {"start": v(-14.81, 4.01) * mm, "mid": v(-15.12, 4.04) * mm, "end": v(-15.36, 4.22) * mm});
            skPoint(sketch, "E203.17.9", {"position": v(-15.08, 5.36) * mm});
            skArc(sketch, "E203.17.10", {"start": v(-15.01, 5) * mm, "mid": v(-15.5, 4.91) * mm, "end": v(-16, 4.85) * mm, "construction": true});
            skArc(sketch, "E203.17.11", {"start": v(-15.08, 5.36) * mm, "mid": v(-14.61, 5.47) * mm, "end": v(-14.15, 5.6) * mm});
            skPoint(sketch, "E203.17.12", {"position": v(-15.01, 5) * mm});
            skArc(sketch, "E203.17.13", {"start": v(-14.24, 4.89) * mm, "mid": v(-14.1, 4.93) * mm, "end": v(-13.96, 4.97) * mm});
            skArc(sketch, "E203.17.14", {"start": v(-15.52, 4.5) * mm, "mid": v(-15.58, 4.58) * mm, "end": v(-15.68, 4.6) * mm});
            skArc(sketch, "E203.17.15", {"start": v(-14.36, 4.73) * mm, "mid": v(-14.33, 4.83) * mm, "end": v(-14.24, 4.89) * mm});
            skArc(sketch, "E203.18.0", {"start": v(-12.37, 5.13) * mm, "mid": v(-12.37, 5.29) * mm, "end": v(-12.4, 5.45) * mm});
            skArc(sketch, "E203.18.1", {"start": v(-12.71, 4.65) * mm, "mid": v(-12.47, 4.84) * mm, "end": v(-12.37, 5.13) * mm});
            skArc(sketch, "E203.18.2", {"start": v(-13.24, 5.92) * mm, "mid": v(-13.7, 5.75) * mm, "end": v(-14.15, 5.6) * mm});
            skPoint(sketch, "E203.18.3", {"position": v(-13, 5.34) * mm});
            skArc(sketch, "E203.18.4", {"start": v(-13.3, 4.75) * mm, "mid": v(-13.4, 4.86) * mm, "end": v(-13.5, 5) * mm});
            skLineSegment(sketch, "E203.18.5", {"start": v(-12.37, 6.34) * mm, "end": v(-12.06, 5.76) * mm});
            skArc(sketch, "E203.18.6", {"start": v(-13.67, 5.06) * mm, "mid": v(-13.82, 5.02) * mm, "end": v(-13.96, 4.97) * mm});
            skLineSegment(sketch, "E203.18.7", {"start": v(-14.15, 5.6) * mm, "end": v(-13.96, 4.97) * mm});
            skArc(sketch, "E203.18.8", {"start": v(-12.71, 4.65) * mm, "mid": v(-13.02, 4.61) * mm, "end": v(-13.3, 4.75) * mm});
            skPoint(sketch, "E203.18.9", {"position": v(-13.24, 5.92) * mm});
            skArc(sketch, "E203.18.10", {"start": v(-13.1, 5.58) * mm, "mid": v(-13.56, 5.4) * mm, "end": v(-14.04, 5.24) * mm, "construction": true});
            skArc(sketch, "E203.18.11", {"start": v(-13.24, 5.92) * mm, "mid": v(-12.8, 6.12) * mm, "end": v(-12.37, 6.34) * mm});
            skPoint(sketch, "E203.18.12", {"position": v(-13.1, 5.58) * mm});
            skArc(sketch, "E203.18.13", {"start": v(-12.33, 5.62) * mm, "mid": v(-12.2, 5.69) * mm, "end": v(-12.06, 5.76) * mm});
            skArc(sketch, "E203.18.14", {"start": v(-13.5, 5) * mm, "mid": v(-13.57, 5.06) * mm, "end": v(-13.67, 5.06) * mm});
            skArc(sketch, "E203.18.15", {"start": v(-12.4, 5.45) * mm, "mid": v(-12.4, 5.55) * mm, "end": v(-12.33, 5.62) * mm});
            skArc(sketch, "E203.19.0", {"start": v(-10.53, 6.22) * mm, "mid": v(-10.57, 6.38) * mm, "end": v(-10.63, 6.53) * mm});
            skArc(sketch, "E203.19.1", {"start": v(-10.78, 5.68) * mm, "mid": v(-10.58, 5.92) * mm, "end": v(-10.53, 6.22) * mm});
            skArc(sketch, "E203.19.2", {"start": v(-11.54, 6.83) * mm, "mid": v(-11.95, 6.57) * mm, "end": v(-12.37, 6.34) * mm});
            skPoint(sketch, "E203.19.3", {"position": v(-11.2, 6.3) * mm});
            skArc(sketch, "E203.19.4", {"start": v(-11.36, 5.67) * mm, "mid": v(-11.5, 5.76) * mm, "end": v(-11.61, 5.87) * mm});
            skLineSegment(sketch, "E203.19.5", {"start": v(-10.77, 7.4) * mm, "end": v(-10.35, 6.9) * mm});
            skArc(sketch, "E203.19.6", {"start": v(-11.8, 5.9) * mm, "mid": v(-11.93, 5.83) * mm, "end": v(-12.06, 5.76) * mm});
            skLineSegment(sketch, "E203.19.7", {"start": v(-12.37, 6.34) * mm, "end": v(-12.06, 5.76) * mm});
            skArc(sketch, "E203.19.8", {"start": v(-10.78, 5.68) * mm, "mid": v(-11.07, 5.6) * mm, "end": v(-11.36, 5.67) * mm});
            skPoint(sketch, "E203.19.9", {"position": v(-11.54, 6.83) * mm});
            skArc(sketch, "E203.19.10", {"start": v(-11.33, 6.52) * mm, "mid": v(-11.76, 6.25) * mm, "end": v(-12.2, 6) * mm, "construction": true});
            skArc(sketch, "E203.19.11", {"start": v(-11.54, 6.83) * mm, "mid": v(-11.15, 7.1) * mm, "end": v(-10.77, 7.4) * mm});
            skPoint(sketch, "E203.19.12", {"position": v(-11.33, 6.52) * mm});
            skArc(sketch, "E203.19.13", {"start": v(-10.59, 6.71) * mm, "mid": v(-10.47, 6.8) * mm, "end": v(-10.35, 6.9) * mm});
            skArc(sketch, "E203.19.14", {"start": v(-11.61, 5.87) * mm, "mid": v(-11.7, 5.92) * mm, "end": v(-11.8, 5.9) * mm});
            skArc(sketch, "E203.19.15", {"start": v(-10.63, 6.53) * mm, "mid": v(-10.64, 6.63) * mm, "end": v(-10.59, 6.71) * mm});
            skArc(sketch, "E203.20.0", {"start": v(-8.95, 7.65) * mm, "mid": v(-9, 7.8) * mm, "end": v(-9.1, 7.93) * mm});
            skArc(sketch, "E203.20.1", {"start": v(-9.08, 7.08) * mm, "mid": v(-8.93, 7.35) * mm, "end": v(-8.95, 7.65) * mm});
            skArc(sketch, "E203.20.2", {"start": v(-10.05, 8.05) * mm, "mid": v(-10.4, 7.72) * mm, "end": v(-10.77, 7.4) * mm});
            skPoint(sketch, "E203.20.3", {"position": v(-9.6, 7.6) * mm});
            skArc(sketch, "E203.20.4", {"start": v(-9.65, 6.95) * mm, "mid": v(-9.8, 7) * mm, "end": v(-9.93, 7.1) * mm});
            skLineSegment(sketch, "E203.20.5", {"start": v(-9.4, 8.77) * mm, "end": v(-8.9, 8.35) * mm});
            skArc(sketch, "E203.20.6", {"start": v(-10.12, 7.1) * mm, "mid": v(-10.24, 7) * mm, "end": v(-10.35, 6.9) * mm});
            skLineSegment(sketch, "E203.20.7", {"start": v(-10.77, 7.4) * mm, "end": v(-10.35, 6.9) * mm});
            skArc(sketch, "E203.20.8", {"start": v(-9.08, 7.08) * mm, "mid": v(-9.35, 6.93) * mm, "end": v(-9.65, 6.95) * mm});
            skPoint(sketch, "E203.20.9", {"position": v(-10.05, 8.05) * mm});
            skArc(sketch, "E203.20.10", {"start": v(-9.79, 7.79) * mm, "mid": v(-10.15, 7.44) * mm, "end": v(-10.53, 7.12) * mm, "construction": true});
            skArc(sketch, "E203.20.11", {"start": v(-10.05, 8.05) * mm, "mid": v(-9.72, 8.4) * mm, "end": v(-9.4, 8.77) * mm});
            skPoint(sketch, "E203.20.12", {"position": v(-9.79, 7.79) * mm});
            skArc(sketch, "E203.20.13", {"start": v(-9.1, 8.12) * mm, "mid": v(-9, 8.24) * mm, "end": v(-8.9, 8.35) * mm});
            skArc(sketch, "E203.20.14", {"start": v(-9.93, 7.1) * mm, "mid": v(-10.03, 7.13) * mm, "end": v(-10.12, 7.1) * mm});
            skArc(sketch, "E203.20.15", {"start": v(-9.1, 7.93) * mm, "mid": v(-9.13, 8.03) * mm, "end": v(-9.1, 8.12) * mm});
            skArc(sketch, "E203.21.0", {"start": v(-7.67, 9.36) * mm, "mid": v(-7.76, 9.5) * mm, "end": v(-7.87, 9.61) * mm});
            skArc(sketch, "E203.21.1", {"start": v(-7.68, 8.78) * mm, "mid": v(-7.6, 9.07) * mm, "end": v(-7.67, 9.36) * mm});
            skArc(sketch, "E203.21.2", {"start": v(-8.83, 9.54) * mm, "mid": v(-9.1, 9.15) * mm, "end": v(-9.4, 8.77) * mm});
            skPoint(sketch, "E203.21.3", {"position": v(-8.3, 9.2) * mm});
            skArc(sketch, "E203.21.4", {"start": v(-8.22, 8.53) * mm, "mid": v(-8.38, 8.57) * mm, "end": v(-8.53, 8.63) * mm});
            skLineSegment(sketch, "E203.21.5", {"start": v(-8.34, 10.37) * mm, "end": v(-7.76, 10.06) * mm});
            skArc(sketch, "E203.21.6", {"start": v(-8.71, 8.59) * mm, "mid": v(-8.8, 8.47) * mm, "end": v(-8.9, 8.35) * mm});
            skLineSegment(sketch, "E203.21.7", {"start": v(-9.4, 8.77) * mm, "end": v(-8.9, 8.35) * mm});
            skArc(sketch, "E203.21.8", {"start": v(-7.68, 8.78) * mm, "mid": v(-7.92, 8.58) * mm, "end": v(-8.22, 8.53) * mm});
            skPoint(sketch, "E203.21.9", {"position": v(-8.83, 9.54) * mm});
            skArc(sketch, "E203.21.10", {"start": v(-8.52, 9.33) * mm, "mid": v(-8.8, 8.92) * mm, "end": v(-9.12, 8.53) * mm, "construction": true});
            skArc(sketch, "E203.21.11", {"start": v(-8.83, 9.54) * mm, "mid": v(-8.57, 9.95) * mm, "end": v(-8.34, 10.37) * mm});
            skPoint(sketch, "E203.21.12", {"position": v(-8.52, 9.33) * mm});
            skArc(sketch, "E203.21.13", {"start": v(-7.9, 9.8) * mm, "mid": v(-7.83, 9.93) * mm, "end": v(-7.76, 10.06) * mm});
            skArc(sketch, "E203.21.14", {"start": v(-8.53, 8.63) * mm, "mid": v(-8.63, 8.64) * mm, "end": v(-8.71, 8.59) * mm});
            skArc(sketch, "E203.21.15", {"start": v(-7.87, 9.61) * mm, "mid": v(-7.92, 9.7) * mm, "end": v(-7.9, 9.8) * mm});
            skArc(sketch, "E203.22.0", {"start": v(-6.75, 11.3) * mm, "mid": v(-6.86, 11.4) * mm, "end": v(-7, 11.5) * mm});
            skArc(sketch, "E203.22.1", {"start": v(-6.65, 10.71) * mm, "mid": v(-6.61, 11.02) * mm, "end": v(-6.75, 11.3) * mm});
            skArc(sketch, "E203.22.2", {"start": v(-7.92, 11.24) * mm, "mid": v(-8.12, 10.8) * mm, "end": v(-8.34, 10.37) * mm});
            skPoint(sketch, "E203.22.3", {"position": v(-7.34, 11) * mm});
            skArc(sketch, "E203.22.4", {"start": v(-7.13, 10.37) * mm, "mid": v(-7.29, 10.37) * mm, "end": v(-7.45, 10.4) * mm});
            skLineSegment(sketch, "E203.22.5", {"start": v(-7.6, 12.15) * mm, "end": v(-6.97, 11.96) * mm});
            skArc(sketch, "E203.22.6", {"start": v(-7.62, 10.33) * mm, "mid": v(-7.69, 10.2) * mm, "end": v(-7.76, 10.06) * mm});
            skLineSegment(sketch, "E203.22.7", {"start": v(-8.34, 10.37) * mm, "end": v(-7.76, 10.06) * mm});
            skArc(sketch, "E203.22.8", {"start": v(-6.65, 10.71) * mm, "mid": v(-6.84, 10.47) * mm, "end": v(-7.13, 10.37) * mm});
            skPoint(sketch, "E203.22.9", {"position": v(-7.92, 11.24) * mm});
            skArc(sketch, "E203.22.10", {"start": v(-7.58, 11.1) * mm, "mid": v(-7.78, 10.64) * mm, "end": v(-8, 10.2) * mm, "construction": true});
            skArc(sketch, "E203.22.11", {"start": v(-7.92, 11.24) * mm, "mid": v(-7.75, 11.7) * mm, "end": v(-7.6, 12.15) * mm});
            skPoint(sketch, "E203.22.12", {"position": v(-7.58, 11.1) * mm});
            skArc(sketch, "E203.22.13", {"start": v(-7.06, 11.67) * mm, "mid": v(-7.02, 11.82) * mm, "end": v(-6.97, 11.96) * mm});
            skArc(sketch, "E203.22.14", {"start": v(-7.45, 10.4) * mm, "mid": v(-7.55, 10.4) * mm, "end": v(-7.62, 10.33) * mm});
            skArc(sketch, "E203.22.15", {"start": v(-7, 11.5) * mm, "mid": v(-7.06, 11.57) * mm, "end": v(-7.06, 11.67) * mm});
            skArc(sketch, "E203.23.0", {"start": v(-6.22, 13.36) * mm, "mid": v(-6.36, 13.45) * mm, "end": v(-6.5, 13.52) * mm});
            skArc(sketch, "E203.23.1", {"start": v(-6.01, 12.81) * mm, "mid": v(-6.04, 13.12) * mm, "end": v(-6.22, 13.36) * mm});
            skArc(sketch, "E203.23.2", {"start": v(-7.36, 13.08) * mm, "mid": v(-7.47, 12.61) * mm, "end": v(-7.6, 12.15) * mm});
            skPoint(sketch, "E203.23.3", {"position": v(-6.75, 12.96) * mm});
            skArc(sketch, "E203.23.4", {"start": v(-6.41, 12.39) * mm, "mid": v(-6.57, 12.36) * mm, "end": v(-6.73, 12.36) * mm});
            skLineSegment(sketch, "E203.23.5", {"start": v(-7.22, 14.04) * mm, "end": v(-6.57, 13.97) * mm});
            skArc(sketch, "E203.23.6", {"start": v(-6.89, 12.24) * mm, "mid": v(-6.93, 12.1) * mm, "end": v(-6.97, 11.96) * mm});
            skLineSegment(sketch, "E203.23.7", {"start": v(-7.6, 12.15) * mm, "end": v(-6.97, 11.96) * mm});
            skArc(sketch, "E203.23.8", {"start": v(-6.01, 12.81) * mm, "mid": v(-6.15, 12.54) * mm, "end": v(-6.41, 12.39) * mm});
            skPoint(sketch, "E203.23.9", {"position": v(-7.36, 13.08) * mm});
            skArc(sketch, "E203.23.10", {"start": v(-7, 13.01) * mm, "mid": v(-7.1, 12.52) * mm, "end": v(-7.24, 12.04) * mm, "construction": true});
            skArc(sketch, "E203.23.11", {"start": v(-7.36, 13.08) * mm, "mid": v(-7.28, 13.56) * mm, "end": v(-7.22, 14.04) * mm});
            skPoint(sketch, "E203.23.12", {"position": v(-7, 13.01) * mm});
            skArc(sketch, "E203.23.13", {"start": v(-6.6, 13.68) * mm, "mid": v(-6.59, 13.82) * mm, "end": v(-6.57, 13.97) * mm});
            skArc(sketch, "E203.23.14", {"start": v(-6.73, 12.36) * mm, "mid": v(-6.83, 12.33) * mm, "end": v(-6.89, 12.24) * mm});
            skArc(sketch, "E203.23.15", {"start": v(-6.5, 13.52) * mm, "mid": v(-6.58, 13.58) * mm, "end": v(-6.6, 13.68) * mm});
            skArc(sketch, "E203.24.0", {"start": v(-6.1, 15.5) * mm, "mid": v(-6.26, 15.56) * mm, "end": v(-6.42, 15.6) * mm});
            skArc(sketch, "E203.24.1", {"start": v(-5.8, 15) * mm, "mid": v(-5.88, 15.3) * mm, "end": v(-6.1, 15.5) * mm});
            skArc(sketch, "E203.24.2", {"start": v(-7.18, 15) * mm, "mid": v(-7.19, 14.52) * mm, "end": v(-7.22, 14.04) * mm});
            skPoint(sketch, "E203.24.3", {"position": v(-6.55, 15) * mm});
            skArc(sketch, "E203.24.4", {"start": v(-6.1, 14.5) * mm, "mid": v(-6.26, 14.44) * mm, "end": v(-6.42, 14.4) * mm});
            skLineSegment(sketch, "E203.24.5", {"start": v(-7.22, 15.96) * mm, "end": v(-6.57, 16.03) * mm});
            skArc(sketch, "E203.24.6", {"start": v(-6.55, 14.27) * mm, "mid": v(-6.56, 14.12) * mm, "end": v(-6.57, 13.97) * mm});
            skLineSegment(sketch, "E203.24.7", {"start": v(-7.22, 14.04) * mm, "end": v(-6.57, 13.97) * mm});
            skArc(sketch, "E203.24.8", {"start": v(-5.8, 15) * mm, "mid": v(-5.88, 14.7) * mm, "end": v(-6.1, 14.5) * mm});
            skPoint(sketch, "E203.24.9", {"position": v(-7.18, 15) * mm});
            skArc(sketch, "E203.24.10", {"start": v(-6.8, 15) * mm, "mid": v(-6.81, 14.5) * mm, "end": v(-6.85, 14) * mm, "construction": true});
            skArc(sketch, "E203.24.11", {"start": v(-7.18, 15) * mm, "mid": v(-7.19, 15.48) * mm, "end": v(-7.22, 15.96) * mm});
            skPoint(sketch, "E203.24.12", {"position": v(-6.8, 15) * mm});
            skArc(sketch, "E203.24.13", {"start": v(-6.55, 15.73) * mm, "mid": v(-6.56, 15.88) * mm, "end": v(-6.57, 16.03) * mm});
            skArc(sketch, "E203.24.14", {"start": v(-6.42, 14.4) * mm, "mid": v(-6.5, 14.36) * mm, "end": v(-6.55, 14.27) * mm});
            skArc(sketch, "E203.24.15", {"start": v(-6.42, 15.6) * mm, "mid": v(-6.5, 15.64) * mm, "end": v(-6.55, 15.73) * mm});
            skArc(sketch, "E203.25.0", {"start": v(-6.41, 17.61) * mm, "mid": v(-6.57, 17.64) * mm, "end": v(-6.73, 17.64) * mm});
            skArc(sketch, "E203.25.1", {"start": v(-6.01, 17.19) * mm, "mid": v(-6.15, 17.46) * mm, "end": v(-6.41, 17.61) * mm});
            skArc(sketch, "E203.25.2", {"start": v(-7.36, 16.92) * mm, "mid": v(-7.28, 16.44) * mm, "end": v(-7.22, 15.96) * mm});
            skPoint(sketch, "E203.25.3", {"position": v(-6.75, 17.04) * mm});
            skArc(sketch, "E203.25.4", {"start": v(-6.22, 16.64) * mm, "mid": v(-6.36, 16.55) * mm, "end": v(-6.5, 16.48) * mm});
            skLineSegment(sketch, "E203.25.5", {"start": v(-7.6, 17.85) * mm, "end": v(-6.97, 18.04) * mm});
            skArc(sketch, "E203.25.6", {"start": v(-6.6, 16.32) * mm, "mid": v(-6.59, 16.18) * mm, "end": v(-6.57, 16.03) * mm});
            skLineSegment(sketch, "E203.25.7", {"start": v(-7.22, 15.96) * mm, "end": v(-6.57, 16.03) * mm});
            skArc(sketch, "E203.25.8", {"start": v(-6.01, 17.19) * mm, "mid": v(-6.04, 16.88) * mm, "end": v(-6.22, 16.64) * mm});
            skPoint(sketch, "E203.25.9", {"position": v(-7.36, 16.92) * mm});
            skArc(sketch, "E203.25.10", {"start": v(-7, 16.99) * mm, "mid": v(-6.91, 16.5) * mm, "end": v(-6.85, 16) * mm, "construction": true});
            skArc(sketch, "E203.25.11", {"start": v(-7.36, 16.92) * mm, "mid": v(-7.47, 17.39) * mm, "end": v(-7.6, 17.85) * mm});
            skPoint(sketch, "E203.25.12", {"position": v(-7, 16.99) * mm});
            skArc(sketch, "E203.25.13", {"start": v(-6.89, 17.76) * mm, "mid": v(-6.93, 17.9) * mm, "end": v(-6.97, 18.04) * mm});
            skArc(sketch, "E203.25.14", {"start": v(-6.5, 16.48) * mm, "mid": v(-6.58, 16.42) * mm, "end": v(-6.6, 16.32) * mm});
            skArc(sketch, "E203.25.15", {"start": v(-6.73, 17.64) * mm, "mid": v(-6.83, 17.67) * mm, "end": v(-6.89, 17.76) * mm});
            skArc(sketch, "E203.26.0", {"start": v(-7.13, 19.63) * mm, "mid": v(-7.29, 19.63) * mm, "end": v(-7.45, 19.6) * mm});
            skArc(sketch, "E203.26.1", {"start": v(-6.65, 19.29) * mm, "mid": v(-6.84, 19.53) * mm, "end": v(-7.13, 19.63) * mm});
            skArc(sketch, "E203.26.2", {"start": v(-7.92, 18.76) * mm, "mid": v(-7.75, 18.3) * mm, "end": v(-7.6, 17.85) * mm});
            skPoint(sketch, "E203.26.3", {"position": v(-7.34, 19) * mm});
            skArc(sketch, "E203.26.4", {"start": v(-6.75, 18.7) * mm, "mid": v(-6.86, 18.6) * mm, "end": v(-7, 18.5) * mm});
            skLineSegment(sketch, "E203.26.5", {"start": v(-8.34, 19.63) * mm, "end": v(-7.76, 19.94) * mm});
            skArc(sketch, "E203.26.6", {"start": v(-7.06, 18.33) * mm, "mid": v(-7.02, 18.18) * mm, "end": v(-6.97, 18.04) * mm});
            skLineSegment(sketch, "E203.26.7", {"start": v(-7.6, 17.85) * mm, "end": v(-6.97, 18.04) * mm});
            skArc(sketch, "E203.26.8", {"start": v(-6.65, 19.29) * mm, "mid": v(-6.61, 18.98) * mm, "end": v(-6.75, 18.7) * mm});
            skPoint(sketch, "E203.26.9", {"position": v(-7.92, 18.76) * mm});
            skArc(sketch, "E203.26.10", {"start": v(-7.58, 18.9) * mm, "mid": v(-7.4, 18.44) * mm, "end": v(-7.24, 17.96) * mm, "construction": true});
            skArc(sketch, "E203.26.11", {"start": v(-7.92, 18.76) * mm, "mid": v(-8.12, 19.2) * mm, "end": v(-8.34, 19.63) * mm});
            skPoint(sketch, "E203.26.12", {"position": v(-7.58, 18.9) * mm});
            skArc(sketch, "E203.26.13", {"start": v(-7.62, 19.67) * mm, "mid": v(-7.69, 19.8) * mm, "end": v(-7.76, 19.94) * mm});
            skArc(sketch, "E203.26.14", {"start": v(-7, 18.5) * mm, "mid": v(-7.06, 18.43) * mm, "end": v(-7.06, 18.33) * mm});
            skArc(sketch, "E203.26.15", {"start": v(-7.45, 19.6) * mm, "mid": v(-7.55, 19.6) * mm, "end": v(-7.62, 19.67) * mm});
            skArc(sketch, "E203.27.0", {"start": v(-8.22, 21.47) * mm, "mid": v(-8.38, 21.43) * mm, "end": v(-8.53, 21.37) * mm});
            skArc(sketch, "E203.27.1", {"start": v(-7.68, 21.22) * mm, "mid": v(-7.92, 21.42) * mm, "end": v(-8.22, 21.47) * mm});
            skArc(sketch, "E203.27.2", {"start": v(-8.83, 20.46) * mm, "mid": v(-8.57, 20.05) * mm, "end": v(-8.34, 19.63) * mm});
            skPoint(sketch, "E203.27.3", {"position": v(-8.3, 20.8) * mm});
            skArc(sketch, "E203.27.4", {"start": v(-7.67, 20.64) * mm, "mid": v(-7.76, 20.5) * mm, "end": v(-7.87, 20.39) * mm});
            skLineSegment(sketch, "E203.27.5", {"start": v(-9.4, 21.23) * mm, "end": v(-8.9, 21.65) * mm});
            skArc(sketch, "E203.27.6", {"start": v(-7.9, 20.2) * mm, "mid": v(-7.83, 20.07) * mm, "end": v(-7.76, 19.94) * mm});
            skLineSegment(sketch, "E203.27.7", {"start": v(-8.34, 19.63) * mm, "end": v(-7.76, 19.94) * mm});
            skArc(sketch, "E203.27.8", {"start": v(-7.68, 21.22) * mm, "mid": v(-7.6, 20.93) * mm, "end": v(-7.67, 20.64) * mm});
            skPoint(sketch, "E203.27.9", {"position": v(-8.83, 20.46) * mm});
            skArc(sketch, "E203.27.10", {"start": v(-8.52, 20.67) * mm, "mid": v(-8.25, 20.24) * mm, "end": v(-8, 19.8) * mm, "construction": true});
            skArc(sketch, "E203.27.11", {"start": v(-8.83, 20.46) * mm, "mid": v(-9.1, 20.85) * mm, "end": v(-9.4, 21.23) * mm});
            skPoint(sketch, "E203.27.12", {"position": v(-8.52, 20.67) * mm});
            skArc(sketch, "E203.27.13", {"start": v(-8.71, 21.41) * mm, "mid": v(-8.8, 21.53) * mm, "end": v(-8.9, 21.65) * mm});
            skArc(sketch, "E203.27.14", {"start": v(-7.87, 20.39) * mm, "mid": v(-7.92, 20.3) * mm, "end": v(-7.9, 20.2) * mm});
            skArc(sketch, "E203.27.15", {"start": v(-8.53, 21.37) * mm, "mid": v(-8.63, 21.36) * mm, "end": v(-8.71, 21.41) * mm});
            skArc(sketch, "E203.28.0", {"start": v(-9.65, 23.05) * mm, "mid": v(-9.8, 23) * mm, "end": v(-9.93, 22.9) * mm});
            skArc(sketch, "E203.28.1", {"start": v(-9.08, 22.92) * mm, "mid": v(-9.35, 23.07) * mm, "end": v(-9.65, 23.05) * mm});
            skArc(sketch, "E203.28.2", {"start": v(-10.05, 21.95) * mm, "mid": v(-9.72, 21.6) * mm, "end": v(-9.4, 21.23) * mm});
            skPoint(sketch, "E203.28.3", {"position": v(-9.6, 22.4) * mm});
            skArc(sketch, "E203.28.4", {"start": v(-8.95, 22.35) * mm, "mid": v(-9, 22.2) * mm, "end": v(-9.1, 22.07) * mm});
            skLineSegment(sketch, "E203.28.5", {"start": v(-10.77, 22.6) * mm, "end": v(-10.35, 23.1) * mm});
            skArc(sketch, "E203.28.6", {"start": v(-9.1, 21.88) * mm, "mid": v(-9, 21.76) * mm, "end": v(-8.9, 21.65) * mm});
            skLineSegment(sketch, "E203.28.7", {"start": v(-9.4, 21.23) * mm, "end": v(-8.9, 21.65) * mm});
            skArc(sketch, "E203.28.8", {"start": v(-9.08, 22.92) * mm, "mid": v(-8.93, 22.65) * mm, "end": v(-8.95, 22.35) * mm});
            skPoint(sketch, "E203.28.9", {"position": v(-10.05, 21.95) * mm});
            skArc(sketch, "E203.28.10", {"start": v(-9.79, 22.21) * mm, "mid": v(-9.44, 21.85) * mm, "end": v(-9.12, 21.47) * mm, "construction": true});
            skArc(sketch, "E203.28.11", {"start": v(-10.05, 21.95) * mm, "mid": v(-10.4, 22.28) * mm, "end": v(-10.77, 22.6) * mm});
            skPoint(sketch, "E203.28.12", {"position": v(-9.79, 22.21) * mm});
            skArc(sketch, "E203.28.13", {"start": v(-10.12, 22.9) * mm, "mid": v(-10.24, 23) * mm, "end": v(-10.35, 23.1) * mm});
            skArc(sketch, "E203.28.14", {"start": v(-9.1, 22.07) * mm, "mid": v(-9.13, 21.97) * mm, "end": v(-9.1, 21.88) * mm});
            skArc(sketch, "E203.28.15", {"start": v(-9.93, 22.9) * mm, "mid": v(-10.03, 22.87) * mm, "end": v(-10.12, 22.9) * mm});
            skArc(sketch, "E203.29.0", {"start": v(-11.36, 24.33) * mm, "mid": v(-11.5, 24.24) * mm, "end": v(-11.61, 24.13) * mm});
            skArc(sketch, "E203.29.1", {"start": v(-10.78, 24.32) * mm, "mid": v(-11.07, 24.4) * mm, "end": v(-11.36, 24.33) * mm});
            skArc(sketch, "E203.29.2", {"start": v(-11.54, 23.17) * mm, "mid": v(-11.15, 22.9) * mm, "end": v(-10.77, 22.6) * mm});
            skPoint(sketch, "E203.29.3", {"position": v(-11.2, 23.7) * mm});
            skArc(sketch, "E203.29.4", {"start": v(-10.53, 23.78) * mm, "mid": v(-10.57, 23.62) * mm, "end": v(-10.63, 23.47) * mm});
            skLineSegment(sketch, "E203.29.5", {"start": v(-12.37, 23.66) * mm, "end": v(-12.06, 24.24) * mm});
            skArc(sketch, "E203.29.6", {"start": v(-10.59, 23.29) * mm, "mid": v(-10.47, 23.2) * mm, "end": v(-10.35, 23.1) * mm});
            skLineSegment(sketch, "E203.29.7", {"start": v(-10.77, 22.6) * mm, "end": v(-10.35, 23.1) * mm});
            skArc(sketch, "E203.29.8", {"start": v(-10.78, 24.32) * mm, "mid": v(-10.58, 24.08) * mm, "end": v(-10.53, 23.78) * mm});
            skPoint(sketch, "E203.29.9", {"position": v(-11.54, 23.17) * mm});
            skArc(sketch, "E203.29.10", {"start": v(-11.33, 23.48) * mm, "mid": v(-10.92, 23.2) * mm, "end": v(-10.53, 22.88) * mm, "construction": true});
            skArc(sketch, "E203.29.11", {"start": v(-11.54, 23.17) * mm, "mid": v(-11.95, 23.43) * mm, "end": v(-12.37, 23.66) * mm});
            skPoint(sketch, "E203.29.12", {"position": v(-11.33, 23.48) * mm});
            skArc(sketch, "E203.29.13", {"start": v(-11.8, 24.1) * mm, "mid": v(-11.93, 24.17) * mm, "end": v(-12.06, 24.24) * mm});
            skArc(sketch, "E203.29.14", {"start": v(-10.63, 23.47) * mm, "mid": v(-10.64, 23.37) * mm, "end": v(-10.59, 23.29) * mm});
            skArc(sketch, "E203.29.15", {"start": v(-11.61, 24.13) * mm, "mid": v(-11.7, 24.08) * mm, "end": v(-11.8, 24.1) * mm});
            skArc(sketch, "E203.30.0", {"start": v(-13.3, 25.25) * mm, "mid": v(-13.4, 25.14) * mm, "end": v(-13.5, 25) * mm});
            skArc(sketch, "E203.30.1", {"start": v(-12.71, 25.35) * mm, "mid": v(-13.02, 25.39) * mm, "end": v(-13.3, 25.25) * mm});
            skArc(sketch, "E203.30.2", {"start": v(-13.24, 24.08) * mm, "mid": v(-12.8, 23.88) * mm, "end": v(-12.37, 23.66) * mm});
            skPoint(sketch, "E203.30.3", {"position": v(-13, 24.66) * mm});
            skArc(sketch, "E203.30.4", {"start": v(-12.37, 24.87) * mm, "mid": v(-12.37, 24.71) * mm, "end": v(-12.4, 24.55) * mm});
            skLineSegment(sketch, "E203.30.5", {"start": v(-14.15, 24.4) * mm, "end": v(-13.96, 25.03) * mm});
            skArc(sketch, "E203.30.6", {"start": v(-12.33, 24.38) * mm, "mid": v(-12.2, 24.31) * mm, "end": v(-12.06, 24.24) * mm});
            skLineSegment(sketch, "E203.30.7", {"start": v(-12.37, 23.66) * mm, "end": v(-12.06, 24.24) * mm});
            skArc(sketch, "E203.30.8", {"start": v(-12.71, 25.35) * mm, "mid": v(-12.47, 25.16) * mm, "end": v(-12.37, 24.87) * mm});
            skPoint(sketch, "E203.30.9", {"position": v(-13.24, 24.08) * mm});
            skArc(sketch, "E203.30.10", {"start": v(-13.1, 24.42) * mm, "mid": v(-12.64, 24.22) * mm, "end": v(-12.2, 24) * mm, "construction": true});
            skArc(sketch, "E203.30.11", {"start": v(-13.24, 24.08) * mm, "mid": v(-13.7, 24.25) * mm, "end": v(-14.15, 24.4) * mm});
            skPoint(sketch, "E203.30.12", {"position": v(-13.1, 24.42) * mm});
            skArc(sketch, "E203.30.13", {"start": v(-13.67, 24.94) * mm, "mid": v(-13.82, 24.98) * mm, "end": v(-13.96, 25.03) * mm});
            skArc(sketch, "E203.30.14", {"start": v(-12.4, 24.55) * mm, "mid": v(-12.4, 24.45) * mm, "end": v(-12.33, 24.38) * mm});
            skArc(sketch, "E203.30.15", {"start": v(-13.5, 25) * mm, "mid": v(-13.57, 24.94) * mm, "end": v(-13.67, 24.94) * mm});
            skArc(sketch, "E203.31.0", {"start": v(-15.36, 25.78) * mm, "mid": v(-15.45, 25.64) * mm, "end": v(-15.52, 25.5) * mm});
            skArc(sketch, "E203.31.1", {"start": v(-14.81, 25.99) * mm, "mid": v(-15.12, 25.96) * mm, "end": v(-15.36, 25.78) * mm});
            skArc(sketch, "E203.31.2", {"start": v(-15.08, 24.64) * mm, "mid": v(-14.61, 24.53) * mm, "end": v(-14.15, 24.4) * mm});
            skPoint(sketch, "E203.31.3", {"position": v(-14.96, 25.25) * mm});
            skArc(sketch, "E203.31.4", {"start": v(-14.39, 25.59) * mm, "mid": v(-14.36, 25.43) * mm, "end": v(-14.36, 25.27) * mm});
            skArc(sketch, "E203.31.6", {"start": v(-14.24, 25.11) * mm, "mid": v(-14.1, 25.07) * mm, "end": v(-13.96, 25.03) * mm});
            skLineSegment(sketch, "E203.31.7", {"start": v(-14.15, 24.4) * mm, "end": v(-13.96, 25.03) * mm});
            skArc(sketch, "E203.31.8", {"start": v(-14.81, 25.99) * mm, "mid": v(-14.54, 25.85) * mm, "end": v(-14.39, 25.59) * mm});
            skPoint(sketch, "E203.31.9", {"position": v(-15.08, 24.64) * mm});
            skArc(sketch, "E203.31.10", {"start": v(-15.01, 25) * mm, "mid": v(-14.52, 24.9) * mm, "end": v(-14.04, 24.76) * mm, "construction": true});
            skArc(sketch, "E203.31.11", {"start": v(-15.08, 24.64) * mm, "mid": v(-15.56, 24.72) * mm, "end": v(-16.04, 24.78) * mm});
            skPoint(sketch, "E203.31.12", {"position": v(-15.01, 25) * mm});
            skArc(sketch, "E203.31.13", {"start": v(-15.68, 25.4) * mm, "mid": v(-15.82, 25.41) * mm, "end": v(-15.97, 25.43) * mm});
            skArc(sketch, "E203.31.14", {"start": v(-14.36, 25.27) * mm, "mid": v(-14.33, 25.17) * mm, "end": v(-14.24, 25.11) * mm});
            skArc(sketch, "E203.31.15", {"start": v(-15.52, 25.5) * mm, "mid": v(-15.58, 25.42) * mm, "end": v(-15.68, 25.4) * mm});
            skLineSegment(sketch, "E204.0", {"start": v(-27.25, 15) * mm, "end": v(-6.75, 15) * mm});
            skSolve(sketch);
        }
        {
            var Q0;
            Q0 = qSketchRegion(id + "F31", true);
            extrude(context, id + "F32", {"entities" : qUnion([Q0]), "operationType" : NewBodyOperationType.REMOVE, "endBound" : BoundingType.SYMMETRIC, "oppositeDirection" : true, "depth" : 6.5 * mm});
        }
        {
            var Q0;
            {var subQ0=sQuery(id+"F0.wireOp",EDGE,"E28");var subQ1=sQuery(id+"F0.wireOp",EDGE,"E27");var subQ2=sQuery(id+"F0.wireOp",EDGE,"E26");var subQ3=sQuery(id+"F0.wireOp",EDGE,"E24");var subQ4=sQuery(id+"F0.wireOp",EDGE,"E23");Q0=makeQuery(id+"F2.boolean.opBoolean","MERGE",FACE,{"derivedFrom":[makeQuery(id+"F1.opExtrude","CAP_FACE",FACE,{"disambiguationData":[OSD([sQuery(id+"F0.wireOp",EDGE,"E0.right"),sQuery(id+"F0.wireOp",EDGE,"E4"),sQuery(id+"F0.wireOp",EDGE,"E9"),sQuery(id+"F0.wireOp",EDGE,"E11.MirrorC"),sQuery(id+"F0.wireOp",EDGE,"E13.MirrorC"),sQuery(id+"F0.wireOp",EDGE,"E14.MirrorC"),sQuery(id+"F0.wireOp",EDGE,"E15"),sQuery(id+"F0.wireOp",EDGE,"E17.MirrorC"),sQuery(id+"F0.wireOp",EDGE,"E18.MirrorC"),sQuery(id+"F0.wireOp",EDGE,"E20.MirrorC"),sQuery(id+"F0.wireOp",EDGE,"E21"),sQuery(id+"F0.wireOp",EDGE,"E22"),subQ4,subQ3,sQuery(id+"F0.wireOp",EDGE,"E25"),subQ2,subQ1,subQ0,sQuery(id+"F0.wireOp",EDGE,"E30.0"),sQuery(id+"F0.wireOp",EDGE,"E30.1"),sQuery(id+"F0.wireOp",EDGE,"E30.2")])],"isStart":true}),makeQuery(id+"F2.opExtrude","CAP_FACE",FACE,{"disambiguationData":[OSD([subQ4,subQ3,subQ2,subQ1,subQ0,sQuery(id+"F0.wireOp",EDGE,"E31"),sQuery(id+"F0.wireOp",EDGE,"E32"),sQuery(id+"F0.wireOp",EDGE,"E33"),sQuery(id+"F0.wireOp",EDGE,"E34"),sQuery(id+"F0.wireOp",EDGE,"E35"),sQuery(id+"F0.wireOp",EDGE,"E39"),sQuery(id+"F0.wireOp",EDGE,"E41"),sQuery(id+"F0.wireOp",EDGE,"E43"),sQuery(id+"F0.wireOp",EDGE,"E44"),sQuery(id+"F0.wireOp",EDGE,"E45"),sQuery(id+"F0.wireOp",EDGE,"E46")])],"isStart":true})]});}
            var Q1;
            Q1=sQuery(id+"F10.wireOp",VERTEX,"E106.MirrorP");
            cPlane(context, id + "F33", {"entities" : qUnion([Q0, Q1]), "cplaneType" : CPlaneType.PLANE_POINT, "offset" : 150 * mm, "width" : 150 * mm, "height" : 150 * mm});
        }
        {
            var Q0;
            Q0=qCreatedBy(id+"F33.planeOp",FACE);
            var sketch = newSketch(context, id + "F34", { "sketchPlane" : qUnion([Q0])});
            skLineSegment(sketch, "E205", {"start": v(11.5, -0.3) * mm, "end": v(11.5, -1.68) * mm, "construction": true});
            skArc(sketch, "E206", {"start": v(11.5, -0.3) * mm, "mid": v(11.8, -0.38) * mm, "end": v(12, -0.6) * mm});
            skArc(sketch, "E207", {"start": v(12, -0.6) * mm, "mid": v(12.06, -0.76) * mm, "end": v(12.1, -0.92) * mm});
            skArc(sketch, "E208", {"start": v(12.1, -0.92) * mm, "mid": v(12.14, -1) * mm, "end": v(12.23, -1.05) * mm});
            skPoint(sketch, "E209", {"position": v(11.5, -1.68) * mm});
            skPoint(sketch, "E210", {"position": v(11.5, -1.05) * mm});
            skPoint(sketch, "E211", {"position": v(11.5, -1.3) * mm});
            skArc(sketch, "E212", {"start": v(11.5, -1.3) * mm, "mid": v(12, -1.31) * mm, "end": v(12.5, -1.35) * mm, "construction": true});
            skLineSegment(sketch, "E213", {"start": v(10.54, -21.28) * mm, "end": v(12.53, -1.07) * mm});
            skArc(sketch, "E214", {"start": v(12.23, -1.05) * mm, "mid": v(12.38, -1.06) * mm, "end": v(12.53, -1.07) * mm});
            skArc(sketch, "E215", {"start": v(11.5, -1.68) * mm, "mid": v(21.31, -11.98) * mm, "end": v(10.54, -21.28) * mm});
            skArc(sketch, "E216.MirrorCS", {"start": v(11.5, -0.3) * mm, "mid": v(11.2, -0.38) * mm, "end": v(11, -0.6) * mm});
            skArc(sketch, "E217.MirrorCS", {"start": v(11, -0.6) * mm, "mid": v(10.94, -0.76) * mm, "end": v(10.9, -0.92) * mm});
            skArc(sketch, "E218.MirrorCS", {"start": v(10.9, -0.92) * mm, "mid": v(10.86, -1) * mm, "end": v(10.77, -1.05) * mm});
            skArc(sketch, "E219.MirrorCS", {"start": v(10.77, -1.05) * mm, "mid": v(10.62, -1.06) * mm, "end": v(10.47, -1.07) * mm});
            skLineSegment(sketch, "E220.MirrorCS", {"start": v(12.46, -21.28) * mm, "end": v(10.47, -1.07) * mm});
            skArc(sketch, "E221.MirrorCS", {"start": v(11.5, -1.68) * mm, "mid": v(1.69, -11.98) * mm, "end": v(12.46, -21.28) * mm});
            skArc(sketch, "E222.1.0", {"start": v(8.89, -0.91) * mm, "mid": v(8.86, -1.07) * mm, "end": v(8.86, -1.23) * mm});
            skArc(sketch, "E222.1.1", {"start": v(9.31, -0.51) * mm, "mid": v(9.04, -0.65) * mm, "end": v(8.89, -0.91) * mm});
            skArc(sketch, "E222.1.2", {"start": v(9.58, -1.86) * mm, "mid": v(21.22, -10.06) * mm, "end": v(12.46, -21.28) * mm});
            skPoint(sketch, "E222.1.3", {"position": v(9.46, -1.25) * mm});
            skArc(sketch, "E222.1.4", {"start": v(9.86, -0.72) * mm, "mid": v(9.95, -0.86) * mm, "end": v(10.02, -1) * mm});
            skLineSegment(sketch, "E222.1.5", {"start": v(14.35, -20.9) * mm, "end": v(8.46, -1.47) * mm});
            skArc(sketch, "E222.1.6", {"start": v(10.18, -1.1) * mm, "mid": v(10.32, -1.09) * mm, "end": v(10.47, -1.07) * mm});
            skArc(sketch, "E222.1.8", {"start": v(9.31, -0.51) * mm, "mid": v(9.62, -0.54) * mm, "end": v(9.86, -0.72) * mm});
            skPoint(sketch, "E222.1.9", {"position": v(9.58, -1.86) * mm});
            skArc(sketch, "E222.1.10", {"start": v(9.51, -1.5) * mm, "mid": v(10, -1.41) * mm, "end": v(10.5, -1.35) * mm, "construction": true});
            skArc(sketch, "E222.1.11", {"start": v(9.58, -1.86) * mm, "mid": v(1.97, -13.89) * mm, "end": v(14.35, -20.9) * mm});
            skPoint(sketch, "E222.1.12", {"position": v(9.51, -1.5) * mm});
            skArc(sketch, "E222.1.13", {"start": v(8.74, -1.39) * mm, "mid": v(8.6, -1.43) * mm, "end": v(8.46, -1.47) * mm});
            skArc(sketch, "E222.1.14", {"start": v(10.02, -1) * mm, "mid": v(10.08, -1.08) * mm, "end": v(10.18, -1.1) * mm});
            skArc(sketch, "E222.1.15", {"start": v(8.86, -1.23) * mm, "mid": v(8.83, -1.33) * mm, "end": v(8.74, -1.39) * mm});
            skArc(sketch, "E222.2.0", {"start": v(6.87, -1.63) * mm, "mid": v(6.87, -1.79) * mm, "end": v(6.9, -1.95) * mm});
            skArc(sketch, "E222.2.1", {"start": v(7.21, -1.15) * mm, "mid": v(6.97, -1.34) * mm, "end": v(6.87, -1.63) * mm});
            skArc(sketch, "E222.2.2", {"start": v(7.74, -2.42) * mm, "mid": v(20.75, -8.2) * mm, "end": v(14.35, -20.9) * mm});
            skPoint(sketch, "E222.2.3", {"position": v(7.5, -1.84) * mm});
            skArc(sketch, "E222.2.4", {"start": v(7.8, -1.25) * mm, "mid": v(7.9, -1.36) * mm, "end": v(8, -1.5) * mm});
            skLineSegment(sketch, "E222.2.5", {"start": v(16.13, -20.16) * mm, "end": v(6.56, -2.26) * mm});
            skArc(sketch, "E222.2.6", {"start": v(8.17, -1.56) * mm, "mid": v(8.32, -1.52) * mm, "end": v(8.46, -1.47) * mm});
            skLineSegment(sketch, "E222.2.7", {"start": v(14.35, -20.9) * mm, "end": v(8.46, -1.47) * mm});
            skArc(sketch, "E222.2.8", {"start": v(7.21, -1.15) * mm, "mid": v(7.52, -1.11) * mm, "end": v(7.8, -1.25) * mm});
            skPoint(sketch, "E222.2.9", {"position": v(7.74, -2.42) * mm});
            skArc(sketch, "E222.2.10", {"start": v(7.6, -2.08) * mm, "mid": v(8.06, -1.9) * mm, "end": v(8.54, -1.74) * mm, "construction": true});
            skArc(sketch, "E222.2.11", {"start": v(7.74, -2.42) * mm, "mid": v(2.62, -15.7) * mm, "end": v(16.13, -20.16) * mm});
            skPoint(sketch, "E222.2.12", {"position": v(7.6, -2.08) * mm});
            skArc(sketch, "E222.2.13", {"start": v(6.83, -2.12) * mm, "mid": v(6.7, -2.19) * mm, "end": v(6.56, -2.26) * mm});
            skArc(sketch, "E222.2.14", {"start": v(8, -1.5) * mm, "mid": v(8.07, -1.56) * mm, "end": v(8.17, -1.56) * mm});
            skArc(sketch, "E222.2.15", {"start": v(6.9, -1.95) * mm, "mid": v(6.9, -2.05) * mm, "end": v(6.83, -2.12) * mm});
            skArc(sketch, "E222.3.0", {"start": v(5.03, -2.72) * mm, "mid": v(5.07, -2.88) * mm, "end": v(5.13, -3.03) * mm});
            skArc(sketch, "E222.3.1", {"start": v(5.28, -2.18) * mm, "mid": v(5.08, -2.42) * mm, "end": v(5.03, -2.72) * mm});
            skArc(sketch, "E222.3.2", {"start": v(6.04, -3.33) * mm, "mid": v(19.93, -6.45) * mm, "end": v(16.13, -20.16) * mm});
            skPoint(sketch, "E222.3.3", {"position": v(5.7, -2.8) * mm});
            skArc(sketch, "E222.3.4", {"start": v(5.86, -2.17) * mm, "mid": v(6, -2.26) * mm, "end": v(6.11, -2.37) * mm});
            skLineSegment(sketch, "E222.3.5", {"start": v(17.73, -19.1) * mm, "end": v(4.85, -3.4) * mm});
            skArc(sketch, "E222.3.6", {"start": v(6.3, -2.4) * mm, "mid": v(6.43, -2.33) * mm, "end": v(6.56, -2.26) * mm});
            skLineSegment(sketch, "E222.3.7", {"start": v(16.13, -20.16) * mm, "end": v(6.56, -2.26) * mm});
            skArc(sketch, "E222.3.8", {"start": v(5.28, -2.18) * mm, "mid": v(5.57, -2.1) * mm, "end": v(5.86, -2.17) * mm});
            skPoint(sketch, "E222.3.9", {"position": v(6.04, -3.33) * mm});
            skArc(sketch, "E222.3.10", {"start": v(5.83, -3.02) * mm, "mid": v(6.26, -2.75) * mm, "end": v(6.7, -2.5) * mm, "construction": true});
            skArc(sketch, "E222.3.11", {"start": v(6.04, -3.33) * mm, "mid": v(3.6, -17.35) * mm, "end": v(17.73, -19.1) * mm});
            skPoint(sketch, "E222.3.12", {"position": v(5.83, -3.02) * mm});
            skArc(sketch, "E222.3.13", {"start": v(5.09, -3.21) * mm, "mid": v(4.97, -3.3) * mm, "end": v(4.85, -3.4) * mm});
            skArc(sketch, "E222.3.14", {"start": v(6.11, -2.37) * mm, "mid": v(6.2, -2.42) * mm, "end": v(6.3, -2.4) * mm});
            skArc(sketch, "E222.3.15", {"start": v(5.13, -3.03) * mm, "mid": v(5.14, -3.13) * mm, "end": v(5.09, -3.21) * mm});
            skArc(sketch, "E222.4.0", {"start": v(3.45, -4.15) * mm, "mid": v(3.5, -4.3) * mm, "end": v(3.6, -4.43) * mm});
            skArc(sketch, "E222.4.1", {"start": v(3.58, -3.58) * mm, "mid": v(3.43, -3.85) * mm, "end": v(3.45, -4.15) * mm});
            skArc(sketch, "E222.4.2", {"start": v(4.55, -4.55) * mm, "mid": v(18.78, -4.9) * mm, "end": v(17.73, -19.1) * mm});
            skPoint(sketch, "E222.4.3", {"position": v(4.1, -4.1) * mm});
            skArc(sketch, "E222.4.4", {"start": v(4.15, -3.45) * mm, "mid": v(4.3, -3.5) * mm, "end": v(4.43, -3.6) * mm});
            skLineSegment(sketch, "E222.4.5", {"start": v(19.1, -17.73) * mm, "end": v(3.4, -4.85) * mm});
            skArc(sketch, "E222.4.6", {"start": v(4.62, -3.6) * mm, "mid": v(4.74, -3.5) * mm, "end": v(4.85, -3.4) * mm});
            skLineSegment(sketch, "E222.4.7", {"start": v(17.73, -19.1) * mm, "end": v(4.85, -3.4) * mm});
            skArc(sketch, "E222.4.8", {"start": v(3.58, -3.58) * mm, "mid": v(3.85, -3.43) * mm, "end": v(4.15, -3.45) * mm});
            skPoint(sketch, "E222.4.9", {"position": v(4.55, -4.55) * mm});
            skArc(sketch, "E222.4.10", {"start": v(4.29, -4.29) * mm, "mid": v(4.65, -3.94) * mm, "end": v(5.03, -3.62) * mm, "construction": true});
            skArc(sketch, "E222.4.11", {"start": v(4.55, -4.55) * mm, "mid": v(4.9, -18.78) * mm, "end": v(19.1, -17.73) * mm});
            skPoint(sketch, "E222.4.12", {"position": v(4.29, -4.29) * mm});
            skArc(sketch, "E222.4.13", {"start": v(3.6, -4.62) * mm, "mid": v(3.5, -4.74) * mm, "end": v(3.4, -4.85) * mm});
            skArc(sketch, "E222.4.14", {"start": v(4.43, -3.6) * mm, "mid": v(4.53, -3.63) * mm, "end": v(4.62, -3.6) * mm});
            skArc(sketch, "E222.4.15", {"start": v(3.6, -4.43) * mm, "mid": v(3.63, -4.53) * mm, "end": v(3.6, -4.62) * mm});
            skArc(sketch, "E222.5.0", {"start": v(2.17, -5.86) * mm, "mid": v(2.26, -6) * mm, "end": v(2.37, -6.11) * mm});
            skArc(sketch, "E222.5.1", {"start": v(2.18, -5.28) * mm, "mid": v(2.1, -5.57) * mm, "end": v(2.17, -5.86) * mm});
            skArc(sketch, "E222.5.2", {"start": v(3.33, -6.04) * mm, "mid": v(17.35, -3.6) * mm, "end": v(19.1, -17.73) * mm});
            skPoint(sketch, "E222.5.3", {"position": v(2.8, -5.7) * mm});
            skArc(sketch, "E222.5.4", {"start": v(2.72, -5.03) * mm, "mid": v(2.88, -5.07) * mm, "end": v(3.03, -5.13) * mm});
            skLineSegment(sketch, "E222.5.5", {"start": v(20.16, -16.13) * mm, "end": v(2.26, -6.56) * mm});
            skArc(sketch, "E222.5.6", {"start": v(3.21, -5.09) * mm, "mid": v(3.3, -4.97) * mm, "end": v(3.4, -4.85) * mm});
            skLineSegment(sketch, "E222.5.7", {"start": v(19.1, -17.73) * mm, "end": v(3.4, -4.85) * mm});
            skArc(sketch, "E222.5.8", {"start": v(2.18, -5.28) * mm, "mid": v(2.42, -5.08) * mm, "end": v(2.72, -5.03) * mm});
            skPoint(sketch, "E222.5.9", {"position": v(3.33, -6.04) * mm});
            skArc(sketch, "E222.5.10", {"start": v(3.02, -5.83) * mm, "mid": v(3.3, -5.42) * mm, "end": v(3.62, -5.03) * mm, "construction": true});
            skArc(sketch, "E222.5.11", {"start": v(3.33, -6.04) * mm, "mid": v(6.45, -19.93) * mm, "end": v(20.16, -16.13) * mm});
            skPoint(sketch, "E222.5.12", {"position": v(3.02, -5.83) * mm});
            skArc(sketch, "E222.5.13", {"start": v(2.4, -6.3) * mm, "mid": v(2.33, -6.43) * mm, "end": v(2.26, -6.56) * mm});
            skArc(sketch, "E222.5.14", {"start": v(3.03, -5.13) * mm, "mid": v(3.13, -5.14) * mm, "end": v(3.21, -5.09) * mm});
            skArc(sketch, "E222.5.15", {"start": v(2.37, -6.11) * mm, "mid": v(2.42, -6.2) * mm, "end": v(2.4, -6.3) * mm});
            skArc(sketch, "E222.6.0", {"start": v(1.25, -7.8) * mm, "mid": v(1.36, -7.9) * mm, "end": v(1.5, -8) * mm});
            skArc(sketch, "E222.6.1", {"start": v(1.15, -7.21) * mm, "mid": v(1.11, -7.52) * mm, "end": v(1.25, -7.8) * mm});
            skArc(sketch, "E222.6.2", {"start": v(2.42, -7.74) * mm, "mid": v(15.7, -2.62) * mm, "end": v(20.16, -16.13) * mm});
            skPoint(sketch, "E222.6.3", {"position": v(1.84, -7.5) * mm});
            skArc(sketch, "E222.6.4", {"start": v(1.63, -6.87) * mm, "mid": v(1.79, -6.87) * mm, "end": v(1.95, -6.9) * mm});
            skLineSegment(sketch, "E222.6.5", {"start": v(20.9, -14.35) * mm, "end": v(1.47, -8.46) * mm});
            skArc(sketch, "E222.6.6", {"start": v(2.12, -6.83) * mm, "mid": v(2.19, -6.7) * mm, "end": v(2.26, -6.56) * mm});
            skLineSegment(sketch, "E222.6.7", {"start": v(20.16, -16.13) * mm, "end": v(2.26, -6.56) * mm});
            skArc(sketch, "E222.6.8", {"start": v(1.15, -7.21) * mm, "mid": v(1.34, -6.97) * mm, "end": v(1.63, -6.87) * mm});
            skPoint(sketch, "E222.6.9", {"position": v(2.42, -7.74) * mm});
            skArc(sketch, "E222.6.10", {"start": v(2.08, -7.6) * mm, "mid": v(2.28, -7.14) * mm, "end": v(2.5, -6.7) * mm, "construction": true});
            skArc(sketch, "E222.6.11", {"start": v(2.42, -7.74) * mm, "mid": v(8.2, -20.75) * mm, "end": v(20.9, -14.35) * mm});
            skPoint(sketch, "E222.6.12", {"position": v(2.08, -7.6) * mm});
            skArc(sketch, "E222.6.13", {"start": v(1.56, -8.17) * mm, "mid": v(1.52, -8.32) * mm, "end": v(1.47, -8.46) * mm});
            skArc(sketch, "E222.6.14", {"start": v(1.95, -6.9) * mm, "mid": v(2.05, -6.9) * mm, "end": v(2.12, -6.83) * mm});
            skArc(sketch, "E222.6.15", {"start": v(1.5, -8) * mm, "mid": v(1.56, -8.07) * mm, "end": v(1.56, -8.17) * mm});
            skArc(sketch, "E222.7.0", {"start": v(0.72, -9.86) * mm, "mid": v(0.86, -9.95) * mm, "end": v(1, -10.02) * mm});
            skArc(sketch, "E222.7.1", {"start": v(0.51, -9.31) * mm, "mid": v(0.54, -9.62) * mm, "end": v(0.72, -9.86) * mm});
            skArc(sketch, "E222.7.2", {"start": v(1.86, -9.58) * mm, "mid": v(13.89, -1.97) * mm, "end": v(20.9, -14.35) * mm});
            skPoint(sketch, "E222.7.3", {"position": v(1.25, -9.46) * mm});
            skArc(sketch, "E222.7.4", {"start": v(0.91, -8.89) * mm, "mid": v(1.07, -8.86) * mm, "end": v(1.23, -8.86) * mm});
            skLineSegment(sketch, "E222.7.5", {"start": v(21.28, -12.46) * mm, "end": v(1.07, -10.47) * mm});
            skArc(sketch, "E222.7.6", {"start": v(1.39, -8.74) * mm, "mid": v(1.43, -8.6) * mm, "end": v(1.47, -8.46) * mm});
            skLineSegment(sketch, "E222.7.7", {"start": v(20.9, -14.35) * mm, "end": v(1.47, -8.46) * mm});
            skArc(sketch, "E222.7.8", {"start": v(0.51, -9.31) * mm, "mid": v(0.65, -9.04) * mm, "end": v(0.91, -8.89) * mm});
            skPoint(sketch, "E222.7.9", {"position": v(1.86, -9.58) * mm});
            skArc(sketch, "E222.7.10", {"start": v(1.5, -9.51) * mm, "mid": v(1.6, -9.02) * mm, "end": v(1.74, -8.54) * mm, "construction": true});
            skArc(sketch, "E222.7.11", {"start": v(1.86, -9.58) * mm, "mid": v(10.06, -21.22) * mm, "end": v(21.28, -12.46) * mm});
            skPoint(sketch, "E222.7.12", {"position": v(1.5, -9.51) * mm});
            skArc(sketch, "E222.7.13", {"start": v(1.1, -10.18) * mm, "mid": v(1.09, -10.32) * mm, "end": v(1.07, -10.47) * mm});
            skArc(sketch, "E222.7.14", {"start": v(1.23, -8.86) * mm, "mid": v(1.33, -8.83) * mm, "end": v(1.39, -8.74) * mm});
            skArc(sketch, "E222.7.15", {"start": v(1, -10.02) * mm, "mid": v(1.08, -10.08) * mm, "end": v(1.1, -10.18) * mm});
            skArc(sketch, "E222.8.0", {"start": v(0.6, -12) * mm, "mid": v(0.76, -12.06) * mm, "end": v(0.92, -12.1) * mm});
            skArc(sketch, "E222.8.1", {"start": v(0.3, -11.5) * mm, "mid": v(0.38, -11.8) * mm, "end": v(0.6, -12) * mm});
            skArc(sketch, "E222.8.2", {"start": v(1.68, -11.5) * mm, "mid": v(11.98, -1.69) * mm, "end": v(21.28, -12.46) * mm});
            skPoint(sketch, "E222.8.3", {"position": v(1.05, -11.5) * mm});
            skArc(sketch, "E222.8.4", {"start": v(0.6, -11) * mm, "mid": v(0.76, -10.94) * mm, "end": v(0.92, -10.9) * mm});
            skLineSegment(sketch, "E222.8.5", {"start": v(21.28, -10.54) * mm, "end": v(1.07, -12.53) * mm});
            skArc(sketch, "E222.8.6", {"start": v(1.05, -10.77) * mm, "mid": v(1.06, -10.62) * mm, "end": v(1.07, -10.47) * mm});
            skLineSegment(sketch, "E222.8.7", {"start": v(21.28, -12.46) * mm, "end": v(1.07, -10.47) * mm});
            skArc(sketch, "E222.8.8", {"start": v(0.3, -11.5) * mm, "mid": v(0.38, -11.2) * mm, "end": v(0.6, -11) * mm});
            skPoint(sketch, "E222.8.9", {"position": v(1.68, -11.5) * mm});
            skArc(sketch, "E222.8.10", {"start": v(1.3, -11.5) * mm, "mid": v(1.31, -11) * mm, "end": v(1.35, -10.5) * mm, "construction": true});
            skArc(sketch, "E222.8.11", {"start": v(1.68, -11.5) * mm, "mid": v(11.98, -21.31) * mm, "end": v(21.28, -10.54) * mm});
            skPoint(sketch, "E222.8.12", {"position": v(1.3, -11.5) * mm});
            skArc(sketch, "E222.8.13", {"start": v(1.05, -12.23) * mm, "mid": v(1.06, -12.38) * mm, "end": v(1.07, -12.53) * mm});
            skArc(sketch, "E222.8.14", {"start": v(0.92, -10.9) * mm, "mid": v(1, -10.86) * mm, "end": v(1.05, -10.77) * mm});
            skArc(sketch, "E222.8.15", {"start": v(0.92, -12.1) * mm, "mid": v(1, -12.14) * mm, "end": v(1.05, -12.23) * mm});
            skArc(sketch, "E222.9.0", {"start": v(0.91, -14.11) * mm, "mid": v(1.07, -14.14) * mm, "end": v(1.23, -14.14) * mm});
            skArc(sketch, "E222.9.1", {"start": v(0.51, -13.69) * mm, "mid": v(0.65, -13.96) * mm, "end": v(0.91, -14.11) * mm});
            skArc(sketch, "E222.9.2", {"start": v(1.86, -13.42) * mm, "mid": v(10.06, -1.78) * mm, "end": v(21.28, -10.54) * mm});
            skPoint(sketch, "E222.9.3", {"position": v(1.25, -13.54) * mm});
            skArc(sketch, "E222.9.4", {"start": v(0.72, -13.14) * mm, "mid": v(0.86, -13.05) * mm, "end": v(1, -12.98) * mm});
            skLineSegment(sketch, "E222.9.5", {"start": v(20.9, -8.65) * mm, "end": v(1.47, -14.54) * mm});
            skArc(sketch, "E222.9.6", {"start": v(1.1, -12.82) * mm, "mid": v(1.09, -12.68) * mm, "end": v(1.07, -12.53) * mm});
            skLineSegment(sketch, "E222.9.7", {"start": v(21.28, -10.54) * mm, "end": v(1.07, -12.53) * mm});
            skArc(sketch, "E222.9.8", {"start": v(0.51, -13.69) * mm, "mid": v(0.54, -13.38) * mm, "end": v(0.72, -13.14) * mm});
            skPoint(sketch, "E222.9.9", {"position": v(1.86, -13.42) * mm});
            skArc(sketch, "E222.9.10", {"start": v(1.5, -13.49) * mm, "mid": v(1.41, -13) * mm, "end": v(1.35, -12.5) * mm, "construction": true});
            skArc(sketch, "E222.9.11", {"start": v(1.86, -13.42) * mm, "mid": v(13.89, -21.03) * mm, "end": v(20.9, -8.65) * mm});
            skPoint(sketch, "E222.9.12", {"position": v(1.5, -13.49) * mm});
            skArc(sketch, "E222.9.13", {"start": v(1.39, -14.26) * mm, "mid": v(1.43, -14.4) * mm, "end": v(1.47, -14.54) * mm});
            skArc(sketch, "E222.9.14", {"start": v(1, -12.98) * mm, "mid": v(1.08, -12.92) * mm, "end": v(1.1, -12.82) * mm});
            skArc(sketch, "E222.9.15", {"start": v(1.23, -14.14) * mm, "mid": v(1.33, -14.17) * mm, "end": v(1.39, -14.26) * mm});
            skArc(sketch, "E222.10.0", {"start": v(1.63, -16.13) * mm, "mid": v(1.79, -16.13) * mm, "end": v(1.95, -16.1) * mm});
            skArc(sketch, "E222.10.1", {"start": v(1.15, -15.79) * mm, "mid": v(1.34, -16.03) * mm, "end": v(1.63, -16.13) * mm});
            skArc(sketch, "E222.10.2", {"start": v(2.42, -15.26) * mm, "mid": v(8.2, -2.25) * mm, "end": v(20.9, -8.65) * mm});
            skPoint(sketch, "E222.10.3", {"position": v(1.84, -15.5) * mm});
            skArc(sketch, "E222.10.4", {"start": v(1.25, -15.2) * mm, "mid": v(1.36, -15.1) * mm, "end": v(1.5, -15) * mm});
            skLineSegment(sketch, "E222.10.5", {"start": v(20.16, -6.87) * mm, "end": v(2.26, -16.44) * mm});
            skArc(sketch, "E222.10.6", {"start": v(1.56, -14.83) * mm, "mid": v(1.52, -14.68) * mm, "end": v(1.47, -14.54) * mm});
            skLineSegment(sketch, "E222.10.7", {"start": v(20.9, -8.65) * mm, "end": v(1.47, -14.54) * mm});
            skArc(sketch, "E222.10.8", {"start": v(1.15, -15.79) * mm, "mid": v(1.11, -15.48) * mm, "end": v(1.25, -15.2) * mm});
            skPoint(sketch, "E222.10.9", {"position": v(2.42, -15.26) * mm});
            skArc(sketch, "E222.10.10", {"start": v(2.08, -15.4) * mm, "mid": v(1.9, -14.94) * mm, "end": v(1.74, -14.46) * mm, "construction": true});
            skArc(sketch, "E222.10.11", {"start": v(2.42, -15.26) * mm, "mid": v(15.7, -20.38) * mm, "end": v(20.16, -6.87) * mm});
            skPoint(sketch, "E222.10.12", {"position": v(2.08, -15.4) * mm});
            skArc(sketch, "E222.10.13", {"start": v(2.12, -16.17) * mm, "mid": v(2.19, -16.3) * mm, "end": v(2.26, -16.44) * mm});
            skArc(sketch, "E222.10.14", {"start": v(1.5, -15) * mm, "mid": v(1.56, -14.93) * mm, "end": v(1.56, -14.83) * mm});
            skArc(sketch, "E222.10.15", {"start": v(1.95, -16.1) * mm, "mid": v(2.05, -16.1) * mm, "end": v(2.12, -16.17) * mm});
            skArc(sketch, "E222.11.0", {"start": v(2.72, -17.97) * mm, "mid": v(2.88, -17.93) * mm, "end": v(3.03, -17.87) * mm});
            skArc(sketch, "E222.11.1", {"start": v(2.18, -17.72) * mm, "mid": v(2.42, -17.92) * mm, "end": v(2.72, -17.97) * mm});
            skArc(sketch, "E222.11.2", {"start": v(3.33, -16.96) * mm, "mid": v(6.45, -3.07) * mm, "end": v(20.16, -6.87) * mm});
            skPoint(sketch, "E222.11.3", {"position": v(2.8, -17.3) * mm});
            skArc(sketch, "E222.11.4", {"start": v(2.17, -17.14) * mm, "mid": v(2.26, -17) * mm, "end": v(2.37, -16.89) * mm});
            skLineSegment(sketch, "E222.11.5", {"start": v(19.1, -5.27) * mm, "end": v(3.4, -18.15) * mm});
            skArc(sketch, "E222.11.6", {"start": v(2.4, -16.7) * mm, "mid": v(2.33, -16.57) * mm, "end": v(2.26, -16.44) * mm});
            skLineSegment(sketch, "E222.11.7", {"start": v(20.16, -6.87) * mm, "end": v(2.26, -16.44) * mm});
            skArc(sketch, "E222.11.8", {"start": v(2.18, -17.72) * mm, "mid": v(2.1, -17.43) * mm, "end": v(2.17, -17.14) * mm});
            skPoint(sketch, "E222.11.9", {"position": v(3.33, -16.96) * mm});
            skArc(sketch, "E222.11.10", {"start": v(3.02, -17.17) * mm, "mid": v(2.75, -16.74) * mm, "end": v(2.5, -16.3) * mm, "construction": true});
            skArc(sketch, "E222.11.11", {"start": v(3.33, -16.96) * mm, "mid": v(17.35, -19.4) * mm, "end": v(19.1, -5.27) * mm});
            skPoint(sketch, "E222.11.12", {"position": v(3.02, -17.17) * mm});
            skArc(sketch, "E222.11.13", {"start": v(3.21, -17.91) * mm, "mid": v(3.3, -18.03) * mm, "end": v(3.4, -18.15) * mm});
            skArc(sketch, "E222.11.14", {"start": v(2.37, -16.89) * mm, "mid": v(2.42, -16.8) * mm, "end": v(2.4, -16.7) * mm});
            skArc(sketch, "E222.11.15", {"start": v(3.03, -17.87) * mm, "mid": v(3.13, -17.86) * mm, "end": v(3.21, -17.91) * mm});
            skArc(sketch, "E222.12.0", {"start": v(4.15, -19.55) * mm, "mid": v(4.3, -19.5) * mm, "end": v(4.43, -19.4) * mm});
            skArc(sketch, "E222.12.1", {"start": v(3.58, -19.42) * mm, "mid": v(3.85, -19.57) * mm, "end": v(4.15, -19.55) * mm});
            skArc(sketch, "E222.12.2", {"start": v(4.55, -18.45) * mm, "mid": v(4.9, -4.22) * mm, "end": v(19.1, -5.27) * mm});
            skPoint(sketch, "E222.12.3", {"position": v(4.1, -18.9) * mm});
            skArc(sketch, "E222.12.4", {"start": v(3.45, -18.85) * mm, "mid": v(3.5, -18.7) * mm, "end": v(3.6, -18.57) * mm});
            skLineSegment(sketch, "E222.12.5", {"start": v(17.73, -3.9) * mm, "end": v(4.85, -19.6) * mm});
            skArc(sketch, "E222.12.6", {"start": v(3.6, -18.38) * mm, "mid": v(3.5, -18.26) * mm, "end": v(3.4, -18.15) * mm});
            skLineSegment(sketch, "E222.12.7", {"start": v(19.1, -5.27) * mm, "end": v(3.4, -18.15) * mm});
            skArc(sketch, "E222.12.8", {"start": v(3.58, -19.42) * mm, "mid": v(3.43, -19.15) * mm, "end": v(3.45, -18.85) * mm});
            skPoint(sketch, "E222.12.9", {"position": v(4.55, -18.45) * mm});
            skArc(sketch, "E222.12.10", {"start": v(4.29, -18.71) * mm, "mid": v(3.94, -18.35) * mm, "end": v(3.62, -17.97) * mm, "construction": true});
            skArc(sketch, "E222.12.11", {"start": v(4.55, -18.45) * mm, "mid": v(18.78, -18.1) * mm, "end": v(17.73, -3.9) * mm});
            skPoint(sketch, "E222.12.12", {"position": v(4.29, -18.71) * mm});
            skArc(sketch, "E222.12.13", {"start": v(4.62, -19.4) * mm, "mid": v(4.74, -19.5) * mm, "end": v(4.85, -19.6) * mm});
            skArc(sketch, "E222.12.14", {"start": v(3.6, -18.57) * mm, "mid": v(3.63, -18.47) * mm, "end": v(3.6, -18.38) * mm});
            skArc(sketch, "E222.12.15", {"start": v(4.43, -19.4) * mm, "mid": v(4.53, -19.37) * mm, "end": v(4.62, -19.4) * mm});
            skArc(sketch, "E222.13.0", {"start": v(5.86, -20.83) * mm, "mid": v(6, -20.74) * mm, "end": v(6.11, -20.63) * mm});
            skArc(sketch, "E222.13.1", {"start": v(5.28, -20.82) * mm, "mid": v(5.57, -20.9) * mm, "end": v(5.86, -20.83) * mm});
            skArc(sketch, "E222.13.2", {"start": v(6.04, -19.67) * mm, "mid": v(3.6, -5.65) * mm, "end": v(17.73, -3.9) * mm});
            skPoint(sketch, "E222.13.3", {"position": v(5.7, -20.2) * mm});
            skArc(sketch, "E222.13.4", {"start": v(5.03, -20.28) * mm, "mid": v(5.07, -20.12) * mm, "end": v(5.13, -19.97) * mm});
            skLineSegment(sketch, "E222.13.5", {"start": v(16.13, -2.84) * mm, "end": v(6.56, -20.74) * mm});
            skArc(sketch, "E222.13.6", {"start": v(5.09, -19.79) * mm, "mid": v(4.97, -19.7) * mm, "end": v(4.85, -19.6) * mm});
            skLineSegment(sketch, "E222.13.7", {"start": v(17.73, -3.9) * mm, "end": v(4.85, -19.6) * mm});
            skArc(sketch, "E222.13.8", {"start": v(5.28, -20.82) * mm, "mid": v(5.08, -20.58) * mm, "end": v(5.03, -20.28) * mm});
            skPoint(sketch, "E222.13.9", {"position": v(6.04, -19.67) * mm});
            skArc(sketch, "E222.13.10", {"start": v(5.83, -19.98) * mm, "mid": v(5.42, -19.7) * mm, "end": v(5.03, -19.38) * mm, "construction": true});
            skArc(sketch, "E222.13.11", {"start": v(6.04, -19.67) * mm, "mid": v(19.93, -16.55) * mm, "end": v(16.13, -2.84) * mm});
            skPoint(sketch, "E222.13.12", {"position": v(5.83, -19.98) * mm});
            skArc(sketch, "E222.13.13", {"start": v(6.3, -20.6) * mm, "mid": v(6.43, -20.67) * mm, "end": v(6.56, -20.74) * mm});
            skArc(sketch, "E222.13.14", {"start": v(5.13, -19.97) * mm, "mid": v(5.14, -19.87) * mm, "end": v(5.09, -19.79) * mm});
            skArc(sketch, "E222.13.15", {"start": v(6.11, -20.63) * mm, "mid": v(6.2, -20.58) * mm, "end": v(6.3, -20.6) * mm});
            skArc(sketch, "E222.14.0", {"start": v(7.8, -21.75) * mm, "mid": v(7.9, -21.64) * mm, "end": v(8, -21.5) * mm});
            skArc(sketch, "E222.14.1", {"start": v(7.21, -21.85) * mm, "mid": v(7.52, -21.89) * mm, "end": v(7.8, -21.75) * mm});
            skArc(sketch, "E222.14.2", {"start": v(7.74, -20.58) * mm, "mid": v(2.62, -7.3) * mm, "end": v(16.13, -2.84) * mm});
            skPoint(sketch, "E222.14.3", {"position": v(7.5, -21.16) * mm});
            skArc(sketch, "E222.14.4", {"start": v(6.87, -21.37) * mm, "mid": v(6.87, -21.21) * mm, "end": v(6.9, -21.05) * mm});
            skLineSegment(sketch, "E222.14.5", {"start": v(14.35, -2.1) * mm, "end": v(8.46, -21.53) * mm});
            skArc(sketch, "E222.14.6", {"start": v(6.83, -20.88) * mm, "mid": v(6.7, -20.81) * mm, "end": v(6.56, -20.74) * mm});
            skLineSegment(sketch, "E222.14.7", {"start": v(16.13, -2.84) * mm, "end": v(6.56, -20.74) * mm});
            skArc(sketch, "E222.14.8", {"start": v(7.21, -21.85) * mm, "mid": v(6.97, -21.66) * mm, "end": v(6.87, -21.37) * mm});
            skPoint(sketch, "E222.14.9", {"position": v(7.74, -20.58) * mm});
            skArc(sketch, "E222.14.10", {"start": v(7.6, -20.92) * mm, "mid": v(7.14, -20.72) * mm, "end": v(6.7, -20.5) * mm, "construction": true});
            skArc(sketch, "E222.14.11", {"start": v(7.74, -20.58) * mm, "mid": v(20.75, -14.8) * mm, "end": v(14.35, -2.1) * mm});
            skPoint(sketch, "E222.14.12", {"position": v(7.6, -20.92) * mm});
            skArc(sketch, "E222.14.13", {"start": v(8.17, -21.44) * mm, "mid": v(8.32, -21.48) * mm, "end": v(8.46, -21.53) * mm});
            skArc(sketch, "E222.14.14", {"start": v(6.9, -21.05) * mm, "mid": v(6.9, -20.95) * mm, "end": v(6.83, -20.88) * mm});
            skArc(sketch, "E222.14.15", {"start": v(8, -21.5) * mm, "mid": v(8.07, -21.44) * mm, "end": v(8.17, -21.44) * mm});
            skArc(sketch, "E222.15.0", {"start": v(9.86, -22.28) * mm, "mid": v(9.95, -22.14) * mm, "end": v(10.02, -22) * mm});
            skArc(sketch, "E222.15.1", {"start": v(9.31, -22.49) * mm, "mid": v(9.62, -22.46) * mm, "end": v(9.86, -22.28) * mm});
            skArc(sketch, "E222.15.2", {"start": v(9.58, -21.14) * mm, "mid": v(1.97, -9.11) * mm, "end": v(14.35, -2.1) * mm});
            skPoint(sketch, "E222.15.3", {"position": v(9.46, -21.75) * mm});
            skArc(sketch, "E222.15.4", {"start": v(8.89, -22.09) * mm, "mid": v(8.86, -21.93) * mm, "end": v(8.86, -21.77) * mm});
            skLineSegment(sketch, "E222.15.5", {"start": v(12.46, -1.72) * mm, "end": v(10.47, -21.93) * mm});
            skArc(sketch, "E222.15.6", {"start": v(8.74, -21.61) * mm, "mid": v(8.6, -21.57) * mm, "end": v(8.46, -21.53) * mm});
            skLineSegment(sketch, "E222.15.7", {"start": v(14.35, -2.1) * mm, "end": v(8.46, -21.53) * mm});
            skArc(sketch, "E222.15.8", {"start": v(9.31, -22.49) * mm, "mid": v(9.04, -22.35) * mm, "end": v(8.89, -22.09) * mm});
            skPoint(sketch, "E222.15.9", {"position": v(9.58, -21.14) * mm});
            skArc(sketch, "E222.15.10", {"start": v(9.51, -21.5) * mm, "mid": v(9.02, -21.4) * mm, "end": v(8.54, -21.26) * mm, "construction": true});
            skArc(sketch, "E222.15.11", {"start": v(9.58, -21.14) * mm, "mid": v(21.22, -12.94) * mm, "end": v(12.46, -1.72) * mm});
            skPoint(sketch, "E222.15.12", {"position": v(9.51, -21.5) * mm});
            skArc(sketch, "E222.15.13", {"start": v(10.18, -21.9) * mm, "mid": v(10.32, -21.91) * mm, "end": v(10.47, -21.93) * mm});
            skArc(sketch, "E222.15.14", {"start": v(8.86, -21.77) * mm, "mid": v(8.83, -21.67) * mm, "end": v(8.74, -21.61) * mm});
            skArc(sketch, "E222.15.15", {"start": v(10.02, -22) * mm, "mid": v(10.08, -21.92) * mm, "end": v(10.18, -21.9) * mm});
            skArc(sketch, "E222.16.0", {"start": v(12, -22.4) * mm, "mid": v(12.06, -22.24) * mm, "end": v(12.1, -22.08) * mm});
            skArc(sketch, "E222.16.1", {"start": v(11.5, -22.7) * mm, "mid": v(11.8, -22.62) * mm, "end": v(12, -22.4) * mm});
            skArc(sketch, "E222.16.2", {"start": v(11.5, -21.32) * mm, "mid": v(1.69, -11.02) * mm, "end": v(12.46, -1.72) * mm});
            skPoint(sketch, "E222.16.3", {"position": v(11.5, -21.95) * mm});
            skArc(sketch, "E222.16.4", {"start": v(11, -22.4) * mm, "mid": v(10.94, -22.24) * mm, "end": v(10.9, -22.08) * mm});
            skLineSegment(sketch, "E222.16.5", {"start": v(10.54, -1.72) * mm, "end": v(12.53, -21.93) * mm});
            skArc(sketch, "E222.16.6", {"start": v(10.77, -21.95) * mm, "mid": v(10.62, -21.94) * mm, "end": v(10.47, -21.93) * mm});
            skLineSegment(sketch, "E222.16.7", {"start": v(12.46, -1.72) * mm, "end": v(10.47, -21.93) * mm});
            skArc(sketch, "E222.16.8", {"start": v(11.5, -22.7) * mm, "mid": v(11.2, -22.62) * mm, "end": v(11, -22.4) * mm});
            skPoint(sketch, "E222.16.9", {"position": v(11.5, -21.32) * mm});
            skArc(sketch, "E222.16.10", {"start": v(11.5, -21.7) * mm, "mid": v(11, -21.69) * mm, "end": v(10.5, -21.65) * mm, "construction": true});
            skArc(sketch, "E222.16.11", {"start": v(11.5, -21.32) * mm, "mid": v(21.31, -11.02) * mm, "end": v(10.54, -1.72) * mm});
            skPoint(sketch, "E222.16.12", {"position": v(11.5, -21.7) * mm});
            skArc(sketch, "E222.16.13", {"start": v(12.23, -21.95) * mm, "mid": v(12.38, -21.94) * mm, "end": v(12.53, -21.93) * mm});
            skArc(sketch, "E222.16.14", {"start": v(10.9, -22.08) * mm, "mid": v(10.86, -22) * mm, "end": v(10.77, -21.95) * mm});
            skArc(sketch, "E222.16.15", {"start": v(12.1, -22.08) * mm, "mid": v(12.14, -22) * mm, "end": v(12.23, -21.95) * mm});
            skArc(sketch, "E222.17.0", {"start": v(14.11, -22.09) * mm, "mid": v(14.14, -21.93) * mm, "end": v(14.14, -21.77) * mm});
            skArc(sketch, "E222.17.1", {"start": v(13.69, -22.49) * mm, "mid": v(13.96, -22.35) * mm, "end": v(14.11, -22.09) * mm});
            skArc(sketch, "E222.17.2", {"start": v(13.42, -21.14) * mm, "mid": v(1.78, -12.94) * mm, "end": v(10.54, -1.72) * mm});
            skPoint(sketch, "E222.17.3", {"position": v(13.54, -21.75) * mm});
            skArc(sketch, "E222.17.4", {"start": v(13.14, -22.28) * mm, "mid": v(13.05, -22.14) * mm, "end": v(12.98, -22) * mm});
            skLineSegment(sketch, "E222.17.5", {"start": v(8.65, -2.1) * mm, "end": v(14.54, -21.53) * mm});
            skArc(sketch, "E222.17.6", {"start": v(12.82, -21.9) * mm, "mid": v(12.68, -21.91) * mm, "end": v(12.53, -21.93) * mm});
            skLineSegment(sketch, "E222.17.7", {"start": v(10.54, -1.72) * mm, "end": v(12.53, -21.93) * mm});
            skArc(sketch, "E222.17.8", {"start": v(13.69, -22.49) * mm, "mid": v(13.38, -22.46) * mm, "end": v(13.14, -22.28) * mm});
            skPoint(sketch, "E222.17.9", {"position": v(13.42, -21.14) * mm});
            skArc(sketch, "E222.17.10", {"start": v(13.49, -21.5) * mm, "mid": v(13, -21.59) * mm, "end": v(12.5, -21.65) * mm, "construction": true});
            skArc(sketch, "E222.17.11", {"start": v(13.42, -21.14) * mm, "mid": v(21.03, -9.11) * mm, "end": v(8.65, -2.1) * mm});
            skPoint(sketch, "E222.17.12", {"position": v(13.49, -21.5) * mm});
            skArc(sketch, "E222.17.13", {"start": v(14.26, -21.61) * mm, "mid": v(14.4, -21.57) * mm, "end": v(14.54, -21.53) * mm});
            skArc(sketch, "E222.17.14", {"start": v(12.98, -22) * mm, "mid": v(12.92, -21.92) * mm, "end": v(12.82, -21.9) * mm});
            skArc(sketch, "E222.17.15", {"start": v(14.14, -21.77) * mm, "mid": v(14.17, -21.67) * mm, "end": v(14.26, -21.61) * mm});
            skArc(sketch, "E222.18.0", {"start": v(16.13, -21.37) * mm, "mid": v(16.13, -21.21) * mm, "end": v(16.1, -21.05) * mm});
            skArc(sketch, "E222.18.1", {"start": v(15.79, -21.85) * mm, "mid": v(16.03, -21.66) * mm, "end": v(16.13, -21.37) * mm});
            skArc(sketch, "E222.18.2", {"start": v(15.26, -20.58) * mm, "mid": v(2.25, -14.8) * mm, "end": v(8.65, -2.1) * mm});
            skPoint(sketch, "E222.18.3", {"position": v(15.5, -21.16) * mm});
            skArc(sketch, "E222.18.4", {"start": v(15.2, -21.75) * mm, "mid": v(15.1, -21.64) * mm, "end": v(15, -21.5) * mm});
            skLineSegment(sketch, "E222.18.5", {"start": v(6.87, -2.84) * mm, "end": v(16.44, -20.74) * mm});
            skArc(sketch, "E222.18.6", {"start": v(14.83, -21.44) * mm, "mid": v(14.68, -21.48) * mm, "end": v(14.54, -21.53) * mm});
            skLineSegment(sketch, "E222.18.7", {"start": v(8.65, -2.1) * mm, "end": v(14.54, -21.53) * mm});
            skArc(sketch, "E222.18.8", {"start": v(15.79, -21.85) * mm, "mid": v(15.48, -21.89) * mm, "end": v(15.2, -21.75) * mm});
            skPoint(sketch, "E222.18.9", {"position": v(15.26, -20.58) * mm});
            skArc(sketch, "E222.18.10", {"start": v(15.4, -20.92) * mm, "mid": v(14.94, -21.1) * mm, "end": v(14.46, -21.26) * mm, "construction": true});
            skArc(sketch, "E222.18.11", {"start": v(15.26, -20.58) * mm, "mid": v(20.38, -7.3) * mm, "end": v(6.87, -2.84) * mm});
            skPoint(sketch, "E222.18.12", {"position": v(15.4, -20.92) * mm});
            skArc(sketch, "E222.18.13", {"start": v(16.17, -20.88) * mm, "mid": v(16.3, -20.81) * mm, "end": v(16.44, -20.74) * mm});
            skArc(sketch, "E222.18.14", {"start": v(15, -21.5) * mm, "mid": v(14.93, -21.44) * mm, "end": v(14.83, -21.44) * mm});
            skArc(sketch, "E222.18.15", {"start": v(16.1, -21.05) * mm, "mid": v(16.1, -20.95) * mm, "end": v(16.17, -20.88) * mm});
            skArc(sketch, "E222.19.0", {"start": v(17.97, -20.28) * mm, "mid": v(17.93, -20.12) * mm, "end": v(17.87, -19.97) * mm});
            skArc(sketch, "E222.19.1", {"start": v(17.72, -20.82) * mm, "mid": v(17.92, -20.58) * mm, "end": v(17.97, -20.28) * mm});
            skArc(sketch, "E222.19.2", {"start": v(16.96, -19.67) * mm, "mid": v(3.07, -16.55) * mm, "end": v(6.87, -2.84) * mm});
            skPoint(sketch, "E222.19.3", {"position": v(17.3, -20.2) * mm});
            skArc(sketch, "E222.19.4", {"start": v(17.14, -20.83) * mm, "mid": v(17, -20.74) * mm, "end": v(16.89, -20.63) * mm});
            skLineSegment(sketch, "E222.19.5", {"start": v(5.27, -3.9) * mm, "end": v(18.15, -19.6) * mm});
            skArc(sketch, "E222.19.6", {"start": v(16.7, -20.6) * mm, "mid": v(16.57, -20.67) * mm, "end": v(16.44, -20.74) * mm});
            skLineSegment(sketch, "E222.19.7", {"start": v(6.87, -2.84) * mm, "end": v(16.44, -20.74) * mm});
            skArc(sketch, "E222.19.8", {"start": v(17.72, -20.82) * mm, "mid": v(17.43, -20.9) * mm, "end": v(17.14, -20.83) * mm});
            skPoint(sketch, "E222.19.9", {"position": v(16.96, -19.67) * mm});
            skArc(sketch, "E222.19.10", {"start": v(17.17, -19.98) * mm, "mid": v(16.74, -20.25) * mm, "end": v(16.3, -20.5) * mm, "construction": true});
            skArc(sketch, "E222.19.11", {"start": v(16.96, -19.67) * mm, "mid": v(19.4, -5.65) * mm, "end": v(5.27, -3.9) * mm});
            skPoint(sketch, "E222.19.12", {"position": v(17.17, -19.98) * mm});
            skArc(sketch, "E222.19.13", {"start": v(17.91, -19.79) * mm, "mid": v(18.03, -19.7) * mm, "end": v(18.15, -19.6) * mm});
            skArc(sketch, "E222.19.14", {"start": v(16.89, -20.63) * mm, "mid": v(16.8, -20.58) * mm, "end": v(16.7, -20.6) * mm});
            skArc(sketch, "E222.19.15", {"start": v(17.87, -19.97) * mm, "mid": v(17.86, -19.87) * mm, "end": v(17.91, -19.79) * mm});
            skArc(sketch, "E222.20.0", {"start": v(19.55, -18.85) * mm, "mid": v(19.5, -18.7) * mm, "end": v(19.4, -18.57) * mm});
            skArc(sketch, "E222.20.1", {"start": v(19.42, -19.42) * mm, "mid": v(19.57, -19.15) * mm, "end": v(19.55, -18.85) * mm});
            skArc(sketch, "E222.20.2", {"start": v(18.45, -18.45) * mm, "mid": v(4.22, -18.1) * mm, "end": v(5.27, -3.9) * mm});
            skPoint(sketch, "E222.20.3", {"position": v(18.9, -18.9) * mm});
            skArc(sketch, "E222.20.4", {"start": v(18.85, -19.55) * mm, "mid": v(18.7, -19.5) * mm, "end": v(18.57, -19.4) * mm});
            skLineSegment(sketch, "E222.20.5", {"start": v(3.9, -5.27) * mm, "end": v(19.6, -18.15) * mm});
            skArc(sketch, "E222.20.6", {"start": v(18.38, -19.4) * mm, "mid": v(18.26, -19.5) * mm, "end": v(18.15, -19.6) * mm});
            skLineSegment(sketch, "E222.20.7", {"start": v(5.27, -3.9) * mm, "end": v(18.15, -19.6) * mm});
            skArc(sketch, "E222.20.8", {"start": v(19.42, -19.42) * mm, "mid": v(19.15, -19.57) * mm, "end": v(18.85, -19.55) * mm});
            skPoint(sketch, "E222.20.9", {"position": v(18.45, -18.45) * mm});
            skArc(sketch, "E222.20.10", {"start": v(18.71, -18.71) * mm, "mid": v(18.35, -19.06) * mm, "end": v(17.97, -19.38) * mm, "construction": true});
            skArc(sketch, "E222.20.11", {"start": v(18.45, -18.45) * mm, "mid": v(18.1, -4.22) * mm, "end": v(3.9, -5.27) * mm});
            skPoint(sketch, "E222.20.12", {"position": v(18.71, -18.71) * mm});
            skArc(sketch, "E222.20.13", {"start": v(19.4, -18.38) * mm, "mid": v(19.5, -18.26) * mm, "end": v(19.6, -18.15) * mm});
            skArc(sketch, "E222.20.14", {"start": v(18.57, -19.4) * mm, "mid": v(18.47, -19.37) * mm, "end": v(18.38, -19.4) * mm});
            skArc(sketch, "E222.20.15", {"start": v(19.4, -18.57) * mm, "mid": v(19.37, -18.47) * mm, "end": v(19.4, -18.38) * mm});
            skArc(sketch, "E222.21.0", {"start": v(20.83, -17.14) * mm, "mid": v(20.74, -17) * mm, "end": v(20.63, -16.89) * mm});
            skArc(sketch, "E222.21.1", {"start": v(20.82, -17.72) * mm, "mid": v(20.9, -17.43) * mm, "end": v(20.83, -17.14) * mm});
            skArc(sketch, "E222.21.2", {"start": v(19.67, -16.96) * mm, "mid": v(5.65, -19.4) * mm, "end": v(3.9, -5.27) * mm});
            skPoint(sketch, "E222.21.3", {"position": v(20.2, -17.3) * mm});
            skArc(sketch, "E222.21.4", {"start": v(20.28, -17.97) * mm, "mid": v(20.12, -17.93) * mm, "end": v(19.97, -17.87) * mm});
            skLineSegment(sketch, "E222.21.5", {"start": v(2.84, -6.87) * mm, "end": v(20.74, -16.44) * mm});
            skArc(sketch, "E222.21.6", {"start": v(19.79, -17.91) * mm, "mid": v(19.7, -18.03) * mm, "end": v(19.6, -18.15) * mm});
            skLineSegment(sketch, "E222.21.7", {"start": v(3.9, -5.27) * mm, "end": v(19.6, -18.15) * mm});
            skArc(sketch, "E222.21.8", {"start": v(20.82, -17.72) * mm, "mid": v(20.58, -17.92) * mm, "end": v(20.28, -17.97) * mm});
            skPoint(sketch, "E222.21.9", {"position": v(19.67, -16.96) * mm});
            skArc(sketch, "E222.21.10", {"start": v(19.98, -17.17) * mm, "mid": v(19.7, -17.58) * mm, "end": v(19.38, -17.97) * mm, "construction": true});
            skArc(sketch, "E222.21.11", {"start": v(19.67, -16.96) * mm, "mid": v(16.55, -3.07) * mm, "end": v(2.84, -6.87) * mm});
            skPoint(sketch, "E222.21.12", {"position": v(19.98, -17.17) * mm});
            skArc(sketch, "E222.21.13", {"start": v(20.6, -16.7) * mm, "mid": v(20.67, -16.57) * mm, "end": v(20.74, -16.44) * mm});
            skArc(sketch, "E222.21.14", {"start": v(19.97, -17.87) * mm, "mid": v(19.87, -17.86) * mm, "end": v(19.79, -17.91) * mm});
            skArc(sketch, "E222.21.15", {"start": v(20.63, -16.89) * mm, "mid": v(20.58, -16.8) * mm, "end": v(20.6, -16.7) * mm});
            skArc(sketch, "E222.22.0", {"start": v(21.75, -15.2) * mm, "mid": v(21.64, -15.1) * mm, "end": v(21.5, -15) * mm});
            skArc(sketch, "E222.22.1", {"start": v(21.85, -15.79) * mm, "mid": v(21.89, -15.48) * mm, "end": v(21.75, -15.2) * mm});
            skArc(sketch, "E222.22.2", {"start": v(20.58, -15.26) * mm, "mid": v(7.3, -20.38) * mm, "end": v(2.84, -6.87) * mm});
            skPoint(sketch, "E222.22.3", {"position": v(21.16, -15.5) * mm});
            skArc(sketch, "E222.22.4", {"start": v(21.37, -16.13) * mm, "mid": v(21.21, -16.13) * mm, "end": v(21.05, -16.1) * mm});
            skLineSegment(sketch, "E222.22.5", {"start": v(2.1, -8.65) * mm, "end": v(21.53, -14.54) * mm});
            skArc(sketch, "E222.22.6", {"start": v(20.88, -16.17) * mm, "mid": v(20.81, -16.3) * mm, "end": v(20.74, -16.44) * mm});
            skLineSegment(sketch, "E222.22.7", {"start": v(2.84, -6.87) * mm, "end": v(20.74, -16.44) * mm});
            skArc(sketch, "E222.22.8", {"start": v(21.85, -15.79) * mm, "mid": v(21.66, -16.03) * mm, "end": v(21.37, -16.13) * mm});
            skPoint(sketch, "E222.22.9", {"position": v(20.58, -15.26) * mm});
            skArc(sketch, "E222.22.10", {"start": v(20.92, -15.4) * mm, "mid": v(20.72, -15.86) * mm, "end": v(20.5, -16.3) * mm, "construction": true});
            skArc(sketch, "E222.22.11", {"start": v(20.58, -15.26) * mm, "mid": v(14.8, -2.25) * mm, "end": v(2.1, -8.65) * mm});
            skPoint(sketch, "E222.22.12", {"position": v(20.92, -15.4) * mm});
            skArc(sketch, "E222.22.13", {"start": v(21.44, -14.83) * mm, "mid": v(21.48, -14.68) * mm, "end": v(21.53, -14.54) * mm});
            skArc(sketch, "E222.22.14", {"start": v(21.05, -16.1) * mm, "mid": v(20.95, -16.1) * mm, "end": v(20.88, -16.17) * mm});
            skArc(sketch, "E222.22.15", {"start": v(21.5, -15) * mm, "mid": v(21.44, -14.93) * mm, "end": v(21.44, -14.83) * mm});
            skArc(sketch, "E222.23.0", {"start": v(22.28, -13.14) * mm, "mid": v(22.14, -13.05) * mm, "end": v(22, -12.98) * mm});
            skArc(sketch, "E222.23.1", {"start": v(22.49, -13.69) * mm, "mid": v(22.46, -13.38) * mm, "end": v(22.28, -13.14) * mm});
            skArc(sketch, "E222.23.2", {"start": v(21.14, -13.42) * mm, "mid": v(9.11, -21.03) * mm, "end": v(2.1, -8.65) * mm});
            skPoint(sketch, "E222.23.3", {"position": v(21.75, -13.54) * mm});
            skArc(sketch, "E222.23.4", {"start": v(22.09, -14.11) * mm, "mid": v(21.93, -14.14) * mm, "end": v(21.77, -14.14) * mm});
            skLineSegment(sketch, "E222.23.5", {"start": v(1.72, -10.54) * mm, "end": v(21.93, -12.53) * mm});
            skArc(sketch, "E222.23.6", {"start": v(21.61, -14.26) * mm, "mid": v(21.57, -14.4) * mm, "end": v(21.53, -14.54) * mm});
            skLineSegment(sketch, "E222.23.7", {"start": v(2.1, -8.65) * mm, "end": v(21.53, -14.54) * mm});
            skArc(sketch, "E222.23.8", {"start": v(22.49, -13.69) * mm, "mid": v(22.35, -13.96) * mm, "end": v(22.09, -14.11) * mm});
            skPoint(sketch, "E222.23.9", {"position": v(21.14, -13.42) * mm});
            skArc(sketch, "E222.23.10", {"start": v(21.5, -13.49) * mm, "mid": v(21.4, -13.98) * mm, "end": v(21.26, -14.46) * mm, "construction": true});
            skArc(sketch, "E222.23.11", {"start": v(21.14, -13.42) * mm, "mid": v(12.94, -1.78) * mm, "end": v(1.72, -10.54) * mm});
            skPoint(sketch, "E222.23.12", {"position": v(21.5, -13.49) * mm});
            skArc(sketch, "E222.23.13", {"start": v(21.9, -12.82) * mm, "mid": v(21.91, -12.68) * mm, "end": v(21.93, -12.53) * mm});
            skArc(sketch, "E222.23.14", {"start": v(21.77, -14.14) * mm, "mid": v(21.67, -14.17) * mm, "end": v(21.61, -14.26) * mm});
            skArc(sketch, "E222.23.15", {"start": v(22, -12.98) * mm, "mid": v(21.92, -12.92) * mm, "end": v(21.9, -12.82) * mm});
            skArc(sketch, "E222.24.0", {"start": v(22.4, -11) * mm, "mid": v(22.24, -10.94) * mm, "end": v(22.08, -10.9) * mm});
            skArc(sketch, "E222.24.1", {"start": v(22.7, -11.5) * mm, "mid": v(22.62, -11.2) * mm, "end": v(22.4, -11) * mm});
            skArc(sketch, "E222.24.2", {"start": v(21.32, -11.5) * mm, "mid": v(11.02, -21.31) * mm, "end": v(1.72, -10.54) * mm});
            skPoint(sketch, "E222.24.3", {"position": v(21.95, -11.5) * mm});
            skArc(sketch, "E222.24.4", {"start": v(22.4, -12) * mm, "mid": v(22.24, -12.06) * mm, "end": v(22.08, -12.1) * mm});
            skLineSegment(sketch, "E222.24.5", {"start": v(1.72, -12.46) * mm, "end": v(21.93, -10.47) * mm});
            skArc(sketch, "E222.24.6", {"start": v(21.95, -12.23) * mm, "mid": v(21.94, -12.38) * mm, "end": v(21.93, -12.53) * mm});
            skLineSegment(sketch, "E222.24.7", {"start": v(1.72, -10.54) * mm, "end": v(21.93, -12.53) * mm});
            skArc(sketch, "E222.24.8", {"start": v(22.7, -11.5) * mm, "mid": v(22.62, -11.8) * mm, "end": v(22.4, -12) * mm});
            skPoint(sketch, "E222.24.9", {"position": v(21.32, -11.5) * mm});
            skArc(sketch, "E222.24.10", {"start": v(21.7, -11.5) * mm, "mid": v(21.69, -12) * mm, "end": v(21.65, -12.5) * mm, "construction": true});
            skArc(sketch, "E222.24.11", {"start": v(21.32, -11.5) * mm, "mid": v(11.02, -1.69) * mm, "end": v(1.72, -12.46) * mm});
            skPoint(sketch, "E222.24.12", {"position": v(21.7, -11.5) * mm});
            skArc(sketch, "E222.24.13", {"start": v(21.95, -10.77) * mm, "mid": v(21.94, -10.62) * mm, "end": v(21.93, -10.47) * mm});
            skArc(sketch, "E222.24.14", {"start": v(22.08, -12.1) * mm, "mid": v(22, -12.14) * mm, "end": v(21.95, -12.23) * mm});
            skArc(sketch, "E222.24.15", {"start": v(22.08, -10.9) * mm, "mid": v(22, -10.86) * mm, "end": v(21.95, -10.77) * mm});
            skArc(sketch, "E222.25.0", {"start": v(22.09, -8.89) * mm, "mid": v(21.93, -8.86) * mm, "end": v(21.77, -8.86) * mm});
            skArc(sketch, "E222.25.1", {"start": v(22.49, -9.31) * mm, "mid": v(22.35, -9.04) * mm, "end": v(22.09, -8.89) * mm});
            skArc(sketch, "E222.25.2", {"start": v(21.14, -9.58) * mm, "mid": v(12.94, -21.22) * mm, "end": v(1.72, -12.46) * mm});
            skPoint(sketch, "E222.25.3", {"position": v(21.75, -9.46) * mm});
            skArc(sketch, "E222.25.4", {"start": v(22.28, -9.86) * mm, "mid": v(22.14, -9.95) * mm, "end": v(22, -10.02) * mm});
            skLineSegment(sketch, "E222.25.5", {"start": v(2.1, -14.35) * mm, "end": v(21.53, -8.46) * mm});
            skArc(sketch, "E222.25.6", {"start": v(21.9, -10.18) * mm, "mid": v(21.91, -10.32) * mm, "end": v(21.93, -10.47) * mm});
            skLineSegment(sketch, "E222.25.7", {"start": v(1.72, -12.46) * mm, "end": v(21.93, -10.47) * mm});
            skArc(sketch, "E222.25.8", {"start": v(22.49, -9.31) * mm, "mid": v(22.46, -9.62) * mm, "end": v(22.28, -9.86) * mm});
            skPoint(sketch, "E222.25.9", {"position": v(21.14, -9.58) * mm});
            skArc(sketch, "E222.25.10", {"start": v(21.5, -9.51) * mm, "mid": v(21.59, -10) * mm, "end": v(21.65, -10.5) * mm, "construction": true});
            skArc(sketch, "E222.25.11", {"start": v(21.14, -9.58) * mm, "mid": v(9.11, -1.97) * mm, "end": v(2.1, -14.35) * mm});
            skPoint(sketch, "E222.25.12", {"position": v(21.5, -9.51) * mm});
            skArc(sketch, "E222.25.13", {"start": v(21.61, -8.74) * mm, "mid": v(21.57, -8.6) * mm, "end": v(21.53, -8.46) * mm});
            skArc(sketch, "E222.25.14", {"start": v(22, -10.02) * mm, "mid": v(21.92, -10.08) * mm, "end": v(21.9, -10.18) * mm});
            skArc(sketch, "E222.25.15", {"start": v(21.77, -8.86) * mm, "mid": v(21.67, -8.83) * mm, "end": v(21.61, -8.74) * mm});
            skArc(sketch, "E222.26.0", {"start": v(21.37, -6.87) * mm, "mid": v(21.21, -6.87) * mm, "end": v(21.05, -6.9) * mm});
            skArc(sketch, "E222.26.1", {"start": v(21.85, -7.21) * mm, "mid": v(21.66, -6.97) * mm, "end": v(21.37, -6.87) * mm});
            skArc(sketch, "E222.26.2", {"start": v(20.58, -7.74) * mm, "mid": v(14.8, -20.75) * mm, "end": v(2.1, -14.35) * mm});
            skPoint(sketch, "E222.26.3", {"position": v(21.16, -7.5) * mm});
            skArc(sketch, "E222.26.4", {"start": v(21.75, -7.8) * mm, "mid": v(21.64, -7.9) * mm, "end": v(21.5, -8) * mm});
            skLineSegment(sketch, "E222.26.5", {"start": v(2.84, -16.13) * mm, "end": v(20.74, -6.56) * mm});
            skArc(sketch, "E222.26.6", {"start": v(21.44, -8.17) * mm, "mid": v(21.48, -8.32) * mm, "end": v(21.53, -8.46) * mm});
            skLineSegment(sketch, "E222.26.7", {"start": v(2.1, -14.35) * mm, "end": v(21.53, -8.46) * mm});
            skArc(sketch, "E222.26.8", {"start": v(21.85, -7.21) * mm, "mid": v(21.89, -7.52) * mm, "end": v(21.75, -7.8) * mm});
            skPoint(sketch, "E222.26.9", {"position": v(20.58, -7.74) * mm});
            skArc(sketch, "E222.26.10", {"start": v(20.92, -7.6) * mm, "mid": v(21.1, -8.06) * mm, "end": v(21.26, -8.54) * mm, "construction": true});
            skArc(sketch, "E222.26.11", {"start": v(20.58, -7.74) * mm, "mid": v(7.3, -2.62) * mm, "end": v(2.84, -16.13) * mm});
            skPoint(sketch, "E222.26.12", {"position": v(20.92, -7.6) * mm});
            skArc(sketch, "E222.26.13", {"start": v(20.88, -6.83) * mm, "mid": v(20.81, -6.7) * mm, "end": v(20.74, -6.56) * mm});
            skArc(sketch, "E222.26.14", {"start": v(21.5, -8) * mm, "mid": v(21.44, -8.07) * mm, "end": v(21.44, -8.17) * mm});
            skArc(sketch, "E222.26.15", {"start": v(21.05, -6.9) * mm, "mid": v(20.95, -6.9) * mm, "end": v(20.88, -6.83) * mm});
            skArc(sketch, "E222.27.0", {"start": v(20.28, -5.03) * mm, "mid": v(20.12, -5.07) * mm, "end": v(19.97, -5.13) * mm});
            skArc(sketch, "E222.27.1", {"start": v(20.82, -5.28) * mm, "mid": v(20.58, -5.08) * mm, "end": v(20.28, -5.03) * mm});
            skArc(sketch, "E222.27.2", {"start": v(19.67, -6.04) * mm, "mid": v(16.55, -19.93) * mm, "end": v(2.84, -16.13) * mm});
            skPoint(sketch, "E222.27.3", {"position": v(20.2, -5.7) * mm});
            skArc(sketch, "E222.27.4", {"start": v(20.83, -5.86) * mm, "mid": v(20.74, -6) * mm, "end": v(20.63, -6.11) * mm});
            skLineSegment(sketch, "E222.27.5", {"start": v(3.9, -17.73) * mm, "end": v(19.6, -4.85) * mm});
            skArc(sketch, "E222.27.6", {"start": v(20.6, -6.3) * mm, "mid": v(20.67, -6.43) * mm, "end": v(20.74, -6.56) * mm});
            skLineSegment(sketch, "E222.27.7", {"start": v(2.84, -16.13) * mm, "end": v(20.74, -6.56) * mm});
            skArc(sketch, "E222.27.8", {"start": v(20.82, -5.28) * mm, "mid": v(20.9, -5.57) * mm, "end": v(20.83, -5.86) * mm});
            skPoint(sketch, "E222.27.9", {"position": v(19.67, -6.04) * mm});
            skArc(sketch, "E222.27.10", {"start": v(19.98, -5.83) * mm, "mid": v(20.25, -6.26) * mm, "end": v(20.5, -6.7) * mm, "construction": true});
            skArc(sketch, "E222.27.11", {"start": v(19.67, -6.04) * mm, "mid": v(5.65, -3.6) * mm, "end": v(3.9, -17.73) * mm});
            skPoint(sketch, "E222.27.12", {"position": v(19.98, -5.83) * mm});
            skArc(sketch, "E222.27.13", {"start": v(19.79, -5.09) * mm, "mid": v(19.7, -4.97) * mm, "end": v(19.6, -4.85) * mm});
            skArc(sketch, "E222.27.14", {"start": v(20.63, -6.11) * mm, "mid": v(20.58, -6.2) * mm, "end": v(20.6, -6.3) * mm});
            skArc(sketch, "E222.27.15", {"start": v(19.97, -5.13) * mm, "mid": v(19.87, -5.14) * mm, "end": v(19.79, -5.09) * mm});
            skArc(sketch, "E222.28.0", {"start": v(18.85, -3.45) * mm, "mid": v(18.7, -3.5) * mm, "end": v(18.57, -3.6) * mm});
            skArc(sketch, "E222.28.1", {"start": v(19.42, -3.58) * mm, "mid": v(19.15, -3.43) * mm, "end": v(18.85, -3.45) * mm});
            skArc(sketch, "E222.28.2", {"start": v(18.45, -4.55) * mm, "mid": v(18.1, -18.78) * mm, "end": v(3.9, -17.73) * mm});
            skPoint(sketch, "E222.28.3", {"position": v(18.9, -4.1) * mm});
            skArc(sketch, "E222.28.4", {"start": v(19.55, -4.15) * mm, "mid": v(19.5, -4.3) * mm, "end": v(19.4, -4.43) * mm});
            skLineSegment(sketch, "E222.28.5", {"start": v(5.27, -19.1) * mm, "end": v(18.15, -3.4) * mm});
            skArc(sketch, "E222.28.6", {"start": v(19.4, -4.62) * mm, "mid": v(19.5, -4.74) * mm, "end": v(19.6, -4.85) * mm});
            skLineSegment(sketch, "E222.28.7", {"start": v(3.9, -17.73) * mm, "end": v(19.6, -4.85) * mm});
            skArc(sketch, "E222.28.8", {"start": v(19.42, -3.58) * mm, "mid": v(19.57, -3.85) * mm, "end": v(19.55, -4.15) * mm});
            skPoint(sketch, "E222.28.9", {"position": v(18.45, -4.55) * mm});
            skArc(sketch, "E222.28.10", {"start": v(18.71, -4.29) * mm, "mid": v(19.06, -4.65) * mm, "end": v(19.38, -5.03) * mm, "construction": true});
            skArc(sketch, "E222.28.11", {"start": v(18.45, -4.55) * mm, "mid": v(4.22, -4.9) * mm, "end": v(5.27, -19.1) * mm});
            skPoint(sketch, "E222.28.12", {"position": v(18.71, -4.29) * mm});
            skArc(sketch, "E222.28.13", {"start": v(18.38, -3.6) * mm, "mid": v(18.26, -3.5) * mm, "end": v(18.15, -3.4) * mm});
            skArc(sketch, "E222.28.14", {"start": v(19.4, -4.43) * mm, "mid": v(19.37, -4.53) * mm, "end": v(19.4, -4.62) * mm});
            skArc(sketch, "E222.28.15", {"start": v(18.57, -3.6) * mm, "mid": v(18.47, -3.63) * mm, "end": v(18.38, -3.6) * mm});
            skArc(sketch, "E222.29.0", {"start": v(17.14, -2.17) * mm, "mid": v(17, -2.26) * mm, "end": v(16.89, -2.37) * mm});
            skArc(sketch, "E222.29.1", {"start": v(17.72, -2.18) * mm, "mid": v(17.43, -2.1) * mm, "end": v(17.14, -2.17) * mm});
            skArc(sketch, "E222.29.2", {"start": v(16.96, -3.33) * mm, "mid": v(19.4, -17.35) * mm, "end": v(5.27, -19.1) * mm});
            skPoint(sketch, "E222.29.3", {"position": v(17.3, -2.8) * mm});
            skArc(sketch, "E222.29.4", {"start": v(17.97, -2.72) * mm, "mid": v(17.93, -2.88) * mm, "end": v(17.87, -3.03) * mm});
            skLineSegment(sketch, "E222.29.5", {"start": v(6.87, -20.16) * mm, "end": v(16.44, -2.26) * mm});
            skArc(sketch, "E222.29.6", {"start": v(17.91, -3.21) * mm, "mid": v(18.03, -3.3) * mm, "end": v(18.15, -3.4) * mm});
            skLineSegment(sketch, "E222.29.7", {"start": v(5.27, -19.1) * mm, "end": v(18.15, -3.4) * mm});
            skArc(sketch, "E222.29.8", {"start": v(17.72, -2.18) * mm, "mid": v(17.92, -2.42) * mm, "end": v(17.97, -2.72) * mm});
            skPoint(sketch, "E222.29.9", {"position": v(16.96, -3.33) * mm});
            skArc(sketch, "E222.29.10", {"start": v(17.17, -3.02) * mm, "mid": v(17.58, -3.3) * mm, "end": v(17.97, -3.62) * mm, "construction": true});
            skArc(sketch, "E222.29.11", {"start": v(16.96, -3.33) * mm, "mid": v(3.07, -6.45) * mm, "end": v(6.87, -20.16) * mm});
            skPoint(sketch, "E222.29.12", {"position": v(17.17, -3.02) * mm});
            skArc(sketch, "E222.29.13", {"start": v(16.7, -2.4) * mm, "mid": v(16.57, -2.33) * mm, "end": v(16.44, -2.26) * mm});
            skArc(sketch, "E222.29.14", {"start": v(17.87, -3.03) * mm, "mid": v(17.86, -3.13) * mm, "end": v(17.91, -3.21) * mm});
            skArc(sketch, "E222.29.15", {"start": v(16.89, -2.37) * mm, "mid": v(16.8, -2.42) * mm, "end": v(16.7, -2.4) * mm});
            skArc(sketch, "E222.30.0", {"start": v(15.2, -1.25) * mm, "mid": v(15.1, -1.36) * mm, "end": v(15, -1.5) * mm});
            skArc(sketch, "E222.30.1", {"start": v(15.79, -1.15) * mm, "mid": v(15.48, -1.11) * mm, "end": v(15.2, -1.25) * mm});
            skArc(sketch, "E222.30.2", {"start": v(15.26, -2.42) * mm, "mid": v(20.38, -15.7) * mm, "end": v(6.87, -20.16) * mm});
            skPoint(sketch, "E222.30.3", {"position": v(15.5, -1.84) * mm});
            skArc(sketch, "E222.30.4", {"start": v(16.13, -1.63) * mm, "mid": v(16.13, -1.79) * mm, "end": v(16.1, -1.95) * mm});
            skLineSegment(sketch, "E222.30.5", {"start": v(8.65, -20.9) * mm, "end": v(14.54, -1.47) * mm});
            skArc(sketch, "E222.30.6", {"start": v(16.17, -2.12) * mm, "mid": v(16.3, -2.19) * mm, "end": v(16.44, -2.26) * mm});
            skLineSegment(sketch, "E222.30.7", {"start": v(6.87, -20.16) * mm, "end": v(16.44, -2.26) * mm});
            skArc(sketch, "E222.30.8", {"start": v(15.79, -1.15) * mm, "mid": v(16.03, -1.34) * mm, "end": v(16.13, -1.63) * mm});
            skPoint(sketch, "E222.30.9", {"position": v(15.26, -2.42) * mm});
            skArc(sketch, "E222.30.10", {"start": v(15.4, -2.08) * mm, "mid": v(15.86, -2.28) * mm, "end": v(16.3, -2.5) * mm, "construction": true});
            skArc(sketch, "E222.30.11", {"start": v(15.26, -2.42) * mm, "mid": v(2.25, -8.2) * mm, "end": v(8.65, -20.9) * mm});
            skPoint(sketch, "E222.30.12", {"position": v(15.4, -2.08) * mm});
            skArc(sketch, "E222.30.13", {"start": v(14.83, -1.56) * mm, "mid": v(14.68, -1.52) * mm, "end": v(14.54, -1.47) * mm});
            skArc(sketch, "E222.30.14", {"start": v(16.1, -1.95) * mm, "mid": v(16.1, -2.05) * mm, "end": v(16.17, -2.12) * mm});
            skArc(sketch, "E222.30.15", {"start": v(15, -1.5) * mm, "mid": v(14.93, -1.56) * mm, "end": v(14.83, -1.56) * mm});
            skArc(sketch, "E222.31.0", {"start": v(13.14, -0.72) * mm, "mid": v(13.05, -0.86) * mm, "end": v(12.98, -1) * mm});
            skArc(sketch, "E222.31.1", {"start": v(13.69, -0.51) * mm, "mid": v(13.38, -0.54) * mm, "end": v(13.14, -0.72) * mm});
            skArc(sketch, "E222.31.2", {"start": v(13.42, -1.86) * mm, "mid": v(21.03, -13.89) * mm, "end": v(8.65, -20.9) * mm});
            skPoint(sketch, "E222.31.3", {"position": v(13.54, -1.25) * mm});
            skArc(sketch, "E222.31.4", {"start": v(14.11, -0.91) * mm, "mid": v(14.14, -1.07) * mm, "end": v(14.14, -1.23) * mm});
            skArc(sketch, "E222.31.6", {"start": v(14.26, -1.39) * mm, "mid": v(14.4, -1.43) * mm, "end": v(14.54, -1.47) * mm});
            skLineSegment(sketch, "E222.31.7", {"start": v(8.65, -20.9) * mm, "end": v(14.54, -1.47) * mm});
            skArc(sketch, "E222.31.8", {"start": v(13.69, -0.51) * mm, "mid": v(13.96, -0.65) * mm, "end": v(14.11, -0.91) * mm});
            skPoint(sketch, "E222.31.9", {"position": v(13.42, -1.86) * mm});
            skArc(sketch, "E222.31.10", {"start": v(13.49, -1.5) * mm, "mid": v(13.98, -1.6) * mm, "end": v(14.46, -1.74) * mm, "construction": true});
            skArc(sketch, "E222.31.11", {"start": v(13.42, -1.86) * mm, "mid": v(1.78, -10.06) * mm, "end": v(10.54, -21.28) * mm});
            skPoint(sketch, "E222.31.12", {"position": v(13.49, -1.5) * mm});
            skArc(sketch, "E222.31.13", {"start": v(12.82, -1.1) * mm, "mid": v(12.68, -1.09) * mm, "end": v(12.53, -1.07) * mm});
            skArc(sketch, "E222.31.14", {"start": v(14.14, -1.23) * mm, "mid": v(14.17, -1.33) * mm, "end": v(14.26, -1.39) * mm});
            skArc(sketch, "E222.31.15", {"start": v(12.98, -1) * mm, "mid": v(12.92, -1.08) * mm, "end": v(12.82, -1.1) * mm});
            skArc(sketch, "E223.0", {"start": v(4.25, -18.75) * mm, "mid": v(18.75, -18.75) * mm, "end": v(18.75, -4.25) * mm});
            skLineSegment(sketch, "E224", {"start": v(4.25, -18.75) * mm, "end": v(18.75, -4.25) * mm, "construction": true});
            skSolve(sketch);
        }
        {
            var Q0;
            Q0 = qSketchRegion(id + "F34", true);
            extrude(context, id + "F35", {"entities" : qUnion([Q0]), "operationType" : NewBodyOperationType.REMOVE, "endBound" : BoundingType.SYMMETRIC, "oppositeDirection" : true, "depth" : 6.5 * mm});
        }
        {
            var Q0;
            {var subQ0=sQuery(id+"F0.wireOp",EDGE,"E28");var subQ1=sQuery(id+"F0.wireOp",EDGE,"E27");var subQ2=sQuery(id+"F0.wireOp",EDGE,"E26");var subQ3=sQuery(id+"F0.wireOp",EDGE,"E24");var subQ4=sQuery(id+"F0.wireOp",EDGE,"E23");Q0=makeQuery(id+"F2.boolean.opBoolean","MERGE",FACE,{"derivedFrom":[makeQuery(id+"F1.opExtrude","CAP_FACE",FACE,{"disambiguationData":[OSD([sQuery(id+"F0.wireOp",EDGE,"E0.right"),sQuery(id+"F0.wireOp",EDGE,"E4"),sQuery(id+"F0.wireOp",EDGE,"E9"),sQuery(id+"F0.wireOp",EDGE,"E11.MirrorC"),sQuery(id+"F0.wireOp",EDGE,"E13.MirrorC"),sQuery(id+"F0.wireOp",EDGE,"E14.MirrorC"),sQuery(id+"F0.wireOp",EDGE,"E15"),sQuery(id+"F0.wireOp",EDGE,"E17.MirrorC"),sQuery(id+"F0.wireOp",EDGE,"E18.MirrorC"),sQuery(id+"F0.wireOp",EDGE,"E20.MirrorC"),sQuery(id+"F0.wireOp",EDGE,"E21"),sQuery(id+"F0.wireOp",EDGE,"E22"),subQ4,subQ3,sQuery(id+"F0.wireOp",EDGE,"E25"),subQ2,subQ1,subQ0,sQuery(id+"F0.wireOp",EDGE,"E30.0"),sQuery(id+"F0.wireOp",EDGE,"E30.1"),sQuery(id+"F0.wireOp",EDGE,"E30.2")])],"isStart":true}),makeQuery(id+"F2.opExtrude","CAP_FACE",FACE,{"disambiguationData":[OSD([subQ4,subQ3,subQ2,subQ1,subQ0,sQuery(id+"F0.wireOp",EDGE,"E31"),sQuery(id+"F0.wireOp",EDGE,"E32"),sQuery(id+"F0.wireOp",EDGE,"E33"),sQuery(id+"F0.wireOp",EDGE,"E34"),sQuery(id+"F0.wireOp",EDGE,"E35"),sQuery(id+"F0.wireOp",EDGE,"E39"),sQuery(id+"F0.wireOp",EDGE,"E41"),sQuery(id+"F0.wireOp",EDGE,"E43"),sQuery(id+"F0.wireOp",EDGE,"E44"),sQuery(id+"F0.wireOp",EDGE,"E45"),sQuery(id+"F0.wireOp",EDGE,"E46")])],"isStart":true})]});}
            var Q1;
            Q1=sQuery(id+"F10.wireOp",VERTEX,"E105");
            cPlane(context, id + "F36", {"entities" : qUnion([Q0, Q1]), "cplaneType" : CPlaneType.PLANE_POINT, "offset" : 150 * mm, "width" : 150 * mm, "height" : 150 * mm});
        }
        {
            var Q0;
            Q0=qCreatedBy(id+"F36.planeOp",FACE);
            var sketch = newSketch(context, id + "F37", { "sketchPlane" : qUnion([Q0])});
            skLineSegment(sketch, "E225", {"start": v(11.5, -0.3) * mm, "end": v(11.5, -1.68) * mm, "construction": true});
            skArc(sketch, "E226", {"start": v(11.5, -0.3) * mm, "mid": v(11.8, -0.38) * mm, "end": v(12, -0.6) * mm});
            skArc(sketch, "E227", {"start": v(12, -0.6) * mm, "mid": v(12.06, -0.76) * mm, "end": v(12.1, -0.92) * mm});
            skArc(sketch, "E228", {"start": v(12.1, -0.92) * mm, "mid": v(12.14, -1) * mm, "end": v(12.23, -1.05) * mm});
            skPoint(sketch, "E229", {"position": v(11.5, -1.68) * mm});
            skPoint(sketch, "E230", {"position": v(11.5, -1.05) * mm});
            skPoint(sketch, "E231", {"position": v(11.5, -1.3) * mm});
            skArc(sketch, "E232", {"start": v(11.5, -1.3) * mm, "mid": v(12, -1.31) * mm, "end": v(12.5, -1.35) * mm, "construction": true});
            skLineSegment(sketch, "E233", {"start": v(12.46, -1.72) * mm, "end": v(12.53, -1.07) * mm});
            skArc(sketch, "E234", {"start": v(12.23, -1.05) * mm, "mid": v(12.38, -1.06) * mm, "end": v(12.53, -1.07) * mm});
            skArc(sketch, "E235", {"start": v(11.5, -1.68) * mm, "mid": v(11.98, -1.69) * mm, "end": v(12.46, -1.72) * mm});
            skArc(sketch, "E236.MirrorCS", {"start": v(11.5, -0.3) * mm, "mid": v(11.2, -0.38) * mm, "end": v(11, -0.6) * mm});
            skArc(sketch, "E237.MirrorCS", {"start": v(11, -0.6) * mm, "mid": v(10.94, -0.76) * mm, "end": v(10.9, -0.92) * mm});
            skArc(sketch, "E238.MirrorCS", {"start": v(10.9, -0.92) * mm, "mid": v(10.86, -1) * mm, "end": v(10.77, -1.05) * mm});
            skArc(sketch, "E239.MirrorCS", {"start": v(10.77, -1.05) * mm, "mid": v(10.62, -1.06) * mm, "end": v(10.47, -1.07) * mm});
            skLineSegment(sketch, "E240.MirrorCS", {"start": v(10.54, -1.72) * mm, "end": v(10.47, -1.07) * mm});
            skArc(sketch, "E241.MirrorCS", {"start": v(11.5, -1.68) * mm, "mid": v(11.02, -1.69) * mm, "end": v(10.54, -1.72) * mm});
            skArc(sketch, "E242.1.0", {"start": v(8.89, -0.91) * mm, "mid": v(8.86, -1.07) * mm, "end": v(8.86, -1.23) * mm});
            skArc(sketch, "E242.1.1", {"start": v(9.31, -0.51) * mm, "mid": v(9.04, -0.65) * mm, "end": v(8.89, -0.91) * mm});
            skArc(sketch, "E242.1.2", {"start": v(9.58, -1.86) * mm, "mid": v(10.06, -1.78) * mm, "end": v(10.54, -1.72) * mm});
            skPoint(sketch, "E242.1.3", {"position": v(9.46, -1.25) * mm});
            skArc(sketch, "E242.1.4", {"start": v(9.86, -0.72) * mm, "mid": v(9.95, -0.86) * mm, "end": v(10.02, -1) * mm});
            skLineSegment(sketch, "E242.1.5", {"start": v(8.65, -2.1) * mm, "end": v(8.46, -1.47) * mm});
            skArc(sketch, "E242.1.6", {"start": v(10.18, -1.1) * mm, "mid": v(10.32, -1.09) * mm, "end": v(10.47, -1.07) * mm});
            skArc(sketch, "E242.1.8", {"start": v(9.31, -0.51) * mm, "mid": v(9.62, -0.54) * mm, "end": v(9.86, -0.72) * mm});
            skPoint(sketch, "E242.1.9", {"position": v(9.58, -1.86) * mm});
            skArc(sketch, "E242.1.10", {"start": v(9.51, -1.5) * mm, "mid": v(10, -1.41) * mm, "end": v(10.5, -1.35) * mm, "construction": true});
            skArc(sketch, "E242.1.11", {"start": v(9.58, -1.86) * mm, "mid": v(9.11, -1.97) * mm, "end": v(8.65, -2.1) * mm});
            skPoint(sketch, "E242.1.12", {"position": v(9.51, -1.5) * mm});
            skArc(sketch, "E242.1.13", {"start": v(8.74, -1.39) * mm, "mid": v(8.6, -1.43) * mm, "end": v(8.46, -1.47) * mm});
            skArc(sketch, "E242.1.14", {"start": v(10.02, -1) * mm, "mid": v(10.08, -1.08) * mm, "end": v(10.18, -1.1) * mm});
            skArc(sketch, "E242.1.15", {"start": v(8.86, -1.23) * mm, "mid": v(8.83, -1.33) * mm, "end": v(8.74, -1.39) * mm});
            skArc(sketch, "E242.2.0", {"start": v(6.87, -1.63) * mm, "mid": v(6.87, -1.79) * mm, "end": v(6.9, -1.95) * mm});
            skArc(sketch, "E242.2.1", {"start": v(7.21, -1.15) * mm, "mid": v(6.97, -1.34) * mm, "end": v(6.87, -1.63) * mm});
            skArc(sketch, "E242.2.2", {"start": v(7.74, -2.42) * mm, "mid": v(8.2, -2.25) * mm, "end": v(8.65, -2.1) * mm});
            skPoint(sketch, "E242.2.3", {"position": v(7.5, -1.84) * mm});
            skArc(sketch, "E242.2.4", {"start": v(7.8, -1.25) * mm, "mid": v(7.9, -1.36) * mm, "end": v(8, -1.5) * mm});
            skLineSegment(sketch, "E242.2.5", {"start": v(6.87, -2.84) * mm, "end": v(6.56, -2.26) * mm});
            skArc(sketch, "E242.2.6", {"start": v(8.17, -1.56) * mm, "mid": v(8.32, -1.52) * mm, "end": v(8.46, -1.47) * mm});
            skLineSegment(sketch, "E242.2.7", {"start": v(8.65, -2.1) * mm, "end": v(8.46, -1.47) * mm});
            skArc(sketch, "E242.2.8", {"start": v(7.21, -1.15) * mm, "mid": v(7.52, -1.11) * mm, "end": v(7.8, -1.25) * mm});
            skPoint(sketch, "E242.2.9", {"position": v(7.74, -2.42) * mm});
            skArc(sketch, "E242.2.10", {"start": v(7.6, -2.08) * mm, "mid": v(8.06, -1.9) * mm, "end": v(8.54, -1.74) * mm, "construction": true});
            skArc(sketch, "E242.2.11", {"start": v(7.74, -2.42) * mm, "mid": v(7.3, -2.62) * mm, "end": v(6.87, -2.84) * mm});
            skPoint(sketch, "E242.2.12", {"position": v(7.6, -2.08) * mm});
            skArc(sketch, "E242.2.13", {"start": v(6.83, -2.12) * mm, "mid": v(6.7, -2.19) * mm, "end": v(6.56, -2.26) * mm});
            skArc(sketch, "E242.2.14", {"start": v(8, -1.5) * mm, "mid": v(8.07, -1.56) * mm, "end": v(8.17, -1.56) * mm});
            skArc(sketch, "E242.2.15", {"start": v(6.9, -1.95) * mm, "mid": v(6.9, -2.05) * mm, "end": v(6.83, -2.12) * mm});
            skArc(sketch, "E242.3.0", {"start": v(5.03, -2.72) * mm, "mid": v(5.07, -2.88) * mm, "end": v(5.13, -3.03) * mm});
            skArc(sketch, "E242.3.1", {"start": v(5.28, -2.18) * mm, "mid": v(5.08, -2.42) * mm, "end": v(5.03, -2.72) * mm});
            skArc(sketch, "E242.3.2", {"start": v(6.04, -3.33) * mm, "mid": v(6.45, -3.07) * mm, "end": v(6.87, -2.84) * mm});
            skPoint(sketch, "E242.3.3", {"position": v(5.7, -2.8) * mm});
            skArc(sketch, "E242.3.4", {"start": v(5.86, -2.17) * mm, "mid": v(6, -2.26) * mm, "end": v(6.11, -2.37) * mm});
            skLineSegment(sketch, "E242.3.5", {"start": v(5.27, -3.9) * mm, "end": v(4.85, -3.4) * mm});
            skArc(sketch, "E242.3.6", {"start": v(6.3, -2.4) * mm, "mid": v(6.43, -2.33) * mm, "end": v(6.56, -2.26) * mm});
            skLineSegment(sketch, "E242.3.7", {"start": v(6.87, -2.84) * mm, "end": v(6.56, -2.26) * mm});
            skArc(sketch, "E242.3.8", {"start": v(5.28, -2.18) * mm, "mid": v(5.57, -2.1) * mm, "end": v(5.86, -2.17) * mm});
            skPoint(sketch, "E242.3.9", {"position": v(6.04, -3.33) * mm});
            skArc(sketch, "E242.3.10", {"start": v(5.83, -3.02) * mm, "mid": v(6.26, -2.75) * mm, "end": v(6.7, -2.5) * mm, "construction": true});
            skArc(sketch, "E242.3.11", {"start": v(6.04, -3.33) * mm, "mid": v(5.65, -3.6) * mm, "end": v(5.27, -3.9) * mm});
            skPoint(sketch, "E242.3.12", {"position": v(5.83, -3.02) * mm});
            skArc(sketch, "E242.3.13", {"start": v(5.09, -3.21) * mm, "mid": v(4.97, -3.3) * mm, "end": v(4.85, -3.4) * mm});
            skArc(sketch, "E242.3.14", {"start": v(6.11, -2.37) * mm, "mid": v(6.2, -2.42) * mm, "end": v(6.3, -2.4) * mm});
            skArc(sketch, "E242.3.15", {"start": v(5.13, -3.03) * mm, "mid": v(5.14, -3.13) * mm, "end": v(5.09, -3.21) * mm});
            skArc(sketch, "E242.4.0", {"start": v(3.45, -4.15) * mm, "mid": v(3.5, -4.3) * mm, "end": v(3.6, -4.43) * mm});
            skArc(sketch, "E242.4.1", {"start": v(3.58, -3.58) * mm, "mid": v(3.43, -3.85) * mm, "end": v(3.45, -4.15) * mm});
            skArc(sketch, "E242.4.2", {"start": v(4.55, -4.55) * mm, "mid": v(4.9, -4.22) * mm, "end": v(5.27, -3.9) * mm});
            skPoint(sketch, "E242.4.3", {"position": v(4.1, -4.1) * mm});
            skArc(sketch, "E242.4.4", {"start": v(4.15, -3.45) * mm, "mid": v(4.3, -3.5) * mm, "end": v(4.43, -3.6) * mm});
            skLineSegment(sketch, "E242.4.5", {"start": v(3.9, -5.27) * mm, "end": v(3.4, -4.85) * mm});
            skArc(sketch, "E242.4.6", {"start": v(4.62, -3.6) * mm, "mid": v(4.74, -3.5) * mm, "end": v(4.85, -3.4) * mm});
            skLineSegment(sketch, "E242.4.7", {"start": v(5.27, -3.9) * mm, "end": v(4.85, -3.4) * mm});
            skArc(sketch, "E242.4.8", {"start": v(3.58, -3.58) * mm, "mid": v(3.85, -3.43) * mm, "end": v(4.15, -3.45) * mm});
            skPoint(sketch, "E242.4.9", {"position": v(4.55, -4.55) * mm});
            skArc(sketch, "E242.4.10", {"start": v(4.29, -4.29) * mm, "mid": v(4.65, -3.94) * mm, "end": v(5.03, -3.62) * mm, "construction": true});
            skArc(sketch, "E242.4.11", {"start": v(4.55, -4.55) * mm, "mid": v(4.22, -4.9) * mm, "end": v(3.9, -5.27) * mm});
            skPoint(sketch, "E242.4.12", {"position": v(4.29, -4.29) * mm});
            skArc(sketch, "E242.4.13", {"start": v(3.6, -4.62) * mm, "mid": v(3.5, -4.74) * mm, "end": v(3.4, -4.85) * mm});
            skArc(sketch, "E242.4.14", {"start": v(4.43, -3.6) * mm, "mid": v(4.53, -3.63) * mm, "end": v(4.62, -3.6) * mm});
            skArc(sketch, "E242.4.15", {"start": v(3.6, -4.43) * mm, "mid": v(3.63, -4.53) * mm, "end": v(3.6, -4.62) * mm});
            skArc(sketch, "E242.5.0", {"start": v(2.17, -5.86) * mm, "mid": v(2.26, -6) * mm, "end": v(2.37, -6.11) * mm});
            skArc(sketch, "E242.5.1", {"start": v(2.18, -5.28) * mm, "mid": v(2.1, -5.57) * mm, "end": v(2.17, -5.86) * mm});
            skArc(sketch, "E242.5.2", {"start": v(3.33, -6.04) * mm, "mid": v(3.6, -5.65) * mm, "end": v(3.9, -5.27) * mm});
            skPoint(sketch, "E242.5.3", {"position": v(2.8, -5.7) * mm});
            skArc(sketch, "E242.5.4", {"start": v(2.72, -5.03) * mm, "mid": v(2.88, -5.07) * mm, "end": v(3.03, -5.13) * mm});
            skLineSegment(sketch, "E242.5.5", {"start": v(2.84, -6.87) * mm, "end": v(2.26, -6.56) * mm});
            skArc(sketch, "E242.5.6", {"start": v(3.21, -5.09) * mm, "mid": v(3.3, -4.97) * mm, "end": v(3.4, -4.85) * mm});
            skLineSegment(sketch, "E242.5.7", {"start": v(3.9, -5.27) * mm, "end": v(3.4, -4.85) * mm});
            skArc(sketch, "E242.5.8", {"start": v(2.18, -5.28) * mm, "mid": v(2.42, -5.08) * mm, "end": v(2.72, -5.03) * mm});
            skPoint(sketch, "E242.5.9", {"position": v(3.33, -6.04) * mm});
            skArc(sketch, "E242.5.10", {"start": v(3.02, -5.83) * mm, "mid": v(3.3, -5.42) * mm, "end": v(3.62, -5.03) * mm, "construction": true});
            skArc(sketch, "E242.5.11", {"start": v(3.33, -6.04) * mm, "mid": v(3.07, -6.45) * mm, "end": v(2.84, -6.87) * mm});
            skPoint(sketch, "E242.5.12", {"position": v(3.02, -5.83) * mm});
            skArc(sketch, "E242.5.13", {"start": v(2.4, -6.3) * mm, "mid": v(2.33, -6.43) * mm, "end": v(2.26, -6.56) * mm});
            skArc(sketch, "E242.5.14", {"start": v(3.03, -5.13) * mm, "mid": v(3.13, -5.14) * mm, "end": v(3.21, -5.09) * mm});
            skArc(sketch, "E242.5.15", {"start": v(2.37, -6.11) * mm, "mid": v(2.42, -6.2) * mm, "end": v(2.4, -6.3) * mm});
            skArc(sketch, "E242.6.0", {"start": v(1.25, -7.8) * mm, "mid": v(1.36, -7.9) * mm, "end": v(1.5, -8) * mm});
            skArc(sketch, "E242.6.1", {"start": v(1.15, -7.21) * mm, "mid": v(1.11, -7.52) * mm, "end": v(1.25, -7.8) * mm});
            skArc(sketch, "E242.6.2", {"start": v(2.42, -7.74) * mm, "mid": v(2.62, -7.3) * mm, "end": v(2.84, -6.87) * mm});
            skPoint(sketch, "E242.6.3", {"position": v(1.84, -7.5) * mm});
            skArc(sketch, "E242.6.4", {"start": v(1.63, -6.87) * mm, "mid": v(1.79, -6.87) * mm, "end": v(1.95, -6.9) * mm});
            skLineSegment(sketch, "E242.6.5", {"start": v(2.1, -8.65) * mm, "end": v(1.47, -8.46) * mm});
            skArc(sketch, "E242.6.6", {"start": v(2.12, -6.83) * mm, "mid": v(2.19, -6.7) * mm, "end": v(2.26, -6.56) * mm});
            skLineSegment(sketch, "E242.6.7", {"start": v(2.84, -6.87) * mm, "end": v(2.26, -6.56) * mm});
            skArc(sketch, "E242.6.8", {"start": v(1.15, -7.21) * mm, "mid": v(1.34, -6.97) * mm, "end": v(1.63, -6.87) * mm});
            skPoint(sketch, "E242.6.9", {"position": v(2.42, -7.74) * mm});
            skArc(sketch, "E242.6.10", {"start": v(2.08, -7.6) * mm, "mid": v(2.28, -7.14) * mm, "end": v(2.5, -6.7) * mm, "construction": true});
            skArc(sketch, "E242.6.11", {"start": v(2.42, -7.74) * mm, "mid": v(2.25, -8.2) * mm, "end": v(2.1, -8.65) * mm});
            skPoint(sketch, "E242.6.12", {"position": v(2.08, -7.6) * mm});
            skArc(sketch, "E242.6.13", {"start": v(1.56, -8.17) * mm, "mid": v(1.52, -8.32) * mm, "end": v(1.47, -8.46) * mm});
            skArc(sketch, "E242.6.14", {"start": v(1.95, -6.9) * mm, "mid": v(2.05, -6.9) * mm, "end": v(2.12, -6.83) * mm});
            skArc(sketch, "E242.6.15", {"start": v(1.5, -8) * mm, "mid": v(1.56, -8.07) * mm, "end": v(1.56, -8.17) * mm});
            skArc(sketch, "E242.7.0", {"start": v(0.72, -9.86) * mm, "mid": v(0.86, -9.95) * mm, "end": v(1, -10.02) * mm});
            skArc(sketch, "E242.7.1", {"start": v(0.51, -9.31) * mm, "mid": v(0.54, -9.62) * mm, "end": v(0.72, -9.86) * mm});
            skArc(sketch, "E242.7.2", {"start": v(1.86, -9.58) * mm, "mid": v(1.97, -9.11) * mm, "end": v(2.1, -8.65) * mm});
            skPoint(sketch, "E242.7.3", {"position": v(1.25, -9.46) * mm});
            skArc(sketch, "E242.7.4", {"start": v(0.91, -8.89) * mm, "mid": v(1.07, -8.86) * mm, "end": v(1.23, -8.86) * mm});
            skLineSegment(sketch, "E242.7.5", {"start": v(1.72, -10.54) * mm, "end": v(1.07, -10.47) * mm});
            skArc(sketch, "E242.7.6", {"start": v(1.39, -8.74) * mm, "mid": v(1.43, -8.6) * mm, "end": v(1.47, -8.46) * mm});
            skLineSegment(sketch, "E242.7.7", {"start": v(2.1, -8.65) * mm, "end": v(1.47, -8.46) * mm});
            skArc(sketch, "E242.7.8", {"start": v(0.51, -9.31) * mm, "mid": v(0.65, -9.04) * mm, "end": v(0.91, -8.89) * mm});
            skPoint(sketch, "E242.7.9", {"position": v(1.86, -9.58) * mm});
            skArc(sketch, "E242.7.10", {"start": v(1.5, -9.51) * mm, "mid": v(1.6, -9.02) * mm, "end": v(1.74, -8.54) * mm, "construction": true});
            skArc(sketch, "E242.7.11", {"start": v(1.86, -9.58) * mm, "mid": v(1.78, -10.06) * mm, "end": v(1.72, -10.54) * mm});
            skPoint(sketch, "E242.7.12", {"position": v(1.5, -9.51) * mm});
            skArc(sketch, "E242.7.13", {"start": v(1.1, -10.18) * mm, "mid": v(1.09, -10.32) * mm, "end": v(1.07, -10.47) * mm});
            skArc(sketch, "E242.7.14", {"start": v(1.23, -8.86) * mm, "mid": v(1.33, -8.83) * mm, "end": v(1.39, -8.74) * mm});
            skArc(sketch, "E242.7.15", {"start": v(1, -10.02) * mm, "mid": v(1.08, -10.08) * mm, "end": v(1.1, -10.18) * mm});
            skArc(sketch, "E242.8.0", {"start": v(0.6, -12) * mm, "mid": v(0.76, -12.06) * mm, "end": v(0.92, -12.1) * mm});
            skArc(sketch, "E242.8.1", {"start": v(0.3, -11.5) * mm, "mid": v(0.38, -11.8) * mm, "end": v(0.6, -12) * mm});
            skArc(sketch, "E242.8.2", {"start": v(1.68, -11.5) * mm, "mid": v(1.69, -11.02) * mm, "end": v(1.72, -10.54) * mm});
            skPoint(sketch, "E242.8.3", {"position": v(1.05, -11.5) * mm});
            skArc(sketch, "E242.8.4", {"start": v(0.6, -11) * mm, "mid": v(0.76, -10.94) * mm, "end": v(0.92, -10.9) * mm});
            skLineSegment(sketch, "E242.8.5", {"start": v(1.72, -12.46) * mm, "end": v(1.07, -12.53) * mm});
            skArc(sketch, "E242.8.6", {"start": v(1.05, -10.77) * mm, "mid": v(1.06, -10.62) * mm, "end": v(1.07, -10.47) * mm});
            skLineSegment(sketch, "E242.8.7", {"start": v(1.72, -10.54) * mm, "end": v(1.07, -10.47) * mm});
            skArc(sketch, "E242.8.8", {"start": v(0.3, -11.5) * mm, "mid": v(0.38, -11.2) * mm, "end": v(0.6, -11) * mm});
            skPoint(sketch, "E242.8.9", {"position": v(1.68, -11.5) * mm});
            skArc(sketch, "E242.8.10", {"start": v(1.3, -11.5) * mm, "mid": v(1.31, -11) * mm, "end": v(1.35, -10.5) * mm, "construction": true});
            skArc(sketch, "E242.8.11", {"start": v(1.68, -11.5) * mm, "mid": v(1.69, -11.98) * mm, "end": v(1.72, -12.46) * mm});
            skPoint(sketch, "E242.8.12", {"position": v(1.3, -11.5) * mm});
            skArc(sketch, "E242.8.13", {"start": v(1.05, -12.23) * mm, "mid": v(1.06, -12.38) * mm, "end": v(1.07, -12.53) * mm});
            skArc(sketch, "E242.8.14", {"start": v(0.92, -10.9) * mm, "mid": v(1, -10.86) * mm, "end": v(1.05, -10.77) * mm});
            skArc(sketch, "E242.8.15", {"start": v(0.92, -12.1) * mm, "mid": v(1, -12.14) * mm, "end": v(1.05, -12.23) * mm});
            skArc(sketch, "E242.9.0", {"start": v(0.91, -14.11) * mm, "mid": v(1.07, -14.14) * mm, "end": v(1.23, -14.14) * mm});
            skArc(sketch, "E242.9.1", {"start": v(0.51, -13.69) * mm, "mid": v(0.65, -13.96) * mm, "end": v(0.91, -14.11) * mm});
            skArc(sketch, "E242.9.2", {"start": v(1.86, -13.42) * mm, "mid": v(1.78, -12.94) * mm, "end": v(1.72, -12.46) * mm});
            skPoint(sketch, "E242.9.3", {"position": v(1.25, -13.54) * mm});
            skArc(sketch, "E242.9.4", {"start": v(0.72, -13.14) * mm, "mid": v(0.86, -13.05) * mm, "end": v(1, -12.98) * mm});
            skLineSegment(sketch, "E242.9.5", {"start": v(2.1, -14.35) * mm, "end": v(1.47, -14.54) * mm});
            skArc(sketch, "E242.9.6", {"start": v(1.1, -12.82) * mm, "mid": v(1.09, -12.68) * mm, "end": v(1.07, -12.53) * mm});
            skLineSegment(sketch, "E242.9.7", {"start": v(1.72, -12.46) * mm, "end": v(1.07, -12.53) * mm});
            skArc(sketch, "E242.9.8", {"start": v(0.51, -13.69) * mm, "mid": v(0.54, -13.38) * mm, "end": v(0.72, -13.14) * mm});
            skPoint(sketch, "E242.9.9", {"position": v(1.86, -13.42) * mm});
            skArc(sketch, "E242.9.10", {"start": v(1.5, -13.49) * mm, "mid": v(1.41, -13) * mm, "end": v(1.35, -12.5) * mm, "construction": true});
            skArc(sketch, "E242.9.11", {"start": v(1.86, -13.42) * mm, "mid": v(1.97, -13.89) * mm, "end": v(2.1, -14.35) * mm});
            skPoint(sketch, "E242.9.12", {"position": v(1.5, -13.49) * mm});
            skArc(sketch, "E242.9.13", {"start": v(1.39, -14.26) * mm, "mid": v(1.43, -14.4) * mm, "end": v(1.47, -14.54) * mm});
            skArc(sketch, "E242.9.14", {"start": v(1, -12.98) * mm, "mid": v(1.08, -12.92) * mm, "end": v(1.1, -12.82) * mm});
            skArc(sketch, "E242.9.15", {"start": v(1.23, -14.14) * mm, "mid": v(1.33, -14.17) * mm, "end": v(1.39, -14.26) * mm});
            skArc(sketch, "E242.10.0", {"start": v(1.63, -16.13) * mm, "mid": v(1.79, -16.13) * mm, "end": v(1.95, -16.1) * mm});
            skArc(sketch, "E242.10.1", {"start": v(1.15, -15.79) * mm, "mid": v(1.34, -16.03) * mm, "end": v(1.63, -16.13) * mm});
            skArc(sketch, "E242.10.2", {"start": v(2.42, -15.26) * mm, "mid": v(2.25, -14.8) * mm, "end": v(2.1, -14.35) * mm});
            skPoint(sketch, "E242.10.3", {"position": v(1.84, -15.5) * mm});
            skArc(sketch, "E242.10.4", {"start": v(1.25, -15.2) * mm, "mid": v(1.36, -15.1) * mm, "end": v(1.5, -15) * mm});
            skLineSegment(sketch, "E242.10.5", {"start": v(2.84, -16.13) * mm, "end": v(2.26, -16.44) * mm});
            skArc(sketch, "E242.10.6", {"start": v(1.56, -14.83) * mm, "mid": v(1.52, -14.68) * mm, "end": v(1.47, -14.54) * mm});
            skLineSegment(sketch, "E242.10.7", {"start": v(2.1, -14.35) * mm, "end": v(1.47, -14.54) * mm});
            skArc(sketch, "E242.10.8", {"start": v(1.15, -15.79) * mm, "mid": v(1.11, -15.48) * mm, "end": v(1.25, -15.2) * mm});
            skPoint(sketch, "E242.10.9", {"position": v(2.42, -15.26) * mm});
            skArc(sketch, "E242.10.10", {"start": v(2.08, -15.4) * mm, "mid": v(1.9, -14.94) * mm, "end": v(1.74, -14.46) * mm, "construction": true});
            skArc(sketch, "E242.10.11", {"start": v(2.42, -15.26) * mm, "mid": v(2.62, -15.7) * mm, "end": v(2.84, -16.13) * mm});
            skPoint(sketch, "E242.10.12", {"position": v(2.08, -15.4) * mm});
            skArc(sketch, "E242.10.13", {"start": v(2.12, -16.17) * mm, "mid": v(2.19, -16.3) * mm, "end": v(2.26, -16.44) * mm});
            skArc(sketch, "E242.10.14", {"start": v(1.5, -15) * mm, "mid": v(1.56, -14.93) * mm, "end": v(1.56, -14.83) * mm});
            skArc(sketch, "E242.10.15", {"start": v(1.95, -16.1) * mm, "mid": v(2.05, -16.1) * mm, "end": v(2.12, -16.17) * mm});
            skArc(sketch, "E242.11.0", {"start": v(2.72, -17.97) * mm, "mid": v(2.88, -17.93) * mm, "end": v(3.03, -17.87) * mm});
            skArc(sketch, "E242.11.1", {"start": v(2.18, -17.72) * mm, "mid": v(2.42, -17.92) * mm, "end": v(2.72, -17.97) * mm});
            skArc(sketch, "E242.11.2", {"start": v(3.33, -16.96) * mm, "mid": v(3.07, -16.55) * mm, "end": v(2.84, -16.13) * mm});
            skPoint(sketch, "E242.11.3", {"position": v(2.8, -17.3) * mm});
            skArc(sketch, "E242.11.4", {"start": v(2.17, -17.14) * mm, "mid": v(2.26, -17) * mm, "end": v(2.37, -16.89) * mm});
            skLineSegment(sketch, "E242.11.5", {"start": v(3.9, -17.73) * mm, "end": v(3.4, -18.15) * mm});
            skArc(sketch, "E242.11.6", {"start": v(2.4, -16.7) * mm, "mid": v(2.33, -16.57) * mm, "end": v(2.26, -16.44) * mm});
            skLineSegment(sketch, "E242.11.7", {"start": v(2.84, -16.13) * mm, "end": v(2.26, -16.44) * mm});
            skArc(sketch, "E242.11.8", {"start": v(2.18, -17.72) * mm, "mid": v(2.1, -17.43) * mm, "end": v(2.17, -17.14) * mm});
            skPoint(sketch, "E242.11.9", {"position": v(3.33, -16.96) * mm});
            skArc(sketch, "E242.11.10", {"start": v(3.02, -17.17) * mm, "mid": v(2.75, -16.74) * mm, "end": v(2.5, -16.3) * mm, "construction": true});
            skArc(sketch, "E242.11.11", {"start": v(3.33, -16.96) * mm, "mid": v(3.6, -17.35) * mm, "end": v(3.9, -17.73) * mm});
            skPoint(sketch, "E242.11.12", {"position": v(3.02, -17.17) * mm});
            skArc(sketch, "E242.11.13", {"start": v(3.21, -17.91) * mm, "mid": v(3.3, -18.03) * mm, "end": v(3.4, -18.15) * mm});
            skArc(sketch, "E242.11.14", {"start": v(2.37, -16.89) * mm, "mid": v(2.42, -16.8) * mm, "end": v(2.4, -16.7) * mm});
            skArc(sketch, "E242.11.15", {"start": v(3.03, -17.87) * mm, "mid": v(3.13, -17.86) * mm, "end": v(3.21, -17.91) * mm});
            skArc(sketch, "E242.12.0", {"start": v(4.15, -19.55) * mm, "mid": v(4.3, -19.5) * mm, "end": v(4.43, -19.4) * mm});
            skArc(sketch, "E242.12.1", {"start": v(3.58, -19.42) * mm, "mid": v(3.85, -19.57) * mm, "end": v(4.15, -19.55) * mm});
            skArc(sketch, "E242.12.2", {"start": v(4.55, -18.45) * mm, "mid": v(4.22, -18.1) * mm, "end": v(3.9, -17.73) * mm});
            skPoint(sketch, "E242.12.3", {"position": v(4.1, -18.9) * mm});
            skArc(sketch, "E242.12.4", {"start": v(3.45, -18.85) * mm, "mid": v(3.5, -18.7) * mm, "end": v(3.6, -18.57) * mm});
            skLineSegment(sketch, "E242.12.5", {"start": v(5.27, -19.1) * mm, "end": v(4.85, -19.6) * mm});
            skArc(sketch, "E242.12.6", {"start": v(3.6, -18.38) * mm, "mid": v(3.5, -18.26) * mm, "end": v(3.4, -18.15) * mm});
            skLineSegment(sketch, "E242.12.7", {"start": v(3.9, -17.73) * mm, "end": v(3.4, -18.15) * mm});
            skArc(sketch, "E242.12.8", {"start": v(3.58, -19.42) * mm, "mid": v(3.43, -19.15) * mm, "end": v(3.45, -18.85) * mm});
            skPoint(sketch, "E242.12.9", {"position": v(4.55, -18.45) * mm});
            skArc(sketch, "E242.12.10", {"start": v(4.29, -18.71) * mm, "mid": v(3.94, -18.35) * mm, "end": v(3.62, -17.97) * mm, "construction": true});
            skArc(sketch, "E242.12.11", {"start": v(4.55, -18.45) * mm, "mid": v(4.9, -18.78) * mm, "end": v(5.27, -19.1) * mm});
            skPoint(sketch, "E242.12.12", {"position": v(4.29, -18.71) * mm});
            skArc(sketch, "E242.12.13", {"start": v(4.62, -19.4) * mm, "mid": v(4.74, -19.5) * mm, "end": v(4.85, -19.6) * mm});
            skArc(sketch, "E242.12.14", {"start": v(3.6, -18.57) * mm, "mid": v(3.63, -18.47) * mm, "end": v(3.6, -18.38) * mm});
            skArc(sketch, "E242.12.15", {"start": v(4.43, -19.4) * mm, "mid": v(4.53, -19.37) * mm, "end": v(4.62, -19.4) * mm});
            skArc(sketch, "E242.13.0", {"start": v(5.86, -20.83) * mm, "mid": v(6, -20.74) * mm, "end": v(6.11, -20.63) * mm});
            skArc(sketch, "E242.13.1", {"start": v(5.28, -20.82) * mm, "mid": v(5.57, -20.9) * mm, "end": v(5.86, -20.83) * mm});
            skArc(sketch, "E242.13.2", {"start": v(6.04, -19.67) * mm, "mid": v(5.65, -19.4) * mm, "end": v(5.27, -19.1) * mm});
            skPoint(sketch, "E242.13.3", {"position": v(5.7, -20.2) * mm});
            skArc(sketch, "E242.13.4", {"start": v(5.03, -20.28) * mm, "mid": v(5.07, -20.12) * mm, "end": v(5.13, -19.97) * mm});
            skLineSegment(sketch, "E242.13.5", {"start": v(6.87, -20.16) * mm, "end": v(6.56, -20.74) * mm});
            skArc(sketch, "E242.13.6", {"start": v(5.09, -19.79) * mm, "mid": v(4.97, -19.7) * mm, "end": v(4.85, -19.6) * mm});
            skLineSegment(sketch, "E242.13.7", {"start": v(5.27, -19.1) * mm, "end": v(4.85, -19.6) * mm});
            skArc(sketch, "E242.13.8", {"start": v(5.28, -20.82) * mm, "mid": v(5.08, -20.58) * mm, "end": v(5.03, -20.28) * mm});
            skPoint(sketch, "E242.13.9", {"position": v(6.04, -19.67) * mm});
            skArc(sketch, "E242.13.10", {"start": v(5.83, -19.98) * mm, "mid": v(5.42, -19.7) * mm, "end": v(5.03, -19.38) * mm, "construction": true});
            skArc(sketch, "E242.13.11", {"start": v(6.04, -19.67) * mm, "mid": v(6.45, -19.93) * mm, "end": v(6.87, -20.16) * mm});
            skPoint(sketch, "E242.13.12", {"position": v(5.83, -19.98) * mm});
            skArc(sketch, "E242.13.13", {"start": v(6.3, -20.6) * mm, "mid": v(6.43, -20.67) * mm, "end": v(6.56, -20.74) * mm});
            skArc(sketch, "E242.13.14", {"start": v(5.13, -19.97) * mm, "mid": v(5.14, -19.87) * mm, "end": v(5.09, -19.79) * mm});
            skArc(sketch, "E242.13.15", {"start": v(6.11, -20.63) * mm, "mid": v(6.2, -20.58) * mm, "end": v(6.3, -20.6) * mm});
            skArc(sketch, "E242.14.0", {"start": v(7.8, -21.75) * mm, "mid": v(7.9, -21.64) * mm, "end": v(8, -21.5) * mm});
            skArc(sketch, "E242.14.1", {"start": v(7.21, -21.85) * mm, "mid": v(7.52, -21.89) * mm, "end": v(7.8, -21.75) * mm});
            skArc(sketch, "E242.14.2", {"start": v(7.74, -20.58) * mm, "mid": v(7.3, -20.38) * mm, "end": v(6.87, -20.16) * mm});
            skPoint(sketch, "E242.14.3", {"position": v(7.5, -21.16) * mm});
            skArc(sketch, "E242.14.4", {"start": v(6.87, -21.37) * mm, "mid": v(6.87, -21.21) * mm, "end": v(6.9, -21.05) * mm});
            skLineSegment(sketch, "E242.14.5", {"start": v(8.65, -20.9) * mm, "end": v(8.46, -21.53) * mm});
            skArc(sketch, "E242.14.6", {"start": v(6.83, -20.88) * mm, "mid": v(6.7, -20.81) * mm, "end": v(6.56, -20.74) * mm});
            skLineSegment(sketch, "E242.14.7", {"start": v(6.87, -20.16) * mm, "end": v(6.56, -20.74) * mm});
            skArc(sketch, "E242.14.8", {"start": v(7.21, -21.85) * mm, "mid": v(6.97, -21.66) * mm, "end": v(6.87, -21.37) * mm});
            skPoint(sketch, "E242.14.9", {"position": v(7.74, -20.58) * mm});
            skArc(sketch, "E242.14.10", {"start": v(7.6, -20.92) * mm, "mid": v(7.14, -20.72) * mm, "end": v(6.7, -20.5) * mm, "construction": true});
            skArc(sketch, "E242.14.11", {"start": v(7.74, -20.58) * mm, "mid": v(8.2, -20.75) * mm, "end": v(8.65, -20.9) * mm});
            skPoint(sketch, "E242.14.12", {"position": v(7.6, -20.92) * mm});
            skArc(sketch, "E242.14.13", {"start": v(8.17, -21.44) * mm, "mid": v(8.32, -21.48) * mm, "end": v(8.46, -21.53) * mm});
            skArc(sketch, "E242.14.14", {"start": v(6.9, -21.05) * mm, "mid": v(6.9, -20.95) * mm, "end": v(6.83, -20.88) * mm});
            skArc(sketch, "E242.14.15", {"start": v(8, -21.5) * mm, "mid": v(8.07, -21.44) * mm, "end": v(8.17, -21.44) * mm});
            skArc(sketch, "E242.15.0", {"start": v(9.86, -22.28) * mm, "mid": v(9.95, -22.14) * mm, "end": v(10.02, -22) * mm});
            skArc(sketch, "E242.15.1", {"start": v(9.31, -22.49) * mm, "mid": v(9.62, -22.46) * mm, "end": v(9.86, -22.28) * mm});
            skArc(sketch, "E242.15.2", {"start": v(9.58, -21.14) * mm, "mid": v(9.11, -21.03) * mm, "end": v(8.65, -20.9) * mm});
            skPoint(sketch, "E242.15.3", {"position": v(9.46, -21.75) * mm});
            skArc(sketch, "E242.15.4", {"start": v(8.89, -22.09) * mm, "mid": v(8.86, -21.93) * mm, "end": v(8.86, -21.77) * mm});
            skLineSegment(sketch, "E242.15.5", {"start": v(10.54, -21.28) * mm, "end": v(10.47, -21.93) * mm});
            skArc(sketch, "E242.15.6", {"start": v(8.74, -21.61) * mm, "mid": v(8.6, -21.57) * mm, "end": v(8.46, -21.53) * mm});
            skLineSegment(sketch, "E242.15.7", {"start": v(8.65, -20.9) * mm, "end": v(8.46, -21.53) * mm});
            skArc(sketch, "E242.15.8", {"start": v(9.31, -22.49) * mm, "mid": v(9.04, -22.35) * mm, "end": v(8.89, -22.09) * mm});
            skPoint(sketch, "E242.15.9", {"position": v(9.58, -21.14) * mm});
            skArc(sketch, "E242.15.10", {"start": v(9.51, -21.5) * mm, "mid": v(9.02, -21.4) * mm, "end": v(8.54, -21.26) * mm, "construction": true});
            skArc(sketch, "E242.15.11", {"start": v(9.58, -21.14) * mm, "mid": v(10.06, -21.22) * mm, "end": v(10.54, -21.28) * mm});
            skPoint(sketch, "E242.15.12", {"position": v(9.51, -21.5) * mm});
            skArc(sketch, "E242.15.13", {"start": v(10.18, -21.9) * mm, "mid": v(10.32, -21.91) * mm, "end": v(10.47, -21.93) * mm});
            skArc(sketch, "E242.15.14", {"start": v(8.86, -21.77) * mm, "mid": v(8.83, -21.67) * mm, "end": v(8.74, -21.61) * mm});
            skArc(sketch, "E242.15.15", {"start": v(10.02, -22) * mm, "mid": v(10.08, -21.92) * mm, "end": v(10.18, -21.9) * mm});
            skArc(sketch, "E242.16.0", {"start": v(12, -22.4) * mm, "mid": v(12.06, -22.24) * mm, "end": v(12.1, -22.08) * mm});
            skArc(sketch, "E242.16.1", {"start": v(11.5, -22.7) * mm, "mid": v(11.8, -22.62) * mm, "end": v(12, -22.4) * mm});
            skArc(sketch, "E242.16.2", {"start": v(11.5, -21.32) * mm, "mid": v(11.02, -21.31) * mm, "end": v(10.54, -21.28) * mm});
            skPoint(sketch, "E242.16.3", {"position": v(11.5, -21.95) * mm});
            skArc(sketch, "E242.16.4", {"start": v(11, -22.4) * mm, "mid": v(10.94, -22.24) * mm, "end": v(10.9, -22.08) * mm});
            skLineSegment(sketch, "E242.16.5", {"start": v(12.46, -21.28) * mm, "end": v(12.53, -21.93) * mm});
            skArc(sketch, "E242.16.6", {"start": v(10.77, -21.95) * mm, "mid": v(10.62, -21.94) * mm, "end": v(10.47, -21.93) * mm});
            skLineSegment(sketch, "E242.16.7", {"start": v(10.54, -21.28) * mm, "end": v(10.47, -21.93) * mm});
            skArc(sketch, "E242.16.8", {"start": v(11.5, -22.7) * mm, "mid": v(11.2, -22.62) * mm, "end": v(11, -22.4) * mm});
            skPoint(sketch, "E242.16.9", {"position": v(11.5, -21.32) * mm});
            skArc(sketch, "E242.16.10", {"start": v(11.5, -21.7) * mm, "mid": v(11, -21.69) * mm, "end": v(10.5, -21.65) * mm, "construction": true});
            skArc(sketch, "E242.16.11", {"start": v(11.5, -21.32) * mm, "mid": v(11.98, -21.31) * mm, "end": v(12.46, -21.28) * mm});
            skPoint(sketch, "E242.16.12", {"position": v(11.5, -21.7) * mm});
            skArc(sketch, "E242.16.13", {"start": v(12.23, -21.95) * mm, "mid": v(12.38, -21.94) * mm, "end": v(12.53, -21.93) * mm});
            skArc(sketch, "E242.16.14", {"start": v(10.9, -22.08) * mm, "mid": v(10.86, -22) * mm, "end": v(10.77, -21.95) * mm});
            skArc(sketch, "E242.16.15", {"start": v(12.1, -22.08) * mm, "mid": v(12.14, -22) * mm, "end": v(12.23, -21.95) * mm});
            skArc(sketch, "E242.17.0", {"start": v(14.11, -22.09) * mm, "mid": v(14.14, -21.93) * mm, "end": v(14.14, -21.77) * mm});
            skArc(sketch, "E242.17.1", {"start": v(13.69, -22.49) * mm, "mid": v(13.96, -22.35) * mm, "end": v(14.11, -22.09) * mm});
            skArc(sketch, "E242.17.2", {"start": v(13.42, -21.14) * mm, "mid": v(12.94, -21.22) * mm, "end": v(12.46, -21.28) * mm});
            skPoint(sketch, "E242.17.3", {"position": v(13.54, -21.75) * mm});
            skArc(sketch, "E242.17.4", {"start": v(13.14, -22.28) * mm, "mid": v(13.05, -22.14) * mm, "end": v(12.98, -22) * mm});
            skLineSegment(sketch, "E242.17.5", {"start": v(14.35, -20.9) * mm, "end": v(14.54, -21.53) * mm});
            skArc(sketch, "E242.17.6", {"start": v(12.82, -21.9) * mm, "mid": v(12.68, -21.91) * mm, "end": v(12.53, -21.93) * mm});
            skLineSegment(sketch, "E242.17.7", {"start": v(12.46, -21.28) * mm, "end": v(12.53, -21.93) * mm});
            skArc(sketch, "E242.17.8", {"start": v(13.69, -22.49) * mm, "mid": v(13.38, -22.46) * mm, "end": v(13.14, -22.28) * mm});
            skPoint(sketch, "E242.17.9", {"position": v(13.42, -21.14) * mm});
            skArc(sketch, "E242.17.10", {"start": v(13.49, -21.5) * mm, "mid": v(13, -21.59) * mm, "end": v(12.5, -21.65) * mm, "construction": true});
            skArc(sketch, "E242.17.11", {"start": v(13.42, -21.14) * mm, "mid": v(13.89, -21.03) * mm, "end": v(14.35, -20.9) * mm});
            skPoint(sketch, "E242.17.12", {"position": v(13.49, -21.5) * mm});
            skArc(sketch, "E242.17.13", {"start": v(14.26, -21.61) * mm, "mid": v(14.4, -21.57) * mm, "end": v(14.54, -21.53) * mm});
            skArc(sketch, "E242.17.14", {"start": v(12.98, -22) * mm, "mid": v(12.92, -21.92) * mm, "end": v(12.82, -21.9) * mm});
            skArc(sketch, "E242.17.15", {"start": v(14.14, -21.77) * mm, "mid": v(14.17, -21.67) * mm, "end": v(14.26, -21.61) * mm});
            skArc(sketch, "E242.18.0", {"start": v(16.13, -21.37) * mm, "mid": v(16.13, -21.21) * mm, "end": v(16.1, -21.05) * mm});
            skArc(sketch, "E242.18.1", {"start": v(15.79, -21.85) * mm, "mid": v(16.03, -21.66) * mm, "end": v(16.13, -21.37) * mm});
            skArc(sketch, "E242.18.2", {"start": v(15.26, -20.58) * mm, "mid": v(14.8, -20.75) * mm, "end": v(14.35, -20.9) * mm});
            skPoint(sketch, "E242.18.3", {"position": v(15.5, -21.16) * mm});
            skArc(sketch, "E242.18.4", {"start": v(15.2, -21.75) * mm, "mid": v(15.1, -21.64) * mm, "end": v(15, -21.5) * mm});
            skLineSegment(sketch, "E242.18.5", {"start": v(16.13, -20.16) * mm, "end": v(16.44, -20.74) * mm});
            skArc(sketch, "E242.18.6", {"start": v(14.83, -21.44) * mm, "mid": v(14.68, -21.48) * mm, "end": v(14.54, -21.53) * mm});
            skLineSegment(sketch, "E242.18.7", {"start": v(14.35, -20.9) * mm, "end": v(14.54, -21.53) * mm});
            skArc(sketch, "E242.18.8", {"start": v(15.79, -21.85) * mm, "mid": v(15.48, -21.89) * mm, "end": v(15.2, -21.75) * mm});
            skPoint(sketch, "E242.18.9", {"position": v(15.26, -20.58) * mm});
            skArc(sketch, "E242.18.10", {"start": v(15.4, -20.92) * mm, "mid": v(14.94, -21.1) * mm, "end": v(14.46, -21.26) * mm, "construction": true});
            skArc(sketch, "E242.18.11", {"start": v(15.26, -20.58) * mm, "mid": v(15.7, -20.38) * mm, "end": v(16.13, -20.16) * mm});
            skPoint(sketch, "E242.18.12", {"position": v(15.4, -20.92) * mm});
            skArc(sketch, "E242.18.13", {"start": v(16.17, -20.88) * mm, "mid": v(16.3, -20.81) * mm, "end": v(16.44, -20.74) * mm});
            skArc(sketch, "E242.18.14", {"start": v(15, -21.5) * mm, "mid": v(14.93, -21.44) * mm, "end": v(14.83, -21.44) * mm});
            skArc(sketch, "E242.18.15", {"start": v(16.1, -21.05) * mm, "mid": v(16.1, -20.95) * mm, "end": v(16.17, -20.88) * mm});
            skArc(sketch, "E242.19.0", {"start": v(17.97, -20.28) * mm, "mid": v(17.93, -20.12) * mm, "end": v(17.87, -19.97) * mm});
            skArc(sketch, "E242.19.1", {"start": v(17.72, -20.82) * mm, "mid": v(17.92, -20.58) * mm, "end": v(17.97, -20.28) * mm});
            skArc(sketch, "E242.19.2", {"start": v(16.96, -19.67) * mm, "mid": v(16.55, -19.93) * mm, "end": v(16.13, -20.16) * mm});
            skPoint(sketch, "E242.19.3", {"position": v(17.3, -20.2) * mm});
            skArc(sketch, "E242.19.4", {"start": v(17.14, -20.83) * mm, "mid": v(17, -20.74) * mm, "end": v(16.89, -20.63) * mm});
            skLineSegment(sketch, "E242.19.5", {"start": v(17.73, -19.1) * mm, "end": v(18.15, -19.6) * mm});
            skArc(sketch, "E242.19.6", {"start": v(16.7, -20.6) * mm, "mid": v(16.57, -20.67) * mm, "end": v(16.44, -20.74) * mm});
            skLineSegment(sketch, "E242.19.7", {"start": v(16.13, -20.16) * mm, "end": v(16.44, -20.74) * mm});
            skArc(sketch, "E242.19.8", {"start": v(17.72, -20.82) * mm, "mid": v(17.43, -20.9) * mm, "end": v(17.14, -20.83) * mm});
            skPoint(sketch, "E242.19.9", {"position": v(16.96, -19.67) * mm});
            skArc(sketch, "E242.19.10", {"start": v(17.17, -19.98) * mm, "mid": v(16.74, -20.25) * mm, "end": v(16.3, -20.5) * mm, "construction": true});
            skArc(sketch, "E242.19.11", {"start": v(16.96, -19.67) * mm, "mid": v(17.35, -19.4) * mm, "end": v(17.73, -19.1) * mm});
            skPoint(sketch, "E242.19.12", {"position": v(17.17, -19.98) * mm});
            skArc(sketch, "E242.19.13", {"start": v(17.91, -19.79) * mm, "mid": v(18.03, -19.7) * mm, "end": v(18.15, -19.6) * mm});
            skArc(sketch, "E242.19.14", {"start": v(16.89, -20.63) * mm, "mid": v(16.8, -20.58) * mm, "end": v(16.7, -20.6) * mm});
            skArc(sketch, "E242.19.15", {"start": v(17.87, -19.97) * mm, "mid": v(17.86, -19.87) * mm, "end": v(17.91, -19.79) * mm});
            skArc(sketch, "E242.20.0", {"start": v(19.55, -18.85) * mm, "mid": v(19.5, -18.7) * mm, "end": v(19.4, -18.57) * mm});
            skArc(sketch, "E242.20.1", {"start": v(19.42, -19.42) * mm, "mid": v(19.57, -19.15) * mm, "end": v(19.55, -18.85) * mm});
            skArc(sketch, "E242.20.2", {"start": v(18.45, -18.45) * mm, "mid": v(18.1, -18.78) * mm, "end": v(17.73, -19.1) * mm});
            skPoint(sketch, "E242.20.3", {"position": v(18.9, -18.9) * mm});
            skArc(sketch, "E242.20.4", {"start": v(18.85, -19.55) * mm, "mid": v(18.7, -19.5) * mm, "end": v(18.57, -19.4) * mm});
            skLineSegment(sketch, "E242.20.5", {"start": v(19.1, -17.73) * mm, "end": v(19.6, -18.15) * mm});
            skArc(sketch, "E242.20.6", {"start": v(18.38, -19.4) * mm, "mid": v(18.26, -19.5) * mm, "end": v(18.15, -19.6) * mm});
            skLineSegment(sketch, "E242.20.7", {"start": v(17.73, -19.1) * mm, "end": v(18.15, -19.6) * mm});
            skArc(sketch, "E242.20.8", {"start": v(19.42, -19.42) * mm, "mid": v(19.15, -19.57) * mm, "end": v(18.85, -19.55) * mm});
            skPoint(sketch, "E242.20.9", {"position": v(18.45, -18.45) * mm});
            skArc(sketch, "E242.20.10", {"start": v(18.71, -18.71) * mm, "mid": v(18.35, -19.06) * mm, "end": v(17.97, -19.38) * mm, "construction": true});
            skArc(sketch, "E242.20.11", {"start": v(18.45, -18.45) * mm, "mid": v(18.78, -18.1) * mm, "end": v(19.1, -17.73) * mm});
            skPoint(sketch, "E242.20.12", {"position": v(18.71, -18.71) * mm});
            skArc(sketch, "E242.20.13", {"start": v(19.4, -18.38) * mm, "mid": v(19.5, -18.26) * mm, "end": v(19.6, -18.15) * mm});
            skArc(sketch, "E242.20.14", {"start": v(18.57, -19.4) * mm, "mid": v(18.47, -19.37) * mm, "end": v(18.38, -19.4) * mm});
            skArc(sketch, "E242.20.15", {"start": v(19.4, -18.57) * mm, "mid": v(19.37, -18.47) * mm, "end": v(19.4, -18.38) * mm});
            skArc(sketch, "E242.21.0", {"start": v(20.83, -17.14) * mm, "mid": v(20.74, -17) * mm, "end": v(20.63, -16.89) * mm});
            skArc(sketch, "E242.21.1", {"start": v(20.82, -17.72) * mm, "mid": v(20.9, -17.43) * mm, "end": v(20.83, -17.14) * mm});
            skArc(sketch, "E242.21.2", {"start": v(19.67, -16.96) * mm, "mid": v(19.4, -17.35) * mm, "end": v(19.1, -17.73) * mm});
            skPoint(sketch, "E242.21.3", {"position": v(20.2, -17.3) * mm});
            skArc(sketch, "E242.21.4", {"start": v(20.28, -17.97) * mm, "mid": v(20.12, -17.93) * mm, "end": v(19.97, -17.87) * mm});
            skLineSegment(sketch, "E242.21.5", {"start": v(20.16, -16.13) * mm, "end": v(20.74, -16.44) * mm});
            skArc(sketch, "E242.21.6", {"start": v(19.79, -17.91) * mm, "mid": v(19.7, -18.03) * mm, "end": v(19.6, -18.15) * mm});
            skLineSegment(sketch, "E242.21.7", {"start": v(19.1, -17.73) * mm, "end": v(19.6, -18.15) * mm});
            skArc(sketch, "E242.21.8", {"start": v(20.82, -17.72) * mm, "mid": v(20.58, -17.92) * mm, "end": v(20.28, -17.97) * mm});
            skPoint(sketch, "E242.21.9", {"position": v(19.67, -16.96) * mm});
            skArc(sketch, "E242.21.10", {"start": v(19.98, -17.17) * mm, "mid": v(19.7, -17.58) * mm, "end": v(19.38, -17.97) * mm, "construction": true});
            skArc(sketch, "E242.21.11", {"start": v(19.67, -16.96) * mm, "mid": v(19.93, -16.55) * mm, "end": v(20.16, -16.13) * mm});
            skPoint(sketch, "E242.21.12", {"position": v(19.98, -17.17) * mm});
            skArc(sketch, "E242.21.13", {"start": v(20.6, -16.7) * mm, "mid": v(20.67, -16.57) * mm, "end": v(20.74, -16.44) * mm});
            skArc(sketch, "E242.21.14", {"start": v(19.97, -17.87) * mm, "mid": v(19.87, -17.86) * mm, "end": v(19.79, -17.91) * mm});
            skArc(sketch, "E242.21.15", {"start": v(20.63, -16.89) * mm, "mid": v(20.58, -16.8) * mm, "end": v(20.6, -16.7) * mm});
            skArc(sketch, "E242.22.0", {"start": v(21.75, -15.2) * mm, "mid": v(21.64, -15.1) * mm, "end": v(21.5, -15) * mm});
            skArc(sketch, "E242.22.1", {"start": v(21.85, -15.79) * mm, "mid": v(21.89, -15.48) * mm, "end": v(21.75, -15.2) * mm});
            skArc(sketch, "E242.22.2", {"start": v(20.58, -15.26) * mm, "mid": v(20.38, -15.7) * mm, "end": v(20.16, -16.13) * mm});
            skPoint(sketch, "E242.22.3", {"position": v(21.16, -15.5) * mm});
            skArc(sketch, "E242.22.4", {"start": v(21.37, -16.13) * mm, "mid": v(21.21, -16.13) * mm, "end": v(21.05, -16.1) * mm});
            skLineSegment(sketch, "E242.22.5", {"start": v(20.9, -14.35) * mm, "end": v(21.53, -14.54) * mm});
            skArc(sketch, "E242.22.6", {"start": v(20.88, -16.17) * mm, "mid": v(20.81, -16.3) * mm, "end": v(20.74, -16.44) * mm});
            skLineSegment(sketch, "E242.22.7", {"start": v(20.16, -16.13) * mm, "end": v(20.74, -16.44) * mm});
            skArc(sketch, "E242.22.8", {"start": v(21.85, -15.79) * mm, "mid": v(21.66, -16.03) * mm, "end": v(21.37, -16.13) * mm});
            skPoint(sketch, "E242.22.9", {"position": v(20.58, -15.26) * mm});
            skArc(sketch, "E242.22.10", {"start": v(20.92, -15.4) * mm, "mid": v(20.72, -15.86) * mm, "end": v(20.5, -16.3) * mm, "construction": true});
            skArc(sketch, "E242.22.11", {"start": v(20.58, -15.26) * mm, "mid": v(20.75, -14.8) * mm, "end": v(20.9, -14.35) * mm});
            skPoint(sketch, "E242.22.12", {"position": v(20.92, -15.4) * mm});
            skArc(sketch, "E242.22.13", {"start": v(21.44, -14.83) * mm, "mid": v(21.48, -14.68) * mm, "end": v(21.53, -14.54) * mm});
            skArc(sketch, "E242.22.14", {"start": v(21.05, -16.1) * mm, "mid": v(20.95, -16.1) * mm, "end": v(20.88, -16.17) * mm});
            skArc(sketch, "E242.22.15", {"start": v(21.5, -15) * mm, "mid": v(21.44, -14.93) * mm, "end": v(21.44, -14.83) * mm});
            skArc(sketch, "E242.23.0", {"start": v(22.28, -13.14) * mm, "mid": v(22.14, -13.05) * mm, "end": v(22, -12.98) * mm});
            skArc(sketch, "E242.23.1", {"start": v(22.49, -13.69) * mm, "mid": v(22.46, -13.38) * mm, "end": v(22.28, -13.14) * mm});
            skArc(sketch, "E242.23.2", {"start": v(21.14, -13.42) * mm, "mid": v(21.03, -13.89) * mm, "end": v(20.9, -14.35) * mm});
            skPoint(sketch, "E242.23.3", {"position": v(21.75, -13.54) * mm});
            skArc(sketch, "E242.23.4", {"start": v(22.09, -14.11) * mm, "mid": v(21.93, -14.14) * mm, "end": v(21.77, -14.14) * mm});
            skLineSegment(sketch, "E242.23.5", {"start": v(21.28, -12.46) * mm, "end": v(21.93, -12.53) * mm});
            skArc(sketch, "E242.23.6", {"start": v(21.61, -14.26) * mm, "mid": v(21.57, -14.4) * mm, "end": v(21.53, -14.54) * mm});
            skLineSegment(sketch, "E242.23.7", {"start": v(20.9, -14.35) * mm, "end": v(21.53, -14.54) * mm});
            skArc(sketch, "E242.23.8", {"start": v(22.49, -13.69) * mm, "mid": v(22.35, -13.96) * mm, "end": v(22.09, -14.11) * mm});
            skPoint(sketch, "E242.23.9", {"position": v(21.14, -13.42) * mm});
            skArc(sketch, "E242.23.10", {"start": v(21.5, -13.49) * mm, "mid": v(21.4, -13.98) * mm, "end": v(21.26, -14.46) * mm, "construction": true});
            skArc(sketch, "E242.23.11", {"start": v(21.14, -13.42) * mm, "mid": v(21.22, -12.94) * mm, "end": v(21.28, -12.46) * mm});
            skPoint(sketch, "E242.23.12", {"position": v(21.5, -13.49) * mm});
            skArc(sketch, "E242.23.13", {"start": v(21.9, -12.82) * mm, "mid": v(21.91, -12.68) * mm, "end": v(21.93, -12.53) * mm});
            skArc(sketch, "E242.23.14", {"start": v(21.77, -14.14) * mm, "mid": v(21.67, -14.17) * mm, "end": v(21.61, -14.26) * mm});
            skArc(sketch, "E242.23.15", {"start": v(22, -12.98) * mm, "mid": v(21.92, -12.92) * mm, "end": v(21.9, -12.82) * mm});
            skArc(sketch, "E242.24.0", {"start": v(22.4, -11) * mm, "mid": v(22.24, -10.94) * mm, "end": v(22.08, -10.9) * mm});
            skArc(sketch, "E242.24.1", {"start": v(22.7, -11.5) * mm, "mid": v(22.62, -11.2) * mm, "end": v(22.4, -11) * mm});
            skArc(sketch, "E242.24.2", {"start": v(21.32, -11.5) * mm, "mid": v(21.31, -11.98) * mm, "end": v(21.28, -12.46) * mm});
            skPoint(sketch, "E242.24.3", {"position": v(21.95, -11.5) * mm});
            skArc(sketch, "E242.24.4", {"start": v(22.4, -12) * mm, "mid": v(22.24, -12.06) * mm, "end": v(22.08, -12.1) * mm});
            skLineSegment(sketch, "E242.24.5", {"start": v(21.28, -10.54) * mm, "end": v(21.93, -10.47) * mm});
            skArc(sketch, "E242.24.6", {"start": v(21.95, -12.23) * mm, "mid": v(21.94, -12.38) * mm, "end": v(21.93, -12.53) * mm});
            skLineSegment(sketch, "E242.24.7", {"start": v(21.28, -12.46) * mm, "end": v(21.93, -12.53) * mm});
            skArc(sketch, "E242.24.8", {"start": v(22.7, -11.5) * mm, "mid": v(22.62, -11.8) * mm, "end": v(22.4, -12) * mm});
            skPoint(sketch, "E242.24.9", {"position": v(21.32, -11.5) * mm});
            skArc(sketch, "E242.24.10", {"start": v(21.7, -11.5) * mm, "mid": v(21.69, -12) * mm, "end": v(21.65, -12.5) * mm, "construction": true});
            skArc(sketch, "E242.24.11", {"start": v(21.32, -11.5) * mm, "mid": v(21.31, -11.02) * mm, "end": v(21.28, -10.54) * mm});
            skPoint(sketch, "E242.24.12", {"position": v(21.7, -11.5) * mm});
            skArc(sketch, "E242.24.13", {"start": v(21.95, -10.77) * mm, "mid": v(21.94, -10.62) * mm, "end": v(21.93, -10.47) * mm});
            skArc(sketch, "E242.24.14", {"start": v(22.08, -12.1) * mm, "mid": v(22, -12.14) * mm, "end": v(21.95, -12.23) * mm});
            skArc(sketch, "E242.24.15", {"start": v(22.08, -10.9) * mm, "mid": v(22, -10.86) * mm, "end": v(21.95, -10.77) * mm});
            skArc(sketch, "E242.25.0", {"start": v(22.09, -8.89) * mm, "mid": v(21.93, -8.86) * mm, "end": v(21.77, -8.86) * mm});
            skArc(sketch, "E242.25.1", {"start": v(22.49, -9.31) * mm, "mid": v(22.35, -9.04) * mm, "end": v(22.09, -8.89) * mm});
            skArc(sketch, "E242.25.2", {"start": v(21.14, -9.58) * mm, "mid": v(21.22, -10.06) * mm, "end": v(21.28, -10.54) * mm});
            skPoint(sketch, "E242.25.3", {"position": v(21.75, -9.46) * mm});
            skArc(sketch, "E242.25.4", {"start": v(22.28, -9.86) * mm, "mid": v(22.14, -9.95) * mm, "end": v(22, -10.02) * mm});
            skLineSegment(sketch, "E242.25.5", {"start": v(20.9, -8.65) * mm, "end": v(21.53, -8.46) * mm});
            skArc(sketch, "E242.25.6", {"start": v(21.9, -10.18) * mm, "mid": v(21.91, -10.32) * mm, "end": v(21.93, -10.47) * mm});
            skLineSegment(sketch, "E242.25.7", {"start": v(21.28, -10.54) * mm, "end": v(21.93, -10.47) * mm});
            skArc(sketch, "E242.25.8", {"start": v(22.49, -9.31) * mm, "mid": v(22.46, -9.62) * mm, "end": v(22.28, -9.86) * mm});
            skPoint(sketch, "E242.25.9", {"position": v(21.14, -9.58) * mm});
            skArc(sketch, "E242.25.10", {"start": v(21.5, -9.51) * mm, "mid": v(21.59, -10) * mm, "end": v(21.65, -10.5) * mm, "construction": true});
            skArc(sketch, "E242.25.11", {"start": v(21.14, -9.58) * mm, "mid": v(21.03, -9.11) * mm, "end": v(20.9, -8.65) * mm});
            skPoint(sketch, "E242.25.12", {"position": v(21.5, -9.51) * mm});
            skArc(sketch, "E242.25.13", {"start": v(21.61, -8.74) * mm, "mid": v(21.57, -8.6) * mm, "end": v(21.53, -8.46) * mm});
            skArc(sketch, "E242.25.14", {"start": v(22, -10.02) * mm, "mid": v(21.92, -10.08) * mm, "end": v(21.9, -10.18) * mm});
            skArc(sketch, "E242.25.15", {"start": v(21.77, -8.86) * mm, "mid": v(21.67, -8.83) * mm, "end": v(21.61, -8.74) * mm});
            skArc(sketch, "E242.26.0", {"start": v(21.37, -6.87) * mm, "mid": v(21.21, -6.87) * mm, "end": v(21.05, -6.9) * mm});
            skArc(sketch, "E242.26.1", {"start": v(21.85, -7.21) * mm, "mid": v(21.66, -6.97) * mm, "end": v(21.37, -6.87) * mm});
            skArc(sketch, "E242.26.2", {"start": v(20.58, -7.74) * mm, "mid": v(20.75, -8.2) * mm, "end": v(20.9, -8.65) * mm});
            skPoint(sketch, "E242.26.3", {"position": v(21.16, -7.5) * mm});
            skArc(sketch, "E242.26.4", {"start": v(21.75, -7.8) * mm, "mid": v(21.64, -7.9) * mm, "end": v(21.5, -8) * mm});
            skLineSegment(sketch, "E242.26.5", {"start": v(20.16, -6.87) * mm, "end": v(20.74, -6.56) * mm});
            skArc(sketch, "E242.26.6", {"start": v(21.44, -8.17) * mm, "mid": v(21.48, -8.32) * mm, "end": v(21.53, -8.46) * mm});
            skLineSegment(sketch, "E242.26.7", {"start": v(20.9, -8.65) * mm, "end": v(21.53, -8.46) * mm});
            skArc(sketch, "E242.26.8", {"start": v(21.85, -7.21) * mm, "mid": v(21.89, -7.52) * mm, "end": v(21.75, -7.8) * mm});
            skPoint(sketch, "E242.26.9", {"position": v(20.58, -7.74) * mm});
            skArc(sketch, "E242.26.10", {"start": v(20.92, -7.6) * mm, "mid": v(21.1, -8.06) * mm, "end": v(21.26, -8.54) * mm, "construction": true});
            skArc(sketch, "E242.26.11", {"start": v(20.58, -7.74) * mm, "mid": v(20.38, -7.3) * mm, "end": v(20.16, -6.87) * mm});
            skPoint(sketch, "E242.26.12", {"position": v(20.92, -7.6) * mm});
            skArc(sketch, "E242.26.13", {"start": v(20.88, -6.83) * mm, "mid": v(20.81, -6.7) * mm, "end": v(20.74, -6.56) * mm});
            skArc(sketch, "E242.26.14", {"start": v(21.5, -8) * mm, "mid": v(21.44, -8.07) * mm, "end": v(21.44, -8.17) * mm});
            skArc(sketch, "E242.26.15", {"start": v(21.05, -6.9) * mm, "mid": v(20.95, -6.9) * mm, "end": v(20.88, -6.83) * mm});
            skArc(sketch, "E242.27.0", {"start": v(20.28, -5.03) * mm, "mid": v(20.12, -5.07) * mm, "end": v(19.97, -5.13) * mm});
            skArc(sketch, "E242.27.1", {"start": v(20.82, -5.28) * mm, "mid": v(20.58, -5.08) * mm, "end": v(20.28, -5.03) * mm});
            skArc(sketch, "E242.27.2", {"start": v(19.67, -6.04) * mm, "mid": v(19.93, -6.45) * mm, "end": v(20.16, -6.87) * mm});
            skPoint(sketch, "E242.27.3", {"position": v(20.2, -5.7) * mm});
            skArc(sketch, "E242.27.4", {"start": v(20.83, -5.86) * mm, "mid": v(20.74, -6) * mm, "end": v(20.63, -6.11) * mm});
            skLineSegment(sketch, "E242.27.5", {"start": v(19.1, -5.27) * mm, "end": v(19.6, -4.85) * mm});
            skArc(sketch, "E242.27.6", {"start": v(20.6, -6.3) * mm, "mid": v(20.67, -6.43) * mm, "end": v(20.74, -6.56) * mm});
            skLineSegment(sketch, "E242.27.7", {"start": v(20.16, -6.87) * mm, "end": v(20.74, -6.56) * mm});
            skArc(sketch, "E242.27.8", {"start": v(20.82, -5.28) * mm, "mid": v(20.9, -5.57) * mm, "end": v(20.83, -5.86) * mm});
            skPoint(sketch, "E242.27.9", {"position": v(19.67, -6.04) * mm});
            skArc(sketch, "E242.27.10", {"start": v(19.98, -5.83) * mm, "mid": v(20.25, -6.26) * mm, "end": v(20.5, -6.7) * mm, "construction": true});
            skArc(sketch, "E242.27.11", {"start": v(19.67, -6.04) * mm, "mid": v(19.4, -5.65) * mm, "end": v(19.1, -5.27) * mm});
            skPoint(sketch, "E242.27.12", {"position": v(19.98, -5.83) * mm});
            skArc(sketch, "E242.27.13", {"start": v(19.79, -5.09) * mm, "mid": v(19.7, -4.97) * mm, "end": v(19.6, -4.85) * mm});
            skArc(sketch, "E242.27.14", {"start": v(20.63, -6.11) * mm, "mid": v(20.58, -6.2) * mm, "end": v(20.6, -6.3) * mm});
            skArc(sketch, "E242.27.15", {"start": v(19.97, -5.13) * mm, "mid": v(19.87, -5.14) * mm, "end": v(19.79, -5.09) * mm});
            skArc(sketch, "E242.28.0", {"start": v(18.85, -3.45) * mm, "mid": v(18.7, -3.5) * mm, "end": v(18.57, -3.6) * mm});
            skArc(sketch, "E242.28.1", {"start": v(19.42, -3.58) * mm, "mid": v(19.15, -3.43) * mm, "end": v(18.85, -3.45) * mm});
            skArc(sketch, "E242.28.2", {"start": v(18.45, -4.55) * mm, "mid": v(18.78, -4.9) * mm, "end": v(19.1, -5.27) * mm});
            skPoint(sketch, "E242.28.3", {"position": v(18.9, -4.1) * mm});
            skArc(sketch, "E242.28.4", {"start": v(19.55, -4.15) * mm, "mid": v(19.5, -4.3) * mm, "end": v(19.4, -4.43) * mm});
            skLineSegment(sketch, "E242.28.5", {"start": v(17.73, -3.9) * mm, "end": v(18.15, -3.4) * mm});
            skArc(sketch, "E242.28.6", {"start": v(19.4, -4.62) * mm, "mid": v(19.5, -4.74) * mm, "end": v(19.6, -4.85) * mm});
            skLineSegment(sketch, "E242.28.7", {"start": v(19.1, -5.27) * mm, "end": v(19.6, -4.85) * mm});
            skArc(sketch, "E242.28.8", {"start": v(19.42, -3.58) * mm, "mid": v(19.57, -3.85) * mm, "end": v(19.55, -4.15) * mm});
            skPoint(sketch, "E242.28.9", {"position": v(18.45, -4.55) * mm});
            skArc(sketch, "E242.28.10", {"start": v(18.71, -4.29) * mm, "mid": v(19.06, -4.65) * mm, "end": v(19.38, -5.03) * mm, "construction": true});
            skArc(sketch, "E242.28.11", {"start": v(18.45, -4.55) * mm, "mid": v(18.1, -4.22) * mm, "end": v(17.73, -3.9) * mm});
            skPoint(sketch, "E242.28.12", {"position": v(18.71, -4.29) * mm});
            skArc(sketch, "E242.28.13", {"start": v(18.38, -3.6) * mm, "mid": v(18.26, -3.5) * mm, "end": v(18.15, -3.4) * mm});
            skArc(sketch, "E242.28.14", {"start": v(19.4, -4.43) * mm, "mid": v(19.37, -4.53) * mm, "end": v(19.4, -4.62) * mm});
            skArc(sketch, "E242.28.15", {"start": v(18.57, -3.6) * mm, "mid": v(18.47, -3.63) * mm, "end": v(18.38, -3.6) * mm});
            skArc(sketch, "E242.29.0", {"start": v(17.14, -2.17) * mm, "mid": v(17, -2.26) * mm, "end": v(16.89, -2.37) * mm});
            skArc(sketch, "E242.29.1", {"start": v(17.72, -2.18) * mm, "mid": v(17.43, -2.1) * mm, "end": v(17.14, -2.17) * mm});
            skArc(sketch, "E242.29.2", {"start": v(16.96, -3.33) * mm, "mid": v(17.35, -3.6) * mm, "end": v(17.73, -3.9) * mm});
            skPoint(sketch, "E242.29.3", {"position": v(17.3, -2.8) * mm});
            skArc(sketch, "E242.29.4", {"start": v(17.97, -2.72) * mm, "mid": v(17.93, -2.88) * mm, "end": v(17.87, -3.03) * mm});
            skLineSegment(sketch, "E242.29.5", {"start": v(16.13, -2.84) * mm, "end": v(16.44, -2.26) * mm});
            skArc(sketch, "E242.29.6", {"start": v(17.91, -3.21) * mm, "mid": v(18.03, -3.3) * mm, "end": v(18.15, -3.4) * mm});
            skLineSegment(sketch, "E242.29.7", {"start": v(17.73, -3.9) * mm, "end": v(18.15, -3.4) * mm});
            skArc(sketch, "E242.29.8", {"start": v(17.72, -2.18) * mm, "mid": v(17.92, -2.42) * mm, "end": v(17.97, -2.72) * mm});
            skPoint(sketch, "E242.29.9", {"position": v(16.96, -3.33) * mm});
            skArc(sketch, "E242.29.10", {"start": v(17.17, -3.02) * mm, "mid": v(17.58, -3.3) * mm, "end": v(17.97, -3.62) * mm, "construction": true});
            skArc(sketch, "E242.29.11", {"start": v(16.96, -3.33) * mm, "mid": v(16.55, -3.07) * mm, "end": v(16.13, -2.84) * mm});
            skPoint(sketch, "E242.29.12", {"position": v(17.17, -3.02) * mm});
            skArc(sketch, "E242.29.13", {"start": v(16.7, -2.4) * mm, "mid": v(16.57, -2.33) * mm, "end": v(16.44, -2.26) * mm});
            skArc(sketch, "E242.29.14", {"start": v(17.87, -3.03) * mm, "mid": v(17.86, -3.13) * mm, "end": v(17.91, -3.21) * mm});
            skArc(sketch, "E242.29.15", {"start": v(16.89, -2.37) * mm, "mid": v(16.8, -2.42) * mm, "end": v(16.7, -2.4) * mm});
            skArc(sketch, "E242.30.0", {"start": v(15.2, -1.25) * mm, "mid": v(15.1, -1.36) * mm, "end": v(15, -1.5) * mm});
            skArc(sketch, "E242.30.1", {"start": v(15.79, -1.15) * mm, "mid": v(15.48, -1.11) * mm, "end": v(15.2, -1.25) * mm});
            skArc(sketch, "E242.30.2", {"start": v(15.26, -2.42) * mm, "mid": v(15.7, -2.62) * mm, "end": v(16.13, -2.84) * mm});
            skPoint(sketch, "E242.30.3", {"position": v(15.5, -1.84) * mm});
            skArc(sketch, "E242.30.4", {"start": v(16.13, -1.63) * mm, "mid": v(16.13, -1.79) * mm, "end": v(16.1, -1.95) * mm});
            skLineSegment(sketch, "E242.30.5", {"start": v(14.35, -2.1) * mm, "end": v(14.54, -1.47) * mm});
            skArc(sketch, "E242.30.6", {"start": v(16.17, -2.12) * mm, "mid": v(16.3, -2.19) * mm, "end": v(16.44, -2.26) * mm});
            skLineSegment(sketch, "E242.30.7", {"start": v(16.13, -2.84) * mm, "end": v(16.44, -2.26) * mm});
            skArc(sketch, "E242.30.8", {"start": v(15.79, -1.15) * mm, "mid": v(16.03, -1.34) * mm, "end": v(16.13, -1.63) * mm});
            skPoint(sketch, "E242.30.9", {"position": v(15.26, -2.42) * mm});
            skArc(sketch, "E242.30.10", {"start": v(15.4, -2.08) * mm, "mid": v(15.86, -2.28) * mm, "end": v(16.3, -2.5) * mm, "construction": true});
            skArc(sketch, "E242.30.11", {"start": v(15.26, -2.42) * mm, "mid": v(14.8, -2.25) * mm, "end": v(14.35, -2.1) * mm});
            skPoint(sketch, "E242.30.12", {"position": v(15.4, -2.08) * mm});
            skArc(sketch, "E242.30.13", {"start": v(14.83, -1.56) * mm, "mid": v(14.68, -1.52) * mm, "end": v(14.54, -1.47) * mm});
            skArc(sketch, "E242.30.14", {"start": v(16.1, -1.95) * mm, "mid": v(16.1, -2.05) * mm, "end": v(16.17, -2.12) * mm});
            skArc(sketch, "E242.30.15", {"start": v(15, -1.5) * mm, "mid": v(14.93, -1.56) * mm, "end": v(14.83, -1.56) * mm});
            skArc(sketch, "E242.31.0", {"start": v(13.14, -0.72) * mm, "mid": v(13.05, -0.86) * mm, "end": v(12.98, -1) * mm});
            skArc(sketch, "E242.31.1", {"start": v(13.69, -0.51) * mm, "mid": v(13.38, -0.54) * mm, "end": v(13.14, -0.72) * mm});
            skArc(sketch, "E242.31.2", {"start": v(13.42, -1.86) * mm, "mid": v(13.89, -1.97) * mm, "end": v(14.35, -2.1) * mm});
            skPoint(sketch, "E242.31.3", {"position": v(13.54, -1.25) * mm});
            skArc(sketch, "E242.31.4", {"start": v(14.11, -0.91) * mm, "mid": v(14.14, -1.07) * mm, "end": v(14.14, -1.23) * mm});
            skArc(sketch, "E242.31.6", {"start": v(14.26, -1.39) * mm, "mid": v(14.4, -1.43) * mm, "end": v(14.54, -1.47) * mm});
            skLineSegment(sketch, "E242.31.7", {"start": v(14.35, -2.1) * mm, "end": v(14.54, -1.47) * mm});
            skArc(sketch, "E242.31.8", {"start": v(13.69, -0.51) * mm, "mid": v(13.96, -0.65) * mm, "end": v(14.11, -0.91) * mm});
            skPoint(sketch, "E242.31.9", {"position": v(13.42, -1.86) * mm});
            skArc(sketch, "E242.31.10", {"start": v(13.49, -1.5) * mm, "mid": v(13.98, -1.6) * mm, "end": v(14.46, -1.74) * mm, "construction": true});
            skArc(sketch, "E242.31.11", {"start": v(13.42, -1.86) * mm, "mid": v(12.94, -1.78) * mm, "end": v(12.46, -1.72) * mm});
            skPoint(sketch, "E242.31.12", {"position": v(13.49, -1.5) * mm});
            skArc(sketch, "E242.31.13", {"start": v(12.82, -1.1) * mm, "mid": v(12.68, -1.09) * mm, "end": v(12.53, -1.07) * mm});
            skArc(sketch, "E242.31.14", {"start": v(14.14, -1.23) * mm, "mid": v(14.17, -1.33) * mm, "end": v(14.26, -1.39) * mm});
            skArc(sketch, "E242.31.15", {"start": v(12.98, -1) * mm, "mid": v(12.92, -1.08) * mm, "end": v(12.82, -1.1) * mm});
            skArc(sketch, "E243.0", {"start": v(4.25, -18.75) * mm, "mid": v(18.75, -18.75) * mm, "end": v(18.75, -4.25) * mm});
            skSolve(sketch);
        }
        {
            var Q0;
            Q0 = qSketchRegion(id + "F37", true);
            extrude(context, id + "F38", {"entities" : qUnion([Q0]), "operationType" : NewBodyOperationType.REMOVE, "endBound" : BoundingType.SYMMETRIC, "oppositeDirection" : true, "depth" : 6.5 * mm});
        }
        {
            var Q0;
            Q0=qCreatedBy(makeId("Top.planeOp"),FACE);
            var sketch = newSketch(context, id + "F39", { "sketchPlane" : qUnion([Q0])});
            skLineSegment(sketch, "E244.bottom", {"start": v(-46.89, -45.69) * mm, "end": v(-10.89, -45.69) * mm});
            skLineSegment(sketch, "E244.top", {"start": v(-46.89, -11.69) * mm, "end": v(-10.89, -11.69) * mm});
            skLineSegment(sketch, "E244.left", {"start": v(-46.89, -45.69) * mm, "end": v(-46.89, -11.69) * mm});
            skLineSegment(sketch, "E244.right", {"start": v(-10.89, -45.69) * mm, "end": v(-10.89, -11.69) * mm});
            skLineSegment(sketch, "E245", {"start": v(-46.89, -28.69) * mm, "end": v(-10.89, -28.69) * mm, "construction": true});
            skLineSegment(sketch, "E246", {"start": v(-28.89, -45.69) * mm, "end": v(-28.89, -11.69) * mm, "construction": true});
            skCircle(sketch, "E247", {"center": v(-42.89, -41.69) * mm, "radius": 1.55 * mm});
            skCircle(sketch, "E248.MirrorC", {"center": v(-42.89, -15.69) * mm, "radius": 1.55 * mm});
            skCircle(sketch, "E249.MirrorC", {"center": v(-14.89, -41.69) * mm, "radius": 1.55 * mm});
            skCircle(sketch, "E250.MirrorC", {"center": v(-14.89, -15.69) * mm, "radius": 1.55 * mm});
            skPoint(sketch, "E251", {"position": v(-36.89, -28.69) * mm});
            skPoint(sketch, "E252.MirrorP", {"position": v(-20.89, -28.69) * mm});
            skSolve(sketch);
        }
        {
            var Q0;
            Q0 = qSketchRegion(id + "F39", true);
            extrude(context, id + "F40", {"entities" : qUnion([Q0]), "depth" : 15 * mm});
        }
        {
            var Q0;
            Q0=makeQuery(id+"F40.opExtrude","SWEPT_FACE",FACE,{"disambiguationData":[OSD([sQuery(id+"F39.wireOp",EDGE,"E244.right")])]});
            var sketch = newSketch(context, id + "F41", { "sketchPlane" : qUnion([Q0])});
            skPoint(sketch, "E253", {"position": v(-28.69, 15) * mm});
            skArc(sketch, "E254", {"start": v(-38.94, 15) * mm, "mid": v(-28.69, 4.75) * mm, "end": v(-18.44, 15) * mm});
            skLineSegment(sketch, "E255", {"start": v(-38.94, 15) * mm, "end": v(-18.44, 15) * mm});
            skSolve(sketch);
        }
        {
            var Q0;
            Q0 = qSketchRegion(id + "F41", true);
            var Q1;
            Q1=makeQuery(id+"F40.opExtrude","SWEPT_FACE",FACE,{"disambiguationData":[OSD([sQuery(id+"F39.wireOp",EDGE,"E244.left")])]});
            extrude(context, id + "F42", {"entities" : qUnion([Q0]), "operationType" : NewBodyOperationType.REMOVE, "endBound" : BoundingType.UP_TO_SURFACE, "oppositeDirection" : true, "endBoundEntityFace" : qUnion([Q1]), "depth" : 25 * mm});
        }
        {
            var Q0;
            Q0=makeQuery(id+"F40.opExtrude","SWEPT_FACE",FACE,{"disambiguationData":[OSD([sQuery(id+"F39.wireOp",EDGE,"E244.right")])]});
            var Q1;
            Q1=sQuery(id+"F39.wireOp",VERTEX,"E252.MirrorP");
            cPlane(context, id + "F43", {"entities" : qUnion([Q0, Q1]), "cplaneType" : CPlaneType.PLANE_POINT, "offset" : 150 * mm, "width" : 150 * mm, "height" : 150 * mm});
        }
        {
            var Q0;
            Q0=qCreatedBy(id+"F43.planeOp",FACE);
            var sketch = newSketch(context, id + "F44", { "sketchPlane" : qUnion([Q0])});
            skLineSegment(sketch, "E256", {"start": v(-28.69, 26.2) * mm, "end": v(-28.69, 24.82) * mm, "construction": true});
            skArc(sketch, "E257", {"start": v(-28.69, 26.2) * mm, "mid": v(-28.4, 26.12) * mm, "end": v(-28.19, 25.9) * mm});
            skArc(sketch, "E258", {"start": v(-28.19, 25.9) * mm, "mid": v(-28.13, 25.74) * mm, "end": v(-28.1, 25.58) * mm});
            skArc(sketch, "E259", {"start": v(-28.1, 25.58) * mm, "mid": v(-28.05, 25.5) * mm, "end": v(-27.96, 25.45) * mm});
            skPoint(sketch, "E260", {"position": v(-28.69, 24.82) * mm});
            skPoint(sketch, "E261", {"position": v(-28.69, 25.45) * mm});
            skPoint(sketch, "E262", {"position": v(-28.69, 25.2) * mm});
            skArc(sketch, "E263", {"start": v(-28.69, 25.2) * mm, "mid": v(-28.19, 25.19) * mm, "end": v(-27.69, 25.15) * mm, "construction": true});
            skLineSegment(sketch, "E264", {"start": v(-27.73, 24.78) * mm, "end": v(-27.66, 25.43) * mm});
            skArc(sketch, "E265", {"start": v(-27.96, 25.45) * mm, "mid": v(-27.8, 25.44) * mm, "end": v(-27.66, 25.43) * mm});
            skArc(sketch, "E266", {"start": v(-28.69, 24.82) * mm, "mid": v(-28.2, 24.81) * mm, "end": v(-27.73, 24.78) * mm});
            skArc(sketch, "E267.MirrorCS", {"start": v(-28.69, 26.2) * mm, "mid": v(-28.98, 26.12) * mm, "end": v(-29.19, 25.9) * mm});
            skArc(sketch, "E268.MirrorCS", {"start": v(-29.19, 25.9) * mm, "mid": v(-29.25, 25.74) * mm, "end": v(-29.28, 25.58) * mm});
            skArc(sketch, "E269.MirrorCS", {"start": v(-29.28, 25.58) * mm, "mid": v(-29.33, 25.5) * mm, "end": v(-29.42, 25.45) * mm});
            skArc(sketch, "E270.MirrorCS", {"start": v(-29.42, 25.45) * mm, "mid": v(-29.57, 25.44) * mm, "end": v(-29.72, 25.43) * mm});
            skLineSegment(sketch, "E271.MirrorCS", {"start": v(-29.65, 24.78) * mm, "end": v(-29.72, 25.43) * mm});
            skArc(sketch, "E272.MirrorCS", {"start": v(-28.69, 24.82) * mm, "mid": v(-29.17, 24.81) * mm, "end": v(-29.65, 24.78) * mm});
            skArc(sketch, "E273.1.0", {"start": v(-31.3, 25.59) * mm, "mid": v(-31.33, 25.43) * mm, "end": v(-31.33, 25.27) * mm});
            skArc(sketch, "E273.1.1", {"start": v(-30.87, 25.99) * mm, "mid": v(-31.15, 25.85) * mm, "end": v(-31.3, 25.59) * mm});
            skArc(sketch, "E273.1.2", {"start": v(-30.6, 24.64) * mm, "mid": v(-30.13, 24.72) * mm, "end": v(-29.65, 24.78) * mm});
            skPoint(sketch, "E273.1.3", {"position": v(-30.73, 25.25) * mm});
            skArc(sketch, "E273.1.4", {"start": v(-30.32, 25.78) * mm, "mid": v(-30.24, 25.64) * mm, "end": v(-30.17, 25.5) * mm});
            skLineSegment(sketch, "E273.1.5", {"start": v(-31.54, 24.4) * mm, "end": v(-31.73, 25.03) * mm});
            skArc(sketch, "E273.1.6", {"start": v(-30.01, 25.4) * mm, "mid": v(-29.86, 25.41) * mm, "end": v(-29.72, 25.43) * mm});
            skArc(sketch, "E273.1.8", {"start": v(-30.87, 25.99) * mm, "mid": v(-30.57, 25.96) * mm, "end": v(-30.32, 25.78) * mm});
            skPoint(sketch, "E273.1.9", {"position": v(-30.6, 24.64) * mm});
            skArc(sketch, "E273.1.10", {"start": v(-30.68, 25) * mm, "mid": v(-30.19, 25.09) * mm, "end": v(-29.69, 25.15) * mm, "construction": true});
            skArc(sketch, "E273.1.11", {"start": v(-30.6, 24.64) * mm, "mid": v(-31.08, 24.53) * mm, "end": v(-31.54, 24.4) * mm});
            skPoint(sketch, "E273.1.12", {"position": v(-30.68, 25) * mm});
            skArc(sketch, "E273.1.13", {"start": v(-31.44, 25.11) * mm, "mid": v(-31.59, 25.07) * mm, "end": v(-31.73, 25.03) * mm});
            skArc(sketch, "E273.1.14", {"start": v(-30.17, 25.5) * mm, "mid": v(-30.11, 25.42) * mm, "end": v(-30.01, 25.4) * mm});
            skArc(sketch, "E273.1.15", {"start": v(-31.33, 25.27) * mm, "mid": v(-31.36, 25.17) * mm, "end": v(-31.44, 25.11) * mm});
            skArc(sketch, "E273.2.0", {"start": v(-33.32, 24.87) * mm, "mid": v(-33.31, 24.71) * mm, "end": v(-33.29, 24.55) * mm});
            skArc(sketch, "E273.2.1", {"start": v(-32.98, 25.35) * mm, "mid": v(-33.22, 25.16) * mm, "end": v(-33.32, 24.87) * mm});
            skArc(sketch, "E273.2.2", {"start": v(-32.45, 24.08) * mm, "mid": v(-32, 24.25) * mm, "end": v(-31.54, 24.4) * mm});
            skPoint(sketch, "E273.2.3", {"position": v(-32.69, 24.66) * mm});
            skArc(sketch, "E273.2.4", {"start": v(-32.4, 25.25) * mm, "mid": v(-32.28, 25.14) * mm, "end": v(-32.2, 25) * mm});
            skLineSegment(sketch, "E273.2.5", {"start": v(-33.32, 23.66) * mm, "end": v(-33.63, 24.24) * mm});
            skArc(sketch, "E273.2.6", {"start": v(-32.01, 24.94) * mm, "mid": v(-31.87, 24.98) * mm, "end": v(-31.73, 25.03) * mm});
            skLineSegment(sketch, "E273.2.7", {"start": v(-31.54, 24.4) * mm, "end": v(-31.73, 25.03) * mm});
            skArc(sketch, "E273.2.8", {"start": v(-32.98, 25.35) * mm, "mid": v(-32.67, 25.39) * mm, "end": v(-32.4, 25.25) * mm});
            skPoint(sketch, "E273.2.9", {"position": v(-32.45, 24.08) * mm});
            skArc(sketch, "E273.2.10", {"start": v(-32.6, 24.42) * mm, "mid": v(-32.12, 24.6) * mm, "end": v(-31.65, 24.76) * mm, "construction": true});
            skArc(sketch, "E273.2.11", {"start": v(-32.45, 24.08) * mm, "mid": v(-32.89, 23.88) * mm, "end": v(-33.32, 23.66) * mm});
            skPoint(sketch, "E273.2.12", {"position": v(-32.6, 24.42) * mm});
            skArc(sketch, "E273.2.13", {"start": v(-33.36, 24.38) * mm, "mid": v(-33.5, 24.31) * mm, "end": v(-33.63, 24.24) * mm});
            skArc(sketch, "E273.2.14", {"start": v(-32.2, 25) * mm, "mid": v(-32.12, 24.94) * mm, "end": v(-32.01, 24.94) * mm});
            skArc(sketch, "E273.2.15", {"start": v(-33.29, 24.55) * mm, "mid": v(-33.3, 24.45) * mm, "end": v(-33.36, 24.38) * mm});
            skArc(sketch, "E273.3.0", {"start": v(-35.15, 23.78) * mm, "mid": v(-35.12, 23.62) * mm, "end": v(-35.06, 23.47) * mm});
            skArc(sketch, "E273.3.1", {"start": v(-34.91, 24.32) * mm, "mid": v(-35.11, 24.08) * mm, "end": v(-35.15, 23.78) * mm});
            skArc(sketch, "E273.3.2", {"start": v(-34.15, 23.17) * mm, "mid": v(-33.74, 23.43) * mm, "end": v(-33.32, 23.66) * mm});
            skPoint(sketch, "E273.3.3", {"position": v(-34.5, 23.7) * mm});
            skArc(sketch, "E273.3.4", {"start": v(-34.33, 24.33) * mm, "mid": v(-34.2, 24.24) * mm, "end": v(-34.08, 24.13) * mm});
            skLineSegment(sketch, "E273.3.5", {"start": v(-34.92, 22.6) * mm, "end": v(-35.34, 23.1) * mm});
            skArc(sketch, "E273.3.6", {"start": v(-33.89, 24.1) * mm, "mid": v(-33.76, 24.17) * mm, "end": v(-33.63, 24.24) * mm});
            skLineSegment(sketch, "E273.3.7", {"start": v(-33.32, 23.66) * mm, "end": v(-33.63, 24.24) * mm});
            skArc(sketch, "E273.3.8", {"start": v(-34.91, 24.32) * mm, "mid": v(-34.62, 24.4) * mm, "end": v(-34.33, 24.33) * mm});
            skPoint(sketch, "E273.3.9", {"position": v(-34.15, 23.17) * mm});
            skArc(sketch, "E273.3.10", {"start": v(-34.36, 23.48) * mm, "mid": v(-33.93, 23.75) * mm, "end": v(-33.5, 24) * mm, "construction": true});
            skArc(sketch, "E273.3.11", {"start": v(-34.15, 23.17) * mm, "mid": v(-34.54, 22.9) * mm, "end": v(-34.92, 22.6) * mm});
            skPoint(sketch, "E273.3.12", {"position": v(-34.36, 23.48) * mm});
            skArc(sketch, "E273.3.13", {"start": v(-35.1, 23.29) * mm, "mid": v(-35.22, 23.2) * mm, "end": v(-35.34, 23.1) * mm});
            skArc(sketch, "E273.3.14", {"start": v(-34.08, 24.13) * mm, "mid": v(-33.99, 24.08) * mm, "end": v(-33.89, 24.1) * mm});
            skArc(sketch, "E273.3.15", {"start": v(-35.06, 23.47) * mm, "mid": v(-35.05, 23.37) * mm, "end": v(-35.1, 23.29) * mm});
            skArc(sketch, "E273.4.0", {"start": v(-36.74, 22.35) * mm, "mid": v(-36.68, 22.2) * mm, "end": v(-36.6, 22.07) * mm});
            skArc(sketch, "E273.4.1", {"start": v(-36.61, 22.92) * mm, "mid": v(-36.76, 22.65) * mm, "end": v(-36.74, 22.35) * mm});
            skArc(sketch, "E273.4.2", {"start": v(-35.64, 21.95) * mm, "mid": v(-35.29, 22.28) * mm, "end": v(-34.92, 22.6) * mm});
            skPoint(sketch, "E273.4.3", {"position": v(-36.08, 22.4) * mm});
            skArc(sketch, "E273.4.4", {"start": v(-36.04, 23.05) * mm, "mid": v(-35.89, 23) * mm, "end": v(-35.75, 22.9) * mm});
            skLineSegment(sketch, "E273.4.5", {"start": v(-36.28, 21.23) * mm, "end": v(-36.79, 21.65) * mm});
            skArc(sketch, "E273.4.6", {"start": v(-35.56, 22.9) * mm, "mid": v(-35.45, 23) * mm, "end": v(-35.34, 23.1) * mm});
            skLineSegment(sketch, "E273.4.7", {"start": v(-34.92, 22.6) * mm, "end": v(-35.34, 23.1) * mm});
            skArc(sketch, "E273.4.8", {"start": v(-36.61, 22.92) * mm, "mid": v(-36.34, 23.07) * mm, "end": v(-36.04, 23.05) * mm});
            skPoint(sketch, "E273.4.9", {"position": v(-35.64, 21.95) * mm});
            skArc(sketch, "E273.4.10", {"start": v(-35.9, 22.21) * mm, "mid": v(-35.54, 22.56) * mm, "end": v(-35.16, 22.88) * mm, "construction": true});
            skArc(sketch, "E273.4.11", {"start": v(-35.64, 21.95) * mm, "mid": v(-35.97, 21.6) * mm, "end": v(-36.28, 21.23) * mm});
            skPoint(sketch, "E273.4.12", {"position": v(-35.9, 22.21) * mm});
            skArc(sketch, "E273.4.13", {"start": v(-36.6, 21.88) * mm, "mid": v(-36.7, 21.76) * mm, "end": v(-36.79, 21.65) * mm});
            skArc(sketch, "E273.4.14", {"start": v(-35.75, 22.9) * mm, "mid": v(-35.66, 22.87) * mm, "end": v(-35.56, 22.9) * mm});
            skArc(sketch, "E273.4.15", {"start": v(-36.6, 22.07) * mm, "mid": v(-36.56, 21.97) * mm, "end": v(-36.6, 21.88) * mm});
            skArc(sketch, "E273.5.0", {"start": v(-38.02, 20.64) * mm, "mid": v(-37.93, 20.5) * mm, "end": v(-37.82, 20.39) * mm});
            skArc(sketch, "E273.5.1", {"start": v(-38, 21.22) * mm, "mid": v(-38.1, 20.93) * mm, "end": v(-38.02, 20.64) * mm});
            skArc(sketch, "E273.5.2", {"start": v(-36.86, 20.46) * mm, "mid": v(-36.58, 20.85) * mm, "end": v(-36.28, 21.23) * mm});
            skPoint(sketch, "E273.5.3", {"position": v(-37.38, 20.8) * mm});
            skArc(sketch, "E273.5.4", {"start": v(-37.47, 21.47) * mm, "mid": v(-37.31, 21.43) * mm, "end": v(-37.16, 21.37) * mm});
            skLineSegment(sketch, "E273.5.5", {"start": v(-37.35, 19.63) * mm, "end": v(-37.93, 19.94) * mm});
            skArc(sketch, "E273.5.6", {"start": v(-36.98, 21.41) * mm, "mid": v(-36.88, 21.53) * mm, "end": v(-36.79, 21.65) * mm});
            skLineSegment(sketch, "E273.5.7", {"start": v(-36.28, 21.23) * mm, "end": v(-36.79, 21.65) * mm});
            skArc(sketch, "E273.5.8", {"start": v(-38, 21.22) * mm, "mid": v(-37.77, 21.42) * mm, "end": v(-37.47, 21.47) * mm});
            skPoint(sketch, "E273.5.9", {"position": v(-36.86, 20.46) * mm});
            skArc(sketch, "E273.5.10", {"start": v(-37.17, 20.67) * mm, "mid": v(-36.88, 21.08) * mm, "end": v(-36.57, 21.47) * mm, "construction": true});
            skArc(sketch, "E273.5.11", {"start": v(-36.86, 20.46) * mm, "mid": v(-37.11, 20.05) * mm, "end": v(-37.35, 19.63) * mm});
            skPoint(sketch, "E273.5.12", {"position": v(-37.17, 20.67) * mm});
            skArc(sketch, "E273.5.13", {"start": v(-37.79, 20.2) * mm, "mid": v(-37.86, 20.07) * mm, "end": v(-37.93, 19.94) * mm});
            skArc(sketch, "E273.5.14", {"start": v(-37.16, 21.37) * mm, "mid": v(-37.06, 21.36) * mm, "end": v(-36.98, 21.41) * mm});
            skArc(sketch, "E273.5.15", {"start": v(-37.82, 20.39) * mm, "mid": v(-37.77, 20.3) * mm, "end": v(-37.79, 20.2) * mm});
            skArc(sketch, "E273.6.0", {"start": v(-38.94, 18.7) * mm, "mid": v(-38.83, 18.6) * mm, "end": v(-38.7, 18.5) * mm});
            skArc(sketch, "E273.6.1", {"start": v(-39.04, 19.29) * mm, "mid": v(-39.07, 18.98) * mm, "end": v(-38.94, 18.7) * mm});
            skArc(sketch, "E273.6.2", {"start": v(-37.76, 18.76) * mm, "mid": v(-37.57, 19.2) * mm, "end": v(-37.35, 19.63) * mm});
            skPoint(sketch, "E273.6.3", {"position": v(-38.35, 19) * mm});
            skArc(sketch, "E273.6.4", {"start": v(-38.56, 19.63) * mm, "mid": v(-38.4, 19.63) * mm, "end": v(-38.24, 19.6) * mm});
            skLineSegment(sketch, "E273.6.5", {"start": v(-38.09, 17.85) * mm, "end": v(-38.72, 18.04) * mm});
            skArc(sketch, "E273.6.6", {"start": v(-38.07, 19.67) * mm, "mid": v(-38, 19.8) * mm, "end": v(-37.93, 19.94) * mm});
            skLineSegment(sketch, "E273.6.7", {"start": v(-37.35, 19.63) * mm, "end": v(-37.93, 19.94) * mm});
            skArc(sketch, "E273.6.8", {"start": v(-39.04, 19.29) * mm, "mid": v(-38.85, 19.53) * mm, "end": v(-38.56, 19.63) * mm});
            skPoint(sketch, "E273.6.9", {"position": v(-37.76, 18.76) * mm});
            skArc(sketch, "E273.6.10", {"start": v(-38.11, 18.9) * mm, "mid": v(-37.9, 19.36) * mm, "end": v(-37.68, 19.8) * mm, "construction": true});
            skArc(sketch, "E273.6.11", {"start": v(-37.76, 18.76) * mm, "mid": v(-37.94, 18.3) * mm, "end": v(-38.09, 17.85) * mm});
            skPoint(sketch, "E273.6.12", {"position": v(-38.11, 18.9) * mm});
            skArc(sketch, "E273.6.13", {"start": v(-38.63, 18.33) * mm, "mid": v(-38.67, 18.18) * mm, "end": v(-38.72, 18.04) * mm});
            skArc(sketch, "E273.6.14", {"start": v(-38.24, 19.6) * mm, "mid": v(-38.14, 19.6) * mm, "end": v(-38.07, 19.67) * mm});
            skArc(sketch, "E273.6.15", {"start": v(-38.7, 18.5) * mm, "mid": v(-38.63, 18.43) * mm, "end": v(-38.63, 18.33) * mm});
            skArc(sketch, "E273.7.0", {"start": v(-39.47, 16.64) * mm, "mid": v(-39.33, 16.55) * mm, "end": v(-39.18, 16.48) * mm});
            skArc(sketch, "E273.7.1", {"start": v(-39.68, 17.19) * mm, "mid": v(-39.65, 16.88) * mm, "end": v(-39.47, 16.64) * mm});
            skArc(sketch, "E273.7.2", {"start": v(-38.32, 16.92) * mm, "mid": v(-38.22, 17.39) * mm, "end": v(-38.09, 17.85) * mm});
            skPoint(sketch, "E273.7.3", {"position": v(-38.94, 17.04) * mm});
            skArc(sketch, "E273.7.4", {"start": v(-39.27, 17.61) * mm, "mid": v(-39.12, 17.64) * mm, "end": v(-38.95, 17.64) * mm});
            skLineSegment(sketch, "E273.7.5", {"start": v(-38.47, 15.96) * mm, "end": v(-39.12, 16.03) * mm});
            skArc(sketch, "E273.7.6", {"start": v(-38.8, 17.76) * mm, "mid": v(-38.76, 17.9) * mm, "end": v(-38.72, 18.04) * mm});
            skLineSegment(sketch, "E273.7.7", {"start": v(-38.09, 17.85) * mm, "end": v(-38.72, 18.04) * mm});
            skArc(sketch, "E273.7.8", {"start": v(-39.68, 17.19) * mm, "mid": v(-39.54, 17.46) * mm, "end": v(-39.27, 17.61) * mm});
            skPoint(sketch, "E273.7.9", {"position": v(-38.32, 16.92) * mm});
            skArc(sketch, "E273.7.10", {"start": v(-38.7, 16.99) * mm, "mid": v(-38.58, 17.48) * mm, "end": v(-38.45, 17.96) * mm, "construction": true});
            skArc(sketch, "E273.7.11", {"start": v(-38.32, 16.92) * mm, "mid": v(-38.4, 16.44) * mm, "end": v(-38.47, 15.96) * mm});
            skPoint(sketch, "E273.7.12", {"position": v(-38.7, 16.99) * mm});
            skArc(sketch, "E273.7.13", {"start": v(-39.08, 16.32) * mm, "mid": v(-39.1, 16.18) * mm, "end": v(-39.12, 16.03) * mm});
            skArc(sketch, "E273.7.14", {"start": v(-38.95, 17.64) * mm, "mid": v(-38.86, 17.67) * mm, "end": v(-38.8, 17.76) * mm});
            skArc(sketch, "E273.7.15", {"start": v(-39.18, 16.48) * mm, "mid": v(-39.1, 16.42) * mm, "end": v(-39.08, 16.32) * mm});
            skArc(sketch, "E273.8.0", {"start": v(-39.58, 14.5) * mm, "mid": v(-39.43, 14.44) * mm, "end": v(-39.27, 14.4) * mm});
            skArc(sketch, "E273.8.1", {"start": v(-39.9, 15) * mm, "mid": v(-39.8, 14.7) * mm, "end": v(-39.58, 14.5) * mm});
            skArc(sketch, "E273.8.2", {"start": v(-38.51, 15) * mm, "mid": v(-38.5, 15.48) * mm, "end": v(-38.47, 15.96) * mm});
            skPoint(sketch, "E273.8.3", {"position": v(-39.14, 15) * mm});
            skArc(sketch, "E273.8.4", {"start": v(-39.58, 15.5) * mm, "mid": v(-39.43, 15.56) * mm, "end": v(-39.27, 15.6) * mm});
            skLineSegment(sketch, "E273.8.5", {"start": v(-38.47, 14.04) * mm, "end": v(-39.12, 13.97) * mm});
            skArc(sketch, "E273.8.6", {"start": v(-39.14, 15.73) * mm, "mid": v(-39.13, 15.88) * mm, "end": v(-39.12, 16.03) * mm});
            skLineSegment(sketch, "E273.8.7", {"start": v(-38.47, 15.96) * mm, "end": v(-39.12, 16.03) * mm});
            skArc(sketch, "E273.8.8", {"start": v(-39.9, 15) * mm, "mid": v(-39.8, 15.3) * mm, "end": v(-39.58, 15.5) * mm});
            skPoint(sketch, "E273.8.9", {"position": v(-38.51, 15) * mm});
            skArc(sketch, "E273.8.10", {"start": v(-38.89, 15) * mm, "mid": v(-38.88, 15.5) * mm, "end": v(-38.84, 16) * mm, "construction": true});
            skArc(sketch, "E273.8.11", {"start": v(-38.51, 15) * mm, "mid": v(-38.5, 14.52) * mm, "end": v(-38.47, 14.04) * mm});
            skPoint(sketch, "E273.8.12", {"position": v(-38.89, 15) * mm});
            skArc(sketch, "E273.8.13", {"start": v(-39.14, 14.27) * mm, "mid": v(-39.13, 14.12) * mm, "end": v(-39.12, 13.97) * mm});
            skArc(sketch, "E273.8.14", {"start": v(-39.27, 15.6) * mm, "mid": v(-39.18, 15.64) * mm, "end": v(-39.14, 15.73) * mm});
            skArc(sketch, "E273.8.15", {"start": v(-39.27, 14.4) * mm, "mid": v(-39.18, 14.36) * mm, "end": v(-39.14, 14.27) * mm});
            skArc(sketch, "E273.9.0", {"start": v(-39.27, 12.39) * mm, "mid": v(-39.12, 12.36) * mm, "end": v(-38.95, 12.36) * mm});
            skArc(sketch, "E273.9.1", {"start": v(-39.68, 12.81) * mm, "mid": v(-39.54, 12.54) * mm, "end": v(-39.27, 12.39) * mm});
            skArc(sketch, "E273.9.2", {"start": v(-38.32, 13.08) * mm, "mid": v(-38.4, 13.56) * mm, "end": v(-38.47, 14.04) * mm});
            skPoint(sketch, "E273.9.3", {"position": v(-38.94, 12.96) * mm});
            skArc(sketch, "E273.9.4", {"start": v(-39.47, 13.36) * mm, "mid": v(-39.33, 13.45) * mm, "end": v(-39.18, 13.52) * mm});
            skLineSegment(sketch, "E273.9.5", {"start": v(-38.09, 12.15) * mm, "end": v(-38.72, 11.96) * mm});
            skArc(sketch, "E273.9.6", {"start": v(-39.08, 13.68) * mm, "mid": v(-39.1, 13.82) * mm, "end": v(-39.12, 13.97) * mm});
            skLineSegment(sketch, "E273.9.7", {"start": v(-38.47, 14.04) * mm, "end": v(-39.12, 13.97) * mm});
            skArc(sketch, "E273.9.8", {"start": v(-39.68, 12.81) * mm, "mid": v(-39.65, 13.12) * mm, "end": v(-39.47, 13.36) * mm});
            skPoint(sketch, "E273.9.9", {"position": v(-38.32, 13.08) * mm});
            skArc(sketch, "E273.9.10", {"start": v(-38.7, 13.01) * mm, "mid": v(-38.78, 13.5) * mm, "end": v(-38.84, 14) * mm, "construction": true});
            skArc(sketch, "E273.9.11", {"start": v(-38.32, 13.08) * mm, "mid": v(-38.22, 12.61) * mm, "end": v(-38.09, 12.15) * mm});
            skPoint(sketch, "E273.9.12", {"position": v(-38.7, 13.01) * mm});
            skArc(sketch, "E273.9.13", {"start": v(-38.8, 12.24) * mm, "mid": v(-38.76, 12.1) * mm, "end": v(-38.72, 11.96) * mm});
            skArc(sketch, "E273.9.14", {"start": v(-39.18, 13.52) * mm, "mid": v(-39.1, 13.58) * mm, "end": v(-39.08, 13.68) * mm});
            skArc(sketch, "E273.9.15", {"start": v(-38.95, 12.36) * mm, "mid": v(-38.86, 12.33) * mm, "end": v(-38.8, 12.24) * mm});
            skArc(sketch, "E273.10.0", {"start": v(-38.56, 10.37) * mm, "mid": v(-38.4, 10.37) * mm, "end": v(-38.24, 10.4) * mm});
            skArc(sketch, "E273.10.1", {"start": v(-39.04, 10.71) * mm, "mid": v(-38.85, 10.47) * mm, "end": v(-38.56, 10.37) * mm});
            skArc(sketch, "E273.10.2", {"start": v(-37.76, 11.24) * mm, "mid": v(-37.94, 11.7) * mm, "end": v(-38.09, 12.15) * mm});
            skPoint(sketch, "E273.10.3", {"position": v(-38.35, 11) * mm});
            skArc(sketch, "E273.10.4", {"start": v(-38.94, 11.3) * mm, "mid": v(-38.83, 11.4) * mm, "end": v(-38.7, 11.5) * mm});
            skLineSegment(sketch, "E273.10.5", {"start": v(-37.35, 10.37) * mm, "end": v(-37.93, 10.06) * mm});
            skArc(sketch, "E273.10.6", {"start": v(-38.63, 11.67) * mm, "mid": v(-38.67, 11.82) * mm, "end": v(-38.72, 11.96) * mm});
            skLineSegment(sketch, "E273.10.7", {"start": v(-38.09, 12.15) * mm, "end": v(-38.72, 11.96) * mm});
            skArc(sketch, "E273.10.8", {"start": v(-39.04, 10.71) * mm, "mid": v(-39.07, 11.02) * mm, "end": v(-38.94, 11.3) * mm});
            skPoint(sketch, "E273.10.9", {"position": v(-37.76, 11.24) * mm});
            skArc(sketch, "E273.10.10", {"start": v(-38.11, 11.1) * mm, "mid": v(-38.3, 11.56) * mm, "end": v(-38.45, 12.04) * mm, "construction": true});
            skArc(sketch, "E273.10.11", {"start": v(-37.76, 11.24) * mm, "mid": v(-37.57, 10.8) * mm, "end": v(-37.35, 10.37) * mm});
            skPoint(sketch, "E273.10.12", {"position": v(-38.11, 11.1) * mm});
            skArc(sketch, "E273.10.13", {"start": v(-38.07, 10.33) * mm, "mid": v(-38, 10.2) * mm, "end": v(-37.93, 10.06) * mm});
            skArc(sketch, "E273.10.14", {"start": v(-38.7, 11.5) * mm, "mid": v(-38.63, 11.57) * mm, "end": v(-38.63, 11.67) * mm});
            skArc(sketch, "E273.10.15", {"start": v(-38.24, 10.4) * mm, "mid": v(-38.14, 10.4) * mm, "end": v(-38.07, 10.33) * mm});
            skArc(sketch, "E273.11.0", {"start": v(-37.47, 8.53) * mm, "mid": v(-37.31, 8.57) * mm, "end": v(-37.16, 8.63) * mm});
            skArc(sketch, "E273.11.1", {"start": v(-38, 8.78) * mm, "mid": v(-37.77, 8.58) * mm, "end": v(-37.47, 8.53) * mm});
            skArc(sketch, "E273.11.2", {"start": v(-36.86, 9.54) * mm, "mid": v(-37.11, 9.95) * mm, "end": v(-37.35, 10.37) * mm});
            skPoint(sketch, "E273.11.3", {"position": v(-37.38, 9.2) * mm});
            skArc(sketch, "E273.11.4", {"start": v(-38.02, 9.36) * mm, "mid": v(-37.93, 9.5) * mm, "end": v(-37.82, 9.61) * mm});
            skLineSegment(sketch, "E273.11.5", {"start": v(-36.28, 8.77) * mm, "end": v(-36.79, 8.35) * mm});
            skArc(sketch, "E273.11.6", {"start": v(-37.79, 9.8) * mm, "mid": v(-37.86, 9.93) * mm, "end": v(-37.93, 10.06) * mm});
            skLineSegment(sketch, "E273.11.7", {"start": v(-37.35, 10.37) * mm, "end": v(-37.93, 10.06) * mm});
            skArc(sketch, "E273.11.8", {"start": v(-38, 8.78) * mm, "mid": v(-38.1, 9.07) * mm, "end": v(-38.02, 9.36) * mm});
            skPoint(sketch, "E273.11.9", {"position": v(-36.86, 9.54) * mm});
            skArc(sketch, "E273.11.10", {"start": v(-37.17, 9.33) * mm, "mid": v(-37.44, 9.76) * mm, "end": v(-37.68, 10.2) * mm, "construction": true});
            skArc(sketch, "E273.11.11", {"start": v(-36.86, 9.54) * mm, "mid": v(-36.58, 9.15) * mm, "end": v(-36.28, 8.77) * mm});
            skPoint(sketch, "E273.11.12", {"position": v(-37.17, 9.33) * mm});
            skArc(sketch, "E273.11.13", {"start": v(-36.98, 8.59) * mm, "mid": v(-36.88, 8.47) * mm, "end": v(-36.79, 8.35) * mm});
            skArc(sketch, "E273.11.14", {"start": v(-37.82, 9.61) * mm, "mid": v(-37.77, 9.7) * mm, "end": v(-37.79, 9.8) * mm});
            skArc(sketch, "E273.11.15", {"start": v(-37.16, 8.63) * mm, "mid": v(-37.06, 8.64) * mm, "end": v(-36.98, 8.59) * mm});
            skArc(sketch, "E273.12.0", {"start": v(-36.04, 6.95) * mm, "mid": v(-35.89, 7) * mm, "end": v(-35.75, 7.1) * mm});
            skArc(sketch, "E273.12.1", {"start": v(-36.61, 7.08) * mm, "mid": v(-36.34, 6.93) * mm, "end": v(-36.04, 6.95) * mm});
            skArc(sketch, "E273.12.2", {"start": v(-35.64, 8.05) * mm, "mid": v(-35.97, 8.4) * mm, "end": v(-36.28, 8.77) * mm});
            skPoint(sketch, "E273.12.3", {"position": v(-36.08, 7.6) * mm});
            skArc(sketch, "E273.12.4", {"start": v(-36.74, 7.65) * mm, "mid": v(-36.68, 7.8) * mm, "end": v(-36.6, 7.93) * mm});
            skLineSegment(sketch, "E273.12.5", {"start": v(-34.92, 7.4) * mm, "end": v(-35.34, 6.9) * mm});
            skArc(sketch, "E273.12.6", {"start": v(-36.6, 8.12) * mm, "mid": v(-36.7, 8.24) * mm, "end": v(-36.79, 8.35) * mm});
            skLineSegment(sketch, "E273.12.7", {"start": v(-36.28, 8.77) * mm, "end": v(-36.79, 8.35) * mm});
            skArc(sketch, "E273.12.8", {"start": v(-36.61, 7.08) * mm, "mid": v(-36.76, 7.35) * mm, "end": v(-36.74, 7.65) * mm});
            skPoint(sketch, "E273.12.9", {"position": v(-35.64, 8.05) * mm});
            skArc(sketch, "E273.12.10", {"start": v(-35.9, 7.79) * mm, "mid": v(-36.25, 8.15) * mm, "end": v(-36.57, 8.53) * mm, "construction": true});
            skArc(sketch, "E273.12.11", {"start": v(-35.64, 8.05) * mm, "mid": v(-35.29, 7.72) * mm, "end": v(-34.92, 7.4) * mm});
            skPoint(sketch, "E273.12.12", {"position": v(-35.9, 7.79) * mm});
            skArc(sketch, "E273.12.13", {"start": v(-35.56, 7.1) * mm, "mid": v(-35.45, 7) * mm, "end": v(-35.34, 6.9) * mm});
            skArc(sketch, "E273.12.14", {"start": v(-36.6, 7.93) * mm, "mid": v(-36.56, 8.03) * mm, "end": v(-36.6, 8.12) * mm});
            skArc(sketch, "E273.12.15", {"start": v(-35.75, 7.1) * mm, "mid": v(-35.66, 7.13) * mm, "end": v(-35.56, 7.1) * mm});
            skArc(sketch, "E273.13.0", {"start": v(-34.33, 5.67) * mm, "mid": v(-34.2, 5.76) * mm, "end": v(-34.08, 5.87) * mm});
            skArc(sketch, "E273.13.1", {"start": v(-34.91, 5.68) * mm, "mid": v(-34.62, 5.6) * mm, "end": v(-34.33, 5.67) * mm});
            skArc(sketch, "E273.13.2", {"start": v(-34.15, 6.83) * mm, "mid": v(-34.54, 7.1) * mm, "end": v(-34.92, 7.4) * mm});
            skPoint(sketch, "E273.13.3", {"position": v(-34.5, 6.3) * mm});
            skArc(sketch, "E273.13.4", {"start": v(-35.15, 6.22) * mm, "mid": v(-35.12, 6.38) * mm, "end": v(-35.06, 6.53) * mm});
            skLineSegment(sketch, "E273.13.5", {"start": v(-33.32, 6.34) * mm, "end": v(-33.63, 5.76) * mm});
            skArc(sketch, "E273.13.6", {"start": v(-35.1, 6.71) * mm, "mid": v(-35.22, 6.8) * mm, "end": v(-35.34, 6.9) * mm});
            skLineSegment(sketch, "E273.13.7", {"start": v(-34.92, 7.4) * mm, "end": v(-35.34, 6.9) * mm});
            skArc(sketch, "E273.13.8", {"start": v(-34.91, 5.68) * mm, "mid": v(-35.11, 5.92) * mm, "end": v(-35.15, 6.22) * mm});
            skPoint(sketch, "E273.13.9", {"position": v(-34.15, 6.83) * mm});
            skArc(sketch, "E273.13.10", {"start": v(-34.36, 6.52) * mm, "mid": v(-34.76, 6.8) * mm, "end": v(-35.16, 7.12) * mm, "construction": true});
            skArc(sketch, "E273.13.11", {"start": v(-34.15, 6.83) * mm, "mid": v(-33.74, 6.57) * mm, "end": v(-33.32, 6.34) * mm});
            skPoint(sketch, "E273.13.12", {"position": v(-34.36, 6.52) * mm});
            skArc(sketch, "E273.13.13", {"start": v(-33.89, 5.9) * mm, "mid": v(-33.76, 5.83) * mm, "end": v(-33.63, 5.76) * mm});
            skArc(sketch, "E273.13.14", {"start": v(-35.06, 6.53) * mm, "mid": v(-35.05, 6.63) * mm, "end": v(-35.1, 6.71) * mm});
            skArc(sketch, "E273.13.15", {"start": v(-34.08, 5.87) * mm, "mid": v(-33.99, 5.92) * mm, "end": v(-33.89, 5.9) * mm});
            skArc(sketch, "E273.14.0", {"start": v(-32.4, 4.75) * mm, "mid": v(-32.28, 4.86) * mm, "end": v(-32.2, 5) * mm});
            skArc(sketch, "E273.14.1", {"start": v(-32.98, 4.65) * mm, "mid": v(-32.67, 4.61) * mm, "end": v(-32.4, 4.75) * mm});
            skArc(sketch, "E273.14.2", {"start": v(-32.45, 5.92) * mm, "mid": v(-32.89, 6.12) * mm, "end": v(-33.32, 6.34) * mm});
            skPoint(sketch, "E273.14.3", {"position": v(-32.69, 5.34) * mm});
            skArc(sketch, "E273.14.4", {"start": v(-33.32, 5.13) * mm, "mid": v(-33.31, 5.29) * mm, "end": v(-33.29, 5.45) * mm});
            skLineSegment(sketch, "E273.14.5", {"start": v(-31.54, 5.6) * mm, "end": v(-31.73, 4.97) * mm});
            skArc(sketch, "E273.14.6", {"start": v(-33.36, 5.62) * mm, "mid": v(-33.5, 5.69) * mm, "end": v(-33.63, 5.76) * mm});
            skLineSegment(sketch, "E273.14.7", {"start": v(-33.32, 6.34) * mm, "end": v(-33.63, 5.76) * mm});
            skArc(sketch, "E273.14.8", {"start": v(-32.98, 4.65) * mm, "mid": v(-33.22, 4.84) * mm, "end": v(-33.32, 5.13) * mm});
            skPoint(sketch, "E273.14.9", {"position": v(-32.45, 5.92) * mm});
            skArc(sketch, "E273.14.10", {"start": v(-32.6, 5.58) * mm, "mid": v(-33.05, 5.78) * mm, "end": v(-33.5, 6) * mm, "construction": true});
            skArc(sketch, "E273.14.11", {"start": v(-32.45, 5.92) * mm, "mid": v(-32, 5.75) * mm, "end": v(-31.54, 5.6) * mm});
            skPoint(sketch, "E273.14.12", {"position": v(-32.6, 5.58) * mm});
            skArc(sketch, "E273.14.13", {"start": v(-32.01, 5.06) * mm, "mid": v(-31.87, 5.02) * mm, "end": v(-31.73, 4.97) * mm});
            skArc(sketch, "E273.14.14", {"start": v(-33.29, 5.45) * mm, "mid": v(-33.3, 5.55) * mm, "end": v(-33.36, 5.62) * mm});
            skArc(sketch, "E273.14.15", {"start": v(-32.2, 5) * mm, "mid": v(-32.12, 5.06) * mm, "end": v(-32.01, 5.06) * mm});
            skArc(sketch, "E273.15.0", {"start": v(-30.32, 4.22) * mm, "mid": v(-30.24, 4.36) * mm, "end": v(-30.17, 4.5) * mm});
            skArc(sketch, "E273.15.1", {"start": v(-30.87, 4.01) * mm, "mid": v(-30.57, 4.04) * mm, "end": v(-30.32, 4.22) * mm});
            skArc(sketch, "E273.15.2", {"start": v(-30.6, 5.36) * mm, "mid": v(-31.08, 5.47) * mm, "end": v(-31.54, 5.6) * mm});
            skPoint(sketch, "E273.15.3", {"position": v(-30.73, 4.75) * mm});
            skArc(sketch, "E273.15.4", {"start": v(-31.3, 4.41) * mm, "mid": v(-31.33, 4.57) * mm, "end": v(-31.33, 4.73) * mm});
            skLineSegment(sketch, "E273.15.5", {"start": v(-29.65, 5.22) * mm, "end": v(-29.72, 4.57) * mm});
            skArc(sketch, "E273.15.6", {"start": v(-31.44, 4.89) * mm, "mid": v(-31.59, 4.93) * mm, "end": v(-31.73, 4.97) * mm});
            skLineSegment(sketch, "E273.15.7", {"start": v(-31.54, 5.6) * mm, "end": v(-31.73, 4.97) * mm});
            skArc(sketch, "E273.15.8", {"start": v(-30.87, 4.01) * mm, "mid": v(-31.15, 4.15) * mm, "end": v(-31.3, 4.41) * mm});
            skPoint(sketch, "E273.15.9", {"position": v(-30.6, 5.36) * mm});
            skArc(sketch, "E273.15.10", {"start": v(-30.68, 5) * mm, "mid": v(-31.17, 5.1) * mm, "end": v(-31.65, 5.24) * mm, "construction": true});
            skArc(sketch, "E273.15.11", {"start": v(-30.6, 5.36) * mm, "mid": v(-30.13, 5.28) * mm, "end": v(-29.65, 5.22) * mm});
            skPoint(sketch, "E273.15.12", {"position": v(-30.68, 5) * mm});
            skArc(sketch, "E273.15.13", {"start": v(-30.01, 4.6) * mm, "mid": v(-29.86, 4.59) * mm, "end": v(-29.72, 4.57) * mm});
            skArc(sketch, "E273.15.14", {"start": v(-31.33, 4.73) * mm, "mid": v(-31.36, 4.83) * mm, "end": v(-31.44, 4.89) * mm});
            skArc(sketch, "E273.15.15", {"start": v(-30.17, 4.5) * mm, "mid": v(-30.11, 4.58) * mm, "end": v(-30.01, 4.6) * mm});
            skArc(sketch, "E273.16.0", {"start": v(-28.19, 4.1) * mm, "mid": v(-28.13, 4.26) * mm, "end": v(-28.1, 4.42) * mm});
            skArc(sketch, "E273.16.1", {"start": v(-28.69, 3.8) * mm, "mid": v(-28.4, 3.88) * mm, "end": v(-28.19, 4.1) * mm});
            skArc(sketch, "E273.16.2", {"start": v(-28.69, 5.18) * mm, "mid": v(-29.17, 5.19) * mm, "end": v(-29.65, 5.22) * mm});
            skPoint(sketch, "E273.16.3", {"position": v(-28.69, 4.55) * mm});
            skArc(sketch, "E273.16.4", {"start": v(-29.19, 4.1) * mm, "mid": v(-29.25, 4.26) * mm, "end": v(-29.28, 4.42) * mm});
            skLineSegment(sketch, "E273.16.5", {"start": v(-27.73, 5.22) * mm, "end": v(-27.66, 4.57) * mm});
            skArc(sketch, "E273.16.6", {"start": v(-29.42, 4.55) * mm, "mid": v(-29.57, 4.56) * mm, "end": v(-29.72, 4.57) * mm});
            skLineSegment(sketch, "E273.16.7", {"start": v(-29.65, 5.22) * mm, "end": v(-29.72, 4.57) * mm});
            skArc(sketch, "E273.16.8", {"start": v(-28.69, 3.8) * mm, "mid": v(-28.98, 3.88) * mm, "end": v(-29.19, 4.1) * mm});
            skPoint(sketch, "E273.16.9", {"position": v(-28.69, 5.18) * mm});
            skArc(sketch, "E273.16.10", {"start": v(-28.69, 4.8) * mm, "mid": v(-29.19, 4.81) * mm, "end": v(-29.69, 4.85) * mm, "construction": true});
            skArc(sketch, "E273.16.11", {"start": v(-28.69, 5.18) * mm, "mid": v(-28.2, 5.19) * mm, "end": v(-27.73, 5.22) * mm});
            skPoint(sketch, "E273.16.12", {"position": v(-28.69, 4.8) * mm});
            skArc(sketch, "E273.16.13", {"start": v(-27.96, 4.55) * mm, "mid": v(-27.8, 4.56) * mm, "end": v(-27.66, 4.57) * mm});
            skArc(sketch, "E273.16.14", {"start": v(-29.28, 4.42) * mm, "mid": v(-29.33, 4.5) * mm, "end": v(-29.42, 4.55) * mm});
            skArc(sketch, "E273.16.15", {"start": v(-28.1, 4.42) * mm, "mid": v(-28.05, 4.5) * mm, "end": v(-27.96, 4.55) * mm});
            skArc(sketch, "E273.17.0", {"start": v(-26.07, 4.41) * mm, "mid": v(-26.05, 4.57) * mm, "end": v(-26.04, 4.73) * mm});
            skArc(sketch, "E273.17.1", {"start": v(-26.5, 4.01) * mm, "mid": v(-26.23, 4.15) * mm, "end": v(-26.07, 4.41) * mm});
            skArc(sketch, "E273.17.2", {"start": v(-26.77, 5.36) * mm, "mid": v(-27.25, 5.28) * mm, "end": v(-27.73, 5.22) * mm});
            skPoint(sketch, "E273.17.3", {"position": v(-26.65, 4.75) * mm});
            skArc(sketch, "E273.17.4", {"start": v(-27.05, 4.22) * mm, "mid": v(-27.14, 4.36) * mm, "end": v(-27.2, 4.5) * mm});
            skLineSegment(sketch, "E273.17.5", {"start": v(-25.84, 5.6) * mm, "end": v(-25.65, 4.97) * mm});
            skArc(sketch, "E273.17.6", {"start": v(-27.36, 4.6) * mm, "mid": v(-27.51, 4.59) * mm, "end": v(-27.66, 4.57) * mm});
            skLineSegment(sketch, "E273.17.7", {"start": v(-27.73, 5.22) * mm, "end": v(-27.66, 4.57) * mm});
            skArc(sketch, "E273.17.8", {"start": v(-26.5, 4.01) * mm, "mid": v(-26.8, 4.04) * mm, "end": v(-27.05, 4.22) * mm});
            skPoint(sketch, "E273.17.9", {"position": v(-26.77, 5.36) * mm});
            skArc(sketch, "E273.17.10", {"start": v(-26.7, 5) * mm, "mid": v(-27.2, 4.91) * mm, "end": v(-27.69, 4.85) * mm, "construction": true});
            skArc(sketch, "E273.17.11", {"start": v(-26.77, 5.36) * mm, "mid": v(-26.3, 5.47) * mm, "end": v(-25.84, 5.6) * mm});
            skPoint(sketch, "E273.17.12", {"position": v(-26.7, 5) * mm});
            skArc(sketch, "E273.17.13", {"start": v(-25.93, 4.89) * mm, "mid": v(-25.79, 4.93) * mm, "end": v(-25.65, 4.97) * mm});
            skArc(sketch, "E273.17.14", {"start": v(-27.2, 4.5) * mm, "mid": v(-27.27, 4.58) * mm, "end": v(-27.36, 4.6) * mm});
            skArc(sketch, "E273.17.15", {"start": v(-26.04, 4.73) * mm, "mid": v(-26.02, 4.83) * mm, "end": v(-25.93, 4.89) * mm});
            skArc(sketch, "E273.18.0", {"start": v(-24.06, 5.13) * mm, "mid": v(-24.06, 5.29) * mm, "end": v(-24.1, 5.45) * mm});
            skArc(sketch, "E273.18.1", {"start": v(-24.4, 4.65) * mm, "mid": v(-24.16, 4.84) * mm, "end": v(-24.06, 5.13) * mm});
            skArc(sketch, "E273.18.2", {"start": v(-24.93, 5.92) * mm, "mid": v(-25.38, 5.75) * mm, "end": v(-25.84, 5.6) * mm});
            skPoint(sketch, "E273.18.3", {"position": v(-24.69, 5.34) * mm});
            skArc(sketch, "E273.18.4", {"start": v(-24.98, 4.75) * mm, "mid": v(-25.1, 4.86) * mm, "end": v(-25.18, 5) * mm});
            skLineSegment(sketch, "E273.18.5", {"start": v(-24.06, 6.34) * mm, "end": v(-23.75, 5.76) * mm});
            skArc(sketch, "E273.18.6", {"start": v(-25.36, 5.06) * mm, "mid": v(-25.5, 5.02) * mm, "end": v(-25.65, 4.97) * mm});
            skLineSegment(sketch, "E273.18.7", {"start": v(-25.84, 5.6) * mm, "end": v(-25.65, 4.97) * mm});
            skArc(sketch, "E273.18.8", {"start": v(-24.4, 4.65) * mm, "mid": v(-24.7, 4.61) * mm, "end": v(-24.98, 4.75) * mm});
            skPoint(sketch, "E273.18.9", {"position": v(-24.93, 5.92) * mm});
            skArc(sketch, "E273.18.10", {"start": v(-24.79, 5.58) * mm, "mid": v(-25.25, 5.4) * mm, "end": v(-25.73, 5.24) * mm, "construction": true});
            skArc(sketch, "E273.18.11", {"start": v(-24.93, 5.92) * mm, "mid": v(-24.49, 6.12) * mm, "end": v(-24.06, 6.34) * mm});
            skPoint(sketch, "E273.18.12", {"position": v(-24.79, 5.58) * mm});
            skArc(sketch, "E273.18.13", {"start": v(-24.01, 5.62) * mm, "mid": v(-23.88, 5.69) * mm, "end": v(-23.75, 5.76) * mm});
            skArc(sketch, "E273.18.14", {"start": v(-25.18, 5) * mm, "mid": v(-25.26, 5.06) * mm, "end": v(-25.36, 5.06) * mm});
            skArc(sketch, "E273.18.15", {"start": v(-24.1, 5.45) * mm, "mid": v(-24.08, 5.55) * mm, "end": v(-24.01, 5.62) * mm});
            skArc(sketch, "E273.19.0", {"start": v(-22.22, 6.22) * mm, "mid": v(-22.26, 6.38) * mm, "end": v(-22.32, 6.53) * mm});
            skArc(sketch, "E273.19.1", {"start": v(-22.46, 5.68) * mm, "mid": v(-22.27, 5.92) * mm, "end": v(-22.22, 6.22) * mm});
            skArc(sketch, "E273.19.2", {"start": v(-23.23, 6.83) * mm, "mid": v(-23.64, 6.57) * mm, "end": v(-24.06, 6.34) * mm});
            skPoint(sketch, "E273.19.3", {"position": v(-22.88, 6.3) * mm});
            skArc(sketch, "E273.19.4", {"start": v(-23.05, 5.67) * mm, "mid": v(-23.18, 5.76) * mm, "end": v(-23.3, 5.87) * mm});
            skLineSegment(sketch, "E273.19.5", {"start": v(-22.46, 7.4) * mm, "end": v(-22.04, 6.9) * mm});
            skArc(sketch, "E273.19.6", {"start": v(-23.49, 5.9) * mm, "mid": v(-23.62, 5.83) * mm, "end": v(-23.75, 5.76) * mm});
            skLineSegment(sketch, "E273.19.7", {"start": v(-24.06, 6.34) * mm, "end": v(-23.75, 5.76) * mm});
            skArc(sketch, "E273.19.8", {"start": v(-22.46, 5.68) * mm, "mid": v(-22.76, 5.6) * mm, "end": v(-23.05, 5.67) * mm});
            skPoint(sketch, "E273.19.9", {"position": v(-23.23, 6.83) * mm});
            skArc(sketch, "E273.19.10", {"start": v(-23.02, 6.52) * mm, "mid": v(-23.44, 6.25) * mm, "end": v(-23.88, 6) * mm, "construction": true});
            skArc(sketch, "E273.19.11", {"start": v(-23.23, 6.83) * mm, "mid": v(-22.84, 7.1) * mm, "end": v(-22.46, 7.4) * mm});
            skPoint(sketch, "E273.19.12", {"position": v(-23.02, 6.52) * mm});
            skArc(sketch, "E273.19.13", {"start": v(-22.27, 6.71) * mm, "mid": v(-22.16, 6.8) * mm, "end": v(-22.04, 6.9) * mm});
            skArc(sketch, "E273.19.14", {"start": v(-23.3, 5.87) * mm, "mid": v(-23.39, 5.92) * mm, "end": v(-23.49, 5.9) * mm});
            skArc(sketch, "E273.19.15", {"start": v(-22.32, 6.53) * mm, "mid": v(-22.33, 6.63) * mm, "end": v(-22.27, 6.71) * mm});
            skArc(sketch, "E273.20.0", {"start": v(-20.63, 7.65) * mm, "mid": v(-20.7, 7.8) * mm, "end": v(-20.79, 7.93) * mm});
            skArc(sketch, "E273.20.1", {"start": v(-20.77, 7.08) * mm, "mid": v(-20.62, 7.35) * mm, "end": v(-20.63, 7.65) * mm});
            skArc(sketch, "E273.20.2", {"start": v(-21.74, 8.05) * mm, "mid": v(-22.1, 7.72) * mm, "end": v(-22.46, 7.4) * mm});
            skPoint(sketch, "E273.20.3", {"position": v(-21.3, 7.6) * mm});
            skArc(sketch, "E273.20.4", {"start": v(-21.34, 6.95) * mm, "mid": v(-21.49, 7) * mm, "end": v(-21.62, 7.1) * mm});
            skLineSegment(sketch, "E273.20.5", {"start": v(-21.1, 8.77) * mm, "end": v(-20.59, 8.35) * mm});
            skArc(sketch, "E273.20.6", {"start": v(-21.81, 7.1) * mm, "mid": v(-21.93, 7) * mm, "end": v(-22.04, 6.9) * mm});
            skLineSegment(sketch, "E273.20.7", {"start": v(-22.46, 7.4) * mm, "end": v(-22.04, 6.9) * mm});
            skArc(sketch, "E273.20.8", {"start": v(-20.77, 7.08) * mm, "mid": v(-21.03, 6.93) * mm, "end": v(-21.34, 6.95) * mm});
            skPoint(sketch, "E273.20.9", {"position": v(-21.74, 8.05) * mm});
            skArc(sketch, "E273.20.10", {"start": v(-21.48, 7.79) * mm, "mid": v(-21.84, 7.44) * mm, "end": v(-22.22, 7.12) * mm, "construction": true});
            skArc(sketch, "E273.20.11", {"start": v(-21.74, 8.05) * mm, "mid": v(-21.4, 8.4) * mm, "end": v(-21.1, 8.77) * mm});
            skPoint(sketch, "E273.20.12", {"position": v(-21.48, 7.79) * mm});
            skArc(sketch, "E273.20.13", {"start": v(-20.78, 8.12) * mm, "mid": v(-20.68, 8.24) * mm, "end": v(-20.59, 8.35) * mm});
            skArc(sketch, "E273.20.14", {"start": v(-21.62, 7.1) * mm, "mid": v(-21.72, 7.13) * mm, "end": v(-21.81, 7.1) * mm});
            skArc(sketch, "E273.20.15", {"start": v(-20.79, 7.93) * mm, "mid": v(-20.82, 8.03) * mm, "end": v(-20.78, 8.12) * mm});
            skArc(sketch, "E273.21.0", {"start": v(-19.35, 9.36) * mm, "mid": v(-19.45, 9.5) * mm, "end": v(-19.56, 9.61) * mm});
            skArc(sketch, "E273.21.1", {"start": v(-19.37, 8.78) * mm, "mid": v(-19.28, 9.07) * mm, "end": v(-19.35, 9.36) * mm});
            skArc(sketch, "E273.21.2", {"start": v(-20.52, 9.54) * mm, "mid": v(-20.8, 9.15) * mm, "end": v(-21.1, 8.77) * mm});
            skPoint(sketch, "E273.21.3", {"position": v(-20, 9.2) * mm});
            skArc(sketch, "E273.21.4", {"start": v(-19.9, 8.53) * mm, "mid": v(-20.07, 8.57) * mm, "end": v(-20.22, 8.63) * mm});
            skLineSegment(sketch, "E273.21.5", {"start": v(-20.02, 10.37) * mm, "end": v(-19.45, 10.06) * mm});
            skArc(sketch, "E273.21.6", {"start": v(-20.4, 8.59) * mm, "mid": v(-20.5, 8.47) * mm, "end": v(-20.59, 8.35) * mm});
            skLineSegment(sketch, "E273.21.7", {"start": v(-21.1, 8.77) * mm, "end": v(-20.59, 8.35) * mm});
            skArc(sketch, "E273.21.8", {"start": v(-19.37, 8.78) * mm, "mid": v(-19.6, 8.58) * mm, "end": v(-19.9, 8.53) * mm});
            skPoint(sketch, "E273.21.9", {"position": v(-20.52, 9.54) * mm});
            skArc(sketch, "E273.21.10", {"start": v(-20.2, 9.33) * mm, "mid": v(-20.5, 8.92) * mm, "end": v(-20.8, 8.53) * mm, "construction": true});
            skArc(sketch, "E273.21.11", {"start": v(-20.52, 9.54) * mm, "mid": v(-20.26, 9.95) * mm, "end": v(-20.02, 10.37) * mm});
            skPoint(sketch, "E273.21.12", {"position": v(-20.2, 9.33) * mm});
            skArc(sketch, "E273.21.13", {"start": v(-19.6, 9.8) * mm, "mid": v(-19.52, 9.93) * mm, "end": v(-19.45, 10.06) * mm});
            skArc(sketch, "E273.21.14", {"start": v(-20.22, 8.63) * mm, "mid": v(-20.32, 8.64) * mm, "end": v(-20.4, 8.59) * mm});
            skArc(sketch, "E273.21.15", {"start": v(-19.56, 9.61) * mm, "mid": v(-19.6, 9.7) * mm, "end": v(-19.6, 9.8) * mm});
            skArc(sketch, "E273.22.0", {"start": v(-18.43, 11.3) * mm, "mid": v(-18.55, 11.4) * mm, "end": v(-18.68, 11.5) * mm});
            skArc(sketch, "E273.22.1", {"start": v(-18.34, 10.71) * mm, "mid": v(-18.3, 11.02) * mm, "end": v(-18.43, 11.3) * mm});
            skArc(sketch, "E273.22.2", {"start": v(-19.61, 11.24) * mm, "mid": v(-19.8, 10.8) * mm, "end": v(-20.02, 10.37) * mm});
            skPoint(sketch, "E273.22.3", {"position": v(-19.03, 11) * mm});
            skArc(sketch, "E273.22.4", {"start": v(-18.82, 10.37) * mm, "mid": v(-18.98, 10.37) * mm, "end": v(-19.14, 10.4) * mm});
            skLineSegment(sketch, "E273.22.5", {"start": v(-19.29, 12.15) * mm, "end": v(-18.66, 11.96) * mm});
            skArc(sketch, "E273.22.6", {"start": v(-19.3, 10.33) * mm, "mid": v(-19.38, 10.2) * mm, "end": v(-19.45, 10.06) * mm});
            skLineSegment(sketch, "E273.22.7", {"start": v(-20.02, 10.37) * mm, "end": v(-19.45, 10.06) * mm});
            skArc(sketch, "E273.22.8", {"start": v(-18.34, 10.71) * mm, "mid": v(-18.53, 10.47) * mm, "end": v(-18.82, 10.37) * mm});
            skPoint(sketch, "E273.22.9", {"position": v(-19.61, 11.24) * mm});
            skArc(sketch, "E273.22.10", {"start": v(-19.26, 11.1) * mm, "mid": v(-19.47, 10.64) * mm, "end": v(-19.7, 10.2) * mm, "construction": true});
            skArc(sketch, "E273.22.11", {"start": v(-19.61, 11.24) * mm, "mid": v(-19.44, 11.7) * mm, "end": v(-19.29, 12.15) * mm});
            skPoint(sketch, "E273.22.12", {"position": v(-19.26, 11.1) * mm});
            skArc(sketch, "E273.22.13", {"start": v(-18.75, 11.67) * mm, "mid": v(-18.7, 11.82) * mm, "end": v(-18.66, 11.96) * mm});
            skArc(sketch, "E273.22.14", {"start": v(-19.14, 10.4) * mm, "mid": v(-19.24, 10.4) * mm, "end": v(-19.3, 10.33) * mm});
            skArc(sketch, "E273.22.15", {"start": v(-18.68, 11.5) * mm, "mid": v(-18.75, 11.57) * mm, "end": v(-18.75, 11.67) * mm});
            skArc(sketch, "E273.23.0", {"start": v(-17.9, 13.36) * mm, "mid": v(-18.04, 13.45) * mm, "end": v(-18.2, 13.52) * mm});
            skArc(sketch, "E273.23.1", {"start": v(-17.7, 12.81) * mm, "mid": v(-17.73, 13.12) * mm, "end": v(-17.9, 13.36) * mm});
            skArc(sketch, "E273.23.2", {"start": v(-19.05, 13.08) * mm, "mid": v(-19.16, 12.61) * mm, "end": v(-19.29, 12.15) * mm});
            skPoint(sketch, "E273.23.3", {"position": v(-18.44, 12.96) * mm});
            skArc(sketch, "E273.23.4", {"start": v(-18.1, 12.39) * mm, "mid": v(-18.26, 12.36) * mm, "end": v(-18.42, 12.36) * mm});
            skLineSegment(sketch, "E273.23.5", {"start": v(-18.91, 14.04) * mm, "end": v(-18.26, 13.97) * mm});
            skArc(sketch, "E273.23.6", {"start": v(-18.58, 12.24) * mm, "mid": v(-18.62, 12.1) * mm, "end": v(-18.66, 11.96) * mm});
            skLineSegment(sketch, "E273.23.7", {"start": v(-19.29, 12.15) * mm, "end": v(-18.66, 11.96) * mm});
            skArc(sketch, "E273.23.8", {"start": v(-17.7, 12.81) * mm, "mid": v(-17.84, 12.54) * mm, "end": v(-18.1, 12.39) * mm});
            skPoint(sketch, "E273.23.9", {"position": v(-19.05, 13.08) * mm});
            skArc(sketch, "E273.23.10", {"start": v(-18.68, 13.01) * mm, "mid": v(-18.8, 12.52) * mm, "end": v(-18.93, 12.04) * mm, "construction": true});
            skArc(sketch, "E273.23.11", {"start": v(-19.05, 13.08) * mm, "mid": v(-18.97, 13.56) * mm, "end": v(-18.91, 14.04) * mm});
            skPoint(sketch, "E273.23.12", {"position": v(-18.68, 13.01) * mm});
            skArc(sketch, "E273.23.13", {"start": v(-18.3, 13.68) * mm, "mid": v(-18.28, 13.82) * mm, "end": v(-18.26, 13.97) * mm});
            skArc(sketch, "E273.23.14", {"start": v(-18.42, 12.36) * mm, "mid": v(-18.52, 12.33) * mm, "end": v(-18.58, 12.24) * mm});
            skArc(sketch, "E273.23.15", {"start": v(-18.2, 13.52) * mm, "mid": v(-18.27, 13.58) * mm, "end": v(-18.3, 13.68) * mm});
            skArc(sketch, "E273.24.0", {"start": v(-17.8, 15.5) * mm, "mid": v(-17.95, 15.56) * mm, "end": v(-18.1, 15.6) * mm});
            skArc(sketch, "E273.24.1", {"start": v(-17.48, 15) * mm, "mid": v(-17.57, 15.3) * mm, "end": v(-17.8, 15.5) * mm});
            skArc(sketch, "E273.24.2", {"start": v(-18.86, 15) * mm, "mid": v(-18.88, 14.52) * mm, "end": v(-18.91, 14.04) * mm});
            skPoint(sketch, "E273.24.3", {"position": v(-18.23, 15) * mm});
            skArc(sketch, "E273.24.4", {"start": v(-17.8, 14.5) * mm, "mid": v(-17.95, 14.44) * mm, "end": v(-18.1, 14.4) * mm});
            skLineSegment(sketch, "E273.24.5", {"start": v(-18.91, 15.96) * mm, "end": v(-18.26, 16.03) * mm});
            skArc(sketch, "E273.24.6", {"start": v(-18.23, 14.27) * mm, "mid": v(-18.25, 14.12) * mm, "end": v(-18.26, 13.97) * mm});
            skLineSegment(sketch, "E273.24.7", {"start": v(-18.91, 14.04) * mm, "end": v(-18.26, 13.97) * mm});
            skArc(sketch, "E273.24.8", {"start": v(-17.48, 15) * mm, "mid": v(-17.57, 14.7) * mm, "end": v(-17.8, 14.5) * mm});
            skPoint(sketch, "E273.24.9", {"position": v(-18.86, 15) * mm});
            skArc(sketch, "E273.24.10", {"start": v(-18.49, 15) * mm, "mid": v(-18.5, 14.5) * mm, "end": v(-18.54, 14) * mm, "construction": true});
            skArc(sketch, "E273.24.11", {"start": v(-18.86, 15) * mm, "mid": v(-18.88, 15.48) * mm, "end": v(-18.91, 15.96) * mm});
            skPoint(sketch, "E273.24.12", {"position": v(-18.49, 15) * mm});
            skArc(sketch, "E273.24.13", {"start": v(-18.23, 15.73) * mm, "mid": v(-18.25, 15.88) * mm, "end": v(-18.26, 16.03) * mm});
            skArc(sketch, "E273.24.14", {"start": v(-18.1, 14.4) * mm, "mid": v(-18.2, 14.36) * mm, "end": v(-18.23, 14.27) * mm});
            skArc(sketch, "E273.24.15", {"start": v(-18.1, 15.6) * mm, "mid": v(-18.2, 15.64) * mm, "end": v(-18.23, 15.73) * mm});
            skArc(sketch, "E273.25.0", {"start": v(-18.1, 17.61) * mm, "mid": v(-18.26, 17.64) * mm, "end": v(-18.42, 17.64) * mm});
            skArc(sketch, "E273.25.1", {"start": v(-17.7, 17.19) * mm, "mid": v(-17.84, 17.46) * mm, "end": v(-18.1, 17.61) * mm});
            skArc(sketch, "E273.25.2", {"start": v(-19.05, 16.92) * mm, "mid": v(-18.97, 16.44) * mm, "end": v(-18.91, 15.96) * mm});
            skPoint(sketch, "E273.25.3", {"position": v(-18.44, 17.04) * mm});
            skArc(sketch, "E273.25.4", {"start": v(-17.9, 16.64) * mm, "mid": v(-18.04, 16.55) * mm, "end": v(-18.2, 16.48) * mm});
            skLineSegment(sketch, "E273.25.5", {"start": v(-19.29, 17.85) * mm, "end": v(-18.66, 18.04) * mm});
            skArc(sketch, "E273.25.6", {"start": v(-18.3, 16.32) * mm, "mid": v(-18.28, 16.18) * mm, "end": v(-18.26, 16.03) * mm});
            skLineSegment(sketch, "E273.25.7", {"start": v(-18.91, 15.96) * mm, "end": v(-18.26, 16.03) * mm});
            skArc(sketch, "E273.25.8", {"start": v(-17.7, 17.19) * mm, "mid": v(-17.73, 16.88) * mm, "end": v(-17.9, 16.64) * mm});
            skPoint(sketch, "E273.25.9", {"position": v(-19.05, 16.92) * mm});
            skArc(sketch, "E273.25.10", {"start": v(-18.68, 16.99) * mm, "mid": v(-18.6, 16.5) * mm, "end": v(-18.54, 16) * mm, "construction": true});
            skArc(sketch, "E273.25.11", {"start": v(-19.05, 16.92) * mm, "mid": v(-19.16, 17.39) * mm, "end": v(-19.29, 17.85) * mm});
            skPoint(sketch, "E273.25.12", {"position": v(-18.68, 16.99) * mm});
            skArc(sketch, "E273.25.13", {"start": v(-18.58, 17.76) * mm, "mid": v(-18.62, 17.9) * mm, "end": v(-18.66, 18.04) * mm});
            skArc(sketch, "E273.25.14", {"start": v(-18.2, 16.48) * mm, "mid": v(-18.27, 16.42) * mm, "end": v(-18.3, 16.32) * mm});
            skArc(sketch, "E273.25.15", {"start": v(-18.42, 17.64) * mm, "mid": v(-18.52, 17.67) * mm, "end": v(-18.58, 17.76) * mm});
            skArc(sketch, "E273.26.0", {"start": v(-18.82, 19.63) * mm, "mid": v(-18.98, 19.63) * mm, "end": v(-19.14, 19.6) * mm});
            skArc(sketch, "E273.26.1", {"start": v(-18.34, 19.29) * mm, "mid": v(-18.53, 19.53) * mm, "end": v(-18.82, 19.63) * mm});
            skArc(sketch, "E273.26.2", {"start": v(-19.61, 18.76) * mm, "mid": v(-19.44, 18.3) * mm, "end": v(-19.29, 17.85) * mm});
            skPoint(sketch, "E273.26.3", {"position": v(-19.03, 19) * mm});
            skArc(sketch, "E273.26.4", {"start": v(-18.43, 18.7) * mm, "mid": v(-18.55, 18.6) * mm, "end": v(-18.68, 18.5) * mm});
            skLineSegment(sketch, "E273.26.5", {"start": v(-20.02, 19.63) * mm, "end": v(-19.45, 19.94) * mm});
            skArc(sketch, "E273.26.6", {"start": v(-18.75, 18.33) * mm, "mid": v(-18.7, 18.18) * mm, "end": v(-18.66, 18.04) * mm});
            skLineSegment(sketch, "E273.26.7", {"start": v(-19.29, 17.85) * mm, "end": v(-18.66, 18.04) * mm});
            skArc(sketch, "E273.26.8", {"start": v(-18.34, 19.29) * mm, "mid": v(-18.3, 18.98) * mm, "end": v(-18.43, 18.7) * mm});
            skPoint(sketch, "E273.26.9", {"position": v(-19.61, 18.76) * mm});
            skArc(sketch, "E273.26.10", {"start": v(-19.26, 18.9) * mm, "mid": v(-19.08, 18.44) * mm, "end": v(-18.93, 17.96) * mm, "construction": true});
            skArc(sketch, "E273.26.11", {"start": v(-19.61, 18.76) * mm, "mid": v(-19.8, 19.2) * mm, "end": v(-20.02, 19.63) * mm});
            skPoint(sketch, "E273.26.12", {"position": v(-19.26, 18.9) * mm});
            skArc(sketch, "E273.26.13", {"start": v(-19.3, 19.67) * mm, "mid": v(-19.38, 19.8) * mm, "end": v(-19.45, 19.94) * mm});
            skArc(sketch, "E273.26.14", {"start": v(-18.68, 18.5) * mm, "mid": v(-18.75, 18.43) * mm, "end": v(-18.75, 18.33) * mm});
            skArc(sketch, "E273.26.15", {"start": v(-19.14, 19.6) * mm, "mid": v(-19.24, 19.6) * mm, "end": v(-19.3, 19.67) * mm});
            skArc(sketch, "E273.27.0", {"start": v(-19.9, 21.47) * mm, "mid": v(-20.07, 21.43) * mm, "end": v(-20.22, 21.37) * mm});
            skArc(sketch, "E273.27.1", {"start": v(-19.37, 21.22) * mm, "mid": v(-19.6, 21.42) * mm, "end": v(-19.9, 21.47) * mm});
            skArc(sketch, "E273.27.2", {"start": v(-20.52, 20.46) * mm, "mid": v(-20.26, 20.05) * mm, "end": v(-20.02, 19.63) * mm});
            skPoint(sketch, "E273.27.3", {"position": v(-20, 20.8) * mm});
            skArc(sketch, "E273.27.4", {"start": v(-19.35, 20.64) * mm, "mid": v(-19.45, 20.5) * mm, "end": v(-19.56, 20.39) * mm});
            skLineSegment(sketch, "E273.27.5", {"start": v(-21.1, 21.23) * mm, "end": v(-20.59, 21.65) * mm});
            skArc(sketch, "E273.27.6", {"start": v(-19.6, 20.2) * mm, "mid": v(-19.52, 20.07) * mm, "end": v(-19.45, 19.94) * mm});
            skLineSegment(sketch, "E273.27.7", {"start": v(-20.02, 19.63) * mm, "end": v(-19.45, 19.94) * mm});
            skArc(sketch, "E273.27.8", {"start": v(-19.37, 21.22) * mm, "mid": v(-19.28, 20.93) * mm, "end": v(-19.35, 20.64) * mm});
            skPoint(sketch, "E273.27.9", {"position": v(-20.52, 20.46) * mm});
            skArc(sketch, "E273.27.10", {"start": v(-20.2, 20.67) * mm, "mid": v(-19.94, 20.24) * mm, "end": v(-19.7, 19.8) * mm, "construction": true});
            skArc(sketch, "E273.27.11", {"start": v(-20.52, 20.46) * mm, "mid": v(-20.8, 20.85) * mm, "end": v(-21.1, 21.23) * mm});
            skPoint(sketch, "E273.27.12", {"position": v(-20.2, 20.67) * mm});
            skArc(sketch, "E273.27.13", {"start": v(-20.4, 21.41) * mm, "mid": v(-20.5, 21.53) * mm, "end": v(-20.59, 21.65) * mm});
            skArc(sketch, "E273.27.14", {"start": v(-19.56, 20.39) * mm, "mid": v(-19.6, 20.3) * mm, "end": v(-19.6, 20.2) * mm});
            skArc(sketch, "E273.27.15", {"start": v(-20.22, 21.37) * mm, "mid": v(-20.32, 21.36) * mm, "end": v(-20.4, 21.41) * mm});
            skArc(sketch, "E273.28.0", {"start": v(-21.34, 23.05) * mm, "mid": v(-21.49, 23) * mm, "end": v(-21.62, 22.9) * mm});
            skArc(sketch, "E273.28.1", {"start": v(-20.77, 22.92) * mm, "mid": v(-21.03, 23.07) * mm, "end": v(-21.34, 23.05) * mm});
            skArc(sketch, "E273.28.2", {"start": v(-21.74, 21.95) * mm, "mid": v(-21.4, 21.6) * mm, "end": v(-21.1, 21.23) * mm});
            skPoint(sketch, "E273.28.3", {"position": v(-21.3, 22.4) * mm});
            skArc(sketch, "E273.28.4", {"start": v(-20.63, 22.35) * mm, "mid": v(-20.7, 22.2) * mm, "end": v(-20.79, 22.07) * mm});
            skLineSegment(sketch, "E273.28.5", {"start": v(-22.46, 22.6) * mm, "end": v(-22.04, 23.1) * mm});
            skArc(sketch, "E273.28.6", {"start": v(-20.78, 21.88) * mm, "mid": v(-20.68, 21.76) * mm, "end": v(-20.59, 21.65) * mm});
            skLineSegment(sketch, "E273.28.7", {"start": v(-21.1, 21.23) * mm, "end": v(-20.59, 21.65) * mm});
            skArc(sketch, "E273.28.8", {"start": v(-20.77, 22.92) * mm, "mid": v(-20.62, 22.65) * mm, "end": v(-20.63, 22.35) * mm});
            skPoint(sketch, "E273.28.9", {"position": v(-21.74, 21.95) * mm});
            skArc(sketch, "E273.28.10", {"start": v(-21.48, 22.21) * mm, "mid": v(-21.13, 21.85) * mm, "end": v(-20.8, 21.47) * mm, "construction": true});
            skArc(sketch, "E273.28.11", {"start": v(-21.74, 21.95) * mm, "mid": v(-22.1, 22.28) * mm, "end": v(-22.46, 22.6) * mm});
            skPoint(sketch, "E273.28.12", {"position": v(-21.48, 22.21) * mm});
            skArc(sketch, "E273.28.13", {"start": v(-21.81, 22.9) * mm, "mid": v(-21.93, 23) * mm, "end": v(-22.04, 23.1) * mm});
            skArc(sketch, "E273.28.14", {"start": v(-20.79, 22.07) * mm, "mid": v(-20.82, 21.97) * mm, "end": v(-20.78, 21.88) * mm});
            skArc(sketch, "E273.28.15", {"start": v(-21.62, 22.9) * mm, "mid": v(-21.72, 22.87) * mm, "end": v(-21.81, 22.9) * mm});
            skArc(sketch, "E273.29.0", {"start": v(-23.05, 24.33) * mm, "mid": v(-23.18, 24.24) * mm, "end": v(-23.3, 24.13) * mm});
            skArc(sketch, "E273.29.1", {"start": v(-22.46, 24.32) * mm, "mid": v(-22.76, 24.4) * mm, "end": v(-23.05, 24.33) * mm});
            skArc(sketch, "E273.29.2", {"start": v(-23.23, 23.17) * mm, "mid": v(-22.84, 22.9) * mm, "end": v(-22.46, 22.6) * mm});
            skPoint(sketch, "E273.29.3", {"position": v(-22.88, 23.7) * mm});
            skArc(sketch, "E273.29.4", {"start": v(-22.22, 23.78) * mm, "mid": v(-22.26, 23.62) * mm, "end": v(-22.32, 23.47) * mm});
            skLineSegment(sketch, "E273.29.5", {"start": v(-24.06, 23.66) * mm, "end": v(-23.75, 24.24) * mm});
            skArc(sketch, "E273.29.6", {"start": v(-22.27, 23.29) * mm, "mid": v(-22.16, 23.2) * mm, "end": v(-22.04, 23.1) * mm});
            skLineSegment(sketch, "E273.29.7", {"start": v(-22.46, 22.6) * mm, "end": v(-22.04, 23.1) * mm});
            skArc(sketch, "E273.29.8", {"start": v(-22.46, 24.32) * mm, "mid": v(-22.27, 24.08) * mm, "end": v(-22.22, 23.78) * mm});
            skPoint(sketch, "E273.29.9", {"position": v(-23.23, 23.17) * mm});
            skArc(sketch, "E273.29.10", {"start": v(-23.02, 23.48) * mm, "mid": v(-22.61, 23.2) * mm, "end": v(-22.22, 22.88) * mm, "construction": true});
            skArc(sketch, "E273.29.11", {"start": v(-23.23, 23.17) * mm, "mid": v(-23.64, 23.43) * mm, "end": v(-24.06, 23.66) * mm});
            skPoint(sketch, "E273.29.12", {"position": v(-23.02, 23.48) * mm});
            skArc(sketch, "E273.29.13", {"start": v(-23.49, 24.1) * mm, "mid": v(-23.62, 24.17) * mm, "end": v(-23.75, 24.24) * mm});
            skArc(sketch, "E273.29.14", {"start": v(-22.32, 23.47) * mm, "mid": v(-22.33, 23.37) * mm, "end": v(-22.27, 23.29) * mm});
            skArc(sketch, "E273.29.15", {"start": v(-23.3, 24.13) * mm, "mid": v(-23.39, 24.08) * mm, "end": v(-23.49, 24.1) * mm});
            skArc(sketch, "E273.30.0", {"start": v(-24.98, 25.25) * mm, "mid": v(-25.1, 25.14) * mm, "end": v(-25.18, 25) * mm});
            skArc(sketch, "E273.30.1", {"start": v(-24.4, 25.35) * mm, "mid": v(-24.7, 25.39) * mm, "end": v(-24.98, 25.25) * mm});
            skArc(sketch, "E273.30.2", {"start": v(-24.93, 24.08) * mm, "mid": v(-24.49, 23.88) * mm, "end": v(-24.06, 23.66) * mm});
            skPoint(sketch, "E273.30.3", {"position": v(-24.69, 24.66) * mm});
            skArc(sketch, "E273.30.4", {"start": v(-24.06, 24.87) * mm, "mid": v(-24.06, 24.71) * mm, "end": v(-24.1, 24.55) * mm});
            skLineSegment(sketch, "E273.30.5", {"start": v(-25.84, 24.4) * mm, "end": v(-25.65, 25.03) * mm});
            skArc(sketch, "E273.30.6", {"start": v(-24.01, 24.38) * mm, "mid": v(-23.88, 24.31) * mm, "end": v(-23.75, 24.24) * mm});
            skLineSegment(sketch, "E273.30.7", {"start": v(-24.06, 23.66) * mm, "end": v(-23.75, 24.24) * mm});
            skArc(sketch, "E273.30.8", {"start": v(-24.4, 25.35) * mm, "mid": v(-24.16, 25.16) * mm, "end": v(-24.06, 24.87) * mm});
            skPoint(sketch, "E273.30.9", {"position": v(-24.93, 24.08) * mm});
            skArc(sketch, "E273.30.10", {"start": v(-24.79, 24.42) * mm, "mid": v(-24.33, 24.22) * mm, "end": v(-23.88, 24) * mm, "construction": true});
            skArc(sketch, "E273.30.11", {"start": v(-24.93, 24.08) * mm, "mid": v(-25.38, 24.25) * mm, "end": v(-25.84, 24.4) * mm});
            skPoint(sketch, "E273.30.12", {"position": v(-24.79, 24.42) * mm});
            skArc(sketch, "E273.30.13", {"start": v(-25.36, 24.94) * mm, "mid": v(-25.5, 24.98) * mm, "end": v(-25.65, 25.03) * mm});
            skArc(sketch, "E273.30.14", {"start": v(-24.1, 24.55) * mm, "mid": v(-24.08, 24.45) * mm, "end": v(-24.01, 24.38) * mm});
            skArc(sketch, "E273.30.15", {"start": v(-25.18, 25) * mm, "mid": v(-25.26, 24.94) * mm, "end": v(-25.36, 24.94) * mm});
            skArc(sketch, "E273.31.0", {"start": v(-27.05, 25.78) * mm, "mid": v(-27.14, 25.64) * mm, "end": v(-27.2, 25.5) * mm});
            skArc(sketch, "E273.31.1", {"start": v(-26.5, 25.99) * mm, "mid": v(-26.8, 25.96) * mm, "end": v(-27.05, 25.78) * mm});
            skArc(sketch, "E273.31.2", {"start": v(-26.77, 24.64) * mm, "mid": v(-26.3, 24.53) * mm, "end": v(-25.84, 24.4) * mm});
            skPoint(sketch, "E273.31.3", {"position": v(-26.65, 25.25) * mm});
            skArc(sketch, "E273.31.4", {"start": v(-26.07, 25.59) * mm, "mid": v(-26.05, 25.43) * mm, "end": v(-26.04, 25.27) * mm});
            skArc(sketch, "E273.31.6", {"start": v(-25.93, 25.11) * mm, "mid": v(-25.79, 25.07) * mm, "end": v(-25.65, 25.03) * mm});
            skLineSegment(sketch, "E273.31.7", {"start": v(-25.84, 24.4) * mm, "end": v(-25.65, 25.03) * mm});
            skArc(sketch, "E273.31.8", {"start": v(-26.5, 25.99) * mm, "mid": v(-26.23, 25.85) * mm, "end": v(-26.07, 25.59) * mm});
            skPoint(sketch, "E273.31.9", {"position": v(-26.77, 24.64) * mm});
            skArc(sketch, "E273.31.10", {"start": v(-26.7, 25) * mm, "mid": v(-26.2, 24.9) * mm, "end": v(-25.73, 24.76) * mm, "construction": true});
            skArc(sketch, "E273.31.11", {"start": v(-26.77, 24.64) * mm, "mid": v(-27.25, 24.72) * mm, "end": v(-27.73, 24.78) * mm});
            skPoint(sketch, "E273.31.12", {"position": v(-26.7, 25) * mm});
            skArc(sketch, "E273.31.13", {"start": v(-27.36, 25.4) * mm, "mid": v(-27.51, 25.41) * mm, "end": v(-27.66, 25.43) * mm});
            skArc(sketch, "E273.31.14", {"start": v(-26.04, 25.27) * mm, "mid": v(-26.02, 25.17) * mm, "end": v(-25.93, 25.11) * mm});
            skArc(sketch, "E273.31.15", {"start": v(-27.2, 25.5) * mm, "mid": v(-27.27, 25.42) * mm, "end": v(-27.36, 25.4) * mm});
            skArc(sketch, "E274.0", {"start": v(-38.94, 15) * mm, "mid": v(-28.69, 4.75) * mm, "end": v(-18.44, 15) * mm});
            skSolve(sketch);
        }
        {
            var Q0;
            Q0 = qSketchRegion(id + "F44", true);
            extrude(context, id + "F45", {"entities" : qUnion([Q0]), "operationType" : NewBodyOperationType.REMOVE, "endBound" : BoundingType.SYMMETRIC, "oppositeDirection" : true, "depth" : 6.5 * mm});
        }
        {
            var Q0;
            Q0=makeQuery(id+"F40.opExtrude","SWEPT_FACE",FACE,{"disambiguationData":[OSD([sQuery(id+"F39.wireOp",EDGE,"E244.right")])]});
            var Q1;
            Q1=sQuery(id+"F39.wireOp",VERTEX,"E251");
            cPlane(context, id + "F46", {"entities" : qUnion([Q0, Q1]), "cplaneType" : CPlaneType.PLANE_POINT, "offset" : 150 * mm, "width" : 150 * mm, "height" : 150 * mm});
        }
        {
            var Q0;
            Q0=qCreatedBy(id+"F46.planeOp",FACE);
            var sketch = newSketch(context, id + "F47", { "sketchPlane" : qUnion([Q0])});
            skLineSegment(sketch, "E275", {"start": v(-28.69, 26.2) * mm, "end": v(-28.69, 24.82) * mm, "construction": true});
            skArc(sketch, "E276", {"start": v(-28.69, 26.2) * mm, "mid": v(-28.4, 26.12) * mm, "end": v(-28.19, 25.9) * mm});
            skArc(sketch, "E277", {"start": v(-28.19, 25.9) * mm, "mid": v(-28.13, 25.74) * mm, "end": v(-28.1, 25.58) * mm});
            skArc(sketch, "E278", {"start": v(-28.1, 25.58) * mm, "mid": v(-28.05, 25.5) * mm, "end": v(-27.96, 25.45) * mm});
            skPoint(sketch, "E279", {"position": v(-28.69, 24.82) * mm});
            skPoint(sketch, "E280", {"position": v(-28.69, 25.45) * mm});
            skPoint(sketch, "E281", {"position": v(-28.69, 25.2) * mm});
            skArc(sketch, "E282", {"start": v(-28.69, 25.2) * mm, "mid": v(-28.19, 25.19) * mm, "end": v(-27.69, 25.15) * mm, "construction": true});
            skLineSegment(sketch, "E283", {"start": v(-27.73, 24.78) * mm, "end": v(-27.66, 25.43) * mm});
            skArc(sketch, "E284", {"start": v(-27.96, 25.45) * mm, "mid": v(-27.8, 25.44) * mm, "end": v(-27.66, 25.43) * mm});
            skArc(sketch, "E285", {"start": v(-28.69, 24.82) * mm, "mid": v(-28.2, 24.81) * mm, "end": v(-27.73, 24.78) * mm});
            skArc(sketch, "E286.MirrorCS", {"start": v(-28.69, 26.2) * mm, "mid": v(-28.98, 26.12) * mm, "end": v(-29.19, 25.9) * mm});
            skArc(sketch, "E287.MirrorCS", {"start": v(-29.19, 25.9) * mm, "mid": v(-29.25, 25.74) * mm, "end": v(-29.28, 25.58) * mm});
            skArc(sketch, "E288.MirrorCS", {"start": v(-29.28, 25.58) * mm, "mid": v(-29.33, 25.5) * mm, "end": v(-29.42, 25.45) * mm});
            skArc(sketch, "E289.MirrorCS", {"start": v(-29.42, 25.45) * mm, "mid": v(-29.57, 25.44) * mm, "end": v(-29.72, 25.43) * mm});
            skLineSegment(sketch, "E290.MirrorCS", {"start": v(-29.65, 24.78) * mm, "end": v(-29.72, 25.43) * mm});
            skArc(sketch, "E291.MirrorCS", {"start": v(-28.69, 24.82) * mm, "mid": v(-29.17, 24.81) * mm, "end": v(-29.65, 24.78) * mm});
            skArc(sketch, "E292.1.0", {"start": v(-31.3, 25.59) * mm, "mid": v(-31.33, 25.43) * mm, "end": v(-31.33, 25.27) * mm});
            skArc(sketch, "E292.1.1", {"start": v(-30.87, 25.99) * mm, "mid": v(-31.15, 25.85) * mm, "end": v(-31.3, 25.59) * mm});
            skArc(sketch, "E292.1.2", {"start": v(-30.6, 24.64) * mm, "mid": v(-30.13, 24.72) * mm, "end": v(-29.65, 24.78) * mm});
            skPoint(sketch, "E292.1.3", {"position": v(-30.73, 25.25) * mm});
            skArc(sketch, "E292.1.4", {"start": v(-30.32, 25.78) * mm, "mid": v(-30.24, 25.64) * mm, "end": v(-30.17, 25.5) * mm});
            skLineSegment(sketch, "E292.1.5", {"start": v(-31.54, 24.4) * mm, "end": v(-31.73, 25.03) * mm});
            skArc(sketch, "E292.1.6", {"start": v(-30.01, 25.4) * mm, "mid": v(-29.86, 25.41) * mm, "end": v(-29.72, 25.43) * mm});
            skArc(sketch, "E292.1.8", {"start": v(-30.87, 25.99) * mm, "mid": v(-30.57, 25.96) * mm, "end": v(-30.32, 25.78) * mm});
            skPoint(sketch, "E292.1.9", {"position": v(-30.6, 24.64) * mm});
            skArc(sketch, "E292.1.10", {"start": v(-30.68, 25) * mm, "mid": v(-30.19, 25.09) * mm, "end": v(-29.69, 25.15) * mm, "construction": true});
            skArc(sketch, "E292.1.11", {"start": v(-30.6, 24.64) * mm, "mid": v(-31.08, 24.53) * mm, "end": v(-31.54, 24.4) * mm});
            skPoint(sketch, "E292.1.12", {"position": v(-30.68, 25) * mm});
            skArc(sketch, "E292.1.13", {"start": v(-31.44, 25.11) * mm, "mid": v(-31.59, 25.07) * mm, "end": v(-31.73, 25.03) * mm});
            skArc(sketch, "E292.1.14", {"start": v(-30.17, 25.5) * mm, "mid": v(-30.11, 25.42) * mm, "end": v(-30.01, 25.4) * mm});
            skArc(sketch, "E292.1.15", {"start": v(-31.33, 25.27) * mm, "mid": v(-31.36, 25.17) * mm, "end": v(-31.44, 25.11) * mm});
            skArc(sketch, "E292.2.0", {"start": v(-33.32, 24.87) * mm, "mid": v(-33.31, 24.71) * mm, "end": v(-33.29, 24.55) * mm});
            skArc(sketch, "E292.2.1", {"start": v(-32.98, 25.35) * mm, "mid": v(-33.22, 25.16) * mm, "end": v(-33.32, 24.87) * mm});
            skArc(sketch, "E292.2.2", {"start": v(-32.45, 24.08) * mm, "mid": v(-32, 24.25) * mm, "end": v(-31.54, 24.4) * mm});
            skPoint(sketch, "E292.2.3", {"position": v(-32.69, 24.66) * mm});
            skArc(sketch, "E292.2.4", {"start": v(-32.4, 25.25) * mm, "mid": v(-32.28, 25.14) * mm, "end": v(-32.2, 25) * mm});
            skLineSegment(sketch, "E292.2.5", {"start": v(-33.32, 23.66) * mm, "end": v(-33.63, 24.24) * mm});
            skArc(sketch, "E292.2.6", {"start": v(-32.01, 24.94) * mm, "mid": v(-31.87, 24.98) * mm, "end": v(-31.73, 25.03) * mm});
            skLineSegment(sketch, "E292.2.7", {"start": v(-31.54, 24.4) * mm, "end": v(-31.73, 25.03) * mm});
            skArc(sketch, "E292.2.8", {"start": v(-32.98, 25.35) * mm, "mid": v(-32.67, 25.39) * mm, "end": v(-32.4, 25.25) * mm});
            skPoint(sketch, "E292.2.9", {"position": v(-32.45, 24.08) * mm});
            skArc(sketch, "E292.2.10", {"start": v(-32.6, 24.42) * mm, "mid": v(-32.12, 24.6) * mm, "end": v(-31.65, 24.76) * mm, "construction": true});
            skArc(sketch, "E292.2.11", {"start": v(-32.45, 24.08) * mm, "mid": v(-32.89, 23.88) * mm, "end": v(-33.32, 23.66) * mm});
            skPoint(sketch, "E292.2.12", {"position": v(-32.6, 24.42) * mm});
            skArc(sketch, "E292.2.13", {"start": v(-33.36, 24.38) * mm, "mid": v(-33.5, 24.31) * mm, "end": v(-33.63, 24.24) * mm});
            skArc(sketch, "E292.2.14", {"start": v(-32.2, 25) * mm, "mid": v(-32.12, 24.94) * mm, "end": v(-32.01, 24.94) * mm});
            skArc(sketch, "E292.2.15", {"start": v(-33.29, 24.55) * mm, "mid": v(-33.3, 24.45) * mm, "end": v(-33.36, 24.38) * mm});
            skArc(sketch, "E292.3.0", {"start": v(-35.15, 23.78) * mm, "mid": v(-35.12, 23.62) * mm, "end": v(-35.06, 23.47) * mm});
            skArc(sketch, "E292.3.1", {"start": v(-34.91, 24.32) * mm, "mid": v(-35.11, 24.08) * mm, "end": v(-35.15, 23.78) * mm});
            skArc(sketch, "E292.3.2", {"start": v(-34.15, 23.17) * mm, "mid": v(-33.74, 23.43) * mm, "end": v(-33.32, 23.66) * mm});
            skPoint(sketch, "E292.3.3", {"position": v(-34.5, 23.7) * mm});
            skArc(sketch, "E292.3.4", {"start": v(-34.33, 24.33) * mm, "mid": v(-34.2, 24.24) * mm, "end": v(-34.08, 24.13) * mm});
            skLineSegment(sketch, "E292.3.5", {"start": v(-34.92, 22.6) * mm, "end": v(-35.34, 23.1) * mm});
            skArc(sketch, "E292.3.6", {"start": v(-33.89, 24.1) * mm, "mid": v(-33.76, 24.17) * mm, "end": v(-33.63, 24.24) * mm});
            skLineSegment(sketch, "E292.3.7", {"start": v(-33.32, 23.66) * mm, "end": v(-33.63, 24.24) * mm});
            skArc(sketch, "E292.3.8", {"start": v(-34.91, 24.32) * mm, "mid": v(-34.62, 24.4) * mm, "end": v(-34.33, 24.33) * mm});
            skPoint(sketch, "E292.3.9", {"position": v(-34.15, 23.17) * mm});
            skArc(sketch, "E292.3.10", {"start": v(-34.36, 23.48) * mm, "mid": v(-33.93, 23.75) * mm, "end": v(-33.5, 24) * mm, "construction": true});
            skArc(sketch, "E292.3.11", {"start": v(-34.15, 23.17) * mm, "mid": v(-34.54, 22.9) * mm, "end": v(-34.92, 22.6) * mm});
            skPoint(sketch, "E292.3.12", {"position": v(-34.36, 23.48) * mm});
            skArc(sketch, "E292.3.13", {"start": v(-35.1, 23.29) * mm, "mid": v(-35.22, 23.2) * mm, "end": v(-35.34, 23.1) * mm});
            skArc(sketch, "E292.3.14", {"start": v(-34.08, 24.13) * mm, "mid": v(-33.99, 24.08) * mm, "end": v(-33.89, 24.1) * mm});
            skArc(sketch, "E292.3.15", {"start": v(-35.06, 23.47) * mm, "mid": v(-35.05, 23.37) * mm, "end": v(-35.1, 23.29) * mm});
            skArc(sketch, "E292.4.0", {"start": v(-36.74, 22.35) * mm, "mid": v(-36.68, 22.2) * mm, "end": v(-36.6, 22.07) * mm});
            skArc(sketch, "E292.4.1", {"start": v(-36.61, 22.92) * mm, "mid": v(-36.76, 22.65) * mm, "end": v(-36.74, 22.35) * mm});
            skArc(sketch, "E292.4.2", {"start": v(-35.64, 21.95) * mm, "mid": v(-35.29, 22.28) * mm, "end": v(-34.92, 22.6) * mm});
            skPoint(sketch, "E292.4.3", {"position": v(-36.08, 22.4) * mm});
            skArc(sketch, "E292.4.4", {"start": v(-36.04, 23.05) * mm, "mid": v(-35.89, 23) * mm, "end": v(-35.75, 22.9) * mm});
            skLineSegment(sketch, "E292.4.5", {"start": v(-36.28, 21.23) * mm, "end": v(-36.79, 21.65) * mm});
            skArc(sketch, "E292.4.6", {"start": v(-35.56, 22.9) * mm, "mid": v(-35.45, 23) * mm, "end": v(-35.34, 23.1) * mm});
            skLineSegment(sketch, "E292.4.7", {"start": v(-34.92, 22.6) * mm, "end": v(-35.34, 23.1) * mm});
            skArc(sketch, "E292.4.8", {"start": v(-36.61, 22.92) * mm, "mid": v(-36.34, 23.07) * mm, "end": v(-36.04, 23.05) * mm});
            skPoint(sketch, "E292.4.9", {"position": v(-35.64, 21.95) * mm});
            skArc(sketch, "E292.4.10", {"start": v(-35.9, 22.21) * mm, "mid": v(-35.54, 22.56) * mm, "end": v(-35.16, 22.88) * mm, "construction": true});
            skArc(sketch, "E292.4.11", {"start": v(-35.64, 21.95) * mm, "mid": v(-35.97, 21.6) * mm, "end": v(-36.28, 21.23) * mm});
            skPoint(sketch, "E292.4.12", {"position": v(-35.9, 22.21) * mm});
            skArc(sketch, "E292.4.13", {"start": v(-36.6, 21.88) * mm, "mid": v(-36.7, 21.76) * mm, "end": v(-36.79, 21.65) * mm});
            skArc(sketch, "E292.4.14", {"start": v(-35.75, 22.9) * mm, "mid": v(-35.66, 22.87) * mm, "end": v(-35.56, 22.9) * mm});
            skArc(sketch, "E292.4.15", {"start": v(-36.6, 22.07) * mm, "mid": v(-36.56, 21.97) * mm, "end": v(-36.6, 21.88) * mm});
            skArc(sketch, "E292.5.0", {"start": v(-38.02, 20.64) * mm, "mid": v(-37.93, 20.5) * mm, "end": v(-37.82, 20.39) * mm});
            skArc(sketch, "E292.5.1", {"start": v(-38, 21.22) * mm, "mid": v(-38.1, 20.93) * mm, "end": v(-38.02, 20.64) * mm});
            skArc(sketch, "E292.5.2", {"start": v(-36.86, 20.46) * mm, "mid": v(-36.58, 20.85) * mm, "end": v(-36.28, 21.23) * mm});
            skPoint(sketch, "E292.5.3", {"position": v(-37.38, 20.8) * mm});
            skArc(sketch, "E292.5.4", {"start": v(-37.47, 21.47) * mm, "mid": v(-37.31, 21.43) * mm, "end": v(-37.16, 21.37) * mm});
            skLineSegment(sketch, "E292.5.5", {"start": v(-37.35, 19.63) * mm, "end": v(-37.93, 19.94) * mm});
            skArc(sketch, "E292.5.6", {"start": v(-36.98, 21.41) * mm, "mid": v(-36.88, 21.53) * mm, "end": v(-36.79, 21.65) * mm});
            skLineSegment(sketch, "E292.5.7", {"start": v(-36.28, 21.23) * mm, "end": v(-36.79, 21.65) * mm});
            skArc(sketch, "E292.5.8", {"start": v(-38, 21.22) * mm, "mid": v(-37.77, 21.42) * mm, "end": v(-37.47, 21.47) * mm});
            skPoint(sketch, "E292.5.9", {"position": v(-36.86, 20.46) * mm});
            skArc(sketch, "E292.5.10", {"start": v(-37.17, 20.67) * mm, "mid": v(-36.88, 21.08) * mm, "end": v(-36.57, 21.47) * mm, "construction": true});
            skArc(sketch, "E292.5.11", {"start": v(-36.86, 20.46) * mm, "mid": v(-37.11, 20.05) * mm, "end": v(-37.35, 19.63) * mm});
            skPoint(sketch, "E292.5.12", {"position": v(-37.17, 20.67) * mm});
            skArc(sketch, "E292.5.13", {"start": v(-37.79, 20.2) * mm, "mid": v(-37.86, 20.07) * mm, "end": v(-37.93, 19.94) * mm});
            skArc(sketch, "E292.5.14", {"start": v(-37.16, 21.37) * mm, "mid": v(-37.06, 21.36) * mm, "end": v(-36.98, 21.41) * mm});
            skArc(sketch, "E292.5.15", {"start": v(-37.82, 20.39) * mm, "mid": v(-37.77, 20.3) * mm, "end": v(-37.79, 20.2) * mm});
            skArc(sketch, "E292.6.0", {"start": v(-38.94, 18.7) * mm, "mid": v(-38.83, 18.6) * mm, "end": v(-38.7, 18.5) * mm});
            skArc(sketch, "E292.6.1", {"start": v(-39.04, 19.29) * mm, "mid": v(-39.07, 18.98) * mm, "end": v(-38.94, 18.7) * mm});
            skArc(sketch, "E292.6.2", {"start": v(-37.76, 18.76) * mm, "mid": v(-37.57, 19.2) * mm, "end": v(-37.35, 19.63) * mm});
            skPoint(sketch, "E292.6.3", {"position": v(-38.35, 19) * mm});
            skArc(sketch, "E292.6.4", {"start": v(-38.56, 19.63) * mm, "mid": v(-38.4, 19.63) * mm, "end": v(-38.24, 19.6) * mm});
            skLineSegment(sketch, "E292.6.5", {"start": v(-38.09, 17.85) * mm, "end": v(-38.72, 18.04) * mm});
            skArc(sketch, "E292.6.6", {"start": v(-38.07, 19.67) * mm, "mid": v(-38, 19.8) * mm, "end": v(-37.93, 19.94) * mm});
            skLineSegment(sketch, "E292.6.7", {"start": v(-37.35, 19.63) * mm, "end": v(-37.93, 19.94) * mm});
            skArc(sketch, "E292.6.8", {"start": v(-39.04, 19.29) * mm, "mid": v(-38.85, 19.53) * mm, "end": v(-38.56, 19.63) * mm});
            skPoint(sketch, "E292.6.9", {"position": v(-37.76, 18.76) * mm});
            skArc(sketch, "E292.6.10", {"start": v(-38.11, 18.9) * mm, "mid": v(-37.9, 19.36) * mm, "end": v(-37.68, 19.8) * mm, "construction": true});
            skArc(sketch, "E292.6.11", {"start": v(-37.76, 18.76) * mm, "mid": v(-37.94, 18.3) * mm, "end": v(-38.09, 17.85) * mm});
            skPoint(sketch, "E292.6.12", {"position": v(-38.11, 18.9) * mm});
            skArc(sketch, "E292.6.13", {"start": v(-38.63, 18.33) * mm, "mid": v(-38.67, 18.18) * mm, "end": v(-38.72, 18.04) * mm});
            skArc(sketch, "E292.6.14", {"start": v(-38.24, 19.6) * mm, "mid": v(-38.14, 19.6) * mm, "end": v(-38.07, 19.67) * mm});
            skArc(sketch, "E292.6.15", {"start": v(-38.7, 18.5) * mm, "mid": v(-38.63, 18.43) * mm, "end": v(-38.63, 18.33) * mm});
            skArc(sketch, "E292.7.0", {"start": v(-39.47, 16.64) * mm, "mid": v(-39.33, 16.55) * mm, "end": v(-39.18, 16.48) * mm});
            skArc(sketch, "E292.7.1", {"start": v(-39.68, 17.19) * mm, "mid": v(-39.65, 16.88) * mm, "end": v(-39.47, 16.64) * mm});
            skArc(sketch, "E292.7.2", {"start": v(-38.32, 16.92) * mm, "mid": v(-38.22, 17.39) * mm, "end": v(-38.09, 17.85) * mm});
            skPoint(sketch, "E292.7.3", {"position": v(-38.94, 17.04) * mm});
            skArc(sketch, "E292.7.4", {"start": v(-39.27, 17.61) * mm, "mid": v(-39.12, 17.64) * mm, "end": v(-38.95, 17.64) * mm});
            skLineSegment(sketch, "E292.7.5", {"start": v(-38.47, 15.96) * mm, "end": v(-39.12, 16.03) * mm});
            skArc(sketch, "E292.7.6", {"start": v(-38.8, 17.76) * mm, "mid": v(-38.76, 17.9) * mm, "end": v(-38.72, 18.04) * mm});
            skLineSegment(sketch, "E292.7.7", {"start": v(-38.09, 17.85) * mm, "end": v(-38.72, 18.04) * mm});
            skArc(sketch, "E292.7.8", {"start": v(-39.68, 17.19) * mm, "mid": v(-39.54, 17.46) * mm, "end": v(-39.27, 17.61) * mm});
            skPoint(sketch, "E292.7.9", {"position": v(-38.32, 16.92) * mm});
            skArc(sketch, "E292.7.10", {"start": v(-38.7, 16.99) * mm, "mid": v(-38.58, 17.48) * mm, "end": v(-38.45, 17.96) * mm, "construction": true});
            skArc(sketch, "E292.7.11", {"start": v(-38.32, 16.92) * mm, "mid": v(-38.4, 16.44) * mm, "end": v(-38.47, 15.96) * mm});
            skPoint(sketch, "E292.7.12", {"position": v(-38.7, 16.99) * mm});
            skArc(sketch, "E292.7.13", {"start": v(-39.08, 16.32) * mm, "mid": v(-39.1, 16.18) * mm, "end": v(-39.12, 16.03) * mm});
            skArc(sketch, "E292.7.14", {"start": v(-38.95, 17.64) * mm, "mid": v(-38.86, 17.67) * mm, "end": v(-38.8, 17.76) * mm});
            skArc(sketch, "E292.7.15", {"start": v(-39.18, 16.48) * mm, "mid": v(-39.1, 16.42) * mm, "end": v(-39.08, 16.32) * mm});
            skArc(sketch, "E292.8.0", {"start": v(-39.58, 14.5) * mm, "mid": v(-39.43, 14.44) * mm, "end": v(-39.27, 14.4) * mm});
            skArc(sketch, "E292.8.1", {"start": v(-39.9, 15) * mm, "mid": v(-39.8, 14.7) * mm, "end": v(-39.58, 14.5) * mm});
            skArc(sketch, "E292.8.2", {"start": v(-38.51, 15) * mm, "mid": v(-38.5, 15.48) * mm, "end": v(-38.47, 15.96) * mm});
            skPoint(sketch, "E292.8.3", {"position": v(-39.14, 15) * mm});
            skArc(sketch, "E292.8.4", {"start": v(-39.58, 15.5) * mm, "mid": v(-39.43, 15.56) * mm, "end": v(-39.27, 15.6) * mm});
            skLineSegment(sketch, "E292.8.5", {"start": v(-38.47, 14.04) * mm, "end": v(-39.12, 13.97) * mm});
            skArc(sketch, "E292.8.6", {"start": v(-39.14, 15.73) * mm, "mid": v(-39.13, 15.88) * mm, "end": v(-39.12, 16.03) * mm});
            skLineSegment(sketch, "E292.8.7", {"start": v(-38.47, 15.96) * mm, "end": v(-39.12, 16.03) * mm});
            skArc(sketch, "E292.8.8", {"start": v(-39.9, 15) * mm, "mid": v(-39.8, 15.3) * mm, "end": v(-39.58, 15.5) * mm});
            skPoint(sketch, "E292.8.9", {"position": v(-38.51, 15) * mm});
            skArc(sketch, "E292.8.10", {"start": v(-38.89, 15) * mm, "mid": v(-38.88, 15.5) * mm, "end": v(-38.84, 16) * mm, "construction": true});
            skArc(sketch, "E292.8.11", {"start": v(-38.51, 15) * mm, "mid": v(-38.5, 14.52) * mm, "end": v(-38.47, 14.04) * mm});
            skPoint(sketch, "E292.8.12", {"position": v(-38.89, 15) * mm});
            skArc(sketch, "E292.8.13", {"start": v(-39.14, 14.27) * mm, "mid": v(-39.13, 14.12) * mm, "end": v(-39.12, 13.97) * mm});
            skArc(sketch, "E292.8.14", {"start": v(-39.27, 15.6) * mm, "mid": v(-39.18, 15.64) * mm, "end": v(-39.14, 15.73) * mm});
            skArc(sketch, "E292.8.15", {"start": v(-39.27, 14.4) * mm, "mid": v(-39.18, 14.36) * mm, "end": v(-39.14, 14.27) * mm});
            skArc(sketch, "E292.9.0", {"start": v(-39.27, 12.39) * mm, "mid": v(-39.12, 12.36) * mm, "end": v(-38.95, 12.36) * mm});
            skArc(sketch, "E292.9.1", {"start": v(-39.68, 12.81) * mm, "mid": v(-39.54, 12.54) * mm, "end": v(-39.27, 12.39) * mm});
            skArc(sketch, "E292.9.2", {"start": v(-38.32, 13.08) * mm, "mid": v(-38.4, 13.56) * mm, "end": v(-38.47, 14.04) * mm});
            skPoint(sketch, "E292.9.3", {"position": v(-38.94, 12.96) * mm});
            skArc(sketch, "E292.9.4", {"start": v(-39.47, 13.36) * mm, "mid": v(-39.33, 13.45) * mm, "end": v(-39.18, 13.52) * mm});
            skLineSegment(sketch, "E292.9.5", {"start": v(-38.09, 12.15) * mm, "end": v(-38.72, 11.96) * mm});
            skArc(sketch, "E292.9.6", {"start": v(-39.08, 13.68) * mm, "mid": v(-39.1, 13.82) * mm, "end": v(-39.12, 13.97) * mm});
            skLineSegment(sketch, "E292.9.7", {"start": v(-38.47, 14.04) * mm, "end": v(-39.12, 13.97) * mm});
            skArc(sketch, "E292.9.8", {"start": v(-39.68, 12.81) * mm, "mid": v(-39.65, 13.12) * mm, "end": v(-39.47, 13.36) * mm});
            skPoint(sketch, "E292.9.9", {"position": v(-38.32, 13.08) * mm});
            skArc(sketch, "E292.9.10", {"start": v(-38.7, 13.01) * mm, "mid": v(-38.78, 13.5) * mm, "end": v(-38.84, 14) * mm, "construction": true});
            skArc(sketch, "E292.9.11", {"start": v(-38.32, 13.08) * mm, "mid": v(-38.22, 12.61) * mm, "end": v(-38.09, 12.15) * mm});
            skPoint(sketch, "E292.9.12", {"position": v(-38.7, 13.01) * mm});
            skArc(sketch, "E292.9.13", {"start": v(-38.8, 12.24) * mm, "mid": v(-38.76, 12.1) * mm, "end": v(-38.72, 11.96) * mm});
            skArc(sketch, "E292.9.14", {"start": v(-39.18, 13.52) * mm, "mid": v(-39.1, 13.58) * mm, "end": v(-39.08, 13.68) * mm});
            skArc(sketch, "E292.9.15", {"start": v(-38.95, 12.36) * mm, "mid": v(-38.86, 12.33) * mm, "end": v(-38.8, 12.24) * mm});
            skArc(sketch, "E292.10.0", {"start": v(-38.56, 10.37) * mm, "mid": v(-38.4, 10.37) * mm, "end": v(-38.24, 10.4) * mm});
            skArc(sketch, "E292.10.1", {"start": v(-39.04, 10.71) * mm, "mid": v(-38.85, 10.47) * mm, "end": v(-38.56, 10.37) * mm});
            skArc(sketch, "E292.10.2", {"start": v(-37.76, 11.24) * mm, "mid": v(-37.94, 11.7) * mm, "end": v(-38.09, 12.15) * mm});
            skPoint(sketch, "E292.10.3", {"position": v(-38.35, 11) * mm});
            skArc(sketch, "E292.10.4", {"start": v(-38.94, 11.3) * mm, "mid": v(-38.83, 11.4) * mm, "end": v(-38.7, 11.5) * mm});
            skLineSegment(sketch, "E292.10.5", {"start": v(-37.35, 10.37) * mm, "end": v(-37.93, 10.06) * mm});
            skArc(sketch, "E292.10.6", {"start": v(-38.63, 11.67) * mm, "mid": v(-38.67, 11.82) * mm, "end": v(-38.72, 11.96) * mm});
            skLineSegment(sketch, "E292.10.7", {"start": v(-38.09, 12.15) * mm, "end": v(-38.72, 11.96) * mm});
            skArc(sketch, "E292.10.8", {"start": v(-39.04, 10.71) * mm, "mid": v(-39.07, 11.02) * mm, "end": v(-38.94, 11.3) * mm});
            skPoint(sketch, "E292.10.9", {"position": v(-37.76, 11.24) * mm});
            skArc(sketch, "E292.10.10", {"start": v(-38.11, 11.1) * mm, "mid": v(-38.3, 11.56) * mm, "end": v(-38.45, 12.04) * mm, "construction": true});
            skArc(sketch, "E292.10.11", {"start": v(-37.76, 11.24) * mm, "mid": v(-37.57, 10.8) * mm, "end": v(-37.35, 10.37) * mm});
            skPoint(sketch, "E292.10.12", {"position": v(-38.11, 11.1) * mm});
            skArc(sketch, "E292.10.13", {"start": v(-38.07, 10.33) * mm, "mid": v(-38, 10.2) * mm, "end": v(-37.93, 10.06) * mm});
            skArc(sketch, "E292.10.14", {"start": v(-38.7, 11.5) * mm, "mid": v(-38.63, 11.57) * mm, "end": v(-38.63, 11.67) * mm});
            skArc(sketch, "E292.10.15", {"start": v(-38.24, 10.4) * mm, "mid": v(-38.14, 10.4) * mm, "end": v(-38.07, 10.33) * mm});
            skArc(sketch, "E292.11.0", {"start": v(-37.47, 8.53) * mm, "mid": v(-37.31, 8.57) * mm, "end": v(-37.16, 8.63) * mm});
            skArc(sketch, "E292.11.1", {"start": v(-38, 8.78) * mm, "mid": v(-37.77, 8.58) * mm, "end": v(-37.47, 8.53) * mm});
            skArc(sketch, "E292.11.2", {"start": v(-36.86, 9.54) * mm, "mid": v(-37.11, 9.95) * mm, "end": v(-37.35, 10.37) * mm});
            skPoint(sketch, "E292.11.3", {"position": v(-37.38, 9.2) * mm});
            skArc(sketch, "E292.11.4", {"start": v(-38.02, 9.36) * mm, "mid": v(-37.93, 9.5) * mm, "end": v(-37.82, 9.61) * mm});
            skLineSegment(sketch, "E292.11.5", {"start": v(-36.28, 8.77) * mm, "end": v(-36.79, 8.35) * mm});
            skArc(sketch, "E292.11.6", {"start": v(-37.79, 9.8) * mm, "mid": v(-37.86, 9.93) * mm, "end": v(-37.93, 10.06) * mm});
            skLineSegment(sketch, "E292.11.7", {"start": v(-37.35, 10.37) * mm, "end": v(-37.93, 10.06) * mm});
            skArc(sketch, "E292.11.8", {"start": v(-38, 8.78) * mm, "mid": v(-38.1, 9.07) * mm, "end": v(-38.02, 9.36) * mm});
            skPoint(sketch, "E292.11.9", {"position": v(-36.86, 9.54) * mm});
            skArc(sketch, "E292.11.10", {"start": v(-37.17, 9.33) * mm, "mid": v(-37.44, 9.76) * mm, "end": v(-37.68, 10.2) * mm, "construction": true});
            skArc(sketch, "E292.11.11", {"start": v(-36.86, 9.54) * mm, "mid": v(-36.58, 9.15) * mm, "end": v(-36.28, 8.77) * mm});
            skPoint(sketch, "E292.11.12", {"position": v(-37.17, 9.33) * mm});
            skArc(sketch, "E292.11.13", {"start": v(-36.98, 8.59) * mm, "mid": v(-36.88, 8.47) * mm, "end": v(-36.79, 8.35) * mm});
            skArc(sketch, "E292.11.14", {"start": v(-37.82, 9.61) * mm, "mid": v(-37.77, 9.7) * mm, "end": v(-37.79, 9.8) * mm});
            skArc(sketch, "E292.11.15", {"start": v(-37.16, 8.63) * mm, "mid": v(-37.06, 8.64) * mm, "end": v(-36.98, 8.59) * mm});
            skArc(sketch, "E292.12.0", {"start": v(-36.04, 6.95) * mm, "mid": v(-35.89, 7) * mm, "end": v(-35.75, 7.1) * mm});
            skArc(sketch, "E292.12.1", {"start": v(-36.61, 7.08) * mm, "mid": v(-36.34, 6.93) * mm, "end": v(-36.04, 6.95) * mm});
            skArc(sketch, "E292.12.2", {"start": v(-35.64, 8.05) * mm, "mid": v(-35.97, 8.4) * mm, "end": v(-36.28, 8.77) * mm});
            skPoint(sketch, "E292.12.3", {"position": v(-36.08, 7.6) * mm});
            skArc(sketch, "E292.12.4", {"start": v(-36.74, 7.65) * mm, "mid": v(-36.68, 7.8) * mm, "end": v(-36.6, 7.93) * mm});
            skLineSegment(sketch, "E292.12.5", {"start": v(-34.92, 7.4) * mm, "end": v(-35.34, 6.9) * mm});
            skArc(sketch, "E292.12.6", {"start": v(-36.6, 8.12) * mm, "mid": v(-36.7, 8.24) * mm, "end": v(-36.79, 8.35) * mm});
            skLineSegment(sketch, "E292.12.7", {"start": v(-36.28, 8.77) * mm, "end": v(-36.79, 8.35) * mm});
            skArc(sketch, "E292.12.8", {"start": v(-36.61, 7.08) * mm, "mid": v(-36.76, 7.35) * mm, "end": v(-36.74, 7.65) * mm});
            skPoint(sketch, "E292.12.9", {"position": v(-35.64, 8.05) * mm});
            skArc(sketch, "E292.12.10", {"start": v(-35.9, 7.79) * mm, "mid": v(-36.25, 8.15) * mm, "end": v(-36.57, 8.53) * mm, "construction": true});
            skArc(sketch, "E292.12.11", {"start": v(-35.64, 8.05) * mm, "mid": v(-35.29, 7.72) * mm, "end": v(-34.92, 7.4) * mm});
            skPoint(sketch, "E292.12.12", {"position": v(-35.9, 7.79) * mm});
            skArc(sketch, "E292.12.13", {"start": v(-35.56, 7.1) * mm, "mid": v(-35.45, 7) * mm, "end": v(-35.34, 6.9) * mm});
            skArc(sketch, "E292.12.14", {"start": v(-36.6, 7.93) * mm, "mid": v(-36.56, 8.03) * mm, "end": v(-36.6, 8.12) * mm});
            skArc(sketch, "E292.12.15", {"start": v(-35.75, 7.1) * mm, "mid": v(-35.66, 7.13) * mm, "end": v(-35.56, 7.1) * mm});
            skArc(sketch, "E292.13.0", {"start": v(-34.33, 5.67) * mm, "mid": v(-34.2, 5.76) * mm, "end": v(-34.08, 5.87) * mm});
            skArc(sketch, "E292.13.1", {"start": v(-34.91, 5.68) * mm, "mid": v(-34.62, 5.6) * mm, "end": v(-34.33, 5.67) * mm});
            skArc(sketch, "E292.13.2", {"start": v(-34.15, 6.83) * mm, "mid": v(-34.54, 7.1) * mm, "end": v(-34.92, 7.4) * mm});
            skPoint(sketch, "E292.13.3", {"position": v(-34.5, 6.3) * mm});
            skArc(sketch, "E292.13.4", {"start": v(-35.15, 6.22) * mm, "mid": v(-35.12, 6.38) * mm, "end": v(-35.06, 6.53) * mm});
            skLineSegment(sketch, "E292.13.5", {"start": v(-33.32, 6.34) * mm, "end": v(-33.63, 5.76) * mm});
            skArc(sketch, "E292.13.6", {"start": v(-35.1, 6.71) * mm, "mid": v(-35.22, 6.8) * mm, "end": v(-35.34, 6.9) * mm});
            skLineSegment(sketch, "E292.13.7", {"start": v(-34.92, 7.4) * mm, "end": v(-35.34, 6.9) * mm});
            skArc(sketch, "E292.13.8", {"start": v(-34.91, 5.68) * mm, "mid": v(-35.11, 5.92) * mm, "end": v(-35.15, 6.22) * mm});
            skPoint(sketch, "E292.13.9", {"position": v(-34.15, 6.83) * mm});
            skArc(sketch, "E292.13.10", {"start": v(-34.36, 6.52) * mm, "mid": v(-34.76, 6.8) * mm, "end": v(-35.16, 7.12) * mm, "construction": true});
            skArc(sketch, "E292.13.11", {"start": v(-34.15, 6.83) * mm, "mid": v(-33.74, 6.57) * mm, "end": v(-33.32, 6.34) * mm});
            skPoint(sketch, "E292.13.12", {"position": v(-34.36, 6.52) * mm});
            skArc(sketch, "E292.13.13", {"start": v(-33.89, 5.9) * mm, "mid": v(-33.76, 5.83) * mm, "end": v(-33.63, 5.76) * mm});
            skArc(sketch, "E292.13.14", {"start": v(-35.06, 6.53) * mm, "mid": v(-35.05, 6.63) * mm, "end": v(-35.1, 6.71) * mm});
            skArc(sketch, "E292.13.15", {"start": v(-34.08, 5.87) * mm, "mid": v(-33.99, 5.92) * mm, "end": v(-33.89, 5.9) * mm});
            skArc(sketch, "E292.14.0", {"start": v(-32.4, 4.75) * mm, "mid": v(-32.28, 4.86) * mm, "end": v(-32.2, 5) * mm});
            skArc(sketch, "E292.14.1", {"start": v(-32.98, 4.65) * mm, "mid": v(-32.67, 4.61) * mm, "end": v(-32.4, 4.75) * mm});
            skArc(sketch, "E292.14.2", {"start": v(-32.45, 5.92) * mm, "mid": v(-32.89, 6.12) * mm, "end": v(-33.32, 6.34) * mm});
            skPoint(sketch, "E292.14.3", {"position": v(-32.69, 5.34) * mm});
            skArc(sketch, "E292.14.4", {"start": v(-33.32, 5.13) * mm, "mid": v(-33.31, 5.29) * mm, "end": v(-33.29, 5.45) * mm});
            skLineSegment(sketch, "E292.14.5", {"start": v(-31.54, 5.6) * mm, "end": v(-31.73, 4.97) * mm});
            skArc(sketch, "E292.14.6", {"start": v(-33.36, 5.62) * mm, "mid": v(-33.5, 5.69) * mm, "end": v(-33.63, 5.76) * mm});
            skLineSegment(sketch, "E292.14.7", {"start": v(-33.32, 6.34) * mm, "end": v(-33.63, 5.76) * mm});
            skArc(sketch, "E292.14.8", {"start": v(-32.98, 4.65) * mm, "mid": v(-33.22, 4.84) * mm, "end": v(-33.32, 5.13) * mm});
            skPoint(sketch, "E292.14.9", {"position": v(-32.45, 5.92) * mm});
            skArc(sketch, "E292.14.10", {"start": v(-32.6, 5.58) * mm, "mid": v(-33.05, 5.78) * mm, "end": v(-33.5, 6) * mm, "construction": true});
            skArc(sketch, "E292.14.11", {"start": v(-32.45, 5.92) * mm, "mid": v(-32, 5.75) * mm, "end": v(-31.54, 5.6) * mm});
            skPoint(sketch, "E292.14.12", {"position": v(-32.6, 5.58) * mm});
            skArc(sketch, "E292.14.13", {"start": v(-32.01, 5.06) * mm, "mid": v(-31.87, 5.02) * mm, "end": v(-31.73, 4.97) * mm});
            skArc(sketch, "E292.14.14", {"start": v(-33.29, 5.45) * mm, "mid": v(-33.3, 5.55) * mm, "end": v(-33.36, 5.62) * mm});
            skArc(sketch, "E292.14.15", {"start": v(-32.2, 5) * mm, "mid": v(-32.12, 5.06) * mm, "end": v(-32.01, 5.06) * mm});
            skArc(sketch, "E292.15.0", {"start": v(-30.32, 4.22) * mm, "mid": v(-30.24, 4.36) * mm, "end": v(-30.17, 4.5) * mm});
            skArc(sketch, "E292.15.1", {"start": v(-30.87, 4.01) * mm, "mid": v(-30.57, 4.04) * mm, "end": v(-30.32, 4.22) * mm});
            skArc(sketch, "E292.15.2", {"start": v(-30.6, 5.36) * mm, "mid": v(-31.08, 5.47) * mm, "end": v(-31.54, 5.6) * mm});
            skPoint(sketch, "E292.15.3", {"position": v(-30.73, 4.75) * mm});
            skArc(sketch, "E292.15.4", {"start": v(-31.3, 4.41) * mm, "mid": v(-31.33, 4.57) * mm, "end": v(-31.33, 4.73) * mm});
            skLineSegment(sketch, "E292.15.5", {"start": v(-29.65, 5.22) * mm, "end": v(-29.72, 4.57) * mm});
            skArc(sketch, "E292.15.6", {"start": v(-31.44, 4.89) * mm, "mid": v(-31.59, 4.93) * mm, "end": v(-31.73, 4.97) * mm});
            skLineSegment(sketch, "E292.15.7", {"start": v(-31.54, 5.6) * mm, "end": v(-31.73, 4.97) * mm});
            skArc(sketch, "E292.15.8", {"start": v(-30.87, 4.01) * mm, "mid": v(-31.15, 4.15) * mm, "end": v(-31.3, 4.41) * mm});
            skPoint(sketch, "E292.15.9", {"position": v(-30.6, 5.36) * mm});
            skArc(sketch, "E292.15.10", {"start": v(-30.68, 5) * mm, "mid": v(-31.17, 5.1) * mm, "end": v(-31.65, 5.24) * mm, "construction": true});
            skArc(sketch, "E292.15.11", {"start": v(-30.6, 5.36) * mm, "mid": v(-30.13, 5.28) * mm, "end": v(-29.65, 5.22) * mm});
            skPoint(sketch, "E292.15.12", {"position": v(-30.68, 5) * mm});
            skArc(sketch, "E292.15.13", {"start": v(-30.01, 4.6) * mm, "mid": v(-29.86, 4.59) * mm, "end": v(-29.72, 4.57) * mm});
            skArc(sketch, "E292.15.14", {"start": v(-31.33, 4.73) * mm, "mid": v(-31.36, 4.83) * mm, "end": v(-31.44, 4.89) * mm});
            skArc(sketch, "E292.15.15", {"start": v(-30.17, 4.5) * mm, "mid": v(-30.11, 4.58) * mm, "end": v(-30.01, 4.6) * mm});
            skArc(sketch, "E292.16.0", {"start": v(-28.19, 4.1) * mm, "mid": v(-28.13, 4.26) * mm, "end": v(-28.1, 4.42) * mm});
            skArc(sketch, "E292.16.1", {"start": v(-28.69, 3.8) * mm, "mid": v(-28.4, 3.88) * mm, "end": v(-28.19, 4.1) * mm});
            skArc(sketch, "E292.16.2", {"start": v(-28.69, 5.18) * mm, "mid": v(-29.17, 5.19) * mm, "end": v(-29.65, 5.22) * mm});
            skPoint(sketch, "E292.16.3", {"position": v(-28.69, 4.55) * mm});
            skArc(sketch, "E292.16.4", {"start": v(-29.19, 4.1) * mm, "mid": v(-29.25, 4.26) * mm, "end": v(-29.28, 4.42) * mm});
            skLineSegment(sketch, "E292.16.5", {"start": v(-27.73, 5.22) * mm, "end": v(-27.66, 4.57) * mm});
            skArc(sketch, "E292.16.6", {"start": v(-29.42, 4.55) * mm, "mid": v(-29.57, 4.56) * mm, "end": v(-29.72, 4.57) * mm});
            skLineSegment(sketch, "E292.16.7", {"start": v(-29.65, 5.22) * mm, "end": v(-29.72, 4.57) * mm});
            skArc(sketch, "E292.16.8", {"start": v(-28.69, 3.8) * mm, "mid": v(-28.98, 3.88) * mm, "end": v(-29.19, 4.1) * mm});
            skPoint(sketch, "E292.16.9", {"position": v(-28.69, 5.18) * mm});
            skArc(sketch, "E292.16.10", {"start": v(-28.69, 4.8) * mm, "mid": v(-29.19, 4.81) * mm, "end": v(-29.69, 4.85) * mm, "construction": true});
            skArc(sketch, "E292.16.11", {"start": v(-28.69, 5.18) * mm, "mid": v(-28.2, 5.19) * mm, "end": v(-27.73, 5.22) * mm});
            skPoint(sketch, "E292.16.12", {"position": v(-28.69, 4.8) * mm});
            skArc(sketch, "E292.16.13", {"start": v(-27.96, 4.55) * mm, "mid": v(-27.8, 4.56) * mm, "end": v(-27.66, 4.57) * mm});
            skArc(sketch, "E292.16.14", {"start": v(-29.28, 4.42) * mm, "mid": v(-29.33, 4.5) * mm, "end": v(-29.42, 4.55) * mm});
            skArc(sketch, "E292.16.15", {"start": v(-28.1, 4.42) * mm, "mid": v(-28.05, 4.5) * mm, "end": v(-27.96, 4.55) * mm});
            skArc(sketch, "E292.17.0", {"start": v(-26.07, 4.41) * mm, "mid": v(-26.05, 4.57) * mm, "end": v(-26.04, 4.73) * mm});
            skArc(sketch, "E292.17.1", {"start": v(-26.5, 4.01) * mm, "mid": v(-26.23, 4.15) * mm, "end": v(-26.07, 4.41) * mm});
            skArc(sketch, "E292.17.2", {"start": v(-26.77, 5.36) * mm, "mid": v(-27.25, 5.28) * mm, "end": v(-27.73, 5.22) * mm});
            skPoint(sketch, "E292.17.3", {"position": v(-26.65, 4.75) * mm});
            skArc(sketch, "E292.17.4", {"start": v(-27.05, 4.22) * mm, "mid": v(-27.14, 4.36) * mm, "end": v(-27.2, 4.5) * mm});
            skLineSegment(sketch, "E292.17.5", {"start": v(-25.84, 5.6) * mm, "end": v(-25.65, 4.97) * mm});
            skArc(sketch, "E292.17.6", {"start": v(-27.36, 4.6) * mm, "mid": v(-27.51, 4.59) * mm, "end": v(-27.66, 4.57) * mm});
            skLineSegment(sketch, "E292.17.7", {"start": v(-27.73, 5.22) * mm, "end": v(-27.66, 4.57) * mm});
            skArc(sketch, "E292.17.8", {"start": v(-26.5, 4.01) * mm, "mid": v(-26.8, 4.04) * mm, "end": v(-27.05, 4.22) * mm});
            skPoint(sketch, "E292.17.9", {"position": v(-26.77, 5.36) * mm});
            skArc(sketch, "E292.17.10", {"start": v(-26.7, 5) * mm, "mid": v(-27.2, 4.91) * mm, "end": v(-27.69, 4.85) * mm, "construction": true});
            skArc(sketch, "E292.17.11", {"start": v(-26.77, 5.36) * mm, "mid": v(-26.3, 5.47) * mm, "end": v(-25.84, 5.6) * mm});
            skPoint(sketch, "E292.17.12", {"position": v(-26.7, 5) * mm});
            skArc(sketch, "E292.17.13", {"start": v(-25.93, 4.89) * mm, "mid": v(-25.79, 4.93) * mm, "end": v(-25.65, 4.97) * mm});
            skArc(sketch, "E292.17.14", {"start": v(-27.2, 4.5) * mm, "mid": v(-27.27, 4.58) * mm, "end": v(-27.36, 4.6) * mm});
            skArc(sketch, "E292.17.15", {"start": v(-26.04, 4.73) * mm, "mid": v(-26.02, 4.83) * mm, "end": v(-25.93, 4.89) * mm});
            skArc(sketch, "E292.18.0", {"start": v(-24.06, 5.13) * mm, "mid": v(-24.06, 5.29) * mm, "end": v(-24.1, 5.45) * mm});
            skArc(sketch, "E292.18.1", {"start": v(-24.4, 4.65) * mm, "mid": v(-24.16, 4.84) * mm, "end": v(-24.06, 5.13) * mm});
            skArc(sketch, "E292.18.2", {"start": v(-24.93, 5.92) * mm, "mid": v(-25.38, 5.75) * mm, "end": v(-25.84, 5.6) * mm});
            skPoint(sketch, "E292.18.3", {"position": v(-24.69, 5.34) * mm});
            skArc(sketch, "E292.18.4", {"start": v(-24.98, 4.75) * mm, "mid": v(-25.1, 4.86) * mm, "end": v(-25.18, 5) * mm});
            skLineSegment(sketch, "E292.18.5", {"start": v(-24.06, 6.34) * mm, "end": v(-23.75, 5.76) * mm});
            skArc(sketch, "E292.18.6", {"start": v(-25.36, 5.06) * mm, "mid": v(-25.5, 5.02) * mm, "end": v(-25.65, 4.97) * mm});
            skLineSegment(sketch, "E292.18.7", {"start": v(-25.84, 5.6) * mm, "end": v(-25.65, 4.97) * mm});
            skArc(sketch, "E292.18.8", {"start": v(-24.4, 4.65) * mm, "mid": v(-24.7, 4.61) * mm, "end": v(-24.98, 4.75) * mm});
            skPoint(sketch, "E292.18.9", {"position": v(-24.93, 5.92) * mm});
            skArc(sketch, "E292.18.10", {"start": v(-24.79, 5.58) * mm, "mid": v(-25.25, 5.4) * mm, "end": v(-25.73, 5.24) * mm, "construction": true});
            skArc(sketch, "E292.18.11", {"start": v(-24.93, 5.92) * mm, "mid": v(-24.49, 6.12) * mm, "end": v(-24.06, 6.34) * mm});
            skPoint(sketch, "E292.18.12", {"position": v(-24.79, 5.58) * mm});
            skArc(sketch, "E292.18.13", {"start": v(-24.01, 5.62) * mm, "mid": v(-23.88, 5.69) * mm, "end": v(-23.75, 5.76) * mm});
            skArc(sketch, "E292.18.14", {"start": v(-25.18, 5) * mm, "mid": v(-25.26, 5.06) * mm, "end": v(-25.36, 5.06) * mm});
            skArc(sketch, "E292.18.15", {"start": v(-24.1, 5.45) * mm, "mid": v(-24.08, 5.55) * mm, "end": v(-24.01, 5.62) * mm});
            skArc(sketch, "E292.19.0", {"start": v(-22.22, 6.22) * mm, "mid": v(-22.26, 6.38) * mm, "end": v(-22.32, 6.53) * mm});
            skArc(sketch, "E292.19.1", {"start": v(-22.46, 5.68) * mm, "mid": v(-22.27, 5.92) * mm, "end": v(-22.22, 6.22) * mm});
            skArc(sketch, "E292.19.2", {"start": v(-23.23, 6.83) * mm, "mid": v(-23.64, 6.57) * mm, "end": v(-24.06, 6.34) * mm});
            skPoint(sketch, "E292.19.3", {"position": v(-22.88, 6.3) * mm});
            skArc(sketch, "E292.19.4", {"start": v(-23.05, 5.67) * mm, "mid": v(-23.18, 5.76) * mm, "end": v(-23.3, 5.87) * mm});
            skLineSegment(sketch, "E292.19.5", {"start": v(-22.46, 7.4) * mm, "end": v(-22.04, 6.9) * mm});
            skArc(sketch, "E292.19.6", {"start": v(-23.49, 5.9) * mm, "mid": v(-23.62, 5.83) * mm, "end": v(-23.75, 5.76) * mm});
            skLineSegment(sketch, "E292.19.7", {"start": v(-24.06, 6.34) * mm, "end": v(-23.75, 5.76) * mm});
            skArc(sketch, "E292.19.8", {"start": v(-22.46, 5.68) * mm, "mid": v(-22.76, 5.6) * mm, "end": v(-23.05, 5.67) * mm});
            skPoint(sketch, "E292.19.9", {"position": v(-23.23, 6.83) * mm});
            skArc(sketch, "E292.19.10", {"start": v(-23.02, 6.52) * mm, "mid": v(-23.44, 6.25) * mm, "end": v(-23.88, 6) * mm, "construction": true});
            skArc(sketch, "E292.19.11", {"start": v(-23.23, 6.83) * mm, "mid": v(-22.84, 7.1) * mm, "end": v(-22.46, 7.4) * mm});
            skPoint(sketch, "E292.19.12", {"position": v(-23.02, 6.52) * mm});
            skArc(sketch, "E292.19.13", {"start": v(-22.27, 6.71) * mm, "mid": v(-22.16, 6.8) * mm, "end": v(-22.04, 6.9) * mm});
            skArc(sketch, "E292.19.14", {"start": v(-23.3, 5.87) * mm, "mid": v(-23.39, 5.92) * mm, "end": v(-23.49, 5.9) * mm});
            skArc(sketch, "E292.19.15", {"start": v(-22.32, 6.53) * mm, "mid": v(-22.33, 6.63) * mm, "end": v(-22.27, 6.71) * mm});
            skArc(sketch, "E292.20.0", {"start": v(-20.63, 7.65) * mm, "mid": v(-20.7, 7.8) * mm, "end": v(-20.79, 7.93) * mm});
            skArc(sketch, "E292.20.1", {"start": v(-20.77, 7.08) * mm, "mid": v(-20.62, 7.35) * mm, "end": v(-20.63, 7.65) * mm});
            skArc(sketch, "E292.20.2", {"start": v(-21.74, 8.05) * mm, "mid": v(-22.1, 7.72) * mm, "end": v(-22.46, 7.4) * mm});
            skPoint(sketch, "E292.20.3", {"position": v(-21.3, 7.6) * mm});
            skArc(sketch, "E292.20.4", {"start": v(-21.34, 6.95) * mm, "mid": v(-21.49, 7) * mm, "end": v(-21.62, 7.1) * mm});
            skLineSegment(sketch, "E292.20.5", {"start": v(-21.1, 8.77) * mm, "end": v(-20.59, 8.35) * mm});
            skArc(sketch, "E292.20.6", {"start": v(-21.81, 7.1) * mm, "mid": v(-21.93, 7) * mm, "end": v(-22.04, 6.9) * mm});
            skLineSegment(sketch, "E292.20.7", {"start": v(-22.46, 7.4) * mm, "end": v(-22.04, 6.9) * mm});
            skArc(sketch, "E292.20.8", {"start": v(-20.77, 7.08) * mm, "mid": v(-21.03, 6.93) * mm, "end": v(-21.34, 6.95) * mm});
            skPoint(sketch, "E292.20.9", {"position": v(-21.74, 8.05) * mm});
            skArc(sketch, "E292.20.10", {"start": v(-21.48, 7.79) * mm, "mid": v(-21.84, 7.44) * mm, "end": v(-22.22, 7.12) * mm, "construction": true});
            skArc(sketch, "E292.20.11", {"start": v(-21.74, 8.05) * mm, "mid": v(-21.4, 8.4) * mm, "end": v(-21.1, 8.77) * mm});
            skPoint(sketch, "E292.20.12", {"position": v(-21.48, 7.79) * mm});
            skArc(sketch, "E292.20.13", {"start": v(-20.78, 8.12) * mm, "mid": v(-20.68, 8.24) * mm, "end": v(-20.59, 8.35) * mm});
            skArc(sketch, "E292.20.14", {"start": v(-21.62, 7.1) * mm, "mid": v(-21.72, 7.13) * mm, "end": v(-21.81, 7.1) * mm});
            skArc(sketch, "E292.20.15", {"start": v(-20.79, 7.93) * mm, "mid": v(-20.82, 8.03) * mm, "end": v(-20.78, 8.12) * mm});
            skArc(sketch, "E292.21.0", {"start": v(-19.35, 9.36) * mm, "mid": v(-19.45, 9.5) * mm, "end": v(-19.56, 9.61) * mm});
            skArc(sketch, "E292.21.1", {"start": v(-19.37, 8.78) * mm, "mid": v(-19.28, 9.07) * mm, "end": v(-19.35, 9.36) * mm});
            skArc(sketch, "E292.21.2", {"start": v(-20.52, 9.54) * mm, "mid": v(-20.8, 9.15) * mm, "end": v(-21.1, 8.77) * mm});
            skPoint(sketch, "E292.21.3", {"position": v(-20, 9.2) * mm});
            skArc(sketch, "E292.21.4", {"start": v(-19.9, 8.53) * mm, "mid": v(-20.07, 8.57) * mm, "end": v(-20.22, 8.63) * mm});
            skLineSegment(sketch, "E292.21.5", {"start": v(-20.02, 10.37) * mm, "end": v(-19.45, 10.06) * mm});
            skArc(sketch, "E292.21.6", {"start": v(-20.4, 8.59) * mm, "mid": v(-20.5, 8.47) * mm, "end": v(-20.59, 8.35) * mm});
            skLineSegment(sketch, "E292.21.7", {"start": v(-21.1, 8.77) * mm, "end": v(-20.59, 8.35) * mm});
            skArc(sketch, "E292.21.8", {"start": v(-19.37, 8.78) * mm, "mid": v(-19.6, 8.58) * mm, "end": v(-19.9, 8.53) * mm});
            skPoint(sketch, "E292.21.9", {"position": v(-20.52, 9.54) * mm});
            skArc(sketch, "E292.21.10", {"start": v(-20.2, 9.33) * mm, "mid": v(-20.5, 8.92) * mm, "end": v(-20.8, 8.53) * mm, "construction": true});
            skArc(sketch, "E292.21.11", {"start": v(-20.52, 9.54) * mm, "mid": v(-20.26, 9.95) * mm, "end": v(-20.02, 10.37) * mm});
            skPoint(sketch, "E292.21.12", {"position": v(-20.2, 9.33) * mm});
            skArc(sketch, "E292.21.13", {"start": v(-19.6, 9.8) * mm, "mid": v(-19.52, 9.93) * mm, "end": v(-19.45, 10.06) * mm});
            skArc(sketch, "E292.21.14", {"start": v(-20.22, 8.63) * mm, "mid": v(-20.32, 8.64) * mm, "end": v(-20.4, 8.59) * mm});
            skArc(sketch, "E292.21.15", {"start": v(-19.56, 9.61) * mm, "mid": v(-19.6, 9.7) * mm, "end": v(-19.6, 9.8) * mm});
            skArc(sketch, "E292.22.0", {"start": v(-18.43, 11.3) * mm, "mid": v(-18.55, 11.4) * mm, "end": v(-18.68, 11.5) * mm});
            skArc(sketch, "E292.22.1", {"start": v(-18.34, 10.71) * mm, "mid": v(-18.3, 11.02) * mm, "end": v(-18.43, 11.3) * mm});
            skArc(sketch, "E292.22.2", {"start": v(-19.61, 11.24) * mm, "mid": v(-19.8, 10.8) * mm, "end": v(-20.02, 10.37) * mm});
            skPoint(sketch, "E292.22.3", {"position": v(-19.03, 11) * mm});
            skArc(sketch, "E292.22.4", {"start": v(-18.82, 10.37) * mm, "mid": v(-18.98, 10.37) * mm, "end": v(-19.14, 10.4) * mm});
            skLineSegment(sketch, "E292.22.5", {"start": v(-19.29, 12.15) * mm, "end": v(-18.66, 11.96) * mm});
            skArc(sketch, "E292.22.6", {"start": v(-19.3, 10.33) * mm, "mid": v(-19.38, 10.2) * mm, "end": v(-19.45, 10.06) * mm});
            skLineSegment(sketch, "E292.22.7", {"start": v(-20.02, 10.37) * mm, "end": v(-19.45, 10.06) * mm});
            skArc(sketch, "E292.22.8", {"start": v(-18.34, 10.71) * mm, "mid": v(-18.53, 10.47) * mm, "end": v(-18.82, 10.37) * mm});
            skPoint(sketch, "E292.22.9", {"position": v(-19.61, 11.24) * mm});
            skArc(sketch, "E292.22.10", {"start": v(-19.26, 11.1) * mm, "mid": v(-19.47, 10.64) * mm, "end": v(-19.7, 10.2) * mm, "construction": true});
            skArc(sketch, "E292.22.11", {"start": v(-19.61, 11.24) * mm, "mid": v(-19.44, 11.7) * mm, "end": v(-19.29, 12.15) * mm});
            skPoint(sketch, "E292.22.12", {"position": v(-19.26, 11.1) * mm});
            skArc(sketch, "E292.22.13", {"start": v(-18.75, 11.67) * mm, "mid": v(-18.7, 11.82) * mm, "end": v(-18.66, 11.96) * mm});
            skArc(sketch, "E292.22.14", {"start": v(-19.14, 10.4) * mm, "mid": v(-19.24, 10.4) * mm, "end": v(-19.3, 10.33) * mm});
            skArc(sketch, "E292.22.15", {"start": v(-18.68, 11.5) * mm, "mid": v(-18.75, 11.57) * mm, "end": v(-18.75, 11.67) * mm});
            skArc(sketch, "E292.23.0", {"start": v(-17.9, 13.36) * mm, "mid": v(-18.04, 13.45) * mm, "end": v(-18.2, 13.52) * mm});
            skArc(sketch, "E292.23.1", {"start": v(-17.7, 12.81) * mm, "mid": v(-17.73, 13.12) * mm, "end": v(-17.9, 13.36) * mm});
            skArc(sketch, "E292.23.2", {"start": v(-19.05, 13.08) * mm, "mid": v(-19.16, 12.61) * mm, "end": v(-19.29, 12.15) * mm});
            skPoint(sketch, "E292.23.3", {"position": v(-18.44, 12.96) * mm});
            skArc(sketch, "E292.23.4", {"start": v(-18.1, 12.39) * mm, "mid": v(-18.26, 12.36) * mm, "end": v(-18.42, 12.36) * mm});
            skLineSegment(sketch, "E292.23.5", {"start": v(-18.91, 14.04) * mm, "end": v(-18.26, 13.97) * mm});
            skArc(sketch, "E292.23.6", {"start": v(-18.58, 12.24) * mm, "mid": v(-18.62, 12.1) * mm, "end": v(-18.66, 11.96) * mm});
            skLineSegment(sketch, "E292.23.7", {"start": v(-19.29, 12.15) * mm, "end": v(-18.66, 11.96) * mm});
            skArc(sketch, "E292.23.8", {"start": v(-17.7, 12.81) * mm, "mid": v(-17.84, 12.54) * mm, "end": v(-18.1, 12.39) * mm});
            skPoint(sketch, "E292.23.9", {"position": v(-19.05, 13.08) * mm});
            skArc(sketch, "E292.23.10", {"start": v(-18.68, 13.01) * mm, "mid": v(-18.8, 12.52) * mm, "end": v(-18.93, 12.04) * mm, "construction": true});
            skArc(sketch, "E292.23.11", {"start": v(-19.05, 13.08) * mm, "mid": v(-18.97, 13.56) * mm, "end": v(-18.91, 14.04) * mm});
            skPoint(sketch, "E292.23.12", {"position": v(-18.68, 13.01) * mm});
            skArc(sketch, "E292.23.13", {"start": v(-18.3, 13.68) * mm, "mid": v(-18.28, 13.82) * mm, "end": v(-18.26, 13.97) * mm});
            skArc(sketch, "E292.23.14", {"start": v(-18.42, 12.36) * mm, "mid": v(-18.52, 12.33) * mm, "end": v(-18.58, 12.24) * mm});
            skArc(sketch, "E292.23.15", {"start": v(-18.2, 13.52) * mm, "mid": v(-18.27, 13.58) * mm, "end": v(-18.3, 13.68) * mm});
            skArc(sketch, "E292.24.0", {"start": v(-17.8, 15.5) * mm, "mid": v(-17.95, 15.56) * mm, "end": v(-18.1, 15.6) * mm});
            skArc(sketch, "E292.24.1", {"start": v(-17.48, 15) * mm, "mid": v(-17.57, 15.3) * mm, "end": v(-17.8, 15.5) * mm});
            skArc(sketch, "E292.24.2", {"start": v(-18.86, 15) * mm, "mid": v(-18.88, 14.52) * mm, "end": v(-18.91, 14.04) * mm});
            skPoint(sketch, "E292.24.3", {"position": v(-18.23, 15) * mm});
            skArc(sketch, "E292.24.4", {"start": v(-17.8, 14.5) * mm, "mid": v(-17.95, 14.44) * mm, "end": v(-18.1, 14.4) * mm});
            skLineSegment(sketch, "E292.24.5", {"start": v(-18.91, 15.96) * mm, "end": v(-18.26, 16.03) * mm});
            skArc(sketch, "E292.24.6", {"start": v(-18.23, 14.27) * mm, "mid": v(-18.25, 14.12) * mm, "end": v(-18.26, 13.97) * mm});
            skLineSegment(sketch, "E292.24.7", {"start": v(-18.91, 14.04) * mm, "end": v(-18.26, 13.97) * mm});
            skArc(sketch, "E292.24.8", {"start": v(-17.48, 15) * mm, "mid": v(-17.57, 14.7) * mm, "end": v(-17.8, 14.5) * mm});
            skPoint(sketch, "E292.24.9", {"position": v(-18.86, 15) * mm});
            skArc(sketch, "E292.24.10", {"start": v(-18.49, 15) * mm, "mid": v(-18.5, 14.5) * mm, "end": v(-18.54, 14) * mm, "construction": true});
            skArc(sketch, "E292.24.11", {"start": v(-18.86, 15) * mm, "mid": v(-18.88, 15.48) * mm, "end": v(-18.91, 15.96) * mm});
            skPoint(sketch, "E292.24.12", {"position": v(-18.49, 15) * mm});
            skArc(sketch, "E292.24.13", {"start": v(-18.23, 15.73) * mm, "mid": v(-18.25, 15.88) * mm, "end": v(-18.26, 16.03) * mm});
            skArc(sketch, "E292.24.14", {"start": v(-18.1, 14.4) * mm, "mid": v(-18.2, 14.36) * mm, "end": v(-18.23, 14.27) * mm});
            skArc(sketch, "E292.24.15", {"start": v(-18.1, 15.6) * mm, "mid": v(-18.2, 15.64) * mm, "end": v(-18.23, 15.73) * mm});
            skArc(sketch, "E292.25.0", {"start": v(-18.1, 17.61) * mm, "mid": v(-18.26, 17.64) * mm, "end": v(-18.42, 17.64) * mm});
            skArc(sketch, "E292.25.1", {"start": v(-17.7, 17.19) * mm, "mid": v(-17.84, 17.46) * mm, "end": v(-18.1, 17.61) * mm});
            skArc(sketch, "E292.25.2", {"start": v(-19.05, 16.92) * mm, "mid": v(-18.97, 16.44) * mm, "end": v(-18.91, 15.96) * mm});
            skPoint(sketch, "E292.25.3", {"position": v(-18.44, 17.04) * mm});
            skArc(sketch, "E292.25.4", {"start": v(-17.9, 16.64) * mm, "mid": v(-18.04, 16.55) * mm, "end": v(-18.2, 16.48) * mm});
            skLineSegment(sketch, "E292.25.5", {"start": v(-19.29, 17.85) * mm, "end": v(-18.66, 18.04) * mm});
            skArc(sketch, "E292.25.6", {"start": v(-18.3, 16.32) * mm, "mid": v(-18.28, 16.18) * mm, "end": v(-18.26, 16.03) * mm});
            skLineSegment(sketch, "E292.25.7", {"start": v(-18.91, 15.96) * mm, "end": v(-18.26, 16.03) * mm});
            skArc(sketch, "E292.25.8", {"start": v(-17.7, 17.19) * mm, "mid": v(-17.73, 16.88) * mm, "end": v(-17.9, 16.64) * mm});
            skPoint(sketch, "E292.25.9", {"position": v(-19.05, 16.92) * mm});
            skArc(sketch, "E292.25.10", {"start": v(-18.68, 16.99) * mm, "mid": v(-18.6, 16.5) * mm, "end": v(-18.54, 16) * mm, "construction": true});
            skArc(sketch, "E292.25.11", {"start": v(-19.05, 16.92) * mm, "mid": v(-19.16, 17.39) * mm, "end": v(-19.29, 17.85) * mm});
            skPoint(sketch, "E292.25.12", {"position": v(-18.68, 16.99) * mm});
            skArc(sketch, "E292.25.13", {"start": v(-18.58, 17.76) * mm, "mid": v(-18.62, 17.9) * mm, "end": v(-18.66, 18.04) * mm});
            skArc(sketch, "E292.25.14", {"start": v(-18.2, 16.48) * mm, "mid": v(-18.27, 16.42) * mm, "end": v(-18.3, 16.32) * mm});
            skArc(sketch, "E292.25.15", {"start": v(-18.42, 17.64) * mm, "mid": v(-18.52, 17.67) * mm, "end": v(-18.58, 17.76) * mm});
            skArc(sketch, "E292.26.0", {"start": v(-18.82, 19.63) * mm, "mid": v(-18.98, 19.63) * mm, "end": v(-19.14, 19.6) * mm});
            skArc(sketch, "E292.26.1", {"start": v(-18.34, 19.29) * mm, "mid": v(-18.53, 19.53) * mm, "end": v(-18.82, 19.63) * mm});
            skArc(sketch, "E292.26.2", {"start": v(-19.61, 18.76) * mm, "mid": v(-19.44, 18.3) * mm, "end": v(-19.29, 17.85) * mm});
            skPoint(sketch, "E292.26.3", {"position": v(-19.03, 19) * mm});
            skArc(sketch, "E292.26.4", {"start": v(-18.43, 18.7) * mm, "mid": v(-18.55, 18.6) * mm, "end": v(-18.68, 18.5) * mm});
            skLineSegment(sketch, "E292.26.5", {"start": v(-20.02, 19.63) * mm, "end": v(-19.45, 19.94) * mm});
            skArc(sketch, "E292.26.6", {"start": v(-18.75, 18.33) * mm, "mid": v(-18.7, 18.18) * mm, "end": v(-18.66, 18.04) * mm});
            skLineSegment(sketch, "E292.26.7", {"start": v(-19.29, 17.85) * mm, "end": v(-18.66, 18.04) * mm});
            skArc(sketch, "E292.26.8", {"start": v(-18.34, 19.29) * mm, "mid": v(-18.3, 18.98) * mm, "end": v(-18.43, 18.7) * mm});
            skPoint(sketch, "E292.26.9", {"position": v(-19.61, 18.76) * mm});
            skArc(sketch, "E292.26.10", {"start": v(-19.26, 18.9) * mm, "mid": v(-19.08, 18.44) * mm, "end": v(-18.93, 17.96) * mm, "construction": true});
            skArc(sketch, "E292.26.11", {"start": v(-19.61, 18.76) * mm, "mid": v(-19.8, 19.2) * mm, "end": v(-20.02, 19.63) * mm});
            skPoint(sketch, "E292.26.12", {"position": v(-19.26, 18.9) * mm});
            skArc(sketch, "E292.26.13", {"start": v(-19.3, 19.67) * mm, "mid": v(-19.38, 19.8) * mm, "end": v(-19.45, 19.94) * mm});
            skArc(sketch, "E292.26.14", {"start": v(-18.68, 18.5) * mm, "mid": v(-18.75, 18.43) * mm, "end": v(-18.75, 18.33) * mm});
            skArc(sketch, "E292.26.15", {"start": v(-19.14, 19.6) * mm, "mid": v(-19.24, 19.6) * mm, "end": v(-19.3, 19.67) * mm});
            skArc(sketch, "E292.27.0", {"start": v(-19.9, 21.47) * mm, "mid": v(-20.07, 21.43) * mm, "end": v(-20.22, 21.37) * mm});
            skArc(sketch, "E292.27.1", {"start": v(-19.37, 21.22) * mm, "mid": v(-19.6, 21.42) * mm, "end": v(-19.9, 21.47) * mm});
            skArc(sketch, "E292.27.2", {"start": v(-20.52, 20.46) * mm, "mid": v(-20.26, 20.05) * mm, "end": v(-20.02, 19.63) * mm});
            skPoint(sketch, "E292.27.3", {"position": v(-20, 20.8) * mm});
            skArc(sketch, "E292.27.4", {"start": v(-19.35, 20.64) * mm, "mid": v(-19.45, 20.5) * mm, "end": v(-19.56, 20.39) * mm});
            skLineSegment(sketch, "E292.27.5", {"start": v(-21.1, 21.23) * mm, "end": v(-20.59, 21.65) * mm});
            skArc(sketch, "E292.27.6", {"start": v(-19.6, 20.2) * mm, "mid": v(-19.52, 20.07) * mm, "end": v(-19.45, 19.94) * mm});
            skLineSegment(sketch, "E292.27.7", {"start": v(-20.02, 19.63) * mm, "end": v(-19.45, 19.94) * mm});
            skArc(sketch, "E292.27.8", {"start": v(-19.37, 21.22) * mm, "mid": v(-19.28, 20.93) * mm, "end": v(-19.35, 20.64) * mm});
            skPoint(sketch, "E292.27.9", {"position": v(-20.52, 20.46) * mm});
            skArc(sketch, "E292.27.10", {"start": v(-20.2, 20.67) * mm, "mid": v(-19.94, 20.24) * mm, "end": v(-19.7, 19.8) * mm, "construction": true});
            skArc(sketch, "E292.27.11", {"start": v(-20.52, 20.46) * mm, "mid": v(-20.8, 20.85) * mm, "end": v(-21.1, 21.23) * mm});
            skPoint(sketch, "E292.27.12", {"position": v(-20.2, 20.67) * mm});
            skArc(sketch, "E292.27.13", {"start": v(-20.4, 21.41) * mm, "mid": v(-20.5, 21.53) * mm, "end": v(-20.59, 21.65) * mm});
            skArc(sketch, "E292.27.14", {"start": v(-19.56, 20.39) * mm, "mid": v(-19.6, 20.3) * mm, "end": v(-19.6, 20.2) * mm});
            skArc(sketch, "E292.27.15", {"start": v(-20.22, 21.37) * mm, "mid": v(-20.32, 21.36) * mm, "end": v(-20.4, 21.41) * mm});
            skArc(sketch, "E292.28.0", {"start": v(-21.34, 23.05) * mm, "mid": v(-21.49, 23) * mm, "end": v(-21.62, 22.9) * mm});
            skArc(sketch, "E292.28.1", {"start": v(-20.77, 22.92) * mm, "mid": v(-21.03, 23.07) * mm, "end": v(-21.34, 23.05) * mm});
            skArc(sketch, "E292.28.2", {"start": v(-21.74, 21.95) * mm, "mid": v(-21.4, 21.6) * mm, "end": v(-21.1, 21.23) * mm});
            skPoint(sketch, "E292.28.3", {"position": v(-21.3, 22.4) * mm});
            skArc(sketch, "E292.28.4", {"start": v(-20.63, 22.35) * mm, "mid": v(-20.7, 22.2) * mm, "end": v(-20.79, 22.07) * mm});
            skLineSegment(sketch, "E292.28.5", {"start": v(-22.46, 22.6) * mm, "end": v(-22.04, 23.1) * mm});
            skArc(sketch, "E292.28.6", {"start": v(-20.78, 21.88) * mm, "mid": v(-20.68, 21.76) * mm, "end": v(-20.59, 21.65) * mm});
            skLineSegment(sketch, "E292.28.7", {"start": v(-21.1, 21.23) * mm, "end": v(-20.59, 21.65) * mm});
            skArc(sketch, "E292.28.8", {"start": v(-20.77, 22.92) * mm, "mid": v(-20.62, 22.65) * mm, "end": v(-20.63, 22.35) * mm});
            skPoint(sketch, "E292.28.9", {"position": v(-21.74, 21.95) * mm});
            skArc(sketch, "E292.28.10", {"start": v(-21.48, 22.21) * mm, "mid": v(-21.13, 21.85) * mm, "end": v(-20.8, 21.47) * mm, "construction": true});
            skArc(sketch, "E292.28.11", {"start": v(-21.74, 21.95) * mm, "mid": v(-22.1, 22.28) * mm, "end": v(-22.46, 22.6) * mm});
            skPoint(sketch, "E292.28.12", {"position": v(-21.48, 22.21) * mm});
            skArc(sketch, "E292.28.13", {"start": v(-21.81, 22.9) * mm, "mid": v(-21.93, 23) * mm, "end": v(-22.04, 23.1) * mm});
            skArc(sketch, "E292.28.14", {"start": v(-20.79, 22.07) * mm, "mid": v(-20.82, 21.97) * mm, "end": v(-20.78, 21.88) * mm});
            skArc(sketch, "E292.28.15", {"start": v(-21.62, 22.9) * mm, "mid": v(-21.72, 22.87) * mm, "end": v(-21.81, 22.9) * mm});
            skArc(sketch, "E292.29.0", {"start": v(-23.05, 24.33) * mm, "mid": v(-23.18, 24.24) * mm, "end": v(-23.3, 24.13) * mm});
            skArc(sketch, "E292.29.1", {"start": v(-22.46, 24.32) * mm, "mid": v(-22.76, 24.4) * mm, "end": v(-23.05, 24.33) * mm});
            skArc(sketch, "E292.29.2", {"start": v(-23.23, 23.17) * mm, "mid": v(-22.84, 22.9) * mm, "end": v(-22.46, 22.6) * mm});
            skPoint(sketch, "E292.29.3", {"position": v(-22.88, 23.7) * mm});
            skArc(sketch, "E292.29.4", {"start": v(-22.22, 23.78) * mm, "mid": v(-22.26, 23.62) * mm, "end": v(-22.32, 23.47) * mm});
            skLineSegment(sketch, "E292.29.5", {"start": v(-24.06, 23.66) * mm, "end": v(-23.75, 24.24) * mm});
            skArc(sketch, "E292.29.6", {"start": v(-22.27, 23.29) * mm, "mid": v(-22.16, 23.2) * mm, "end": v(-22.04, 23.1) * mm});
            skLineSegment(sketch, "E292.29.7", {"start": v(-22.46, 22.6) * mm, "end": v(-22.04, 23.1) * mm});
            skArc(sketch, "E292.29.8", {"start": v(-22.46, 24.32) * mm, "mid": v(-22.27, 24.08) * mm, "end": v(-22.22, 23.78) * mm});
            skPoint(sketch, "E292.29.9", {"position": v(-23.23, 23.17) * mm});
            skArc(sketch, "E292.29.10", {"start": v(-23.02, 23.48) * mm, "mid": v(-22.61, 23.2) * mm, "end": v(-22.22, 22.88) * mm, "construction": true});
            skArc(sketch, "E292.29.11", {"start": v(-23.23, 23.17) * mm, "mid": v(-23.64, 23.43) * mm, "end": v(-24.06, 23.66) * mm});
            skPoint(sketch, "E292.29.12", {"position": v(-23.02, 23.48) * mm});
            skArc(sketch, "E292.29.13", {"start": v(-23.49, 24.1) * mm, "mid": v(-23.62, 24.17) * mm, "end": v(-23.75, 24.24) * mm});
            skArc(sketch, "E292.29.14", {"start": v(-22.32, 23.47) * mm, "mid": v(-22.33, 23.37) * mm, "end": v(-22.27, 23.29) * mm});
            skArc(sketch, "E292.29.15", {"start": v(-23.3, 24.13) * mm, "mid": v(-23.39, 24.08) * mm, "end": v(-23.49, 24.1) * mm});
            skArc(sketch, "E292.30.0", {"start": v(-24.98, 25.25) * mm, "mid": v(-25.1, 25.14) * mm, "end": v(-25.18, 25) * mm});
            skArc(sketch, "E292.30.1", {"start": v(-24.4, 25.35) * mm, "mid": v(-24.7, 25.39) * mm, "end": v(-24.98, 25.25) * mm});
            skArc(sketch, "E292.30.2", {"start": v(-24.93, 24.08) * mm, "mid": v(-24.49, 23.88) * mm, "end": v(-24.06, 23.66) * mm});
            skPoint(sketch, "E292.30.3", {"position": v(-24.69, 24.66) * mm});
            skArc(sketch, "E292.30.4", {"start": v(-24.06, 24.87) * mm, "mid": v(-24.06, 24.71) * mm, "end": v(-24.1, 24.55) * mm});
            skLineSegment(sketch, "E292.30.5", {"start": v(-25.84, 24.4) * mm, "end": v(-25.65, 25.03) * mm});
            skArc(sketch, "E292.30.6", {"start": v(-24.01, 24.38) * mm, "mid": v(-23.88, 24.31) * mm, "end": v(-23.75, 24.24) * mm});
            skLineSegment(sketch, "E292.30.7", {"start": v(-24.06, 23.66) * mm, "end": v(-23.75, 24.24) * mm});
            skArc(sketch, "E292.30.8", {"start": v(-24.4, 25.35) * mm, "mid": v(-24.16, 25.16) * mm, "end": v(-24.06, 24.87) * mm});
            skPoint(sketch, "E292.30.9", {"position": v(-24.93, 24.08) * mm});
            skArc(sketch, "E292.30.10", {"start": v(-24.79, 24.42) * mm, "mid": v(-24.33, 24.22) * mm, "end": v(-23.88, 24) * mm, "construction": true});
            skArc(sketch, "E292.30.11", {"start": v(-24.93, 24.08) * mm, "mid": v(-25.38, 24.25) * mm, "end": v(-25.84, 24.4) * mm});
            skPoint(sketch, "E292.30.12", {"position": v(-24.79, 24.42) * mm});
            skArc(sketch, "E292.30.13", {"start": v(-25.36, 24.94) * mm, "mid": v(-25.5, 24.98) * mm, "end": v(-25.65, 25.03) * mm});
            skArc(sketch, "E292.30.14", {"start": v(-24.1, 24.55) * mm, "mid": v(-24.08, 24.45) * mm, "end": v(-24.01, 24.38) * mm});
            skArc(sketch, "E292.30.15", {"start": v(-25.18, 25) * mm, "mid": v(-25.26, 24.94) * mm, "end": v(-25.36, 24.94) * mm});
            skArc(sketch, "E292.31.0", {"start": v(-27.05, 25.78) * mm, "mid": v(-27.14, 25.64) * mm, "end": v(-27.2, 25.5) * mm});
            skArc(sketch, "E292.31.1", {"start": v(-26.5, 25.99) * mm, "mid": v(-26.8, 25.96) * mm, "end": v(-27.05, 25.78) * mm});
            skArc(sketch, "E292.31.2", {"start": v(-26.77, 24.64) * mm, "mid": v(-26.3, 24.53) * mm, "end": v(-25.84, 24.4) * mm});
            skPoint(sketch, "E292.31.3", {"position": v(-26.65, 25.25) * mm});
            skArc(sketch, "E292.31.4", {"start": v(-26.07, 25.59) * mm, "mid": v(-26.05, 25.43) * mm, "end": v(-26.04, 25.27) * mm});
            skArc(sketch, "E292.31.6", {"start": v(-25.93, 25.11) * mm, "mid": v(-25.79, 25.07) * mm, "end": v(-25.65, 25.03) * mm});
            skLineSegment(sketch, "E292.31.7", {"start": v(-25.84, 24.4) * mm, "end": v(-25.65, 25.03) * mm});
            skArc(sketch, "E292.31.8", {"start": v(-26.5, 25.99) * mm, "mid": v(-26.23, 25.85) * mm, "end": v(-26.07, 25.59) * mm});
            skPoint(sketch, "E292.31.9", {"position": v(-26.77, 24.64) * mm});
            skArc(sketch, "E292.31.10", {"start": v(-26.7, 25) * mm, "mid": v(-26.2, 24.9) * mm, "end": v(-25.73, 24.76) * mm, "construction": true});
            skArc(sketch, "E292.31.11", {"start": v(-26.77, 24.64) * mm, "mid": v(-27.25, 24.72) * mm, "end": v(-27.73, 24.78) * mm});
            skPoint(sketch, "E292.31.12", {"position": v(-26.7, 25) * mm});
            skArc(sketch, "E292.31.13", {"start": v(-27.36, 25.4) * mm, "mid": v(-27.51, 25.41) * mm, "end": v(-27.66, 25.43) * mm});
            skArc(sketch, "E292.31.14", {"start": v(-26.04, 25.27) * mm, "mid": v(-26.02, 25.17) * mm, "end": v(-25.93, 25.11) * mm});
            skArc(sketch, "E292.31.15", {"start": v(-27.2, 25.5) * mm, "mid": v(-27.27, 25.42) * mm, "end": v(-27.36, 25.4) * mm});
            skArc(sketch, "E293.0", {"start": v(-38.94, 15) * mm, "mid": v(-28.69, 4.75) * mm, "end": v(-18.44, 15) * mm});
            skSolve(sketch);
        }
        {
            var Q0;
            Q0 = qSketchRegion(id + "F47", true);
            extrude(context, id + "F48", {"entities" : qUnion([Q0]), "operationType" : NewBodyOperationType.REMOVE, "endBound" : BoundingType.SYMMETRIC, "oppositeDirection" : true, "depth" : 6.5 * mm});
        }
    });
